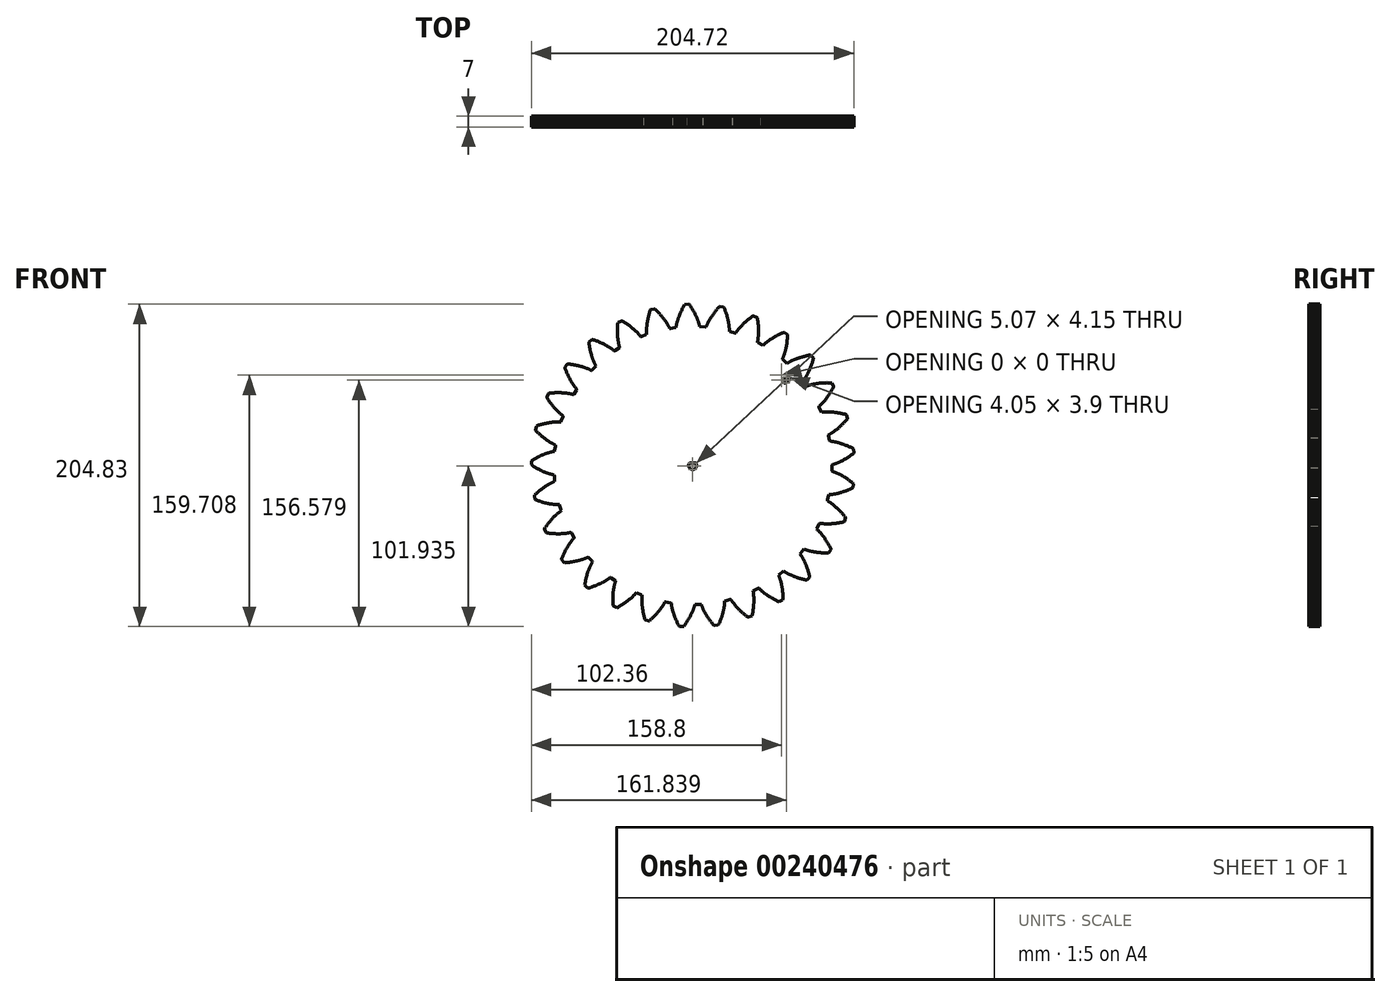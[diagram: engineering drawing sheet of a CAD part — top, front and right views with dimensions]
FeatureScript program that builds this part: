
annotation { "Feature Type Name" : "Feature", "Feature Type Description" : "" }
export const myFeature = defineFeature(function(context is Context, id is Id, definition is map)
    precondition{}
    {
        {
            var Q0;
            Q0=qCreatedBy(makeId("Front.planeOp"),FACE);
            var sketch = newSketch(context, id + "F0", { "sketchPlane" : qUnion([Q0])});
            skLineSegment(sketch, "E0", {"start": v(88.47, -0.08) * mm, "end": v(88.5, 0.43) * mm});
            skLineSegment(sketch, "E1", {"start": v(88.5, 0.43) * mm, "end": v(88.77, 0.5) * mm});
            skLineSegment(sketch, "E2", {"start": v(88.77, 0.5) * mm, "end": v(89.04, 0.58) * mm});
            skLineSegment(sketch, "E3", {"start": v(89.04, 0.58) * mm, "end": v(89.33, 0.67) * mm});
            skLineSegment(sketch, "E4", {"start": v(89.33, 0.67) * mm, "end": v(89.63, 0.76) * mm});
            skLineSegment(sketch, "E5", {"start": v(89.63, 0.76) * mm, "end": v(89.94, 0.86) * mm});
            skLineSegment(sketch, "E6", {"start": v(89.94, 0.86) * mm, "end": v(90.26, 0.97) * mm});
            skLineSegment(sketch, "E7", {"start": v(90.26, 0.97) * mm, "end": v(90.59, 1.09) * mm});
            skLineSegment(sketch, "E8", {"start": v(90.59, 1.09) * mm, "end": v(90.93, 1.21) * mm});
            skLineSegment(sketch, "E9", {"start": v(90.93, 1.21) * mm, "end": v(91.28, 1.35) * mm});
            skLineSegment(sketch, "E10", {"start": v(91.28, 1.35) * mm, "end": v(91.64, 1.5) * mm});
            skLineSegment(sketch, "E11", {"start": v(91.64, 1.5) * mm, "end": v(92, 1.64) * mm});
            skLineSegment(sketch, "E12", {"start": v(92, 1.64) * mm, "end": v(92.38, 1.8) * mm});
            skLineSegment(sketch, "E13", {"start": v(92.38, 1.8) * mm, "end": v(92.77, 1.97) * mm});
            skLineSegment(sketch, "E14", {"start": v(92.77, 1.97) * mm, "end": v(93.17, 2.15) * mm});
            skLineSegment(sketch, "E15", {"start": v(93.17, 2.15) * mm, "end": v(93.58, 2.34) * mm});
            skLineSegment(sketch, "E16", {"start": v(93.58, 2.34) * mm, "end": v(94, 2.54) * mm});
            skLineSegment(sketch, "E17", {"start": v(94, 2.54) * mm, "end": v(94.42, 2.75) * mm});
            skLineSegment(sketch, "E18", {"start": v(94.42, 2.75) * mm, "end": v(94.85, 2.97) * mm});
            skLineSegment(sketch, "E19", {"start": v(94.85, 2.97) * mm, "end": v(95.3, 3.2) * mm});
            skLineSegment(sketch, "E20", {"start": v(95.3, 3.2) * mm, "end": v(95.74, 3.45) * mm});
            skLineSegment(sketch, "E21", {"start": v(95.74, 3.45) * mm, "end": v(96.2, 3.7) * mm});
            skLineSegment(sketch, "E22", {"start": v(96.2, 3.7) * mm, "end": v(96.66, 3.97) * mm});
            skLineSegment(sketch, "E23", {"start": v(96.66, 3.97) * mm, "end": v(97.13, 4.25) * mm});
            skLineSegment(sketch, "E24", {"start": v(97.13, 4.25) * mm, "end": v(97.61, 4.54) * mm});
            skLineSegment(sketch, "E25", {"start": v(97.61, 4.54) * mm, "end": v(98.1, 4.84) * mm});
            skLineSegment(sketch, "E26", {"start": v(98.1, 4.84) * mm, "end": v(98.6, 5.16) * mm});
            skLineSegment(sketch, "E27", {"start": v(98.6, 5.16) * mm, "end": v(99.1, 5.48) * mm});
            skLineSegment(sketch, "E28", {"start": v(99.1, 5.48) * mm, "end": v(99.6, 5.82) * mm});
            skLineSegment(sketch, "E29", {"start": v(99.6, 5.82) * mm, "end": v(100.1, 6.18) * mm});
            skLineSegment(sketch, "E30", {"start": v(100.1, 6.18) * mm, "end": v(100.63, 6.55) * mm});
            skLineSegment(sketch, "E31", {"start": v(100.63, 6.55) * mm, "end": v(101.15, 6.93) * mm});
            skLineSegment(sketch, "E32", {"start": v(101.15, 6.93) * mm, "end": v(101.68, 7.32) * mm});
            skLineSegment(sketch, "E33", {"start": v(101.68, 7.32) * mm, "end": v(102.21, 7.73) * mm});
            skLineSegment(sketch, "E34", {"start": v(102.21, 7.73) * mm, "end": v(102.36, 8.12) * mm});
            skLineSegment(sketch, "E35", {"start": v(102.36, 8.12) * mm, "end": v(102.16, 10.37) * mm});
            skLineSegment(sketch, "E36", {"start": v(102.16, 10.37) * mm, "end": v(101.94, 10.72) * mm});
            skLineSegment(sketch, "E37", {"start": v(101.94, 10.72) * mm, "end": v(101.34, 11.03) * mm});
            skLineSegment(sketch, "E38", {"start": v(101.34, 11.03) * mm, "end": v(100.75, 11.32) * mm});
            skLineSegment(sketch, "E39", {"start": v(100.75, 11.32) * mm, "end": v(100.17, 11.6) * mm});
            skLineSegment(sketch, "E40", {"start": v(100.17, 11.6) * mm, "end": v(99.59, 11.87) * mm});
            skLineSegment(sketch, "E41", {"start": v(99.59, 11.87) * mm, "end": v(99.02, 12.12) * mm});
            skLineSegment(sketch, "E42", {"start": v(99.02, 12.12) * mm, "end": v(98.46, 12.37) * mm});
            skLineSegment(sketch, "E43", {"start": v(98.46, 12.37) * mm, "end": v(97.91, 12.6) * mm});
            skLineSegment(sketch, "E44", {"start": v(97.91, 12.6) * mm, "end": v(97.37, 12.82) * mm});
            skLineSegment(sketch, "E45", {"start": v(97.37, 12.82) * mm, "end": v(96.84, 13.03) * mm});
            skLineSegment(sketch, "E46", {"start": v(96.84, 13.03) * mm, "end": v(96.31, 13.23) * mm});
            skLineSegment(sketch, "E47", {"start": v(96.31, 13.23) * mm, "end": v(95.8, 13.42) * mm});
            skLineSegment(sketch, "E48", {"start": v(95.8, 13.42) * mm, "end": v(95.3, 13.6) * mm});
            skLineSegment(sketch, "E49", {"start": v(95.3, 13.6) * mm, "end": v(94.8, 13.76) * mm});
            skLineSegment(sketch, "E50", {"start": v(94.8, 13.76) * mm, "end": v(94.31, 13.92) * mm});
            skLineSegment(sketch, "E51", {"start": v(94.31, 13.92) * mm, "end": v(93.84, 14.07) * mm});
            skLineSegment(sketch, "E52", {"start": v(93.84, 14.07) * mm, "end": v(93.37, 14.2) * mm});
            skLineSegment(sketch, "E53", {"start": v(93.37, 14.2) * mm, "end": v(92.92, 14.34) * mm});
            skLineSegment(sketch, "E54", {"start": v(92.92, 14.34) * mm, "end": v(92.47, 14.46) * mm});
            skLineSegment(sketch, "E55", {"start": v(92.47, 14.46) * mm, "end": v(92.04, 14.57) * mm});
            skLineSegment(sketch, "E56", {"start": v(92.04, 14.57) * mm, "end": v(91.61, 14.68) * mm});
            skLineSegment(sketch, "E57", {"start": v(91.61, 14.68) * mm, "end": v(91.2, 14.77) * mm});
            skLineSegment(sketch, "E58", {"start": v(91.2, 14.77) * mm, "end": v(90.8, 14.86) * mm});
            skLineSegment(sketch, "E59", {"start": v(90.8, 14.86) * mm, "end": v(90.4, 14.94) * mm});
            skLineSegment(sketch, "E60", {"start": v(90.4, 14.94) * mm, "end": v(90.03, 15.02) * mm});
            skLineSegment(sketch, "E61", {"start": v(90.03, 15.02) * mm, "end": v(89.66, 15.09) * mm});
            skLineSegment(sketch, "E62", {"start": v(89.66, 15.09) * mm, "end": v(89.3, 15.15) * mm});
            skLineSegment(sketch, "E63", {"start": v(89.3, 15.15) * mm, "end": v(88.96, 15.2) * mm});
            skLineSegment(sketch, "E64", {"start": v(88.96, 15.2) * mm, "end": v(88.62, 15.25) * mm});
            skLineSegment(sketch, "E65", {"start": v(88.62, 15.25) * mm, "end": v(88.3, 15.3) * mm});
            skLineSegment(sketch, "E66", {"start": v(88.3, 15.3) * mm, "end": v(88, 15.33) * mm});
            skLineSegment(sketch, "E67", {"start": v(88, 15.33) * mm, "end": v(87.7, 15.37) * mm});
            skLineSegment(sketch, "E68", {"start": v(87.7, 15.37) * mm, "end": v(87.4, 15.4) * mm});
            skLineSegment(sketch, "E69", {"start": v(87.4, 15.4) * mm, "end": v(87.13, 15.42) * mm});
            skLineSegment(sketch, "E70", {"start": v(87.13, 15.42) * mm, "end": v(87, 15.91) * mm});
            skLineSegment(sketch, "E71", {"start": v(87, 15.91) * mm, "end": v(86.4, 18.9) * mm});
            skLineSegment(sketch, "E72", {"start": v(86.4, 18.9) * mm, "end": v(86.33, 19.4) * mm});
            skLineSegment(sketch, "E73", {"start": v(86.33, 19.4) * mm, "end": v(86.57, 19.54) * mm});
            skLineSegment(sketch, "E74", {"start": v(86.57, 19.54) * mm, "end": v(86.82, 19.68) * mm});
            skLineSegment(sketch, "E75", {"start": v(86.82, 19.68) * mm, "end": v(87.08, 19.82) * mm});
            skLineSegment(sketch, "E76", {"start": v(87.08, 19.82) * mm, "end": v(87.36, 19.98) * mm});
            skLineSegment(sketch, "E77", {"start": v(87.36, 19.98) * mm, "end": v(87.64, 20.14) * mm});
            skLineSegment(sketch, "E78", {"start": v(87.64, 20.14) * mm, "end": v(87.92, 20.32) * mm});
            skLineSegment(sketch, "E79", {"start": v(87.92, 20.32) * mm, "end": v(88.22, 20.5) * mm});
            skLineSegment(sketch, "E80", {"start": v(88.22, 20.5) * mm, "end": v(88.53, 20.7) * mm});
            skLineSegment(sketch, "E81", {"start": v(88.53, 20.7) * mm, "end": v(88.84, 20.9) * mm});
            skLineSegment(sketch, "E82", {"start": v(88.84, 20.9) * mm, "end": v(89.16, 21.12) * mm});
            skLineSegment(sketch, "E83", {"start": v(89.16, 21.12) * mm, "end": v(89.49, 21.35) * mm});
            skLineSegment(sketch, "E84", {"start": v(89.49, 21.35) * mm, "end": v(89.82, 21.58) * mm});
            skLineSegment(sketch, "E85", {"start": v(89.82, 21.58) * mm, "end": v(90.17, 21.83) * mm});
            skLineSegment(sketch, "E86", {"start": v(90.17, 21.83) * mm, "end": v(90.52, 22.1) * mm});
            skLineSegment(sketch, "E87", {"start": v(90.52, 22.1) * mm, "end": v(90.87, 22.37) * mm});
            skLineSegment(sketch, "E88", {"start": v(90.87, 22.37) * mm, "end": v(91.24, 22.65) * mm});
            skLineSegment(sketch, "E89", {"start": v(91.24, 22.65) * mm, "end": v(91.6, 22.95) * mm});
            skLineSegment(sketch, "E90", {"start": v(91.6, 22.95) * mm, "end": v(91.98, 23.26) * mm});
            skLineSegment(sketch, "E91", {"start": v(91.98, 23.26) * mm, "end": v(92.36, 23.58) * mm});
            skLineSegment(sketch, "E92", {"start": v(92.36, 23.58) * mm, "end": v(92.75, 23.91) * mm});
            skLineSegment(sketch, "E93", {"start": v(92.75, 23.91) * mm, "end": v(93.14, 24.26) * mm});
            skLineSegment(sketch, "E94", {"start": v(93.14, 24.26) * mm, "end": v(93.54, 24.62) * mm});
            skLineSegment(sketch, "E95", {"start": v(93.54, 24.62) * mm, "end": v(93.94, 25) * mm});
            skLineSegment(sketch, "E96", {"start": v(93.94, 25) * mm, "end": v(94.34, 25.38) * mm});
            skLineSegment(sketch, "E97", {"start": v(94.34, 25.38) * mm, "end": v(94.75, 25.78) * mm});
            skLineSegment(sketch, "E98", {"start": v(94.75, 25.78) * mm, "end": v(95.17, 26.2) * mm});
            skLineSegment(sketch, "E99", {"start": v(95.17, 26.2) * mm, "end": v(95.58, 26.62) * mm});
            skLineSegment(sketch, "E100", {"start": v(95.58, 26.62) * mm, "end": v(96, 27.06) * mm});
            skLineSegment(sketch, "E101", {"start": v(96, 27.06) * mm, "end": v(96.43, 27.52) * mm});
            skLineSegment(sketch, "E102", {"start": v(96.43, 27.52) * mm, "end": v(96.85, 27.99) * mm});
            skLineSegment(sketch, "E103", {"start": v(96.85, 27.99) * mm, "end": v(97.28, 28.47) * mm});
            skLineSegment(sketch, "E104", {"start": v(97.28, 28.47) * mm, "end": v(97.71, 28.97) * mm});
            skLineSegment(sketch, "E105", {"start": v(97.71, 28.97) * mm, "end": v(98.15, 29.48) * mm});
            skLineSegment(sketch, "E106", {"start": v(98.15, 29.48) * mm, "end": v(98.21, 29.9) * mm});
            skLineSegment(sketch, "E107", {"start": v(98.21, 29.9) * mm, "end": v(97.53, 32.05) * mm});
            skLineSegment(sketch, "E108", {"start": v(97.53, 32.05) * mm, "end": v(97.24, 32.35) * mm});
            skLineSegment(sketch, "E109", {"start": v(97.24, 32.35) * mm, "end": v(96.59, 32.52) * mm});
            skLineSegment(sketch, "E110", {"start": v(96.59, 32.52) * mm, "end": v(95.95, 32.68) * mm});
            skLineSegment(sketch, "E111", {"start": v(95.95, 32.68) * mm, "end": v(95.32, 32.82) * mm});
            skLineSegment(sketch, "E112", {"start": v(95.32, 32.82) * mm, "end": v(94.7, 32.96) * mm});
            skLineSegment(sketch, "E113", {"start": v(94.7, 32.96) * mm, "end": v(94.09, 33.1) * mm});
            skLineSegment(sketch, "E114", {"start": v(94.09, 33.1) * mm, "end": v(93.49, 33.2) * mm});
            skLineSegment(sketch, "E115", {"start": v(93.49, 33.2) * mm, "end": v(92.9, 33.31) * mm});
            skLineSegment(sketch, "E116", {"start": v(92.9, 33.31) * mm, "end": v(92.33, 33.41) * mm});
            skLineSegment(sketch, "E117", {"start": v(92.33, 33.41) * mm, "end": v(91.76, 33.5) * mm});
            skLineSegment(sketch, "E118", {"start": v(91.76, 33.5) * mm, "end": v(91.2, 33.59) * mm});
            skLineSegment(sketch, "E119", {"start": v(91.2, 33.59) * mm, "end": v(90.66, 33.66) * mm});
            skLineSegment(sketch, "E120", {"start": v(90.66, 33.66) * mm, "end": v(90.13, 33.72) * mm});
            skLineSegment(sketch, "E121", {"start": v(90.13, 33.72) * mm, "end": v(89.61, 33.78) * mm});
            skLineSegment(sketch, "E122", {"start": v(89.61, 33.78) * mm, "end": v(89.1, 33.83) * mm});
            skLineSegment(sketch, "E123", {"start": v(89.1, 33.83) * mm, "end": v(88.6, 33.87) * mm});
            skLineSegment(sketch, "E124", {"start": v(88.6, 33.87) * mm, "end": v(88.12, 33.91) * mm});
            skLineSegment(sketch, "E125", {"start": v(88.12, 33.91) * mm, "end": v(87.65, 33.94) * mm});
            skLineSegment(sketch, "E126", {"start": v(87.65, 33.94) * mm, "end": v(87.19, 33.96) * mm});
            skLineSegment(sketch, "E127", {"start": v(87.19, 33.96) * mm, "end": v(86.74, 33.98) * mm});
            skLineSegment(sketch, "E128", {"start": v(86.74, 33.98) * mm, "end": v(86.3, 33.99) * mm});
            skLineSegment(sketch, "E129", {"start": v(86.3, 33.99) * mm, "end": v(85.88, 34) * mm});
            skLineSegment(sketch, "E130", {"start": v(85.88, 34) * mm, "end": v(85.47, 34) * mm});
            skLineSegment(sketch, "E131", {"start": v(85.47, 34) * mm, "end": v(85.07, 34) * mm});
            skLineSegment(sketch, "E132", {"start": v(85.07, 34) * mm, "end": v(84.68, 33.98) * mm});
            skLineSegment(sketch, "E133", {"start": v(84.68, 33.98) * mm, "end": v(84.3, 33.97) * mm});
            skLineSegment(sketch, "E134", {"start": v(84.3, 33.97) * mm, "end": v(83.95, 33.95) * mm});
            skLineSegment(sketch, "E135", {"start": v(83.95, 33.95) * mm, "end": v(83.6, 33.93) * mm});
            skLineSegment(sketch, "E136", {"start": v(83.6, 33.93) * mm, "end": v(83.26, 33.91) * mm});
            skLineSegment(sketch, "E137", {"start": v(83.26, 33.91) * mm, "end": v(82.94, 33.88) * mm});
            skLineSegment(sketch, "E138", {"start": v(82.94, 33.88) * mm, "end": v(82.63, 33.85) * mm});
            skLineSegment(sketch, "E139", {"start": v(82.63, 33.85) * mm, "end": v(82.33, 33.82) * mm});
            skLineSegment(sketch, "E140", {"start": v(82.33, 33.82) * mm, "end": v(82.04, 33.79) * mm});
            skLineSegment(sketch, "E141", {"start": v(82.04, 33.79) * mm, "end": v(81.77, 33.75) * mm});
            skLineSegment(sketch, "E142", {"start": v(81.77, 33.75) * mm, "end": v(81.54, 34.2) * mm});
            skLineSegment(sketch, "E143", {"start": v(81.54, 34.2) * mm, "end": v(80.3, 37) * mm});
            skLineSegment(sketch, "E144", {"start": v(80.3, 37) * mm, "end": v(80.12, 37.48) * mm});
            skLineSegment(sketch, "E145", {"start": v(80.12, 37.48) * mm, "end": v(80.33, 37.65) * mm});
            skLineSegment(sketch, "E146", {"start": v(80.33, 37.65) * mm, "end": v(80.55, 37.84) * mm});
            skLineSegment(sketch, "E147", {"start": v(80.55, 37.84) * mm, "end": v(80.77, 38.04) * mm});
            skLineSegment(sketch, "E148", {"start": v(80.77, 38.04) * mm, "end": v(81, 38.25) * mm});
            skLineSegment(sketch, "E149", {"start": v(81, 38.25) * mm, "end": v(81.24, 38.47) * mm});
            skLineSegment(sketch, "E150", {"start": v(81.24, 38.47) * mm, "end": v(81.49, 38.7) * mm});
            skLineSegment(sketch, "E151", {"start": v(81.49, 38.7) * mm, "end": v(81.74, 38.95) * mm});
            skLineSegment(sketch, "E152", {"start": v(81.74, 38.95) * mm, "end": v(82, 39.2) * mm});
            skLineSegment(sketch, "E153", {"start": v(82, 39.2) * mm, "end": v(82.26, 39.47) * mm});
            skLineSegment(sketch, "E154", {"start": v(82.26, 39.47) * mm, "end": v(82.52, 39.75) * mm});
            skLineSegment(sketch, "E155", {"start": v(82.52, 39.75) * mm, "end": v(82.8, 40.05) * mm});
            skLineSegment(sketch, "E156", {"start": v(82.8, 40.05) * mm, "end": v(83.07, 40.35) * mm});
            skLineSegment(sketch, "E157", {"start": v(83.07, 40.35) * mm, "end": v(83.35, 40.67) * mm});
            skLineSegment(sketch, "E158", {"start": v(83.35, 40.67) * mm, "end": v(83.64, 41) * mm});
            skLineSegment(sketch, "E159", {"start": v(83.64, 41) * mm, "end": v(83.93, 41.34) * mm});
            skLineSegment(sketch, "E160", {"start": v(83.93, 41.34) * mm, "end": v(84.22, 41.7) * mm});
            skLineSegment(sketch, "E161", {"start": v(84.22, 41.7) * mm, "end": v(84.52, 42.07) * mm});
            skLineSegment(sketch, "E162", {"start": v(84.52, 42.07) * mm, "end": v(84.82, 42.45) * mm});
            skLineSegment(sketch, "E163", {"start": v(84.82, 42.45) * mm, "end": v(85.12, 42.85) * mm});
            skLineSegment(sketch, "E164", {"start": v(85.12, 42.85) * mm, "end": v(85.43, 43.25) * mm});
            skLineSegment(sketch, "E165", {"start": v(85.43, 43.25) * mm, "end": v(85.73, 43.68) * mm});
            skLineSegment(sketch, "E166", {"start": v(85.73, 43.68) * mm, "end": v(86.04, 44.11) * mm});
            skLineSegment(sketch, "E167", {"start": v(86.04, 44.11) * mm, "end": v(86.36, 44.57) * mm});
            skLineSegment(sketch, "E168", {"start": v(86.36, 44.57) * mm, "end": v(86.67, 45.03) * mm});
            skLineSegment(sketch, "E169", {"start": v(86.67, 45.03) * mm, "end": v(86.98, 45.5) * mm});
            skLineSegment(sketch, "E170", {"start": v(86.98, 45.5) * mm, "end": v(87.3, 46) * mm});
            skLineSegment(sketch, "E171", {"start": v(87.3, 46) * mm, "end": v(87.61, 46.5) * mm});
            skLineSegment(sketch, "E172", {"start": v(87.61, 46.5) * mm, "end": v(87.93, 47.03) * mm});
            skLineSegment(sketch, "E173", {"start": v(87.93, 47.03) * mm, "end": v(88.24, 47.57) * mm});
            skLineSegment(sketch, "E174", {"start": v(88.24, 47.57) * mm, "end": v(88.56, 48.12) * mm});
            skLineSegment(sketch, "E175", {"start": v(88.56, 48.12) * mm, "end": v(88.88, 48.68) * mm});
            skLineSegment(sketch, "E176", {"start": v(88.88, 48.68) * mm, "end": v(89.19, 49.26) * mm});
            skLineSegment(sketch, "E177", {"start": v(89.19, 49.26) * mm, "end": v(89.5, 49.86) * mm});
            skLineSegment(sketch, "E178", {"start": v(89.5, 49.86) * mm, "end": v(89.47, 50.27) * mm});
            skLineSegment(sketch, "E179", {"start": v(89.47, 50.27) * mm, "end": v(88.34, 52.23) * mm});
            skLineSegment(sketch, "E180", {"start": v(88.34, 52.23) * mm, "end": v(88, 52.46) * mm});
            skLineSegment(sketch, "E181", {"start": v(88, 52.46) * mm, "end": v(87.33, 52.48) * mm});
            skLineSegment(sketch, "E182", {"start": v(87.33, 52.48) * mm, "end": v(86.67, 52.5) * mm});
            skLineSegment(sketch, "E183", {"start": v(86.67, 52.5) * mm, "end": v(86.02, 52.51) * mm});
            skLineSegment(sketch, "E184", {"start": v(86.02, 52.51) * mm, "end": v(85.39, 52.51) * mm});
            skLineSegment(sketch, "E185", {"start": v(85.39, 52.51) * mm, "end": v(84.76, 52.5) * mm});
            skLineSegment(sketch, "E186", {"start": v(84.76, 52.5) * mm, "end": v(84.15, 52.5) * mm});
            skLineSegment(sketch, "E187", {"start": v(84.15, 52.5) * mm, "end": v(83.56, 52.47) * mm});
            skLineSegment(sketch, "E188", {"start": v(83.56, 52.47) * mm, "end": v(82.97, 52.44) * mm});
            skLineSegment(sketch, "E189", {"start": v(82.97, 52.44) * mm, "end": v(82.4, 52.41) * mm});
            skLineSegment(sketch, "E190", {"start": v(82.4, 52.41) * mm, "end": v(81.84, 52.37) * mm});
            skLineSegment(sketch, "E191", {"start": v(81.84, 52.37) * mm, "end": v(81.3, 52.32) * mm});
            skLineSegment(sketch, "E192", {"start": v(81.3, 52.32) * mm, "end": v(80.76, 52.27) * mm});
            skLineSegment(sketch, "E193", {"start": v(80.76, 52.27) * mm, "end": v(80.24, 52.22) * mm});
            skLineSegment(sketch, "E194", {"start": v(80.24, 52.22) * mm, "end": v(79.73, 52.16) * mm});
            skLineSegment(sketch, "E195", {"start": v(79.73, 52.16) * mm, "end": v(79.24, 52.1) * mm});
            skLineSegment(sketch, "E196", {"start": v(79.24, 52.1) * mm, "end": v(78.76, 52.02) * mm});
            skLineSegment(sketch, "E197", {"start": v(78.76, 52.02) * mm, "end": v(78.3, 51.95) * mm});
            skLineSegment(sketch, "E198", {"start": v(78.3, 51.95) * mm, "end": v(77.84, 51.87) * mm});
            skLineSegment(sketch, "E199", {"start": v(77.84, 51.87) * mm, "end": v(77.4, 51.8) * mm});
            skLineSegment(sketch, "E200", {"start": v(77.4, 51.8) * mm, "end": v(76.97, 51.71) * mm});
            skLineSegment(sketch, "E201", {"start": v(76.97, 51.71) * mm, "end": v(76.55, 51.63) * mm});
            skLineSegment(sketch, "E202", {"start": v(76.55, 51.63) * mm, "end": v(76.15, 51.54) * mm});
            skLineSegment(sketch, "E203", {"start": v(76.15, 51.54) * mm, "end": v(75.76, 51.45) * mm});
            skLineSegment(sketch, "E204", {"start": v(75.76, 51.45) * mm, "end": v(75.38, 51.36) * mm});
            skLineSegment(sketch, "E205", {"start": v(75.38, 51.36) * mm, "end": v(75.02, 51.26) * mm});
            skLineSegment(sketch, "E206", {"start": v(75.02, 51.26) * mm, "end": v(74.67, 51.17) * mm});
            skLineSegment(sketch, "E207", {"start": v(74.67, 51.17) * mm, "end": v(74.33, 51.07) * mm});
            skLineSegment(sketch, "E208", {"start": v(74.33, 51.07) * mm, "end": v(74.01, 50.98) * mm});
            skLineSegment(sketch, "E209", {"start": v(74.01, 50.98) * mm, "end": v(73.7, 50.88) * mm});
            skLineSegment(sketch, "E210", {"start": v(73.7, 50.88) * mm, "end": v(73.4, 50.79) * mm});
            skLineSegment(sketch, "E211", {"start": v(73.4, 50.79) * mm, "end": v(73.12, 50.7) * mm});
            skLineSegment(sketch, "E212", {"start": v(73.12, 50.7) * mm, "end": v(72.85, 50.6) * mm});
            skLineSegment(sketch, "E213", {"start": v(72.85, 50.6) * mm, "end": v(72.59, 50.5) * mm});
            skLineSegment(sketch, "E214", {"start": v(72.59, 50.5) * mm, "end": v(72.27, 50.9) * mm});
            skLineSegment(sketch, "E215", {"start": v(72.27, 50.9) * mm, "end": v(70.46, 53.36) * mm});
            skLineSegment(sketch, "E216", {"start": v(70.46, 53.36) * mm, "end": v(70.18, 53.79) * mm});
            skLineSegment(sketch, "E217", {"start": v(70.18, 53.79) * mm, "end": v(70.35, 54) * mm});
            skLineSegment(sketch, "E218", {"start": v(70.35, 54) * mm, "end": v(70.52, 54.24) * mm});
            skLineSegment(sketch, "E219", {"start": v(70.52, 54.24) * mm, "end": v(70.7, 54.48) * mm});
            skLineSegment(sketch, "E220", {"start": v(70.7, 54.48) * mm, "end": v(70.88, 54.73) * mm});
            skLineSegment(sketch, "E221", {"start": v(70.88, 54.73) * mm, "end": v(71.06, 55) * mm});
            skLineSegment(sketch, "E222", {"start": v(71.06, 55) * mm, "end": v(71.25, 55.28) * mm});
            skLineSegment(sketch, "E223", {"start": v(71.25, 55.28) * mm, "end": v(71.44, 55.57) * mm});
            skLineSegment(sketch, "E224", {"start": v(71.44, 55.57) * mm, "end": v(71.64, 55.88) * mm});
            skLineSegment(sketch, "E225", {"start": v(71.64, 55.88) * mm, "end": v(71.84, 56.2) * mm});
            skLineSegment(sketch, "E226", {"start": v(71.84, 56.2) * mm, "end": v(72.03, 56.53) * mm});
            skLineSegment(sketch, "E227", {"start": v(72.03, 56.53) * mm, "end": v(72.24, 56.87) * mm});
            skLineSegment(sketch, "E228", {"start": v(72.24, 56.87) * mm, "end": v(72.44, 57.23) * mm});
            skLineSegment(sketch, "E229", {"start": v(72.44, 57.23) * mm, "end": v(72.65, 57.6) * mm});
            skLineSegment(sketch, "E230", {"start": v(72.65, 57.6) * mm, "end": v(72.86, 57.98) * mm});
            skLineSegment(sketch, "E231", {"start": v(72.86, 57.98) * mm, "end": v(73.07, 58.38) * mm});
            skLineSegment(sketch, "E232", {"start": v(73.07, 58.38) * mm, "end": v(73.28, 58.8) * mm});
            skLineSegment(sketch, "E233", {"start": v(73.28, 58.8) * mm, "end": v(73.49, 59.21) * mm});
            skLineSegment(sketch, "E234", {"start": v(73.49, 59.21) * mm, "end": v(73.7, 59.65) * mm});
            skLineSegment(sketch, "E235", {"start": v(73.7, 59.65) * mm, "end": v(73.9, 60.1) * mm});
            skLineSegment(sketch, "E236", {"start": v(73.9, 60.1) * mm, "end": v(74.12, 60.57) * mm});
            skLineSegment(sketch, "E237", {"start": v(74.12, 60.57) * mm, "end": v(74.33, 61.05) * mm});
            skLineSegment(sketch, "E238", {"start": v(74.33, 61.05) * mm, "end": v(74.54, 61.54) * mm});
            skLineSegment(sketch, "E239", {"start": v(74.54, 61.54) * mm, "end": v(74.74, 62.05) * mm});
            skLineSegment(sketch, "E240", {"start": v(74.74, 62.05) * mm, "end": v(74.95, 62.57) * mm});
            skLineSegment(sketch, "E241", {"start": v(74.95, 62.57) * mm, "end": v(75.15, 63.1) * mm});
            skLineSegment(sketch, "E242", {"start": v(75.15, 63.1) * mm, "end": v(75.35, 63.66) * mm});
            skLineSegment(sketch, "E243", {"start": v(75.35, 63.66) * mm, "end": v(75.55, 64.22) * mm});
            skLineSegment(sketch, "E244", {"start": v(75.55, 64.22) * mm, "end": v(75.75, 64.8) * mm});
            skLineSegment(sketch, "E245", {"start": v(75.75, 64.8) * mm, "end": v(75.94, 65.39) * mm});
            skLineSegment(sketch, "E246", {"start": v(75.94, 65.39) * mm, "end": v(76.13, 66) * mm});
            skLineSegment(sketch, "E247", {"start": v(76.13, 66) * mm, "end": v(76.32, 66.61) * mm});
            skLineSegment(sketch, "E248", {"start": v(76.32, 66.61) * mm, "end": v(76.5, 67.24) * mm});
            skLineSegment(sketch, "E249", {"start": v(76.5, 67.24) * mm, "end": v(76.68, 67.9) * mm});
            skLineSegment(sketch, "E250", {"start": v(76.68, 67.9) * mm, "end": v(76.56, 68.3) * mm});
            skLineSegment(sketch, "E251", {"start": v(76.56, 68.3) * mm, "end": v(75.04, 69.96) * mm});
            skLineSegment(sketch, "E252", {"start": v(75.04, 69.96) * mm, "end": v(74.65, 70.11) * mm});
            skLineSegment(sketch, "E253", {"start": v(74.65, 70.11) * mm, "end": v(73.99, 70) * mm});
            skLineSegment(sketch, "E254", {"start": v(73.99, 70) * mm, "end": v(73.34, 69.87) * mm});
            skLineSegment(sketch, "E255", {"start": v(73.34, 69.87) * mm, "end": v(72.7, 69.74) * mm});
            skLineSegment(sketch, "E256", {"start": v(72.7, 69.74) * mm, "end": v(72.09, 69.6) * mm});
            skLineSegment(sketch, "E257", {"start": v(72.09, 69.6) * mm, "end": v(71.48, 69.46) * mm});
            skLineSegment(sketch, "E258", {"start": v(71.48, 69.46) * mm, "end": v(70.89, 69.32) * mm});
            skLineSegment(sketch, "E259", {"start": v(70.89, 69.32) * mm, "end": v(70.3, 69.17) * mm});
            skLineSegment(sketch, "E260", {"start": v(70.3, 69.17) * mm, "end": v(69.74, 69.02) * mm});
            skLineSegment(sketch, "E261", {"start": v(69.74, 69.02) * mm, "end": v(69.2, 68.86) * mm});
            skLineSegment(sketch, "E262", {"start": v(69.2, 68.86) * mm, "end": v(68.66, 68.7) * mm});
            skLineSegment(sketch, "E263", {"start": v(68.66, 68.7) * mm, "end": v(68.13, 68.54) * mm});
            skLineSegment(sketch, "E264", {"start": v(68.13, 68.54) * mm, "end": v(67.62, 68.38) * mm});
            skLineSegment(sketch, "E265", {"start": v(67.62, 68.38) * mm, "end": v(67.13, 68.21) * mm});
            skLineSegment(sketch, "E266", {"start": v(67.13, 68.21) * mm, "end": v(66.65, 68.04) * mm});
            skLineSegment(sketch, "E267", {"start": v(66.65, 68.04) * mm, "end": v(66.18, 67.87) * mm});
            skLineSegment(sketch, "E268", {"start": v(66.18, 67.87) * mm, "end": v(65.72, 67.7) * mm});
            skLineSegment(sketch, "E269", {"start": v(65.72, 67.7) * mm, "end": v(65.28, 67.53) * mm});
            skLineSegment(sketch, "E270", {"start": v(65.28, 67.53) * mm, "end": v(64.85, 67.36) * mm});
            skLineSegment(sketch, "E271", {"start": v(64.85, 67.36) * mm, "end": v(64.44, 67.18) * mm});
            skLineSegment(sketch, "E272", {"start": v(64.44, 67.18) * mm, "end": v(64.04, 67.01) * mm});
            skLineSegment(sketch, "E273", {"start": v(64.04, 67.01) * mm, "end": v(63.65, 66.84) * mm});
            skLineSegment(sketch, "E274", {"start": v(63.65, 66.84) * mm, "end": v(63.28, 66.67) * mm});
            skLineSegment(sketch, "E275", {"start": v(63.28, 66.67) * mm, "end": v(62.92, 66.5) * mm});
            skLineSegment(sketch, "E276", {"start": v(62.92, 66.5) * mm, "end": v(62.57, 66.32) * mm});
            skLineSegment(sketch, "E277", {"start": v(62.57, 66.32) * mm, "end": v(62.23, 66.15) * mm});
            skLineSegment(sketch, "E278", {"start": v(62.23, 66.15) * mm, "end": v(61.91, 65.99) * mm});
            skLineSegment(sketch, "E279", {"start": v(61.91, 65.99) * mm, "end": v(61.6, 65.82) * mm});
            skLineSegment(sketch, "E280", {"start": v(61.6, 65.82) * mm, "end": v(61.3, 65.66) * mm});
            skLineSegment(sketch, "E281", {"start": v(61.3, 65.66) * mm, "end": v(61.03, 65.5) * mm});
            skLineSegment(sketch, "E282", {"start": v(61.03, 65.5) * mm, "end": v(60.76, 65.34) * mm});
            skLineSegment(sketch, "E283", {"start": v(60.76, 65.34) * mm, "end": v(60.5, 65.19) * mm});
            skLineSegment(sketch, "E284", {"start": v(60.5, 65.19) * mm, "end": v(60.25, 65.04) * mm});
            skLineSegment(sketch, "E285", {"start": v(60.25, 65.04) * mm, "end": v(60.02, 64.89) * mm});
            skLineSegment(sketch, "E286", {"start": v(60.02, 64.89) * mm, "end": v(59.63, 65.2) * mm});
            skLineSegment(sketch, "E287", {"start": v(59.63, 65.2) * mm, "end": v(57.33, 67.23) * mm});
            skLineSegment(sketch, "E288", {"start": v(57.33, 67.23) * mm, "end": v(56.96, 67.58) * mm});
            skLineSegment(sketch, "E289", {"start": v(56.96, 67.58) * mm, "end": v(57.08, 67.83) * mm});
            skLineSegment(sketch, "E290", {"start": v(57.08, 67.83) * mm, "end": v(57.2, 68.1) * mm});
            skLineSegment(sketch, "E291", {"start": v(57.2, 68.1) * mm, "end": v(57.32, 68.37) * mm});
            skLineSegment(sketch, "E292", {"start": v(57.32, 68.37) * mm, "end": v(57.44, 68.65) * mm});
            skLineSegment(sketch, "E293", {"start": v(57.44, 68.65) * mm, "end": v(57.56, 68.96) * mm});
            skLineSegment(sketch, "E294", {"start": v(57.56, 68.96) * mm, "end": v(57.69, 69.27) * mm});
            skLineSegment(sketch, "E295", {"start": v(57.69, 69.27) * mm, "end": v(57.81, 69.6) * mm});
            skLineSegment(sketch, "E296", {"start": v(57.81, 69.6) * mm, "end": v(57.94, 69.93) * mm});
            skLineSegment(sketch, "E297", {"start": v(57.94, 69.93) * mm, "end": v(58.06, 70.29) * mm});
            skLineSegment(sketch, "E298", {"start": v(58.06, 70.29) * mm, "end": v(58.19, 70.65) * mm});
            skLineSegment(sketch, "E299", {"start": v(58.19, 70.65) * mm, "end": v(58.31, 71.03) * mm});
            skLineSegment(sketch, "E300", {"start": v(58.31, 71.03) * mm, "end": v(58.43, 71.43) * mm});
            skLineSegment(sketch, "E301", {"start": v(58.43, 71.43) * mm, "end": v(58.56, 71.83) * mm});
            skLineSegment(sketch, "E302", {"start": v(58.56, 71.83) * mm, "end": v(58.68, 72.25) * mm});
            skLineSegment(sketch, "E303", {"start": v(58.68, 72.25) * mm, "end": v(58.8, 72.69) * mm});
            skLineSegment(sketch, "E304", {"start": v(58.8, 72.69) * mm, "end": v(58.91, 73.13) * mm});
            skLineSegment(sketch, "E305", {"start": v(58.91, 73.13) * mm, "end": v(59.03, 73.6) * mm});
            skLineSegment(sketch, "E306", {"start": v(59.03, 73.6) * mm, "end": v(59.14, 74.06) * mm});
            skLineSegment(sketch, "E307", {"start": v(59.14, 74.06) * mm, "end": v(59.25, 74.55) * mm});
            skLineSegment(sketch, "E308", {"start": v(59.25, 74.55) * mm, "end": v(59.35, 75.05) * mm});
            skLineSegment(sketch, "E309", {"start": v(59.35, 75.05) * mm, "end": v(59.45, 75.56) * mm});
            skLineSegment(sketch, "E310", {"start": v(59.45, 75.56) * mm, "end": v(59.55, 76.1) * mm});
            skLineSegment(sketch, "E311", {"start": v(59.55, 76.1) * mm, "end": v(59.64, 76.63) * mm});
            skLineSegment(sketch, "E312", {"start": v(59.64, 76.63) * mm, "end": v(59.73, 77.18) * mm});
            skLineSegment(sketch, "E313", {"start": v(59.73, 77.18) * mm, "end": v(59.82, 77.75) * mm});
            skLineSegment(sketch, "E314", {"start": v(59.82, 77.75) * mm, "end": v(59.9, 78.33) * mm});
            skLineSegment(sketch, "E315", {"start": v(59.9, 78.33) * mm, "end": v(59.97, 78.92) * mm});
            skLineSegment(sketch, "E316", {"start": v(59.97, 78.92) * mm, "end": v(60.04, 79.53) * mm});
            skLineSegment(sketch, "E317", {"start": v(60.04, 79.53) * mm, "end": v(60.1, 80.15) * mm});
            skLineSegment(sketch, "E318", {"start": v(60.1, 80.15) * mm, "end": v(60.15, 80.78) * mm});
            skLineSegment(sketch, "E319", {"start": v(60.15, 80.78) * mm, "end": v(60.2, 81.42) * mm});
            skLineSegment(sketch, "E320", {"start": v(60.2, 81.42) * mm, "end": v(60.25, 82.08) * mm});
            skLineSegment(sketch, "E321", {"start": v(60.25, 82.08) * mm, "end": v(60.28, 82.75) * mm});
            skLineSegment(sketch, "E322", {"start": v(60.28, 82.75) * mm, "end": v(60.08, 83.12) * mm});
            skLineSegment(sketch, "E323", {"start": v(60.08, 83.12) * mm, "end": v(58.23, 84.42) * mm});
            skLineSegment(sketch, "E324", {"start": v(58.23, 84.42) * mm, "end": v(57.82, 84.48) * mm});
            skLineSegment(sketch, "E325", {"start": v(57.82, 84.48) * mm, "end": v(57.2, 84.23) * mm});
            skLineSegment(sketch, "E326", {"start": v(57.2, 84.23) * mm, "end": v(56.6, 83.96) * mm});
            skLineSegment(sketch, "E327", {"start": v(56.6, 83.96) * mm, "end": v(56, 83.7) * mm});
            skLineSegment(sketch, "E328", {"start": v(56, 83.7) * mm, "end": v(55.43, 83.44) * mm});
            skLineSegment(sketch, "E329", {"start": v(55.43, 83.44) * mm, "end": v(54.86, 83.17) * mm});
            skLineSegment(sketch, "E330", {"start": v(54.86, 83.17) * mm, "end": v(54.32, 82.9) * mm});
            skLineSegment(sketch, "E331", {"start": v(54.32, 82.9) * mm, "end": v(53.78, 82.63) * mm});
            skLineSegment(sketch, "E332", {"start": v(53.78, 82.63) * mm, "end": v(53.27, 82.36) * mm});
            skLineSegment(sketch, "E333", {"start": v(53.27, 82.36) * mm, "end": v(52.76, 82.09) * mm});
            skLineSegment(sketch, "E334", {"start": v(52.76, 82.09) * mm, "end": v(52.27, 81.82) * mm});
            skLineSegment(sketch, "E335", {"start": v(52.27, 81.82) * mm, "end": v(51.8, 81.55) * mm});
            skLineSegment(sketch, "E336", {"start": v(51.8, 81.55) * mm, "end": v(51.33, 81.28) * mm});
            skLineSegment(sketch, "E337", {"start": v(51.33, 81.28) * mm, "end": v(50.88, 81) * mm});
            skLineSegment(sketch, "E338", {"start": v(50.88, 81) * mm, "end": v(50.45, 80.74) * mm});
            skLineSegment(sketch, "E339", {"start": v(50.45, 80.74) * mm, "end": v(50.03, 80.48) * mm});
            skLineSegment(sketch, "E340", {"start": v(50.03, 80.48) * mm, "end": v(49.62, 80.21) * mm});
            skLineSegment(sketch, "E341", {"start": v(49.62, 80.21) * mm, "end": v(49.23, 79.95) * mm});
            skLineSegment(sketch, "E342", {"start": v(49.23, 79.95) * mm, "end": v(48.84, 79.69) * mm});
            skLineSegment(sketch, "E343", {"start": v(48.84, 79.69) * mm, "end": v(48.48, 79.43) * mm});
            skLineSegment(sketch, "E344", {"start": v(48.48, 79.43) * mm, "end": v(48.12, 79.17) * mm});
            skLineSegment(sketch, "E345", {"start": v(48.12, 79.17) * mm, "end": v(47.78, 78.92) * mm});
            skLineSegment(sketch, "E346", {"start": v(47.78, 78.92) * mm, "end": v(47.45, 78.67) * mm});
            skLineSegment(sketch, "E347", {"start": v(47.45, 78.67) * mm, "end": v(47.14, 78.43) * mm});
            skLineSegment(sketch, "E348", {"start": v(47.14, 78.43) * mm, "end": v(46.84, 78.19) * mm});
            skLineSegment(sketch, "E349", {"start": v(46.84, 78.19) * mm, "end": v(46.55, 77.95) * mm});
            skLineSegment(sketch, "E350", {"start": v(46.55, 77.95) * mm, "end": v(46.27, 77.72) * mm});
            skLineSegment(sketch, "E351", {"start": v(46.27, 77.72) * mm, "end": v(46, 77.5) * mm});
            skLineSegment(sketch, "E352", {"start": v(46, 77.5) * mm, "end": v(45.75, 77.27) * mm});
            skLineSegment(sketch, "E353", {"start": v(45.75, 77.27) * mm, "end": v(45.5, 77.05) * mm});
            skLineSegment(sketch, "E354", {"start": v(45.5, 77.05) * mm, "end": v(45.28, 76.84) * mm});
            skLineSegment(sketch, "E355", {"start": v(45.28, 76.84) * mm, "end": v(45.06, 76.63) * mm});
            skLineSegment(sketch, "E356", {"start": v(45.06, 76.63) * mm, "end": v(44.85, 76.43) * mm});
            skLineSegment(sketch, "E357", {"start": v(44.85, 76.43) * mm, "end": v(44.66, 76.24) * mm});
            skLineSegment(sketch, "E358", {"start": v(44.66, 76.24) * mm, "end": v(44.2, 76.46) * mm});
            skLineSegment(sketch, "E359", {"start": v(44.2, 76.46) * mm, "end": v(41.53, 77.94) * mm});
            skLineSegment(sketch, "E360", {"start": v(41.53, 77.94) * mm, "end": v(41.1, 78.2) * mm});
            skLineSegment(sketch, "E361", {"start": v(41.1, 78.2) * mm, "end": v(41.15, 78.48) * mm});
            skLineSegment(sketch, "E362", {"start": v(41.15, 78.48) * mm, "end": v(41.21, 78.76) * mm});
            skLineSegment(sketch, "E363", {"start": v(41.21, 78.76) * mm, "end": v(41.27, 79.05) * mm});
            skLineSegment(sketch, "E364", {"start": v(41.27, 79.05) * mm, "end": v(41.33, 79.36) * mm});
            skLineSegment(sketch, "E365", {"start": v(41.33, 79.36) * mm, "end": v(41.38, 79.68) * mm});
            skLineSegment(sketch, "E366", {"start": v(41.38, 79.68) * mm, "end": v(41.44, 80.01) * mm});
            skLineSegment(sketch, "E367", {"start": v(41.44, 80.01) * mm, "end": v(41.49, 80.36) * mm});
            skLineSegment(sketch, "E368", {"start": v(41.49, 80.36) * mm, "end": v(41.54, 80.72) * mm});
            skLineSegment(sketch, "E369", {"start": v(41.54, 80.72) * mm, "end": v(41.58, 81.09) * mm});
            skLineSegment(sketch, "E370", {"start": v(41.58, 81.09) * mm, "end": v(41.63, 81.47) * mm});
            skLineSegment(sketch, "E371", {"start": v(41.63, 81.47) * mm, "end": v(41.66, 81.87) * mm});
            skLineSegment(sketch, "E372", {"start": v(41.66, 81.87) * mm, "end": v(41.7, 82.28) * mm});
            skLineSegment(sketch, "E373", {"start": v(41.7, 82.28) * mm, "end": v(41.73, 82.7) * mm});
            skLineSegment(sketch, "E374", {"start": v(41.73, 82.7) * mm, "end": v(41.76, 83.14) * mm});
            skLineSegment(sketch, "E375", {"start": v(41.76, 83.14) * mm, "end": v(41.78, 83.59) * mm});
            skLineSegment(sketch, "E376", {"start": v(41.78, 83.59) * mm, "end": v(41.8, 84.05) * mm});
            skLineSegment(sketch, "E377", {"start": v(41.8, 84.05) * mm, "end": v(41.81, 84.52) * mm});
            skLineSegment(sketch, "E378", {"start": v(41.81, 84.52) * mm, "end": v(41.82, 85) * mm});
            skLineSegment(sketch, "E379", {"start": v(41.82, 85) * mm, "end": v(41.82, 85.5) * mm});
            skLineSegment(sketch, "E380", {"start": v(41.82, 85.5) * mm, "end": v(41.82, 86.02) * mm});
            skLineSegment(sketch, "E381", {"start": v(41.82, 86.02) * mm, "end": v(41.8, 86.54) * mm});
            skLineSegment(sketch, "E382", {"start": v(41.8, 86.54) * mm, "end": v(41.79, 87.08) * mm});
            skLineSegment(sketch, "E383", {"start": v(41.79, 87.08) * mm, "end": v(41.77, 87.62) * mm});
            skLineSegment(sketch, "E384", {"start": v(41.77, 87.62) * mm, "end": v(41.73, 88.18) * mm});
            skLineSegment(sketch, "E385", {"start": v(41.73, 88.18) * mm, "end": v(41.7, 88.75) * mm});
            skLineSegment(sketch, "E386", {"start": v(41.7, 88.75) * mm, "end": v(41.65, 89.34) * mm});
            skLineSegment(sketch, "E387", {"start": v(41.65, 89.34) * mm, "end": v(41.6, 89.93) * mm});
            skLineSegment(sketch, "E388", {"start": v(41.6, 89.93) * mm, "end": v(41.53, 90.54) * mm});
            skLineSegment(sketch, "E389", {"start": v(41.53, 90.54) * mm, "end": v(41.45, 91.16) * mm});
            skLineSegment(sketch, "E390", {"start": v(41.45, 91.16) * mm, "end": v(41.37, 91.79) * mm});
            skLineSegment(sketch, "E391", {"start": v(41.37, 91.79) * mm, "end": v(41.28, 92.43) * mm});
            skLineSegment(sketch, "E392", {"start": v(41.28, 92.43) * mm, "end": v(41.18, 93.08) * mm});
            skLineSegment(sketch, "E393", {"start": v(41.18, 93.08) * mm, "end": v(41.07, 93.74) * mm});
            skLineSegment(sketch, "E394", {"start": v(41.07, 93.74) * mm, "end": v(40.8, 94.06) * mm});
            skLineSegment(sketch, "E395", {"start": v(40.8, 94.06) * mm, "end": v(38.71, 94.93) * mm});
            skLineSegment(sketch, "E396", {"start": v(38.71, 94.93) * mm, "end": v(38.3, 94.9) * mm});
            skLineSegment(sketch, "E397", {"start": v(38.3, 94.9) * mm, "end": v(37.74, 94.52) * mm});
            skLineSegment(sketch, "E398", {"start": v(37.74, 94.52) * mm, "end": v(37.2, 94.13) * mm});
            skLineSegment(sketch, "E399", {"start": v(37.2, 94.13) * mm, "end": v(36.69, 93.75) * mm});
            skLineSegment(sketch, "E400", {"start": v(36.69, 93.75) * mm, "end": v(36.18, 93.36) * mm});
            skLineSegment(sketch, "E401", {"start": v(36.18, 93.36) * mm, "end": v(35.7, 92.98) * mm});
            skLineSegment(sketch, "E402", {"start": v(35.7, 92.98) * mm, "end": v(35.21, 92.6) * mm});
            skLineSegment(sketch, "E403", {"start": v(35.21, 92.6) * mm, "end": v(34.75, 92.22) * mm});
            skLineSegment(sketch, "E404", {"start": v(34.75, 92.22) * mm, "end": v(34.3, 91.85) * mm});
            skLineSegment(sketch, "E405", {"start": v(34.3, 91.85) * mm, "end": v(33.87, 91.48) * mm});
            skLineSegment(sketch, "E406", {"start": v(33.87, 91.48) * mm, "end": v(33.45, 91.1) * mm});
            skLineSegment(sketch, "E407", {"start": v(33.45, 91.1) * mm, "end": v(33.04, 90.74) * mm});
            skLineSegment(sketch, "E408", {"start": v(33.04, 90.74) * mm, "end": v(32.65, 90.38) * mm});
            skLineSegment(sketch, "E409", {"start": v(32.65, 90.38) * mm, "end": v(32.27, 90.02) * mm});
            skLineSegment(sketch, "E410", {"start": v(32.27, 90.02) * mm, "end": v(31.9, 89.66) * mm});
            skLineSegment(sketch, "E411", {"start": v(31.9, 89.66) * mm, "end": v(31.54, 89.31) * mm});
            skLineSegment(sketch, "E412", {"start": v(31.54, 89.31) * mm, "end": v(31.2, 88.96) * mm});
            skLineSegment(sketch, "E413", {"start": v(31.2, 88.96) * mm, "end": v(30.88, 88.62) * mm});
            skLineSegment(sketch, "E414", {"start": v(30.88, 88.62) * mm, "end": v(30.56, 88.29) * mm});
            skLineSegment(sketch, "E415", {"start": v(30.56, 88.29) * mm, "end": v(30.26, 87.96) * mm});
            skLineSegment(sketch, "E416", {"start": v(30.26, 87.96) * mm, "end": v(29.96, 87.63) * mm});
            skLineSegment(sketch, "E417", {"start": v(29.96, 87.63) * mm, "end": v(29.69, 87.31) * mm});
            skLineSegment(sketch, "E418", {"start": v(29.69, 87.31) * mm, "end": v(29.42, 87) * mm});
            skLineSegment(sketch, "E419", {"start": v(29.42, 87) * mm, "end": v(29.16, 86.7) * mm});
            skLineSegment(sketch, "E420", {"start": v(29.16, 86.7) * mm, "end": v(28.92, 86.4) * mm});
            skLineSegment(sketch, "E421", {"start": v(28.92, 86.4) * mm, "end": v(28.69, 86.1) * mm});
            skLineSegment(sketch, "E422", {"start": v(28.69, 86.1) * mm, "end": v(28.47, 85.8) * mm});
            skLineSegment(sketch, "E423", {"start": v(28.47, 85.8) * mm, "end": v(28.26, 85.53) * mm});
            skLineSegment(sketch, "E424", {"start": v(28.26, 85.53) * mm, "end": v(28.06, 85.26) * mm});
            skLineSegment(sketch, "E425", {"start": v(28.06, 85.26) * mm, "end": v(27.87, 85) * mm});
            skLineSegment(sketch, "E426", {"start": v(27.87, 85) * mm, "end": v(27.69, 84.74) * mm});
            skLineSegment(sketch, "E427", {"start": v(27.69, 84.74) * mm, "end": v(27.52, 84.49) * mm});
            skLineSegment(sketch, "E428", {"start": v(27.52, 84.49) * mm, "end": v(27.36, 84.25) * mm});
            skLineSegment(sketch, "E429", {"start": v(27.36, 84.25) * mm, "end": v(27.21, 84.02) * mm});
            skLineSegment(sketch, "E430", {"start": v(27.21, 84.02) * mm, "end": v(26.72, 84.14) * mm});
            skLineSegment(sketch, "E431", {"start": v(26.72, 84.14) * mm, "end": v(23.79, 85) * mm});
            skLineSegment(sketch, "E432", {"start": v(23.79, 85) * mm, "end": v(23.3, 85.18) * mm});
            skLineSegment(sketch, "E433", {"start": v(23.3, 85.18) * mm, "end": v(23.3, 85.45) * mm});
            skLineSegment(sketch, "E434", {"start": v(23.3, 85.45) * mm, "end": v(23.3, 85.74) * mm});
            skLineSegment(sketch, "E435", {"start": v(23.3, 85.74) * mm, "end": v(23.3, 86.04) * mm});
            skLineSegment(sketch, "E436", {"start": v(23.3, 86.04) * mm, "end": v(23.29, 86.35) * mm});
            skLineSegment(sketch, "E437", {"start": v(23.29, 86.35) * mm, "end": v(23.27, 86.68) * mm});
            skLineSegment(sketch, "E438", {"start": v(23.27, 86.68) * mm, "end": v(23.25, 87.01) * mm});
            skLineSegment(sketch, "E439", {"start": v(23.25, 87.01) * mm, "end": v(23.23, 87.36) * mm});
            skLineSegment(sketch, "E440", {"start": v(23.23, 87.36) * mm, "end": v(23.2, 87.72) * mm});
            skLineSegment(sketch, "E441", {"start": v(23.2, 87.72) * mm, "end": v(23.17, 88.1) * mm});
            skLineSegment(sketch, "E442", {"start": v(23.17, 88.1) * mm, "end": v(23.13, 88.48) * mm});
            skLineSegment(sketch, "E443", {"start": v(23.13, 88.48) * mm, "end": v(23.08, 88.88) * mm});
            skLineSegment(sketch, "E444", {"start": v(23.08, 88.88) * mm, "end": v(23.03, 89.29) * mm});
            skLineSegment(sketch, "E445", {"start": v(23.03, 89.29) * mm, "end": v(22.97, 89.7) * mm});
            skLineSegment(sketch, "E446", {"start": v(22.97, 89.7) * mm, "end": v(22.9, 90.14) * mm});
            skLineSegment(sketch, "E447", {"start": v(22.9, 90.14) * mm, "end": v(22.83, 90.58) * mm});
            skLineSegment(sketch, "E448", {"start": v(22.83, 90.58) * mm, "end": v(22.74, 91.03) * mm});
            skLineSegment(sketch, "E449", {"start": v(22.74, 91.03) * mm, "end": v(22.65, 91.5) * mm});
            skLineSegment(sketch, "E450", {"start": v(22.65, 91.5) * mm, "end": v(22.56, 91.98) * mm});
            skLineSegment(sketch, "E451", {"start": v(22.56, 91.98) * mm, "end": v(22.45, 92.46) * mm});
            skLineSegment(sketch, "E452", {"start": v(22.45, 92.46) * mm, "end": v(22.34, 92.96) * mm});
            skLineSegment(sketch, "E453", {"start": v(22.34, 92.96) * mm, "end": v(22.21, 93.47) * mm});
            skLineSegment(sketch, "E454", {"start": v(22.21, 93.47) * mm, "end": v(22.08, 93.99) * mm});
            skLineSegment(sketch, "E455", {"start": v(22.08, 93.99) * mm, "end": v(21.94, 94.52) * mm});
            skLineSegment(sketch, "E456", {"start": v(21.94, 94.52) * mm, "end": v(21.79, 95.06) * mm});
            skLineSegment(sketch, "E457", {"start": v(21.79, 95.06) * mm, "end": v(21.63, 95.6) * mm});
            skLineSegment(sketch, "E458", {"start": v(21.63, 95.6) * mm, "end": v(21.45, 96.16) * mm});
            skLineSegment(sketch, "E459", {"start": v(21.45, 96.16) * mm, "end": v(21.27, 96.73) * mm});
            skLineSegment(sketch, "E460", {"start": v(21.27, 96.73) * mm, "end": v(21.08, 97.31) * mm});
            skLineSegment(sketch, "E461", {"start": v(21.08, 97.31) * mm, "end": v(20.88, 97.9) * mm});
            skLineSegment(sketch, "E462", {"start": v(20.88, 97.9) * mm, "end": v(20.66, 98.5) * mm});
            skLineSegment(sketch, "E463", {"start": v(20.66, 98.5) * mm, "end": v(20.43, 99.1) * mm});
            skLineSegment(sketch, "E464", {"start": v(20.43, 99.1) * mm, "end": v(20.2, 99.72) * mm});
            skLineSegment(sketch, "E465", {"start": v(20.2, 99.72) * mm, "end": v(19.94, 100.34) * mm});
            skLineSegment(sketch, "E466", {"start": v(19.94, 100.34) * mm, "end": v(19.6, 100.59) * mm});
            skLineSegment(sketch, "E467", {"start": v(19.6, 100.59) * mm, "end": v(17.39, 101) * mm});
            skLineSegment(sketch, "E468", {"start": v(17.39, 101) * mm, "end": v(16.98, 100.88) * mm});
            skLineSegment(sketch, "E469", {"start": v(16.98, 100.88) * mm, "end": v(16.53, 100.38) * mm});
            skLineSegment(sketch, "E470", {"start": v(16.53, 100.38) * mm, "end": v(16.1, 99.9) * mm});
            skLineSegment(sketch, "E471", {"start": v(16.1, 99.9) * mm, "end": v(15.66, 99.4) * mm});
            skLineSegment(sketch, "E472", {"start": v(15.66, 99.4) * mm, "end": v(15.25, 98.92) * mm});
            skLineSegment(sketch, "E473", {"start": v(15.25, 98.92) * mm, "end": v(14.86, 98.44) * mm});
            skLineSegment(sketch, "E474", {"start": v(14.86, 98.44) * mm, "end": v(14.47, 97.97) * mm});
            skLineSegment(sketch, "E475", {"start": v(14.47, 97.97) * mm, "end": v(14.1, 97.5) * mm});
            skLineSegment(sketch, "E476", {"start": v(14.1, 97.5) * mm, "end": v(13.74, 97.04) * mm});
            skLineSegment(sketch, "E477", {"start": v(13.74, 97.04) * mm, "end": v(13.4, 96.58) * mm});
            skLineSegment(sketch, "E478", {"start": v(13.4, 96.58) * mm, "end": v(13.07, 96.13) * mm});
            skLineSegment(sketch, "E479", {"start": v(13.07, 96.13) * mm, "end": v(12.75, 95.68) * mm});
            skLineSegment(sketch, "E480", {"start": v(12.75, 95.68) * mm, "end": v(12.44, 95.24) * mm});
            skLineSegment(sketch, "E481", {"start": v(12.44, 95.24) * mm, "end": v(12.15, 94.81) * mm});
            skLineSegment(sketch, "E482", {"start": v(12.15, 94.81) * mm, "end": v(11.87, 94.39) * mm});
            skLineSegment(sketch, "E483", {"start": v(11.87, 94.39) * mm, "end": v(11.6, 93.97) * mm});
            skLineSegment(sketch, "E484", {"start": v(11.6, 93.97) * mm, "end": v(11.34, 93.56) * mm});
            skLineSegment(sketch, "E485", {"start": v(11.34, 93.56) * mm, "end": v(11.09, 93.15) * mm});
            skLineSegment(sketch, "E486", {"start": v(11.09, 93.15) * mm, "end": v(10.85, 92.76) * mm});
            skLineSegment(sketch, "E487", {"start": v(10.85, 92.76) * mm, "end": v(10.63, 92.37) * mm});
            skLineSegment(sketch, "E488", {"start": v(10.63, 92.37) * mm, "end": v(10.41, 91.99) * mm});
            skLineSegment(sketch, "E489", {"start": v(10.41, 91.99) * mm, "end": v(10.21, 91.62) * mm});
            skLineSegment(sketch, "E490", {"start": v(10.21, 91.62) * mm, "end": v(10.02, 91.25) * mm});
            skLineSegment(sketch, "E491", {"start": v(10.02, 91.25) * mm, "end": v(9.83, 90.9) * mm});
            skLineSegment(sketch, "E492", {"start": v(9.83, 90.9) * mm, "end": v(9.66, 90.55) * mm});
            skLineSegment(sketch, "E493", {"start": v(9.66, 90.55) * mm, "end": v(9.5, 90.21) * mm});
            skLineSegment(sketch, "E494", {"start": v(9.5, 90.21) * mm, "end": v(9.34, 89.89) * mm});
            skLineSegment(sketch, "E495", {"start": v(9.34, 89.89) * mm, "end": v(9.2, 89.57) * mm});
            skLineSegment(sketch, "E496", {"start": v(9.2, 89.57) * mm, "end": v(9.06, 89.26) * mm});
            skLineSegment(sketch, "E497", {"start": v(9.06, 89.26) * mm, "end": v(8.93, 88.96) * mm});
            skLineSegment(sketch, "E498", {"start": v(8.93, 88.96) * mm, "end": v(8.81, 88.67) * mm});
            skLineSegment(sketch, "E499", {"start": v(8.81, 88.67) * mm, "end": v(8.7, 88.4) * mm});
            skLineSegment(sketch, "E500", {"start": v(8.7, 88.4) * mm, "end": v(8.6, 88.13) * mm});
            skLineSegment(sketch, "E501", {"start": v(8.6, 88.13) * mm, "end": v(8.5, 87.87) * mm});
            skLineSegment(sketch, "E502", {"start": v(8.5, 87.87) * mm, "end": v(8, 87.88) * mm});
            skLineSegment(sketch, "E503", {"start": v(8, 87.88) * mm, "end": v(4.94, 88.1) * mm});
            skLineSegment(sketch, "E504", {"start": v(4.94, 88.1) * mm, "end": v(4.44, 88.16) * mm});
            skLineSegment(sketch, "E505", {"start": v(4.44, 88.16) * mm, "end": v(4.38, 88.43) * mm});
            skLineSegment(sketch, "E506", {"start": v(4.38, 88.43) * mm, "end": v(4.32, 88.7) * mm});
            skLineSegment(sketch, "E507", {"start": v(4.32, 88.7) * mm, "end": v(4.24, 89) * mm});
            skLineSegment(sketch, "E508", {"start": v(4.24, 89) * mm, "end": v(4.17, 89.3) * mm});
            skLineSegment(sketch, "E509", {"start": v(4.17, 89.3) * mm, "end": v(4.08, 89.62) * mm});
            skLineSegment(sketch, "E510", {"start": v(4.08, 89.62) * mm, "end": v(4, 89.94) * mm});
            skLineSegment(sketch, "E511", {"start": v(4, 89.94) * mm, "end": v(3.9, 90.28) * mm});
            skLineSegment(sketch, "E512", {"start": v(3.9, 90.28) * mm, "end": v(3.79, 90.62) * mm});
            skLineSegment(sketch, "E513", {"start": v(3.79, 90.62) * mm, "end": v(3.67, 90.98) * mm});
            skLineSegment(sketch, "E514", {"start": v(3.67, 90.98) * mm, "end": v(3.55, 91.35) * mm});
            skLineSegment(sketch, "E515", {"start": v(3.55, 91.35) * mm, "end": v(3.42, 91.72) * mm});
            skLineSegment(sketch, "E516", {"start": v(3.42, 91.72) * mm, "end": v(3.28, 92.11) * mm});
            skLineSegment(sketch, "E517", {"start": v(3.28, 92.11) * mm, "end": v(3.13, 92.5) * mm});
            skLineSegment(sketch, "E518", {"start": v(3.13, 92.5) * mm, "end": v(2.97, 92.92) * mm});
            skLineSegment(sketch, "E519", {"start": v(2.97, 92.92) * mm, "end": v(2.8, 93.33) * mm});
            skLineSegment(sketch, "E520", {"start": v(2.8, 93.33) * mm, "end": v(2.63, 93.76) * mm});
            skLineSegment(sketch, "E521", {"start": v(2.63, 93.76) * mm, "end": v(2.44, 94.2) * mm});
            skLineSegment(sketch, "E522", {"start": v(2.44, 94.2) * mm, "end": v(2.24, 94.64) * mm});
            skLineSegment(sketch, "E523", {"start": v(2.24, 94.64) * mm, "end": v(2.04, 95.09) * mm});
            skLineSegment(sketch, "E524", {"start": v(2.04, 95.09) * mm, "end": v(1.82, 95.55) * mm});
            skLineSegment(sketch, "E525", {"start": v(1.82, 95.55) * mm, "end": v(1.59, 96.02) * mm});
            skLineSegment(sketch, "E526", {"start": v(1.59, 96.02) * mm, "end": v(1.35, 96.5) * mm});
            skLineSegment(sketch, "E527", {"start": v(1.35, 96.5) * mm, "end": v(1.1, 96.99) * mm});
            skLineSegment(sketch, "E528", {"start": v(1.1, 96.99) * mm, "end": v(0.83, 97.48) * mm});
            skLineSegment(sketch, "E529", {"start": v(0.83, 97.48) * mm, "end": v(0.56, 97.98) * mm});
            skLineSegment(sketch, "E530", {"start": v(0.56, 97.98) * mm, "end": v(0.27, 98.5) * mm});
            skLineSegment(sketch, "E531", {"start": v(0.27, 98.5) * mm, "end": v(-0.03, 99) * mm});
            skLineSegment(sketch, "E532", {"start": v(-0.03, 99) * mm, "end": v(-0.35, 99.53) * mm});
            skLineSegment(sketch, "E533", {"start": v(-0.35, 99.53) * mm, "end": v(-0.67, 100.06) * mm});
            skLineSegment(sketch, "E534", {"start": v(-0.67, 100.06) * mm, "end": v(-1, 100.6) * mm});
            skLineSegment(sketch, "E535", {"start": v(-1, 100.6) * mm, "end": v(-1.36, 101.14) * mm});
            skLineSegment(sketch, "E536", {"start": v(-1.36, 101.14) * mm, "end": v(-1.73, 101.7) * mm});
            skLineSegment(sketch, "E537", {"start": v(-1.73, 101.7) * mm, "end": v(-2.1, 102.24) * mm});
            skLineSegment(sketch, "E538", {"start": v(-2.1, 102.24) * mm, "end": v(-2.49, 102.42) * mm});
            skLineSegment(sketch, "E539", {"start": v(-2.49, 102.42) * mm, "end": v(-4.74, 102.33) * mm});
            skLineSegment(sketch, "E540", {"start": v(-4.74, 102.33) * mm, "end": v(-5.11, 102.13) * mm});
            skLineSegment(sketch, "E541", {"start": v(-5.11, 102.13) * mm, "end": v(-5.45, 101.55) * mm});
            skLineSegment(sketch, "E542", {"start": v(-5.45, 101.55) * mm, "end": v(-5.77, 100.98) * mm});
            skLineSegment(sketch, "E543", {"start": v(-5.77, 100.98) * mm, "end": v(-6.08, 100.41) * mm});
            skLineSegment(sketch, "E544", {"start": v(-6.08, 100.41) * mm, "end": v(-6.38, 99.85) * mm});
            skLineSegment(sketch, "E545", {"start": v(-6.38, 99.85) * mm, "end": v(-6.67, 99.3) * mm});
            skLineSegment(sketch, "E546", {"start": v(-6.67, 99.3) * mm, "end": v(-6.94, 98.75) * mm});
            skLineSegment(sketch, "E547", {"start": v(-6.94, 98.75) * mm, "end": v(-7.2, 98.21) * mm});
            skLineSegment(sketch, "E548", {"start": v(-7.2, 98.21) * mm, "end": v(-7.45, 97.69) * mm});
            skLineSegment(sketch, "E549", {"start": v(-7.45, 97.69) * mm, "end": v(-7.69, 97.17) * mm});
            skLineSegment(sketch, "E550", {"start": v(-7.69, 97.17) * mm, "end": v(-7.92, 96.65) * mm});
            skLineSegment(sketch, "E551", {"start": v(-7.92, 96.65) * mm, "end": v(-8.13, 96.15) * mm});
            skLineSegment(sketch, "E552", {"start": v(-8.13, 96.15) * mm, "end": v(-8.34, 95.65) * mm});
            skLineSegment(sketch, "E553", {"start": v(-8.34, 95.65) * mm, "end": v(-8.53, 95.17) * mm});
            skLineSegment(sketch, "E554", {"start": v(-8.53, 95.17) * mm, "end": v(-8.71, 94.7) * mm});
            skLineSegment(sketch, "E555", {"start": v(-8.71, 94.7) * mm, "end": v(-8.89, 94.23) * mm});
            skLineSegment(sketch, "E556", {"start": v(-8.89, 94.23) * mm, "end": v(-9.05, 93.77) * mm});
            skLineSegment(sketch, "E557", {"start": v(-9.05, 93.77) * mm, "end": v(-9.2, 93.32) * mm});
            skLineSegment(sketch, "E558", {"start": v(-9.2, 93.32) * mm, "end": v(-9.35, 92.88) * mm});
            skLineSegment(sketch, "E559", {"start": v(-9.35, 92.88) * mm, "end": v(-9.49, 92.46) * mm});
            skLineSegment(sketch, "E560", {"start": v(-9.49, 92.46) * mm, "end": v(-9.62, 92.04) * mm});
            skLineSegment(sketch, "E561", {"start": v(-9.62, 92.04) * mm, "end": v(-9.74, 91.63) * mm});
            skLineSegment(sketch, "E562", {"start": v(-9.74, 91.63) * mm, "end": v(-9.85, 91.24) * mm});
            skLineSegment(sketch, "E563", {"start": v(-9.85, 91.24) * mm, "end": v(-9.95, 90.85) * mm});
            skLineSegment(sketch, "E564", {"start": v(-9.95, 90.85) * mm, "end": v(-10.04, 90.47) * mm});
            skLineSegment(sketch, "E565", {"start": v(-10.04, 90.47) * mm, "end": v(-10.13, 90.1) * mm});
            skLineSegment(sketch, "E566", {"start": v(-10.13, 90.1) * mm, "end": v(-10.21, 89.76) * mm});
            skLineSegment(sketch, "E567", {"start": v(-10.21, 89.76) * mm, "end": v(-10.29, 89.41) * mm});
            skLineSegment(sketch, "E568", {"start": v(-10.29, 89.41) * mm, "end": v(-10.35, 89.08) * mm});
            skLineSegment(sketch, "E569", {"start": v(-10.35, 89.08) * mm, "end": v(-10.41, 88.76) * mm});
            skLineSegment(sketch, "E570", {"start": v(-10.41, 88.76) * mm, "end": v(-10.47, 88.46) * mm});
            skLineSegment(sketch, "E571", {"start": v(-10.47, 88.46) * mm, "end": v(-10.52, 88.16) * mm});
            skLineSegment(sketch, "E572", {"start": v(-10.52, 88.16) * mm, "end": v(-10.56, 87.88) * mm});
            skLineSegment(sketch, "E573", {"start": v(-10.56, 87.88) * mm, "end": v(-10.6, 87.6) * mm});
            skLineSegment(sketch, "E574", {"start": v(-10.6, 87.6) * mm, "end": v(-11.1, 87.5) * mm});
            skLineSegment(sketch, "E575", {"start": v(-11.1, 87.5) * mm, "end": v(-14.12, 87.07) * mm});
            skLineSegment(sketch, "E576", {"start": v(-14.12, 87.07) * mm, "end": v(-14.63, 87.01) * mm});
            skLineSegment(sketch, "E577", {"start": v(-14.63, 87.01) * mm, "end": v(-14.74, 87.27) * mm});
            skLineSegment(sketch, "E578", {"start": v(-14.74, 87.27) * mm, "end": v(-14.87, 87.52) * mm});
            skLineSegment(sketch, "E579", {"start": v(-14.87, 87.52) * mm, "end": v(-15, 87.8) * mm});
            skLineSegment(sketch, "E580", {"start": v(-15, 87.8) * mm, "end": v(-15.14, 88.07) * mm});
            skLineSegment(sketch, "E581", {"start": v(-15.14, 88.07) * mm, "end": v(-15.29, 88.36) * mm});
            skLineSegment(sketch, "E582", {"start": v(-15.29, 88.36) * mm, "end": v(-15.45, 88.66) * mm});
            skLineSegment(sketch, "E583", {"start": v(-15.45, 88.66) * mm, "end": v(-15.62, 88.97) * mm});
            skLineSegment(sketch, "E584", {"start": v(-15.62, 88.97) * mm, "end": v(-15.8, 89.28) * mm});
            skLineSegment(sketch, "E585", {"start": v(-15.8, 89.28) * mm, "end": v(-15.98, 89.6) * mm});
            skLineSegment(sketch, "E586", {"start": v(-15.98, 89.6) * mm, "end": v(-16.18, 89.94) * mm});
            skLineSegment(sketch, "E587", {"start": v(-16.18, 89.94) * mm, "end": v(-16.4, 90.28) * mm});
            skLineSegment(sketch, "E588", {"start": v(-16.4, 90.28) * mm, "end": v(-16.61, 90.63) * mm});
            skLineSegment(sketch, "E589", {"start": v(-16.61, 90.63) * mm, "end": v(-16.84, 90.98) * mm});
            skLineSegment(sketch, "E590", {"start": v(-16.84, 90.98) * mm, "end": v(-17.08, 91.35) * mm});
            skLineSegment(sketch, "E591", {"start": v(-17.08, 91.35) * mm, "end": v(-17.34, 91.72) * mm});
            skLineSegment(sketch, "E592", {"start": v(-17.34, 91.72) * mm, "end": v(-17.6, 92.1) * mm});
            skLineSegment(sketch, "E593", {"start": v(-17.6, 92.1) * mm, "end": v(-17.88, 92.48) * mm});
            skLineSegment(sketch, "E594", {"start": v(-17.88, 92.48) * mm, "end": v(-18.16, 92.87) * mm});
            skLineSegment(sketch, "E595", {"start": v(-18.16, 92.87) * mm, "end": v(-18.47, 93.27) * mm});
            skLineSegment(sketch, "E596", {"start": v(-18.47, 93.27) * mm, "end": v(-18.78, 93.67) * mm});
            skLineSegment(sketch, "E597", {"start": v(-18.78, 93.67) * mm, "end": v(-19.1, 94.08) * mm});
            skLineSegment(sketch, "E598", {"start": v(-19.1, 94.08) * mm, "end": v(-19.44, 94.5) * mm});
            skLineSegment(sketch, "E599", {"start": v(-19.44, 94.5) * mm, "end": v(-19.8, 94.92) * mm});
            skLineSegment(sketch, "E600", {"start": v(-19.8, 94.92) * mm, "end": v(-20.16, 95.34) * mm});
            skLineSegment(sketch, "E601", {"start": v(-20.16, 95.34) * mm, "end": v(-20.53, 95.77) * mm});
            skLineSegment(sketch, "E602", {"start": v(-20.53, 95.77) * mm, "end": v(-20.92, 96.2) * mm});
            skLineSegment(sketch, "E603", {"start": v(-20.92, 96.2) * mm, "end": v(-21.33, 96.65) * mm});
            skLineSegment(sketch, "E604", {"start": v(-21.33, 96.65) * mm, "end": v(-21.75, 97.1) * mm});
            skLineSegment(sketch, "E605", {"start": v(-21.75, 97.1) * mm, "end": v(-22.18, 97.54) * mm});
            skLineSegment(sketch, "E606", {"start": v(-22.18, 97.54) * mm, "end": v(-22.62, 98) * mm});
            skLineSegment(sketch, "E607", {"start": v(-22.62, 98) * mm, "end": v(-23.08, 98.45) * mm});
            skLineSegment(sketch, "E608", {"start": v(-23.08, 98.45) * mm, "end": v(-23.56, 98.9) * mm});
            skLineSegment(sketch, "E609", {"start": v(-23.56, 98.9) * mm, "end": v(-24.05, 99.36) * mm});
            skLineSegment(sketch, "E610", {"start": v(-24.05, 99.36) * mm, "end": v(-24.46, 99.45) * mm});
            skLineSegment(sketch, "E611", {"start": v(-24.46, 99.45) * mm, "end": v(-26.64, 98.88) * mm});
            skLineSegment(sketch, "E612", {"start": v(-26.64, 98.88) * mm, "end": v(-26.96, 98.61) * mm});
            skLineSegment(sketch, "E613", {"start": v(-26.96, 98.61) * mm, "end": v(-27.16, 97.97) * mm});
            skLineSegment(sketch, "E614", {"start": v(-27.16, 97.97) * mm, "end": v(-27.36, 97.34) * mm});
            skLineSegment(sketch, "E615", {"start": v(-27.36, 97.34) * mm, "end": v(-27.54, 96.72) * mm});
            skLineSegment(sketch, "E616", {"start": v(-27.54, 96.72) * mm, "end": v(-27.7, 96.1) * mm});
            skLineSegment(sketch, "E617", {"start": v(-27.7, 96.1) * mm, "end": v(-27.87, 95.5) * mm});
            skLineSegment(sketch, "E618", {"start": v(-27.87, 95.5) * mm, "end": v(-28.02, 94.91) * mm});
            skLineSegment(sketch, "E619", {"start": v(-28.02, 94.91) * mm, "end": v(-28.16, 94.33) * mm});
            skLineSegment(sketch, "E620", {"start": v(-28.16, 94.33) * mm, "end": v(-28.29, 93.76) * mm});
            skLineSegment(sketch, "E621", {"start": v(-28.29, 93.76) * mm, "end": v(-28.4, 93.2) * mm});
            skLineSegment(sketch, "E622", {"start": v(-28.4, 93.2) * mm, "end": v(-28.52, 92.65) * mm});
            skLineSegment(sketch, "E623", {"start": v(-28.52, 92.65) * mm, "end": v(-28.62, 92.12) * mm});
            skLineSegment(sketch, "E624", {"start": v(-28.62, 92.12) * mm, "end": v(-28.72, 91.59) * mm});
            skLineSegment(sketch, "E625", {"start": v(-28.72, 91.59) * mm, "end": v(-28.8, 91.07) * mm});
            skLineSegment(sketch, "E626", {"start": v(-28.8, 91.07) * mm, "end": v(-28.88, 90.57) * mm});
            skLineSegment(sketch, "E627", {"start": v(-28.88, 90.57) * mm, "end": v(-28.95, 90.07) * mm});
            skLineSegment(sketch, "E628", {"start": v(-28.95, 90.07) * mm, "end": v(-29.01, 89.6) * mm});
            skLineSegment(sketch, "E629", {"start": v(-29.01, 89.6) * mm, "end": v(-29.07, 89.12) * mm});
            skLineSegment(sketch, "E630", {"start": v(-29.07, 89.12) * mm, "end": v(-29.11, 88.66) * mm});
            skLineSegment(sketch, "E631", {"start": v(-29.11, 88.66) * mm, "end": v(-29.15, 88.22) * mm});
            skLineSegment(sketch, "E632", {"start": v(-29.15, 88.22) * mm, "end": v(-29.2, 87.78) * mm});
            skLineSegment(sketch, "E633", {"start": v(-29.2, 87.78) * mm, "end": v(-29.22, 87.36) * mm});
            skLineSegment(sketch, "E634", {"start": v(-29.22, 87.36) * mm, "end": v(-29.24, 86.95) * mm});
            skLineSegment(sketch, "E635", {"start": v(-29.24, 86.95) * mm, "end": v(-29.26, 86.55) * mm});
            skLineSegment(sketch, "E636", {"start": v(-29.26, 86.55) * mm, "end": v(-29.27, 86.16) * mm});
            skLineSegment(sketch, "E637", {"start": v(-29.27, 86.16) * mm, "end": v(-29.28, 85.79) * mm});
            skLineSegment(sketch, "E638", {"start": v(-29.28, 85.79) * mm, "end": v(-29.28, 85.43) * mm});
            skLineSegment(sketch, "E639", {"start": v(-29.28, 85.43) * mm, "end": v(-29.28, 85.08) * mm});
            skLineSegment(sketch, "E640", {"start": v(-29.28, 85.08) * mm, "end": v(-29.27, 84.74) * mm});
            skLineSegment(sketch, "E641", {"start": v(-29.27, 84.74) * mm, "end": v(-29.26, 84.41) * mm});
            skLineSegment(sketch, "E642", {"start": v(-29.26, 84.41) * mm, "end": v(-29.25, 84.1) * mm});
            skLineSegment(sketch, "E643", {"start": v(-29.25, 84.1) * mm, "end": v(-29.24, 83.8) * mm});
            skLineSegment(sketch, "E644", {"start": v(-29.24, 83.8) * mm, "end": v(-29.22, 83.51) * mm});
            skLineSegment(sketch, "E645", {"start": v(-29.22, 83.51) * mm, "end": v(-29.2, 83.24) * mm});
            skLineSegment(sketch, "E646", {"start": v(-29.2, 83.24) * mm, "end": v(-29.66, 83.04) * mm});
            skLineSegment(sketch, "E647", {"start": v(-29.66, 83.04) * mm, "end": v(-32.52, 81.96) * mm});
            skLineSegment(sketch, "E648", {"start": v(-32.52, 81.96) * mm, "end": v(-33, 81.8) * mm});
            skLineSegment(sketch, "E649", {"start": v(-33, 81.8) * mm, "end": v(-33.17, 82.02) * mm});
            skLineSegment(sketch, "E650", {"start": v(-33.17, 82.02) * mm, "end": v(-33.35, 82.25) * mm});
            skLineSegment(sketch, "E651", {"start": v(-33.35, 82.25) * mm, "end": v(-33.53, 82.48) * mm});
            skLineSegment(sketch, "E652", {"start": v(-33.53, 82.48) * mm, "end": v(-33.73, 82.72) * mm});
            skLineSegment(sketch, "E653", {"start": v(-33.73, 82.72) * mm, "end": v(-33.94, 82.97) * mm});
            skLineSegment(sketch, "E654", {"start": v(-33.94, 82.97) * mm, "end": v(-34.16, 83.23) * mm});
            skLineSegment(sketch, "E655", {"start": v(-34.16, 83.23) * mm, "end": v(-34.39, 83.5) * mm});
            skLineSegment(sketch, "E656", {"start": v(-34.39, 83.5) * mm, "end": v(-34.63, 83.76) * mm});
            skLineSegment(sketch, "E657", {"start": v(-34.63, 83.76) * mm, "end": v(-34.88, 84.04) * mm});
            skLineSegment(sketch, "E658", {"start": v(-34.88, 84.04) * mm, "end": v(-35.15, 84.32) * mm});
            skLineSegment(sketch, "E659", {"start": v(-35.15, 84.32) * mm, "end": v(-35.43, 84.6) * mm});
            skLineSegment(sketch, "E660", {"start": v(-35.43, 84.6) * mm, "end": v(-35.72, 84.9) * mm});
            skLineSegment(sketch, "E661", {"start": v(-35.72, 84.9) * mm, "end": v(-36.02, 85.2) * mm});
            skLineSegment(sketch, "E662", {"start": v(-36.02, 85.2) * mm, "end": v(-36.33, 85.5) * mm});
            skLineSegment(sketch, "E663", {"start": v(-36.33, 85.5) * mm, "end": v(-36.66, 85.8) * mm});
            skLineSegment(sketch, "E664", {"start": v(-36.66, 85.8) * mm, "end": v(-37, 86.12) * mm});
            skLineSegment(sketch, "E665", {"start": v(-37, 86.12) * mm, "end": v(-37.35, 86.44) * mm});
            skLineSegment(sketch, "E666", {"start": v(-37.35, 86.44) * mm, "end": v(-37.72, 86.76) * mm});
            skLineSegment(sketch, "E667", {"start": v(-37.72, 86.76) * mm, "end": v(-38.1, 87.08) * mm});
            skLineSegment(sketch, "E668", {"start": v(-38.1, 87.08) * mm, "end": v(-38.49, 87.4) * mm});
            skLineSegment(sketch, "E669", {"start": v(-38.49, 87.4) * mm, "end": v(-38.9, 87.74) * mm});
            skLineSegment(sketch, "E670", {"start": v(-38.9, 87.74) * mm, "end": v(-39.31, 88.07) * mm});
            skLineSegment(sketch, "E671", {"start": v(-39.31, 88.07) * mm, "end": v(-39.75, 88.4) * mm});
            skLineSegment(sketch, "E672", {"start": v(-39.75, 88.4) * mm, "end": v(-40.2, 88.74) * mm});
            skLineSegment(sketch, "E673", {"start": v(-40.2, 88.74) * mm, "end": v(-40.65, 89.08) * mm});
            skLineSegment(sketch, "E674", {"start": v(-40.65, 89.08) * mm, "end": v(-41.13, 89.42) * mm});
            skLineSegment(sketch, "E675", {"start": v(-41.13, 89.42) * mm, "end": v(-41.62, 89.77) * mm});
            skLineSegment(sketch, "E676", {"start": v(-41.62, 89.77) * mm, "end": v(-42.12, 90.11) * mm});
            skLineSegment(sketch, "E677", {"start": v(-42.12, 90.11) * mm, "end": v(-42.64, 90.46) * mm});
            skLineSegment(sketch, "E678", {"start": v(-42.64, 90.46) * mm, "end": v(-43.17, 90.8) * mm});
            skLineSegment(sketch, "E679", {"start": v(-43.17, 90.8) * mm, "end": v(-43.72, 91.15) * mm});
            skLineSegment(sketch, "E680", {"start": v(-43.72, 91.15) * mm, "end": v(-44.28, 91.5) * mm});
            skLineSegment(sketch, "E681", {"start": v(-44.28, 91.5) * mm, "end": v(-44.86, 91.83) * mm});
            skLineSegment(sketch, "E682", {"start": v(-44.86, 91.83) * mm, "end": v(-45.28, 91.83) * mm});
            skLineSegment(sketch, "E683", {"start": v(-45.28, 91.83) * mm, "end": v(-47.29, 90.8) * mm});
            skLineSegment(sketch, "E684", {"start": v(-47.29, 90.8) * mm, "end": v(-47.54, 90.47) * mm});
            skLineSegment(sketch, "E685", {"start": v(-47.54, 90.47) * mm, "end": v(-47.6, 89.8) * mm});
            skLineSegment(sketch, "E686", {"start": v(-47.6, 89.8) * mm, "end": v(-47.65, 89.15) * mm});
            skLineSegment(sketch, "E687", {"start": v(-47.65, 89.15) * mm, "end": v(-47.7, 88.5) * mm});
            skLineSegment(sketch, "E688", {"start": v(-47.7, 88.5) * mm, "end": v(-47.73, 87.87) * mm});
            skLineSegment(sketch, "E689", {"start": v(-47.73, 87.87) * mm, "end": v(-47.76, 87.25) * mm});
            skLineSegment(sketch, "E690", {"start": v(-47.76, 87.25) * mm, "end": v(-47.78, 86.64) * mm});
            skLineSegment(sketch, "E691", {"start": v(-47.78, 86.64) * mm, "end": v(-47.8, 86.04) * mm});
            skLineSegment(sketch, "E692", {"start": v(-47.8, 86.04) * mm, "end": v(-47.8, 85.45) * mm});
            skLineSegment(sketch, "E693", {"start": v(-47.8, 85.45) * mm, "end": v(-47.8, 84.88) * mm});
            skLineSegment(sketch, "E694", {"start": v(-47.8, 84.88) * mm, "end": v(-47.78, 84.32) * mm});
            skLineSegment(sketch, "E695", {"start": v(-47.78, 84.32) * mm, "end": v(-47.77, 83.77) * mm});
            skLineSegment(sketch, "E696", {"start": v(-47.77, 83.77) * mm, "end": v(-47.75, 83.24) * mm});
            skLineSegment(sketch, "E697", {"start": v(-47.75, 83.24) * mm, "end": v(-47.72, 82.72) * mm});
            skLineSegment(sketch, "E698", {"start": v(-47.72, 82.72) * mm, "end": v(-47.69, 82.2) * mm});
            skLineSegment(sketch, "E699", {"start": v(-47.69, 82.2) * mm, "end": v(-47.65, 81.7) * mm});
            skLineSegment(sketch, "E700", {"start": v(-47.65, 81.7) * mm, "end": v(-47.6, 81.23) * mm});
            skLineSegment(sketch, "E701", {"start": v(-47.6, 81.23) * mm, "end": v(-47.56, 80.75) * mm});
            skLineSegment(sketch, "E702", {"start": v(-47.56, 80.75) * mm, "end": v(-47.5, 80.3) * mm});
            skLineSegment(sketch, "E703", {"start": v(-47.5, 80.3) * mm, "end": v(-47.45, 79.85) * mm});
            skLineSegment(sketch, "E704", {"start": v(-47.45, 79.85) * mm, "end": v(-47.39, 79.42) * mm});
            skLineSegment(sketch, "E705", {"start": v(-47.39, 79.42) * mm, "end": v(-47.33, 79) * mm});
            skLineSegment(sketch, "E706", {"start": v(-47.33, 79) * mm, "end": v(-47.26, 78.6) * mm});
            skLineSegment(sketch, "E707", {"start": v(-47.26, 78.6) * mm, "end": v(-47.2, 78.2) * mm});
            skLineSegment(sketch, "E708", {"start": v(-47.2, 78.2) * mm, "end": v(-47.12, 77.82) * mm});
            skLineSegment(sketch, "E709", {"start": v(-47.12, 77.82) * mm, "end": v(-47.05, 77.45) * mm});
            skLineSegment(sketch, "E710", {"start": v(-47.05, 77.45) * mm, "end": v(-46.97, 77.1) * mm});
            skLineSegment(sketch, "E711", {"start": v(-46.97, 77.1) * mm, "end": v(-46.9, 76.76) * mm});
            skLineSegment(sketch, "E712", {"start": v(-46.9, 76.76) * mm, "end": v(-46.82, 76.43) * mm});
            skLineSegment(sketch, "E713", {"start": v(-46.82, 76.43) * mm, "end": v(-46.74, 76.11) * mm});
            skLineSegment(sketch, "E714", {"start": v(-46.74, 76.11) * mm, "end": v(-46.66, 75.8) * mm});
            skLineSegment(sketch, "E715", {"start": v(-46.66, 75.8) * mm, "end": v(-46.58, 75.52) * mm});
            skLineSegment(sketch, "E716", {"start": v(-46.58, 75.52) * mm, "end": v(-46.5, 75.24) * mm});
            skLineSegment(sketch, "E717", {"start": v(-46.5, 75.24) * mm, "end": v(-46.42, 74.98) * mm});
            skLineSegment(sketch, "E718", {"start": v(-46.42, 74.98) * mm, "end": v(-46.83, 74.68) * mm});
            skLineSegment(sketch, "E719", {"start": v(-46.83, 74.68) * mm, "end": v(-49.4, 73.01) * mm});
            skLineSegment(sketch, "E720", {"start": v(-49.4, 73.01) * mm, "end": v(-49.83, 72.75) * mm});
            skLineSegment(sketch, "E721", {"start": v(-49.83, 72.75) * mm, "end": v(-50.04, 72.93) * mm});
            skLineSegment(sketch, "E722", {"start": v(-50.04, 72.93) * mm, "end": v(-50.26, 73.12) * mm});
            skLineSegment(sketch, "E723", {"start": v(-50.26, 73.12) * mm, "end": v(-50.5, 73.3) * mm});
            skLineSegment(sketch, "E724", {"start": v(-50.5, 73.3) * mm, "end": v(-50.74, 73.5) * mm});
            skLineSegment(sketch, "E725", {"start": v(-50.74, 73.5) * mm, "end": v(-51, 73.7) * mm});
            skLineSegment(sketch, "E726", {"start": v(-51, 73.7) * mm, "end": v(-51.26, 73.9) * mm});
            skLineSegment(sketch, "E727", {"start": v(-51.26, 73.9) * mm, "end": v(-51.55, 74.11) * mm});
            skLineSegment(sketch, "E728", {"start": v(-51.55, 74.11) * mm, "end": v(-51.84, 74.32) * mm});
            skLineSegment(sketch, "E729", {"start": v(-51.84, 74.32) * mm, "end": v(-52.15, 74.54) * mm});
            skLineSegment(sketch, "E730", {"start": v(-52.15, 74.54) * mm, "end": v(-52.47, 74.76) * mm});
            skLineSegment(sketch, "E731", {"start": v(-52.47, 74.76) * mm, "end": v(-52.8, 74.98) * mm});
            skLineSegment(sketch, "E732", {"start": v(-52.8, 74.98) * mm, "end": v(-53.14, 75.2) * mm});
            skLineSegment(sketch, "E733", {"start": v(-53.14, 75.2) * mm, "end": v(-53.5, 75.43) * mm});
            skLineSegment(sketch, "E734", {"start": v(-53.5, 75.43) * mm, "end": v(-53.88, 75.66) * mm});
            skLineSegment(sketch, "E735", {"start": v(-53.88, 75.66) * mm, "end": v(-54.26, 75.89) * mm});
            skLineSegment(sketch, "E736", {"start": v(-54.26, 75.89) * mm, "end": v(-54.66, 76.12) * mm});
            skLineSegment(sketch, "E737", {"start": v(-54.66, 76.12) * mm, "end": v(-55.07, 76.35) * mm});
            skLineSegment(sketch, "E738", {"start": v(-55.07, 76.35) * mm, "end": v(-55.5, 76.58) * mm});
            skLineSegment(sketch, "E739", {"start": v(-55.5, 76.58) * mm, "end": v(-55.94, 76.82) * mm});
            skLineSegment(sketch, "E740", {"start": v(-55.94, 76.82) * mm, "end": v(-56.4, 77.05) * mm});
            skLineSegment(sketch, "E741", {"start": v(-56.4, 77.05) * mm, "end": v(-56.86, 77.29) * mm});
            skLineSegment(sketch, "E742", {"start": v(-56.86, 77.29) * mm, "end": v(-57.34, 77.52) * mm});
            skLineSegment(sketch, "E743", {"start": v(-57.34, 77.52) * mm, "end": v(-57.83, 77.76) * mm});
            skLineSegment(sketch, "E744", {"start": v(-57.83, 77.76) * mm, "end": v(-58.34, 78) * mm});
            skLineSegment(sketch, "E745", {"start": v(-58.34, 78) * mm, "end": v(-58.87, 78.23) * mm});
            skLineSegment(sketch, "E746", {"start": v(-58.87, 78.23) * mm, "end": v(-59.4, 78.46) * mm});
            skLineSegment(sketch, "E747", {"start": v(-59.4, 78.46) * mm, "end": v(-59.95, 78.69) * mm});
            skLineSegment(sketch, "E748", {"start": v(-59.95, 78.69) * mm, "end": v(-60.52, 78.91) * mm});
            skLineSegment(sketch, "E749", {"start": v(-60.52, 78.91) * mm, "end": v(-61.1, 79.14) * mm});
            skLineSegment(sketch, "E750", {"start": v(-61.1, 79.14) * mm, "end": v(-61.7, 79.36) * mm});
            skLineSegment(sketch, "E751", {"start": v(-61.7, 79.36) * mm, "end": v(-62.3, 79.58) * mm});
            skLineSegment(sketch, "E752", {"start": v(-62.3, 79.58) * mm, "end": v(-62.93, 79.8) * mm});
            skLineSegment(sketch, "E753", {"start": v(-62.93, 79.8) * mm, "end": v(-63.56, 80) * mm});
            skLineSegment(sketch, "E754", {"start": v(-63.56, 80) * mm, "end": v(-63.97, 79.91) * mm});
            skLineSegment(sketch, "E755", {"start": v(-63.97, 79.91) * mm, "end": v(-65.72, 78.48) * mm});
            skLineSegment(sketch, "E756", {"start": v(-65.72, 78.48) * mm, "end": v(-65.9, 78.1) * mm});
            skLineSegment(sketch, "E757", {"start": v(-65.9, 78.1) * mm, "end": v(-65.8, 77.43) * mm});
            skLineSegment(sketch, "E758", {"start": v(-65.8, 77.43) * mm, "end": v(-65.72, 76.78) * mm});
            skLineSegment(sketch, "E759", {"start": v(-65.72, 76.78) * mm, "end": v(-65.62, 76.14) * mm});
            skLineSegment(sketch, "E760", {"start": v(-65.62, 76.14) * mm, "end": v(-65.52, 75.51) * mm});
            skLineSegment(sketch, "E761", {"start": v(-65.52, 75.51) * mm, "end": v(-65.41, 74.9) * mm});
            skLineSegment(sketch, "E762", {"start": v(-65.41, 74.9) * mm, "end": v(-65.3, 74.3) * mm});
            skLineSegment(sketch, "E763", {"start": v(-65.3, 74.3) * mm, "end": v(-65.18, 73.72) * mm});
            skLineSegment(sketch, "E764", {"start": v(-65.18, 73.72) * mm, "end": v(-65.06, 73.14) * mm});
            skLineSegment(sketch, "E765", {"start": v(-65.06, 73.14) * mm, "end": v(-64.94, 72.58) * mm});
            skLineSegment(sketch, "E766", {"start": v(-64.94, 72.58) * mm, "end": v(-64.8, 72.04) * mm});
            skLineSegment(sketch, "E767", {"start": v(-64.8, 72.04) * mm, "end": v(-64.67, 71.5) * mm});
            skLineSegment(sketch, "E768", {"start": v(-64.67, 71.5) * mm, "end": v(-64.54, 71) * mm});
            skLineSegment(sketch, "E769", {"start": v(-64.54, 71) * mm, "end": v(-64.4, 70.49) * mm});
            skLineSegment(sketch, "E770", {"start": v(-64.4, 70.49) * mm, "end": v(-64.26, 70) * mm});
            skLineSegment(sketch, "E771", {"start": v(-64.26, 70) * mm, "end": v(-64.11, 69.52) * mm});
            skLineSegment(sketch, "E772", {"start": v(-64.11, 69.52) * mm, "end": v(-63.97, 69.06) * mm});
            skLineSegment(sketch, "E773", {"start": v(-63.97, 69.06) * mm, "end": v(-63.82, 68.6) * mm});
            skLineSegment(sketch, "E774", {"start": v(-63.82, 68.6) * mm, "end": v(-63.67, 68.17) * mm});
            skLineSegment(sketch, "E775", {"start": v(-63.67, 68.17) * mm, "end": v(-63.52, 67.75) * mm});
            skLineSegment(sketch, "E776", {"start": v(-63.52, 67.75) * mm, "end": v(-63.37, 67.34) * mm});
            skLineSegment(sketch, "E777", {"start": v(-63.37, 67.34) * mm, "end": v(-63.22, 66.94) * mm});
            skLineSegment(sketch, "E778", {"start": v(-63.22, 66.94) * mm, "end": v(-63.06, 66.56) * mm});
            skLineSegment(sketch, "E779", {"start": v(-63.06, 66.56) * mm, "end": v(-62.91, 66.19) * mm});
            skLineSegment(sketch, "E780", {"start": v(-62.91, 66.19) * mm, "end": v(-62.76, 65.83) * mm});
            skLineSegment(sketch, "E781", {"start": v(-62.76, 65.83) * mm, "end": v(-62.61, 65.49) * mm});
            skLineSegment(sketch, "E782", {"start": v(-62.61, 65.49) * mm, "end": v(-62.46, 65.16) * mm});
            skLineSegment(sketch, "E783", {"start": v(-62.46, 65.16) * mm, "end": v(-62.31, 64.84) * mm});
            skLineSegment(sketch, "E784", {"start": v(-62.31, 64.84) * mm, "end": v(-62.17, 64.54) * mm});
            skLineSegment(sketch, "E785", {"start": v(-62.17, 64.54) * mm, "end": v(-62.02, 64.25) * mm});
            skLineSegment(sketch, "E786", {"start": v(-62.02, 64.25) * mm, "end": v(-61.88, 63.97) * mm});
            skLineSegment(sketch, "E787", {"start": v(-61.88, 63.97) * mm, "end": v(-61.74, 63.7) * mm});
            skLineSegment(sketch, "E788", {"start": v(-61.74, 63.7) * mm, "end": v(-61.6, 63.45) * mm});
            skLineSegment(sketch, "E789", {"start": v(-61.6, 63.45) * mm, "end": v(-61.47, 63.21) * mm});
            skLineSegment(sketch, "E790", {"start": v(-61.47, 63.21) * mm, "end": v(-61.8, 62.83) * mm});
            skLineSegment(sketch, "E791", {"start": v(-61.8, 62.83) * mm, "end": v(-63.95, 60.65) * mm});
            skLineSegment(sketch, "E792", {"start": v(-63.95, 60.65) * mm, "end": v(-64.32, 60.3) * mm});
            skLineSegment(sketch, "E793", {"start": v(-64.32, 60.3) * mm, "end": v(-64.56, 60.43) * mm});
            skLineSegment(sketch, "E794", {"start": v(-64.56, 60.43) * mm, "end": v(-64.82, 60.57) * mm});
            skLineSegment(sketch, "E795", {"start": v(-64.82, 60.57) * mm, "end": v(-65.08, 60.7) * mm});
            skLineSegment(sketch, "E796", {"start": v(-65.08, 60.7) * mm, "end": v(-65.37, 60.84) * mm});
            skLineSegment(sketch, "E797", {"start": v(-65.37, 60.84) * mm, "end": v(-65.66, 60.98) * mm});
            skLineSegment(sketch, "E798", {"start": v(-65.66, 60.98) * mm, "end": v(-65.97, 61.12) * mm});
            skLineSegment(sketch, "E799", {"start": v(-65.97, 61.12) * mm, "end": v(-66.29, 61.26) * mm});
            skLineSegment(sketch, "E800", {"start": v(-66.29, 61.26) * mm, "end": v(-66.62, 61.4) * mm});
            skLineSegment(sketch, "E801", {"start": v(-66.62, 61.4) * mm, "end": v(-66.96, 61.55) * mm});
            skLineSegment(sketch, "E802", {"start": v(-66.96, 61.55) * mm, "end": v(-67.32, 61.7) * mm});
            skLineSegment(sketch, "E803", {"start": v(-67.32, 61.7) * mm, "end": v(-67.7, 61.84) * mm});
            skLineSegment(sketch, "E804", {"start": v(-67.7, 61.84) * mm, "end": v(-68.08, 61.98) * mm});
            skLineSegment(sketch, "E805", {"start": v(-68.08, 61.98) * mm, "end": v(-68.48, 62.12) * mm});
            skLineSegment(sketch, "E806", {"start": v(-68.48, 62.12) * mm, "end": v(-68.9, 62.27) * mm});
            skLineSegment(sketch, "E807", {"start": v(-68.9, 62.27) * mm, "end": v(-69.32, 62.4) * mm});
            skLineSegment(sketch, "E808", {"start": v(-69.32, 62.4) * mm, "end": v(-69.76, 62.55) * mm});
            skLineSegment(sketch, "E809", {"start": v(-69.76, 62.55) * mm, "end": v(-70.2, 62.69) * mm});
            skLineSegment(sketch, "E810", {"start": v(-70.2, 62.69) * mm, "end": v(-70.68, 62.83) * mm});
            skLineSegment(sketch, "E811", {"start": v(-70.68, 62.83) * mm, "end": v(-71.16, 62.96) * mm});
            skLineSegment(sketch, "E812", {"start": v(-71.16, 62.96) * mm, "end": v(-71.65, 63.1) * mm});
            skLineSegment(sketch, "E813", {"start": v(-71.65, 63.1) * mm, "end": v(-72.16, 63.22) * mm});
            skLineSegment(sketch, "E814", {"start": v(-72.16, 63.22) * mm, "end": v(-72.68, 63.35) * mm});
            skLineSegment(sketch, "E815", {"start": v(-72.68, 63.35) * mm, "end": v(-73.21, 63.47) * mm});
            skLineSegment(sketch, "E816", {"start": v(-73.21, 63.47) * mm, "end": v(-73.76, 63.59) * mm});
            skLineSegment(sketch, "E817", {"start": v(-73.76, 63.59) * mm, "end": v(-74.32, 63.7) * mm});
            skLineSegment(sketch, "E818", {"start": v(-74.32, 63.7) * mm, "end": v(-74.9, 63.81) * mm});
            skLineSegment(sketch, "E819", {"start": v(-74.9, 63.81) * mm, "end": v(-75.48, 63.92) * mm});
            skLineSegment(sketch, "E820", {"start": v(-75.48, 63.92) * mm, "end": v(-76.08, 64.02) * mm});
            skLineSegment(sketch, "E821", {"start": v(-76.08, 64.02) * mm, "end": v(-76.7, 64.12) * mm});
            skLineSegment(sketch, "E822", {"start": v(-76.7, 64.12) * mm, "end": v(-77.33, 64.2) * mm});
            skLineSegment(sketch, "E823", {"start": v(-77.33, 64.2) * mm, "end": v(-77.97, 64.29) * mm});
            skLineSegment(sketch, "E824", {"start": v(-77.97, 64.29) * mm, "end": v(-78.62, 64.37) * mm});
            skLineSegment(sketch, "E825", {"start": v(-78.62, 64.37) * mm, "end": v(-79.3, 64.44) * mm});
            skLineSegment(sketch, "E826", {"start": v(-79.3, 64.44) * mm, "end": v(-79.67, 64.26) * mm});
            skLineSegment(sketch, "E827", {"start": v(-79.67, 64.26) * mm, "end": v(-81.07, 62.48) * mm});
            skLineSegment(sketch, "E828", {"start": v(-81.07, 62.48) * mm, "end": v(-81.15, 62.07) * mm});
            skLineSegment(sketch, "E829", {"start": v(-81.15, 62.07) * mm, "end": v(-80.93, 61.44) * mm});
            skLineSegment(sketch, "E830", {"start": v(-80.93, 61.44) * mm, "end": v(-80.7, 60.82) * mm});
            skLineSegment(sketch, "E831", {"start": v(-80.7, 60.82) * mm, "end": v(-80.47, 60.22) * mm});
            skLineSegment(sketch, "E832", {"start": v(-80.47, 60.22) * mm, "end": v(-80.23, 59.63) * mm});
            skLineSegment(sketch, "E833", {"start": v(-80.23, 59.63) * mm, "end": v(-80, 59.05) * mm});
            skLineSegment(sketch, "E834", {"start": v(-80, 59.05) * mm, "end": v(-79.76, 58.5) * mm});
            skLineSegment(sketch, "E835", {"start": v(-79.76, 58.5) * mm, "end": v(-79.52, 57.94) * mm});
            skLineSegment(sketch, "E836", {"start": v(-79.52, 57.94) * mm, "end": v(-79.28, 57.41) * mm});
            skLineSegment(sketch, "E837", {"start": v(-79.28, 57.41) * mm, "end": v(-79.03, 56.9) * mm});
            skLineSegment(sketch, "E838", {"start": v(-79.03, 56.9) * mm, "end": v(-78.79, 56.39) * mm});
            skLineSegment(sketch, "E839", {"start": v(-78.79, 56.39) * mm, "end": v(-78.55, 55.9) * mm});
            skLineSegment(sketch, "E840", {"start": v(-78.55, 55.9) * mm, "end": v(-78.3, 55.42) * mm});
            skLineSegment(sketch, "E841", {"start": v(-78.3, 55.42) * mm, "end": v(-78.06, 54.96) * mm});
            skLineSegment(sketch, "E842", {"start": v(-78.06, 54.96) * mm, "end": v(-77.81, 54.5) * mm});
            skLineSegment(sketch, "E843", {"start": v(-77.81, 54.5) * mm, "end": v(-77.57, 54.07) * mm});
            skLineSegment(sketch, "E844", {"start": v(-77.57, 54.07) * mm, "end": v(-77.33, 53.65) * mm});
            skLineSegment(sketch, "E845", {"start": v(-77.33, 53.65) * mm, "end": v(-77.09, 53.25) * mm});
            skLineSegment(sketch, "E846", {"start": v(-77.09, 53.25) * mm, "end": v(-76.85, 52.85) * mm});
            skLineSegment(sketch, "E847", {"start": v(-76.85, 52.85) * mm, "end": v(-76.6, 52.47) * mm});
            skLineSegment(sketch, "E848", {"start": v(-76.6, 52.47) * mm, "end": v(-76.37, 52.1) * mm});
            skLineSegment(sketch, "E849", {"start": v(-76.37, 52.1) * mm, "end": v(-76.14, 51.75) * mm});
            skLineSegment(sketch, "E850", {"start": v(-76.14, 51.75) * mm, "end": v(-75.9, 51.4) * mm});
            skLineSegment(sketch, "E851", {"start": v(-75.9, 51.4) * mm, "end": v(-75.68, 51.08) * mm});
            skLineSegment(sketch, "E852", {"start": v(-75.68, 51.08) * mm, "end": v(-75.46, 50.76) * mm});
            skLineSegment(sketch, "E853", {"start": v(-75.46, 50.76) * mm, "end": v(-75.24, 50.46) * mm});
            skLineSegment(sketch, "E854", {"start": v(-75.24, 50.46) * mm, "end": v(-75.02, 50.17) * mm});
            skLineSegment(sketch, "E855", {"start": v(-75.02, 50.17) * mm, "end": v(-74.8, 49.9) * mm});
            skLineSegment(sketch, "E856", {"start": v(-74.8, 49.9) * mm, "end": v(-74.6, 49.63) * mm});
            skLineSegment(sketch, "E857", {"start": v(-74.6, 49.63) * mm, "end": v(-74.4, 49.38) * mm});
            skLineSegment(sketch, "E858", {"start": v(-74.4, 49.38) * mm, "end": v(-74.2, 49.14) * mm});
            skLineSegment(sketch, "E859", {"start": v(-74.2, 49.14) * mm, "end": v(-74, 48.9) * mm});
            skLineSegment(sketch, "E860", {"start": v(-74, 48.9) * mm, "end": v(-73.81, 48.69) * mm});
            skLineSegment(sketch, "E861", {"start": v(-73.81, 48.69) * mm, "end": v(-73.63, 48.48) * mm});
            skLineSegment(sketch, "E862", {"start": v(-73.63, 48.48) * mm, "end": v(-73.88, 48.04) * mm});
            skLineSegment(sketch, "E863", {"start": v(-73.88, 48.04) * mm, "end": v(-75.5, 45.45) * mm});
            skLineSegment(sketch, "E864", {"start": v(-75.5, 45.45) * mm, "end": v(-75.79, 45.03) * mm});
            skLineSegment(sketch, "E865", {"start": v(-75.79, 45.03) * mm, "end": v(-76.05, 45.1) * mm});
            skLineSegment(sketch, "E866", {"start": v(-76.05, 45.1) * mm, "end": v(-76.33, 45.18) * mm});
            skLineSegment(sketch, "E867", {"start": v(-76.33, 45.18) * mm, "end": v(-76.62, 45.25) * mm});
            skLineSegment(sketch, "E868", {"start": v(-76.62, 45.25) * mm, "end": v(-76.93, 45.33) * mm});
            skLineSegment(sketch, "E869", {"start": v(-76.93, 45.33) * mm, "end": v(-77.25, 45.4) * mm});
            skLineSegment(sketch, "E870", {"start": v(-77.25, 45.4) * mm, "end": v(-77.57, 45.47) * mm});
            skLineSegment(sketch, "E871", {"start": v(-77.57, 45.47) * mm, "end": v(-77.92, 45.54) * mm});
            skLineSegment(sketch, "E872", {"start": v(-77.92, 45.54) * mm, "end": v(-78.27, 45.6) * mm});
            skLineSegment(sketch, "E873", {"start": v(-78.27, 45.6) * mm, "end": v(-78.64, 45.68) * mm});
            skLineSegment(sketch, "E874", {"start": v(-78.64, 45.68) * mm, "end": v(-79.02, 45.74) * mm});
            skLineSegment(sketch, "E875", {"start": v(-79.02, 45.74) * mm, "end": v(-79.42, 45.8) * mm});
            skLineSegment(sketch, "E876", {"start": v(-79.42, 45.8) * mm, "end": v(-79.82, 45.86) * mm});
            skLineSegment(sketch, "E877", {"start": v(-79.82, 45.86) * mm, "end": v(-80.25, 45.91) * mm});
            skLineSegment(sketch, "E878", {"start": v(-80.25, 45.91) * mm, "end": v(-80.68, 45.97) * mm});
            skLineSegment(sketch, "E879", {"start": v(-80.68, 45.97) * mm, "end": v(-81.13, 46.01) * mm});
            skLineSegment(sketch, "E880", {"start": v(-81.13, 46.01) * mm, "end": v(-81.58, 46.05) * mm});
            skLineSegment(sketch, "E881", {"start": v(-81.58, 46.05) * mm, "end": v(-82.06, 46.1) * mm});
            skLineSegment(sketch, "E882", {"start": v(-82.06, 46.1) * mm, "end": v(-82.54, 46.13) * mm});
            skLineSegment(sketch, "E883", {"start": v(-82.54, 46.13) * mm, "end": v(-83.04, 46.16) * mm});
            skLineSegment(sketch, "E884", {"start": v(-83.04, 46.16) * mm, "end": v(-83.55, 46.18) * mm});
            skLineSegment(sketch, "E885", {"start": v(-83.55, 46.18) * mm, "end": v(-84.07, 46.2) * mm});
            skLineSegment(sketch, "E886", {"start": v(-84.07, 46.2) * mm, "end": v(-84.6, 46.2) * mm});
            skLineSegment(sketch, "E887", {"start": v(-84.6, 46.2) * mm, "end": v(-85.16, 46.21) * mm});
            skLineSegment(sketch, "E888", {"start": v(-85.16, 46.21) * mm, "end": v(-85.72, 46.21) * mm});
            skLineSegment(sketch, "E889", {"start": v(-85.72, 46.21) * mm, "end": v(-86.29, 46.2) * mm});
            skLineSegment(sketch, "E890", {"start": v(-86.29, 46.2) * mm, "end": v(-86.87, 46.19) * mm});
            skLineSegment(sketch, "E891", {"start": v(-86.87, 46.19) * mm, "end": v(-87.47, 46.16) * mm});
            skLineSegment(sketch, "E892", {"start": v(-87.47, 46.16) * mm, "end": v(-88.08, 46.13) * mm});
            skLineSegment(sketch, "E893", {"start": v(-88.08, 46.13) * mm, "end": v(-88.7, 46.1) * mm});
            skLineSegment(sketch, "E894", {"start": v(-88.7, 46.1) * mm, "end": v(-89.33, 46.04) * mm});
            skLineSegment(sketch, "E895", {"start": v(-89.33, 46.04) * mm, "end": v(-89.98, 45.99) * mm});
            skLineSegment(sketch, "E896", {"start": v(-89.98, 45.99) * mm, "end": v(-90.63, 45.92) * mm});
            skLineSegment(sketch, "E897", {"start": v(-90.63, 45.92) * mm, "end": v(-91.3, 45.85) * mm});
            skLineSegment(sketch, "E898", {"start": v(-91.3, 45.85) * mm, "end": v(-91.63, 45.6) * mm});
            skLineSegment(sketch, "E899", {"start": v(-91.63, 45.6) * mm, "end": v(-92.61, 43.56) * mm});
            skLineSegment(sketch, "E900", {"start": v(-92.61, 43.56) * mm, "end": v(-92.61, 43.14) * mm});
            skLineSegment(sketch, "E901", {"start": v(-92.61, 43.14) * mm, "end": v(-92.25, 42.57) * mm});
            skLineSegment(sketch, "E902", {"start": v(-92.25, 42.57) * mm, "end": v(-91.9, 42.01) * mm});
            skLineSegment(sketch, "E903", {"start": v(-91.9, 42.01) * mm, "end": v(-91.54, 41.47) * mm});
            skLineSegment(sketch, "E904", {"start": v(-91.54, 41.47) * mm, "end": v(-91.19, 40.95) * mm});
            skLineSegment(sketch, "E905", {"start": v(-91.19, 40.95) * mm, "end": v(-90.83, 40.44) * mm});
            skLineSegment(sketch, "E906", {"start": v(-90.83, 40.44) * mm, "end": v(-90.48, 39.94) * mm});
            skLineSegment(sketch, "E907", {"start": v(-90.48, 39.94) * mm, "end": v(-90.13, 39.46) * mm});
            skLineSegment(sketch, "E908", {"start": v(-90.13, 39.46) * mm, "end": v(-89.78, 38.99) * mm});
            skLineSegment(sketch, "E909", {"start": v(-89.78, 38.99) * mm, "end": v(-89.43, 38.53) * mm});
            skLineSegment(sketch, "E910", {"start": v(-89.43, 38.53) * mm, "end": v(-89.08, 38.1) * mm});
            skLineSegment(sketch, "E911", {"start": v(-89.08, 38.1) * mm, "end": v(-88.74, 37.67) * mm});
            skLineSegment(sketch, "E912", {"start": v(-88.74, 37.67) * mm, "end": v(-88.4, 37.26) * mm});
            skLineSegment(sketch, "E913", {"start": v(-88.4, 37.26) * mm, "end": v(-88.06, 36.86) * mm});
            skLineSegment(sketch, "E914", {"start": v(-88.06, 36.86) * mm, "end": v(-87.73, 36.47) * mm});
            skLineSegment(sketch, "E915", {"start": v(-87.73, 36.47) * mm, "end": v(-87.4, 36.1) * mm});
            skLineSegment(sketch, "E916", {"start": v(-87.4, 36.1) * mm, "end": v(-87.07, 35.74) * mm});
            skLineSegment(sketch, "E917", {"start": v(-87.07, 35.74) * mm, "end": v(-86.74, 35.4) * mm});
            skLineSegment(sketch, "E918", {"start": v(-86.74, 35.4) * mm, "end": v(-86.42, 35.06) * mm});
            skLineSegment(sketch, "E919", {"start": v(-86.42, 35.06) * mm, "end": v(-86.11, 34.74) * mm});
            skLineSegment(sketch, "E920", {"start": v(-86.11, 34.74) * mm, "end": v(-85.8, 34.43) * mm});
            skLineSegment(sketch, "E921", {"start": v(-85.8, 34.43) * mm, "end": v(-85.5, 34.13) * mm});
            skLineSegment(sketch, "E922", {"start": v(-85.5, 34.13) * mm, "end": v(-85.2, 33.85) * mm});
            skLineSegment(sketch, "E923", {"start": v(-85.2, 33.85) * mm, "end": v(-84.9, 33.58) * mm});
            skLineSegment(sketch, "E924", {"start": v(-84.9, 33.58) * mm, "end": v(-84.62, 33.32) * mm});
            skLineSegment(sketch, "E925", {"start": v(-84.62, 33.32) * mm, "end": v(-84.34, 33.07) * mm});
            skLineSegment(sketch, "E926", {"start": v(-84.34, 33.07) * mm, "end": v(-84.07, 32.84) * mm});
            skLineSegment(sketch, "E927", {"start": v(-84.07, 32.84) * mm, "end": v(-83.8, 32.6) * mm});
            skLineSegment(sketch, "E928", {"start": v(-83.8, 32.6) * mm, "end": v(-83.54, 32.4) * mm});
            skLineSegment(sketch, "E929", {"start": v(-83.54, 32.4) * mm, "end": v(-83.28, 32.2) * mm});
            skLineSegment(sketch, "E930", {"start": v(-83.28, 32.2) * mm, "end": v(-83.04, 32) * mm});
            skLineSegment(sketch, "E931", {"start": v(-83.04, 32) * mm, "end": v(-82.8, 31.82) * mm});
            skLineSegment(sketch, "E932", {"start": v(-82.8, 31.82) * mm, "end": v(-82.57, 31.65) * mm});
            skLineSegment(sketch, "E933", {"start": v(-82.57, 31.65) * mm, "end": v(-82.34, 31.49) * mm});
            skLineSegment(sketch, "E934", {"start": v(-82.34, 31.49) * mm, "end": v(-82.5, 31) * mm});
            skLineSegment(sketch, "E935", {"start": v(-82.5, 31) * mm, "end": v(-83.52, 28.12) * mm});
            skLineSegment(sketch, "E936", {"start": v(-83.52, 28.12) * mm, "end": v(-83.71, 27.65) * mm});
            skLineSegment(sketch, "E937", {"start": v(-83.71, 27.65) * mm, "end": v(-83.99, 27.66) * mm});
            skLineSegment(sketch, "E938", {"start": v(-83.99, 27.66) * mm, "end": v(-84.27, 27.68) * mm});
            skLineSegment(sketch, "E939", {"start": v(-84.27, 27.68) * mm, "end": v(-84.57, 27.69) * mm});
            skLineSegment(sketch, "E940", {"start": v(-84.57, 27.69) * mm, "end": v(-84.89, 27.7) * mm});
            skLineSegment(sketch, "E941", {"start": v(-84.89, 27.7) * mm, "end": v(-85.21, 27.7) * mm});
            skLineSegment(sketch, "E942", {"start": v(-85.21, 27.7) * mm, "end": v(-85.55, 27.7) * mm});
            skLineSegment(sketch, "E943", {"start": v(-85.55, 27.7) * mm, "end": v(-85.9, 27.69) * mm});
            skLineSegment(sketch, "E944", {"start": v(-85.9, 27.69) * mm, "end": v(-86.26, 27.68) * mm});
            skLineSegment(sketch, "E945", {"start": v(-86.26, 27.68) * mm, "end": v(-86.64, 27.67) * mm});
            skLineSegment(sketch, "E946", {"start": v(-86.64, 27.67) * mm, "end": v(-87.02, 27.65) * mm});
            skLineSegment(sketch, "E947", {"start": v(-87.02, 27.65) * mm, "end": v(-87.42, 27.62) * mm});
            skLineSegment(sketch, "E948", {"start": v(-87.42, 27.62) * mm, "end": v(-87.83, 27.6) * mm});
            skLineSegment(sketch, "E949", {"start": v(-87.83, 27.6) * mm, "end": v(-88.25, 27.55) * mm});
            skLineSegment(sketch, "E950", {"start": v(-88.25, 27.55) * mm, "end": v(-88.69, 27.5) * mm});
            skLineSegment(sketch, "E951", {"start": v(-88.69, 27.5) * mm, "end": v(-89.13, 27.46) * mm});
            skLineSegment(sketch, "E952", {"start": v(-89.13, 27.46) * mm, "end": v(-89.6, 27.4) * mm});
            skLineSegment(sketch, "E953", {"start": v(-89.6, 27.4) * mm, "end": v(-90.06, 27.34) * mm});
            skLineSegment(sketch, "E954", {"start": v(-90.06, 27.34) * mm, "end": v(-90.54, 27.27) * mm});
            skLineSegment(sketch, "E955", {"start": v(-90.54, 27.27) * mm, "end": v(-91.03, 27.19) * mm});
            skLineSegment(sketch, "E956", {"start": v(-91.03, 27.19) * mm, "end": v(-91.54, 27.1) * mm});
            skLineSegment(sketch, "E957", {"start": v(-91.54, 27.1) * mm, "end": v(-92.05, 27) * mm});
            skLineSegment(sketch, "E958", {"start": v(-92.05, 27) * mm, "end": v(-92.58, 26.9) * mm});
            skLineSegment(sketch, "E959", {"start": v(-92.58, 26.9) * mm, "end": v(-93.11, 26.79) * mm});
            skLineSegment(sketch, "E960", {"start": v(-93.11, 26.79) * mm, "end": v(-93.66, 26.67) * mm});
            skLineSegment(sketch, "E961", {"start": v(-93.66, 26.67) * mm, "end": v(-94.22, 26.54) * mm});
            skLineSegment(sketch, "E962", {"start": v(-94.22, 26.54) * mm, "end": v(-94.78, 26.4) * mm});
            skLineSegment(sketch, "E963", {"start": v(-94.78, 26.4) * mm, "end": v(-95.36, 26.24) * mm});
            skLineSegment(sketch, "E964", {"start": v(-95.36, 26.24) * mm, "end": v(-95.95, 26.08) * mm});
            skLineSegment(sketch, "E965", {"start": v(-95.95, 26.08) * mm, "end": v(-96.55, 25.9) * mm});
            skLineSegment(sketch, "E966", {"start": v(-96.55, 25.9) * mm, "end": v(-97.16, 25.73) * mm});
            skLineSegment(sketch, "E967", {"start": v(-97.16, 25.73) * mm, "end": v(-97.77, 25.53) * mm});
            skLineSegment(sketch, "E968", {"start": v(-97.77, 25.53) * mm, "end": v(-98.4, 25.33) * mm});
            skLineSegment(sketch, "E969", {"start": v(-98.4, 25.33) * mm, "end": v(-99.03, 25.11) * mm});
            skLineSegment(sketch, "E970", {"start": v(-99.03, 25.11) * mm, "end": v(-99.3, 24.79) * mm});
            skLineSegment(sketch, "E971", {"start": v(-99.3, 24.79) * mm, "end": v(-99.82, 22.6) * mm});
            skLineSegment(sketch, "E972", {"start": v(-99.82, 22.6) * mm, "end": v(-99.73, 22.19) * mm});
            skLineSegment(sketch, "E973", {"start": v(-99.73, 22.19) * mm, "end": v(-99.26, 21.7) * mm});
            skLineSegment(sketch, "E974", {"start": v(-99.26, 21.7) * mm, "end": v(-98.8, 21.24) * mm});
            skLineSegment(sketch, "E975", {"start": v(-98.8, 21.24) * mm, "end": v(-98.33, 20.79) * mm});
            skLineSegment(sketch, "E976", {"start": v(-98.33, 20.79) * mm, "end": v(-97.87, 20.35) * mm});
            skLineSegment(sketch, "E977", {"start": v(-97.87, 20.35) * mm, "end": v(-97.42, 19.93) * mm});
            skLineSegment(sketch, "E978", {"start": v(-97.42, 19.93) * mm, "end": v(-96.96, 19.52) * mm});
            skLineSegment(sketch, "E979", {"start": v(-96.96, 19.52) * mm, "end": v(-96.52, 19.12) * mm});
            skLineSegment(sketch, "E980", {"start": v(-96.52, 19.12) * mm, "end": v(-96.07, 18.74) * mm});
            skLineSegment(sketch, "E981", {"start": v(-96.07, 18.74) * mm, "end": v(-95.64, 18.37) * mm});
            skLineSegment(sketch, "E982", {"start": v(-95.64, 18.37) * mm, "end": v(-95.2, 18.02) * mm});
            skLineSegment(sketch, "E983", {"start": v(-95.2, 18.02) * mm, "end": v(-94.77, 17.67) * mm});
            skLineSegment(sketch, "E984", {"start": v(-94.77, 17.67) * mm, "end": v(-94.35, 17.34) * mm});
            skLineSegment(sketch, "E985", {"start": v(-94.35, 17.34) * mm, "end": v(-93.94, 17.03) * mm});
            skLineSegment(sketch, "E986", {"start": v(-93.94, 17.03) * mm, "end": v(-93.53, 16.72) * mm});
            skLineSegment(sketch, "E987", {"start": v(-93.53, 16.72) * mm, "end": v(-93.12, 16.43) * mm});
            skLineSegment(sketch, "E988", {"start": v(-93.12, 16.43) * mm, "end": v(-92.73, 16.15) * mm});
            skLineSegment(sketch, "E989", {"start": v(-92.73, 16.15) * mm, "end": v(-92.34, 15.88) * mm});
            skLineSegment(sketch, "E990", {"start": v(-92.34, 15.88) * mm, "end": v(-91.95, 15.62) * mm});
            skLineSegment(sketch, "E991", {"start": v(-91.95, 15.62) * mm, "end": v(-91.58, 15.38) * mm});
            skLineSegment(sketch, "E992", {"start": v(-91.58, 15.38) * mm, "end": v(-91.21, 15.14) * mm});
            skLineSegment(sketch, "E993", {"start": v(-91.21, 15.14) * mm, "end": v(-90.85, 14.92) * mm});
            skLineSegment(sketch, "E994", {"start": v(-90.85, 14.92) * mm, "end": v(-90.5, 14.7) * mm});
            skLineSegment(sketch, "E995", {"start": v(-90.5, 14.7) * mm, "end": v(-90.15, 14.5) * mm});
            skLineSegment(sketch, "E996", {"start": v(-90.15, 14.5) * mm, "end": v(-89.82, 14.31) * mm});
            skLineSegment(sketch, "E997", {"start": v(-89.82, 14.31) * mm, "end": v(-89.49, 14.13) * mm});
            skLineSegment(sketch, "E998", {"start": v(-89.49, 14.13) * mm, "end": v(-89.17, 13.96) * mm});
            skLineSegment(sketch, "E999", {"start": v(-89.17, 13.96) * mm, "end": v(-88.86, 13.8) * mm});
            skLineSegment(sketch, "E1000", {"start": v(-88.86, 13.8) * mm, "end": v(-88.56, 13.64) * mm});
            skLineSegment(sketch, "E1001", {"start": v(-88.56, 13.64) * mm, "end": v(-88.27, 13.5) * mm});
            skLineSegment(sketch, "E1002", {"start": v(-88.27, 13.5) * mm, "end": v(-87.99, 13.37) * mm});
            skLineSegment(sketch, "E1003", {"start": v(-87.99, 13.37) * mm, "end": v(-87.72, 13.24) * mm});
            skLineSegment(sketch, "E1004", {"start": v(-87.72, 13.24) * mm, "end": v(-87.45, 13.12) * mm});
            skLineSegment(sketch, "E1005", {"start": v(-87.45, 13.12) * mm, "end": v(-87.2, 13) * mm});
            skLineSegment(sketch, "E1006", {"start": v(-87.2, 13) * mm, "end": v(-87.24, 12.5) * mm});
            skLineSegment(sketch, "E1007", {"start": v(-87.24, 12.5) * mm, "end": v(-87.62, 9.47) * mm});
            skLineSegment(sketch, "E1008", {"start": v(-87.62, 9.47) * mm, "end": v(-87.71, 8.97) * mm});
            skLineSegment(sketch, "E1009", {"start": v(-87.71, 8.97) * mm, "end": v(-87.98, 8.93) * mm});
            skLineSegment(sketch, "E1010", {"start": v(-87.98, 8.93) * mm, "end": v(-88.27, 8.88) * mm});
            skLineSegment(sketch, "E1011", {"start": v(-88.27, 8.88) * mm, "end": v(-88.56, 8.82) * mm});
            skLineSegment(sketch, "E1012", {"start": v(-88.56, 8.82) * mm, "end": v(-88.87, 8.76) * mm});
            skLineSegment(sketch, "E1013", {"start": v(-88.87, 8.76) * mm, "end": v(-89.19, 8.7) * mm});
            skLineSegment(sketch, "E1014", {"start": v(-89.19, 8.7) * mm, "end": v(-89.52, 8.62) * mm});
            skLineSegment(sketch, "E1015", {"start": v(-89.52, 8.62) * mm, "end": v(-89.86, 8.54) * mm});
            skLineSegment(sketch, "E1016", {"start": v(-89.86, 8.54) * mm, "end": v(-90.2, 8.45) * mm});
            skLineSegment(sketch, "E1017", {"start": v(-90.2, 8.45) * mm, "end": v(-90.57, 8.36) * mm});
            skLineSegment(sketch, "E1018", {"start": v(-90.57, 8.36) * mm, "end": v(-90.94, 8.26) * mm});
            skLineSegment(sketch, "E1019", {"start": v(-90.94, 8.26) * mm, "end": v(-91.33, 8.15) * mm});
            skLineSegment(sketch, "E1020", {"start": v(-91.33, 8.15) * mm, "end": v(-91.72, 8.03) * mm});
            skLineSegment(sketch, "E1021", {"start": v(-91.72, 8.03) * mm, "end": v(-92.13, 7.9) * mm});
            skLineSegment(sketch, "E1022", {"start": v(-92.13, 7.9) * mm, "end": v(-92.54, 7.76) * mm});
            skLineSegment(sketch, "E1023", {"start": v(-92.54, 7.76) * mm, "end": v(-92.96, 7.62) * mm});
            skLineSegment(sketch, "E1024", {"start": v(-92.96, 7.62) * mm, "end": v(-93.4, 7.47) * mm});
            skLineSegment(sketch, "E1025", {"start": v(-93.4, 7.47) * mm, "end": v(-93.84, 7.3) * mm});
            skLineSegment(sketch, "E1026", {"start": v(-93.84, 7.3) * mm, "end": v(-94.3, 7.13) * mm});
            skLineSegment(sketch, "E1027", {"start": v(-94.3, 7.13) * mm, "end": v(-94.76, 6.95) * mm});
            skLineSegment(sketch, "E1028", {"start": v(-94.76, 6.95) * mm, "end": v(-95.23, 6.75) * mm});
            skLineSegment(sketch, "E1029", {"start": v(-95.23, 6.75) * mm, "end": v(-95.72, 6.55) * mm});
            skLineSegment(sketch, "E1030", {"start": v(-95.72, 6.55) * mm, "end": v(-96.2, 6.33) * mm});
            skLineSegment(sketch, "E1031", {"start": v(-96.2, 6.33) * mm, "end": v(-96.7, 6.1) * mm});
            skLineSegment(sketch, "E1032", {"start": v(-96.7, 6.1) * mm, "end": v(-97.21, 5.87) * mm});
            skLineSegment(sketch, "E1033", {"start": v(-97.21, 5.87) * mm, "end": v(-97.73, 5.62) * mm});
            skLineSegment(sketch, "E1034", {"start": v(-97.73, 5.62) * mm, "end": v(-98.25, 5.36) * mm});
            skLineSegment(sketch, "E1035", {"start": v(-98.25, 5.36) * mm, "end": v(-98.79, 5.1) * mm});
            skLineSegment(sketch, "E1036", {"start": v(-98.79, 5.1) * mm, "end": v(-99.33, 4.8) * mm});
            skLineSegment(sketch, "E1037", {"start": v(-99.33, 4.8) * mm, "end": v(-99.87, 4.51) * mm});
            skLineSegment(sketch, "E1038", {"start": v(-99.87, 4.51) * mm, "end": v(-100.43, 4.2) * mm});
            skLineSegment(sketch, "E1039", {"start": v(-100.43, 4.2) * mm, "end": v(-100.99, 3.88) * mm});
            skLineSegment(sketch, "E1040", {"start": v(-100.99, 3.88) * mm, "end": v(-101.56, 3.55) * mm});
            skLineSegment(sketch, "E1041", {"start": v(-101.56, 3.55) * mm, "end": v(-102.13, 3.2) * mm});
            skLineSegment(sketch, "E1042", {"start": v(-102.13, 3.2) * mm, "end": v(-102.32, 2.83) * mm});
            skLineSegment(sketch, "E1043", {"start": v(-102.32, 2.83) * mm, "end": v(-102.36, 0.57) * mm});
            skLineSegment(sketch, "E1044", {"start": v(-102.36, 0.57) * mm, "end": v(-102.18, 0.19) * mm});
            skLineSegment(sketch, "E1045", {"start": v(-102.18, 0.19) * mm, "end": v(-101.62, -0.18) * mm});
            skLineSegment(sketch, "E1046", {"start": v(-101.62, -0.18) * mm, "end": v(-101.06, -0.53) * mm});
            skLineSegment(sketch, "E1047", {"start": v(-101.06, -0.53) * mm, "end": v(-100.51, -0.87) * mm});
            skLineSegment(sketch, "E1048", {"start": v(-100.51, -0.87) * mm, "end": v(-99.97, -1.2) * mm});
            skLineSegment(sketch, "E1049", {"start": v(-99.97, -1.2) * mm, "end": v(-99.43, -1.52) * mm});
            skLineSegment(sketch, "E1050", {"start": v(-99.43, -1.52) * mm, "end": v(-98.9, -1.82) * mm});
            skLineSegment(sketch, "E1051", {"start": v(-98.9, -1.82) * mm, "end": v(-98.38, -2.1) * mm});
            skLineSegment(sketch, "E1052", {"start": v(-98.38, -2.1) * mm, "end": v(-97.87, -2.39) * mm});
            skLineSegment(sketch, "E1053", {"start": v(-97.87, -2.39) * mm, "end": v(-97.36, -2.65) * mm});
            skLineSegment(sketch, "E1054", {"start": v(-97.36, -2.65) * mm, "end": v(-96.86, -2.9) * mm});
            skLineSegment(sketch, "E1055", {"start": v(-96.86, -2.9) * mm, "end": v(-96.37, -3.15) * mm});
            skLineSegment(sketch, "E1056", {"start": v(-96.37, -3.15) * mm, "end": v(-95.89, -3.38) * mm});
            skLineSegment(sketch, "E1057", {"start": v(-95.89, -3.38) * mm, "end": v(-95.41, -3.6) * mm});
            skLineSegment(sketch, "E1058", {"start": v(-95.41, -3.6) * mm, "end": v(-94.95, -3.81) * mm});
            skLineSegment(sketch, "E1059", {"start": v(-94.95, -3.81) * mm, "end": v(-94.5, -4) * mm});
            skLineSegment(sketch, "E1060", {"start": v(-94.5, -4) * mm, "end": v(-94.04, -4.2) * mm});
            skLineSegment(sketch, "E1061", {"start": v(-94.04, -4.2) * mm, "end": v(-93.6, -4.38) * mm});
            skLineSegment(sketch, "E1062", {"start": v(-93.6, -4.38) * mm, "end": v(-93.18, -4.55) * mm});
            skLineSegment(sketch, "E1063", {"start": v(-93.18, -4.55) * mm, "end": v(-92.76, -4.7) * mm});
            skLineSegment(sketch, "E1064", {"start": v(-92.76, -4.7) * mm, "end": v(-92.35, -4.86) * mm});
            skLineSegment(sketch, "E1065", {"start": v(-92.35, -4.86) * mm, "end": v(-91.95, -5) * mm});
            skLineSegment(sketch, "E1066", {"start": v(-91.95, -5) * mm, "end": v(-91.56, -5.13) * mm});
            skLineSegment(sketch, "E1067", {"start": v(-91.56, -5.13) * mm, "end": v(-91.18, -5.25) * mm});
            skLineSegment(sketch, "E1068", {"start": v(-91.18, -5.25) * mm, "end": v(-90.8, -5.37) * mm});
            skLineSegment(sketch, "E1069", {"start": v(-90.8, -5.37) * mm, "end": v(-90.45, -5.47) * mm});
            skLineSegment(sketch, "E1070", {"start": v(-90.45, -5.47) * mm, "end": v(-90.1, -5.57) * mm});
            skLineSegment(sketch, "E1071", {"start": v(-90.1, -5.57) * mm, "end": v(-89.76, -5.67) * mm});
            skLineSegment(sketch, "E1072", {"start": v(-89.76, -5.67) * mm, "end": v(-89.44, -5.75) * mm});
            skLineSegment(sketch, "E1073", {"start": v(-89.44, -5.75) * mm, "end": v(-89.12, -5.83) * mm});
            skLineSegment(sketch, "E1074", {"start": v(-89.12, -5.83) * mm, "end": v(-88.82, -5.9) * mm});
            skLineSegment(sketch, "E1075", {"start": v(-88.82, -5.9) * mm, "end": v(-88.52, -5.96) * mm});
            skLineSegment(sketch, "E1076", {"start": v(-88.52, -5.96) * mm, "end": v(-88.24, -6.02) * mm});
            skLineSegment(sketch, "E1077", {"start": v(-88.24, -6.02) * mm, "end": v(-87.97, -6.08) * mm});
            skLineSegment(sketch, "E1078", {"start": v(-87.97, -6.08) * mm, "end": v(-87.9, -6.58) * mm});
            skLineSegment(sketch, "E1079", {"start": v(-87.9, -6.58) * mm, "end": v(-87.62, -9.62) * mm});
            skLineSegment(sketch, "E1080", {"start": v(-87.62, -9.62) * mm, "end": v(-87.6, -10.13) * mm});
            skLineSegment(sketch, "E1081", {"start": v(-87.6, -10.13) * mm, "end": v(-87.86, -10.23) * mm});
            skLineSegment(sketch, "E1082", {"start": v(-87.86, -10.23) * mm, "end": v(-88.12, -10.34) * mm});
            skLineSegment(sketch, "E1083", {"start": v(-88.12, -10.34) * mm, "end": v(-88.4, -10.46) * mm});
            skLineSegment(sketch, "E1084", {"start": v(-88.4, -10.46) * mm, "end": v(-88.69, -10.58) * mm});
            skLineSegment(sketch, "E1085", {"start": v(-88.69, -10.58) * mm, "end": v(-88.98, -10.72) * mm});
            skLineSegment(sketch, "E1086", {"start": v(-88.98, -10.72) * mm, "end": v(-89.29, -10.86) * mm});
            skLineSegment(sketch, "E1087", {"start": v(-89.29, -10.86) * mm, "end": v(-89.6, -11.01) * mm});
            skLineSegment(sketch, "E1088", {"start": v(-89.6, -11.01) * mm, "end": v(-89.93, -11.17) * mm});
            skLineSegment(sketch, "E1089", {"start": v(-89.93, -11.17) * mm, "end": v(-90.26, -11.34) * mm});
            skLineSegment(sketch, "E1090", {"start": v(-90.26, -11.34) * mm, "end": v(-90.6, -11.52) * mm});
            skLineSegment(sketch, "E1091", {"start": v(-90.6, -11.52) * mm, "end": v(-90.95, -11.71) * mm});
            skLineSegment(sketch, "E1092", {"start": v(-90.95, -11.71) * mm, "end": v(-91.31, -11.92) * mm});
            skLineSegment(sketch, "E1093", {"start": v(-91.31, -11.92) * mm, "end": v(-91.68, -12.13) * mm});
            skLineSegment(sketch, "E1094", {"start": v(-91.68, -12.13) * mm, "end": v(-92.06, -12.35) * mm});
            skLineSegment(sketch, "E1095", {"start": v(-92.06, -12.35) * mm, "end": v(-92.44, -12.58) * mm});
            skLineSegment(sketch, "E1096", {"start": v(-92.44, -12.58) * mm, "end": v(-92.83, -12.82) * mm});
            skLineSegment(sketch, "E1097", {"start": v(-92.83, -12.82) * mm, "end": v(-93.23, -13.08) * mm});
            skLineSegment(sketch, "E1098", {"start": v(-93.23, -13.08) * mm, "end": v(-93.64, -13.35) * mm});
            skLineSegment(sketch, "E1099", {"start": v(-93.64, -13.35) * mm, "end": v(-94.05, -13.62) * mm});
            skLineSegment(sketch, "E1100", {"start": v(-94.05, -13.62) * mm, "end": v(-94.47, -13.91) * mm});
            skLineSegment(sketch, "E1101", {"start": v(-94.47, -13.91) * mm, "end": v(-94.9, -14.22) * mm});
            skLineSegment(sketch, "E1102", {"start": v(-94.9, -14.22) * mm, "end": v(-95.33, -14.53) * mm});
            skLineSegment(sketch, "E1103", {"start": v(-95.33, -14.53) * mm, "end": v(-95.77, -14.86) * mm});
            skLineSegment(sketch, "E1104", {"start": v(-95.77, -14.86) * mm, "end": v(-96.22, -15.2) * mm});
            skLineSegment(sketch, "E1105", {"start": v(-96.22, -15.2) * mm, "end": v(-96.67, -15.55) * mm});
            skLineSegment(sketch, "E1106", {"start": v(-96.67, -15.55) * mm, "end": v(-97.12, -15.92) * mm});
            skLineSegment(sketch, "E1107", {"start": v(-97.12, -15.92) * mm, "end": v(-97.58, -16.3) * mm});
            skLineSegment(sketch, "E1108", {"start": v(-97.58, -16.3) * mm, "end": v(-98.05, -16.7) * mm});
            skLineSegment(sketch, "E1109", {"start": v(-98.05, -16.7) * mm, "end": v(-98.52, -17.1) * mm});
            skLineSegment(sketch, "E1110", {"start": v(-98.52, -17.1) * mm, "end": v(-99, -17.52) * mm});
            skLineSegment(sketch, "E1111", {"start": v(-99, -17.52) * mm, "end": v(-99.47, -17.96) * mm});
            skLineSegment(sketch, "E1112", {"start": v(-99.47, -17.96) * mm, "end": v(-99.96, -18.4) * mm});
            skLineSegment(sketch, "E1113", {"start": v(-99.96, -18.4) * mm, "end": v(-100.44, -18.87) * mm});
            skLineSegment(sketch, "E1114", {"start": v(-100.44, -18.87) * mm, "end": v(-100.55, -19.27) * mm});
            skLineSegment(sketch, "E1115", {"start": v(-100.55, -19.27) * mm, "end": v(-100.1, -21.49) * mm});
            skLineSegment(sketch, "E1116", {"start": v(-100.1, -21.49) * mm, "end": v(-99.85, -21.82) * mm});
            skLineSegment(sketch, "E1117", {"start": v(-99.85, -21.82) * mm, "end": v(-99.22, -22.06) * mm});
            skLineSegment(sketch, "E1118", {"start": v(-99.22, -22.06) * mm, "end": v(-98.6, -22.28) * mm});
            skLineSegment(sketch, "E1119", {"start": v(-98.6, -22.28) * mm, "end": v(-97.99, -22.5) * mm});
            skLineSegment(sketch, "E1120", {"start": v(-97.99, -22.5) * mm, "end": v(-97.39, -22.7) * mm});
            skLineSegment(sketch, "E1121", {"start": v(-97.39, -22.7) * mm, "end": v(-96.8, -22.9) * mm});
            skLineSegment(sketch, "E1122", {"start": v(-96.8, -22.9) * mm, "end": v(-96.22, -23.07) * mm});
            skLineSegment(sketch, "E1123", {"start": v(-96.22, -23.07) * mm, "end": v(-95.64, -23.25) * mm});
            skLineSegment(sketch, "E1124", {"start": v(-95.64, -23.25) * mm, "end": v(-95.08, -23.4) * mm});
            skLineSegment(sketch, "E1125", {"start": v(-95.08, -23.4) * mm, "end": v(-94.53, -23.56) * mm});
            skLineSegment(sketch, "E1126", {"start": v(-94.53, -23.56) * mm, "end": v(-93.99, -23.7) * mm});
            skLineSegment(sketch, "E1127", {"start": v(-93.99, -23.7) * mm, "end": v(-93.45, -23.83) * mm});
            skLineSegment(sketch, "E1128", {"start": v(-93.45, -23.83) * mm, "end": v(-92.93, -23.95) * mm});
            skLineSegment(sketch, "E1129", {"start": v(-92.93, -23.95) * mm, "end": v(-92.42, -24.07) * mm});
            skLineSegment(sketch, "E1130", {"start": v(-92.42, -24.07) * mm, "end": v(-91.92, -24.17) * mm});
            skLineSegment(sketch, "E1131", {"start": v(-91.92, -24.17) * mm, "end": v(-91.43, -24.26) * mm});
            skLineSegment(sketch, "E1132", {"start": v(-91.43, -24.26) * mm, "end": v(-90.95, -24.35) * mm});
            skLineSegment(sketch, "E1133", {"start": v(-90.95, -24.35) * mm, "end": v(-90.49, -24.43) * mm});
            skLineSegment(sketch, "E1134", {"start": v(-90.49, -24.43) * mm, "end": v(-90.03, -24.5) * mm});
            skLineSegment(sketch, "E1135", {"start": v(-90.03, -24.5) * mm, "end": v(-89.59, -24.57) * mm});
            skLineSegment(sketch, "E1136", {"start": v(-89.59, -24.57) * mm, "end": v(-89.16, -24.63) * mm});
            skLineSegment(sketch, "E1137", {"start": v(-89.16, -24.63) * mm, "end": v(-88.74, -24.68) * mm});
            skLineSegment(sketch, "E1138", {"start": v(-88.74, -24.68) * mm, "end": v(-88.33, -24.73) * mm});
            skLineSegment(sketch, "E1139", {"start": v(-88.33, -24.73) * mm, "end": v(-87.93, -24.77) * mm});
            skLineSegment(sketch, "E1140", {"start": v(-87.93, -24.77) * mm, "end": v(-87.54, -24.8) * mm});
            skLineSegment(sketch, "E1141", {"start": v(-87.54, -24.8) * mm, "end": v(-87.17, -24.83) * mm});
            skLineSegment(sketch, "E1142", {"start": v(-87.17, -24.83) * mm, "end": v(-86.8, -24.85) * mm});
            skLineSegment(sketch, "E1143", {"start": v(-86.8, -24.85) * mm, "end": v(-86.46, -24.87) * mm});
            skLineSegment(sketch, "E1144", {"start": v(-86.46, -24.87) * mm, "end": v(-86.12, -24.88) * mm});
            skLineSegment(sketch, "E1145", {"start": v(-86.12, -24.88) * mm, "end": v(-85.8, -24.89) * mm});
            skLineSegment(sketch, "E1146", {"start": v(-85.8, -24.89) * mm, "end": v(-85.48, -24.9) * mm});
            skLineSegment(sketch, "E1147", {"start": v(-85.48, -24.9) * mm, "end": v(-85.18, -24.9) * mm});
            skLineSegment(sketch, "E1148", {"start": v(-85.18, -24.9) * mm, "end": v(-84.9, -24.89) * mm});
            skLineSegment(sketch, "E1149", {"start": v(-84.9, -24.89) * mm, "end": v(-84.62, -24.88) * mm});
            skLineSegment(sketch, "E1150", {"start": v(-84.62, -24.88) * mm, "end": v(-84.44, -25.36) * mm});
            skLineSegment(sketch, "E1151", {"start": v(-84.44, -25.36) * mm, "end": v(-83.52, -28.27) * mm});
            skLineSegment(sketch, "E1152", {"start": v(-83.52, -28.27) * mm, "end": v(-83.39, -28.76) * mm});
            skLineSegment(sketch, "E1153", {"start": v(-83.39, -28.76) * mm, "end": v(-83.62, -28.92) * mm});
            skLineSegment(sketch, "E1154", {"start": v(-83.62, -28.92) * mm, "end": v(-83.85, -29.08) * mm});
            skLineSegment(sketch, "E1155", {"start": v(-83.85, -29.08) * mm, "end": v(-84.1, -29.26) * mm});
            skLineSegment(sketch, "E1156", {"start": v(-84.1, -29.26) * mm, "end": v(-84.35, -29.44) * mm});
            skLineSegment(sketch, "E1157", {"start": v(-84.35, -29.44) * mm, "end": v(-84.61, -29.63) * mm});
            skLineSegment(sketch, "E1158", {"start": v(-84.61, -29.63) * mm, "end": v(-84.88, -29.84) * mm});
            skLineSegment(sketch, "E1159", {"start": v(-84.88, -29.84) * mm, "end": v(-85.15, -30.05) * mm});
            skLineSegment(sketch, "E1160", {"start": v(-85.15, -30.05) * mm, "end": v(-85.44, -30.28) * mm});
            skLineSegment(sketch, "E1161", {"start": v(-85.44, -30.28) * mm, "end": v(-85.72, -30.52) * mm});
            skLineSegment(sketch, "E1162", {"start": v(-85.72, -30.52) * mm, "end": v(-86.02, -30.77) * mm});
            skLineSegment(sketch, "E1163", {"start": v(-86.02, -30.77) * mm, "end": v(-86.32, -31.03) * mm});
            skLineSegment(sketch, "E1164", {"start": v(-86.32, -31.03) * mm, "end": v(-86.63, -31.3) * mm});
            skLineSegment(sketch, "E1165", {"start": v(-86.63, -31.3) * mm, "end": v(-86.94, -31.59) * mm});
            skLineSegment(sketch, "E1166", {"start": v(-86.94, -31.59) * mm, "end": v(-87.26, -31.89) * mm});
            skLineSegment(sketch, "E1167", {"start": v(-87.26, -31.89) * mm, "end": v(-87.59, -32.2) * mm});
            skLineSegment(sketch, "E1168", {"start": v(-87.59, -32.2) * mm, "end": v(-87.92, -32.52) * mm});
            skLineSegment(sketch, "E1169", {"start": v(-87.92, -32.52) * mm, "end": v(-88.25, -32.85) * mm});
            skLineSegment(sketch, "E1170", {"start": v(-88.25, -32.85) * mm, "end": v(-88.6, -33.2) * mm});
            skLineSegment(sketch, "E1171", {"start": v(-88.6, -33.2) * mm, "end": v(-88.94, -33.56) * mm});
            skLineSegment(sketch, "E1172", {"start": v(-88.94, -33.56) * mm, "end": v(-89.29, -33.93) * mm});
            skLineSegment(sketch, "E1173", {"start": v(-89.29, -33.93) * mm, "end": v(-89.64, -34.32) * mm});
            skLineSegment(sketch, "E1174", {"start": v(-89.64, -34.32) * mm, "end": v(-90, -34.72) * mm});
            skLineSegment(sketch, "E1175", {"start": v(-90, -34.72) * mm, "end": v(-90.35, -35.14) * mm});
            skLineSegment(sketch, "E1176", {"start": v(-90.35, -35.14) * mm, "end": v(-90.71, -35.57) * mm});
            skLineSegment(sketch, "E1177", {"start": v(-90.71, -35.57) * mm, "end": v(-91.08, -36) * mm});
            skLineSegment(sketch, "E1178", {"start": v(-91.08, -36) * mm, "end": v(-91.44, -36.46) * mm});
            skLineSegment(sketch, "E1179", {"start": v(-91.44, -36.46) * mm, "end": v(-91.81, -36.93) * mm});
            skLineSegment(sketch, "E1180", {"start": v(-91.81, -36.93) * mm, "end": v(-92.18, -37.42) * mm});
            skLineSegment(sketch, "E1181", {"start": v(-92.18, -37.42) * mm, "end": v(-92.55, -37.92) * mm});
            skLineSegment(sketch, "E1182", {"start": v(-92.55, -37.92) * mm, "end": v(-92.93, -38.43) * mm});
            skLineSegment(sketch, "E1183", {"start": v(-92.93, -38.43) * mm, "end": v(-93.3, -38.96) * mm});
            skLineSegment(sketch, "E1184", {"start": v(-93.3, -38.96) * mm, "end": v(-93.68, -39.5) * mm});
            skLineSegment(sketch, "E1185", {"start": v(-93.68, -39.5) * mm, "end": v(-94.05, -40.06) * mm});
            skLineSegment(sketch, "E1186", {"start": v(-94.05, -40.06) * mm, "end": v(-94.07, -40.47) * mm});
            skLineSegment(sketch, "E1187", {"start": v(-94.07, -40.47) * mm, "end": v(-93.16, -42.54) * mm});
            skLineSegment(sketch, "E1188", {"start": v(-93.16, -42.54) * mm, "end": v(-92.83, -42.8) * mm});
            skLineSegment(sketch, "E1189", {"start": v(-92.83, -42.8) * mm, "end": v(-92.17, -42.9) * mm});
            skLineSegment(sketch, "E1190", {"start": v(-92.17, -42.9) * mm, "end": v(-91.52, -43) * mm});
            skLineSegment(sketch, "E1191", {"start": v(-91.52, -43) * mm, "end": v(-90.88, -43.07) * mm});
            skLineSegment(sketch, "E1192", {"start": v(-90.88, -43.07) * mm, "end": v(-90.24, -43.14) * mm});
            skLineSegment(sketch, "E1193", {"start": v(-90.24, -43.14) * mm, "end": v(-89.63, -43.2) * mm});
            skLineSegment(sketch, "E1194", {"start": v(-89.63, -43.2) * mm, "end": v(-89.02, -43.26) * mm});
            skLineSegment(sketch, "E1195", {"start": v(-89.02, -43.26) * mm, "end": v(-88.42, -43.3) * mm});
            skLineSegment(sketch, "E1196", {"start": v(-88.42, -43.3) * mm, "end": v(-87.84, -43.34) * mm});
            skLineSegment(sketch, "E1197", {"start": v(-87.84, -43.34) * mm, "end": v(-87.27, -43.36) * mm});
            skLineSegment(sketch, "E1198", {"start": v(-87.27, -43.36) * mm, "end": v(-86.7, -43.39) * mm});
            skLineSegment(sketch, "E1199", {"start": v(-86.7, -43.39) * mm, "end": v(-86.16, -43.4) * mm});
            skLineSegment(sketch, "E1200", {"start": v(-86.16, -43.4) * mm, "end": v(-85.62, -43.4) * mm});
            skLineSegment(sketch, "E1201", {"start": v(-85.62, -43.4) * mm, "end": v(-85.1, -43.4) * mm});
            skLineSegment(sketch, "E1202", {"start": v(-85.1, -43.4) * mm, "end": v(-84.59, -43.4) * mm});
            skLineSegment(sketch, "E1203", {"start": v(-84.59, -43.4) * mm, "end": v(-84.1, -43.4) * mm});
            skLineSegment(sketch, "E1204", {"start": v(-84.1, -43.4) * mm, "end": v(-83.6, -43.37) * mm});
            skLineSegment(sketch, "E1205", {"start": v(-83.6, -43.37) * mm, "end": v(-83.13, -43.35) * mm});
            skLineSegment(sketch, "E1206", {"start": v(-83.13, -43.35) * mm, "end": v(-82.67, -43.32) * mm});
            skLineSegment(sketch, "E1207", {"start": v(-82.67, -43.32) * mm, "end": v(-82.22, -43.3) * mm});
            skLineSegment(sketch, "E1208", {"start": v(-82.22, -43.3) * mm, "end": v(-81.79, -43.26) * mm});
            skLineSegment(sketch, "E1209", {"start": v(-81.79, -43.26) * mm, "end": v(-81.37, -43.22) * mm});
            skLineSegment(sketch, "E1210", {"start": v(-81.37, -43.22) * mm, "end": v(-80.96, -43.17) * mm});
            skLineSegment(sketch, "E1211", {"start": v(-80.96, -43.17) * mm, "end": v(-80.56, -43.12) * mm});
            skLineSegment(sketch, "E1212", {"start": v(-80.56, -43.12) * mm, "end": v(-80.18, -43.08) * mm});
            skLineSegment(sketch, "E1213", {"start": v(-80.18, -43.08) * mm, "end": v(-79.8, -43.02) * mm});
            skLineSegment(sketch, "E1214", {"start": v(-79.8, -43.02) * mm, "end": v(-79.45, -42.96) * mm});
            skLineSegment(sketch, "E1215", {"start": v(-79.45, -42.96) * mm, "end": v(-79.1, -42.9) * mm});
            skLineSegment(sketch, "E1216", {"start": v(-79.1, -42.9) * mm, "end": v(-78.77, -42.85) * mm});
            skLineSegment(sketch, "E1217", {"start": v(-78.77, -42.85) * mm, "end": v(-78.45, -42.79) * mm});
            skLineSegment(sketch, "E1218", {"start": v(-78.45, -42.79) * mm, "end": v(-78.15, -42.72) * mm});
            skLineSegment(sketch, "E1219", {"start": v(-78.15, -42.72) * mm, "end": v(-77.85, -42.66) * mm});
            skLineSegment(sketch, "E1220", {"start": v(-77.85, -42.66) * mm, "end": v(-77.57, -42.6) * mm});
            skLineSegment(sketch, "E1221", {"start": v(-77.57, -42.6) * mm, "end": v(-77.3, -42.53) * mm});
            skLineSegment(sketch, "E1222", {"start": v(-77.3, -42.53) * mm, "end": v(-77.03, -42.96) * mm});
            skLineSegment(sketch, "E1223", {"start": v(-77.03, -42.96) * mm, "end": v(-75.5, -45.6) * mm});
            skLineSegment(sketch, "E1224", {"start": v(-75.5, -45.6) * mm, "end": v(-75.27, -46.05) * mm});
            skLineSegment(sketch, "E1225", {"start": v(-75.27, -46.05) * mm, "end": v(-75.46, -46.25) * mm});
            skLineSegment(sketch, "E1226", {"start": v(-75.46, -46.25) * mm, "end": v(-75.65, -46.46) * mm});
            skLineSegment(sketch, "E1227", {"start": v(-75.65, -46.46) * mm, "end": v(-75.85, -46.69) * mm});
            skLineSegment(sketch, "E1228", {"start": v(-75.85, -46.69) * mm, "end": v(-76.06, -46.92) * mm});
            skLineSegment(sketch, "E1229", {"start": v(-76.06, -46.92) * mm, "end": v(-76.28, -47.17) * mm});
            skLineSegment(sketch, "E1230", {"start": v(-76.28, -47.17) * mm, "end": v(-76.5, -47.42) * mm});
            skLineSegment(sketch, "E1231", {"start": v(-76.5, -47.42) * mm, "end": v(-76.71, -47.7) * mm});
            skLineSegment(sketch, "E1232", {"start": v(-76.71, -47.7) * mm, "end": v(-76.94, -47.98) * mm});
            skLineSegment(sketch, "E1233", {"start": v(-76.94, -47.98) * mm, "end": v(-77.17, -48.27) * mm});
            skLineSegment(sketch, "E1234", {"start": v(-77.17, -48.27) * mm, "end": v(-77.4, -48.58) * mm});
            skLineSegment(sketch, "E1235", {"start": v(-77.4, -48.58) * mm, "end": v(-77.65, -48.9) * mm});
            skLineSegment(sketch, "E1236", {"start": v(-77.65, -48.9) * mm, "end": v(-77.89, -49.23) * mm});
            skLineSegment(sketch, "E1237", {"start": v(-77.89, -49.23) * mm, "end": v(-78.13, -49.58) * mm});
            skLineSegment(sketch, "E1238", {"start": v(-78.13, -49.58) * mm, "end": v(-78.38, -49.94) * mm});
            skLineSegment(sketch, "E1239", {"start": v(-78.38, -49.94) * mm, "end": v(-78.63, -50.3) * mm});
            skLineSegment(sketch, "E1240", {"start": v(-78.63, -50.3) * mm, "end": v(-78.89, -50.7) * mm});
            skLineSegment(sketch, "E1241", {"start": v(-78.89, -50.7) * mm, "end": v(-79.14, -51.1) * mm});
            skLineSegment(sketch, "E1242", {"start": v(-79.14, -51.1) * mm, "end": v(-79.4, -51.5) * mm});
            skLineSegment(sketch, "E1243", {"start": v(-79.4, -51.5) * mm, "end": v(-79.66, -51.93) * mm});
            skLineSegment(sketch, "E1244", {"start": v(-79.66, -51.93) * mm, "end": v(-79.91, -52.37) * mm});
            skLineSegment(sketch, "E1245", {"start": v(-79.91, -52.37) * mm, "end": v(-80.17, -52.82) * mm});
            skLineSegment(sketch, "E1246", {"start": v(-80.17, -52.82) * mm, "end": v(-80.44, -53.3) * mm});
            skLineSegment(sketch, "E1247", {"start": v(-80.44, -53.3) * mm, "end": v(-80.7, -53.77) * mm});
            skLineSegment(sketch, "E1248", {"start": v(-80.7, -53.77) * mm, "end": v(-80.96, -54.27) * mm});
            skLineSegment(sketch, "E1249", {"start": v(-80.96, -54.27) * mm, "end": v(-81.22, -54.78) * mm});
            skLineSegment(sketch, "E1250", {"start": v(-81.22, -54.78) * mm, "end": v(-81.48, -55.3) * mm});
            skLineSegment(sketch, "E1251", {"start": v(-81.48, -55.3) * mm, "end": v(-81.74, -55.84) * mm});
            skLineSegment(sketch, "E1252", {"start": v(-81.74, -55.84) * mm, "end": v(-82, -56.4) * mm});
            skLineSegment(sketch, "E1253", {"start": v(-82, -56.4) * mm, "end": v(-82.25, -56.96) * mm});
            skLineSegment(sketch, "E1254", {"start": v(-82.25, -56.96) * mm, "end": v(-82.5, -57.54) * mm});
            skLineSegment(sketch, "E1255", {"start": v(-82.5, -57.54) * mm, "end": v(-82.76, -58.14) * mm});
            skLineSegment(sketch, "E1256", {"start": v(-82.76, -58.14) * mm, "end": v(-83, -58.75) * mm});
            skLineSegment(sketch, "E1257", {"start": v(-83, -58.75) * mm, "end": v(-83.25, -59.37) * mm});
            skLineSegment(sketch, "E1258", {"start": v(-83.25, -59.37) * mm, "end": v(-83.18, -59.79) * mm});
            skLineSegment(sketch, "E1259", {"start": v(-83.18, -59.79) * mm, "end": v(-81.85, -61.6) * mm});
            skLineSegment(sketch, "E1260", {"start": v(-81.85, -61.6) * mm, "end": v(-81.47, -61.8) * mm});
            skLineSegment(sketch, "E1261", {"start": v(-81.47, -61.8) * mm, "end": v(-80.8, -61.75) * mm});
            skLineSegment(sketch, "E1262", {"start": v(-80.8, -61.75) * mm, "end": v(-80.15, -61.7) * mm});
            skLineSegment(sketch, "E1263", {"start": v(-80.15, -61.7) * mm, "end": v(-79.5, -61.64) * mm});
            skLineSegment(sketch, "E1264", {"start": v(-79.5, -61.64) * mm, "end": v(-78.87, -61.57) * mm});
            skLineSegment(sketch, "E1265", {"start": v(-78.87, -61.57) * mm, "end": v(-78.26, -61.5) * mm});
            skLineSegment(sketch, "E1266", {"start": v(-78.26, -61.5) * mm, "end": v(-77.65, -61.42) * mm});
            skLineSegment(sketch, "E1267", {"start": v(-77.65, -61.42) * mm, "end": v(-77.06, -61.33) * mm});
            skLineSegment(sketch, "E1268", {"start": v(-77.06, -61.33) * mm, "end": v(-76.48, -61.24) * mm});
            skLineSegment(sketch, "E1269", {"start": v(-76.48, -61.24) * mm, "end": v(-75.92, -61.15) * mm});
            skLineSegment(sketch, "E1270", {"start": v(-75.92, -61.15) * mm, "end": v(-75.37, -61.05) * mm});
            skLineSegment(sketch, "E1271", {"start": v(-75.37, -61.05) * mm, "end": v(-74.83, -60.94) * mm});
            skLineSegment(sketch, "E1272", {"start": v(-74.83, -60.94) * mm, "end": v(-74.3, -60.83) * mm});
            skLineSegment(sketch, "E1273", {"start": v(-74.3, -60.83) * mm, "end": v(-73.8, -60.72) * mm});
            skLineSegment(sketch, "E1274", {"start": v(-73.8, -60.72) * mm, "end": v(-73.3, -60.6) * mm});
            skLineSegment(sketch, "E1275", {"start": v(-73.3, -60.6) * mm, "end": v(-72.8, -60.49) * mm});
            skLineSegment(sketch, "E1276", {"start": v(-72.8, -60.49) * mm, "end": v(-72.34, -60.37) * mm});
            skLineSegment(sketch, "E1277", {"start": v(-72.34, -60.37) * mm, "end": v(-71.88, -60.25) * mm});
            skLineSegment(sketch, "E1278", {"start": v(-71.88, -60.25) * mm, "end": v(-71.44, -60.12) * mm});
            skLineSegment(sketch, "E1279", {"start": v(-71.44, -60.12) * mm, "end": v(-71, -60) * mm});
            skLineSegment(sketch, "E1280", {"start": v(-71, -60) * mm, "end": v(-70.6, -59.86) * mm});
            skLineSegment(sketch, "E1281", {"start": v(-70.6, -59.86) * mm, "end": v(-70.19, -59.73) * mm});
            skLineSegment(sketch, "E1282", {"start": v(-70.19, -59.73) * mm, "end": v(-69.8, -59.6) * mm});
            skLineSegment(sketch, "E1283", {"start": v(-69.8, -59.6) * mm, "end": v(-69.42, -59.47) * mm});
            skLineSegment(sketch, "E1284", {"start": v(-69.42, -59.47) * mm, "end": v(-69.06, -59.34) * mm});
            skLineSegment(sketch, "E1285", {"start": v(-69.06, -59.34) * mm, "end": v(-68.7, -59.2) * mm});
            skLineSegment(sketch, "E1286", {"start": v(-68.7, -59.2) * mm, "end": v(-68.37, -59.08) * mm});
            skLineSegment(sketch, "E1287", {"start": v(-68.37, -59.08) * mm, "end": v(-68.04, -58.95) * mm});
            skLineSegment(sketch, "E1288", {"start": v(-68.04, -58.95) * mm, "end": v(-67.73, -58.82) * mm});
            skLineSegment(sketch, "E1289", {"start": v(-67.73, -58.82) * mm, "end": v(-67.43, -58.69) * mm});
            skLineSegment(sketch, "E1290", {"start": v(-67.43, -58.69) * mm, "end": v(-67.15, -58.56) * mm});
            skLineSegment(sketch, "E1291", {"start": v(-67.15, -58.56) * mm, "end": v(-66.88, -58.44) * mm});
            skLineSegment(sketch, "E1292", {"start": v(-66.88, -58.44) * mm, "end": v(-66.61, -58.31) * mm});
            skLineSegment(sketch, "E1293", {"start": v(-66.61, -58.31) * mm, "end": v(-66.37, -58.19) * mm});
            skLineSegment(sketch, "E1294", {"start": v(-66.37, -58.19) * mm, "end": v(-66, -58.55) * mm});
            skLineSegment(sketch, "E1295", {"start": v(-66, -58.55) * mm, "end": v(-63.95, -60.8) * mm});
            skLineSegment(sketch, "E1296", {"start": v(-63.95, -60.8) * mm, "end": v(-63.62, -61.2) * mm});
            skLineSegment(sketch, "E1297", {"start": v(-63.62, -61.2) * mm, "end": v(-63.76, -61.43) * mm});
            skLineSegment(sketch, "E1298", {"start": v(-63.76, -61.43) * mm, "end": v(-63.9, -61.68) * mm});
            skLineSegment(sketch, "E1299", {"start": v(-63.9, -61.68) * mm, "end": v(-64.06, -61.94) * mm});
            skLineSegment(sketch, "E1300", {"start": v(-64.06, -61.94) * mm, "end": v(-64.21, -62.21) * mm});
            skLineSegment(sketch, "E1301", {"start": v(-64.21, -62.21) * mm, "end": v(-64.36, -62.5) * mm});
            skLineSegment(sketch, "E1302", {"start": v(-64.36, -62.5) * mm, "end": v(-64.52, -62.8) * mm});
            skLineSegment(sketch, "E1303", {"start": v(-64.52, -62.8) * mm, "end": v(-64.68, -63.1) * mm});
            skLineSegment(sketch, "E1304", {"start": v(-64.68, -63.1) * mm, "end": v(-64.84, -63.43) * mm});
            skLineSegment(sketch, "E1305", {"start": v(-64.84, -63.43) * mm, "end": v(-65, -63.77) * mm});
            skLineSegment(sketch, "E1306", {"start": v(-65, -63.77) * mm, "end": v(-65.17, -64.12) * mm});
            skLineSegment(sketch, "E1307", {"start": v(-65.17, -64.12) * mm, "end": v(-65.33, -64.48) * mm});
            skLineSegment(sketch, "E1308", {"start": v(-65.33, -64.48) * mm, "end": v(-65.5, -64.86) * mm});
            skLineSegment(sketch, "E1309", {"start": v(-65.5, -64.86) * mm, "end": v(-65.66, -65.25) * mm});
            skLineSegment(sketch, "E1310", {"start": v(-65.66, -65.25) * mm, "end": v(-65.83, -65.65) * mm});
            skLineSegment(sketch, "E1311", {"start": v(-65.83, -65.65) * mm, "end": v(-66, -66.07) * mm});
            skLineSegment(sketch, "E1312", {"start": v(-66, -66.07) * mm, "end": v(-66.16, -66.5) * mm});
            skLineSegment(sketch, "E1313", {"start": v(-66.16, -66.5) * mm, "end": v(-66.32, -66.95) * mm});
            skLineSegment(sketch, "E1314", {"start": v(-66.32, -66.95) * mm, "end": v(-66.48, -67.4) * mm});
            skLineSegment(sketch, "E1315", {"start": v(-66.48, -67.4) * mm, "end": v(-66.64, -67.88) * mm});
            skLineSegment(sketch, "E1316", {"start": v(-66.64, -67.88) * mm, "end": v(-66.8, -68.36) * mm});
            skLineSegment(sketch, "E1317", {"start": v(-66.8, -68.36) * mm, "end": v(-66.96, -68.86) * mm});
            skLineSegment(sketch, "E1318", {"start": v(-66.96, -68.86) * mm, "end": v(-67.11, -69.38) * mm});
            skLineSegment(sketch, "E1319", {"start": v(-67.11, -69.38) * mm, "end": v(-67.26, -69.9) * mm});
            skLineSegment(sketch, "E1320", {"start": v(-67.26, -69.9) * mm, "end": v(-67.41, -70.44) * mm});
            skLineSegment(sketch, "E1321", {"start": v(-67.41, -70.44) * mm, "end": v(-67.56, -71) * mm});
            skLineSegment(sketch, "E1322", {"start": v(-67.56, -71) * mm, "end": v(-67.7, -71.56) * mm});
            skLineSegment(sketch, "E1323", {"start": v(-67.7, -71.56) * mm, "end": v(-67.83, -72.14) * mm});
            skLineSegment(sketch, "E1324", {"start": v(-67.83, -72.14) * mm, "end": v(-67.97, -72.74) * mm});
            skLineSegment(sketch, "E1325", {"start": v(-67.97, -72.74) * mm, "end": v(-68.1, -73.35) * mm});
            skLineSegment(sketch, "E1326", {"start": v(-68.1, -73.35) * mm, "end": v(-68.22, -73.97) * mm});
            skLineSegment(sketch, "E1327", {"start": v(-68.22, -73.97) * mm, "end": v(-68.34, -74.6) * mm});
            skLineSegment(sketch, "E1328", {"start": v(-68.34, -74.6) * mm, "end": v(-68.45, -75.26) * mm});
            skLineSegment(sketch, "E1329", {"start": v(-68.45, -75.26) * mm, "end": v(-68.56, -75.92) * mm});
            skLineSegment(sketch, "E1330", {"start": v(-68.56, -75.92) * mm, "end": v(-68.4, -76.3) * mm});
            skLineSegment(sketch, "E1331", {"start": v(-68.4, -76.3) * mm, "end": v(-66.7, -77.8) * mm});
            skLineSegment(sketch, "E1332", {"start": v(-66.7, -77.8) * mm, "end": v(-66.3, -77.9) * mm});
            skLineSegment(sketch, "E1333", {"start": v(-66.3, -77.9) * mm, "end": v(-65.65, -77.72) * mm});
            skLineSegment(sketch, "E1334", {"start": v(-65.65, -77.72) * mm, "end": v(-65.02, -77.52) * mm});
            skLineSegment(sketch, "E1335", {"start": v(-65.02, -77.52) * mm, "end": v(-64.4, -77.33) * mm});
            skLineSegment(sketch, "E1336", {"start": v(-64.4, -77.33) * mm, "end": v(-63.8, -77.12) * mm});
            skLineSegment(sketch, "E1337", {"start": v(-63.8, -77.12) * mm, "end": v(-63.22, -76.92) * mm});
            skLineSegment(sketch, "E1338", {"start": v(-63.22, -76.92) * mm, "end": v(-62.64, -76.71) * mm});
            skLineSegment(sketch, "E1339", {"start": v(-62.64, -76.71) * mm, "end": v(-62.09, -76.5) * mm});
            skLineSegment(sketch, "E1340", {"start": v(-62.09, -76.5) * mm, "end": v(-61.54, -76.29) * mm});
            skLineSegment(sketch, "E1341", {"start": v(-61.54, -76.29) * mm, "end": v(-61, -76.07) * mm});
            skLineSegment(sketch, "E1342", {"start": v(-61, -76.07) * mm, "end": v(-60.5, -75.86) * mm});
            skLineSegment(sketch, "E1343", {"start": v(-60.5, -75.86) * mm, "end": v(-59.99, -75.64) * mm});
            skLineSegment(sketch, "E1344", {"start": v(-59.99, -75.64) * mm, "end": v(-59.5, -75.42) * mm});
            skLineSegment(sketch, "E1345", {"start": v(-59.5, -75.42) * mm, "end": v(-59.02, -75.2) * mm});
            skLineSegment(sketch, "E1346", {"start": v(-59.02, -75.2) * mm, "end": v(-58.56, -74.98) * mm});
            skLineSegment(sketch, "E1347", {"start": v(-58.56, -74.98) * mm, "end": v(-58.12, -74.76) * mm});
            skLineSegment(sketch, "E1348", {"start": v(-58.12, -74.76) * mm, "end": v(-57.68, -74.55) * mm});
            skLineSegment(sketch, "E1349", {"start": v(-57.68, -74.55) * mm, "end": v(-57.26, -74.33) * mm});
            skLineSegment(sketch, "E1350", {"start": v(-57.26, -74.33) * mm, "end": v(-56.86, -74.1) * mm});
            skLineSegment(sketch, "E1351", {"start": v(-56.86, -74.1) * mm, "end": v(-56.46, -73.9) * mm});
            skLineSegment(sketch, "E1352", {"start": v(-56.46, -73.9) * mm, "end": v(-56.08, -73.68) * mm});
            skLineSegment(sketch, "E1353", {"start": v(-56.08, -73.68) * mm, "end": v(-55.72, -73.46) * mm});
            skLineSegment(sketch, "E1354", {"start": v(-55.72, -73.46) * mm, "end": v(-55.36, -73.25) * mm});
            skLineSegment(sketch, "E1355", {"start": v(-55.36, -73.25) * mm, "end": v(-55.02, -73.04) * mm});
            skLineSegment(sketch, "E1356", {"start": v(-55.02, -73.04) * mm, "end": v(-54.7, -72.84) * mm});
            skLineSegment(sketch, "E1357", {"start": v(-54.7, -72.84) * mm, "end": v(-54.38, -72.63) * mm});
            skLineSegment(sketch, "E1358", {"start": v(-54.38, -72.63) * mm, "end": v(-54.08, -72.43) * mm});
            skLineSegment(sketch, "E1359", {"start": v(-54.08, -72.43) * mm, "end": v(-53.8, -72.23) * mm});
            skLineSegment(sketch, "E1360", {"start": v(-53.8, -72.23) * mm, "end": v(-53.52, -72.04) * mm});
            skLineSegment(sketch, "E1361", {"start": v(-53.52, -72.04) * mm, "end": v(-53.25, -71.85) * mm});
            skLineSegment(sketch, "E1362", {"start": v(-53.25, -71.85) * mm, "end": v(-53, -71.66) * mm});
            skLineSegment(sketch, "E1363", {"start": v(-53, -71.66) * mm, "end": v(-52.76, -71.48) * mm});
            skLineSegment(sketch, "E1364", {"start": v(-52.76, -71.48) * mm, "end": v(-52.54, -71.3) * mm});
            skLineSegment(sketch, "E1365", {"start": v(-52.54, -71.3) * mm, "end": v(-52.32, -71.13) * mm});
            skLineSegment(sketch, "E1366", {"start": v(-52.32, -71.13) * mm, "end": v(-51.9, -71.4) * mm});
            skLineSegment(sketch, "E1367", {"start": v(-51.9, -71.4) * mm, "end": v(-49.4, -73.16) * mm});
            skLineSegment(sketch, "E1368", {"start": v(-49.4, -73.16) * mm, "end": v(-48.99, -73.48) * mm});
            skLineSegment(sketch, "E1369", {"start": v(-48.99, -73.48) * mm, "end": v(-49.08, -73.74) * mm});
            skLineSegment(sketch, "E1370", {"start": v(-49.08, -73.74) * mm, "end": v(-49.17, -74.01) * mm});
            skLineSegment(sketch, "E1371", {"start": v(-49.17, -74.01) * mm, "end": v(-49.26, -74.3) * mm});
            skLineSegment(sketch, "E1372", {"start": v(-49.26, -74.3) * mm, "end": v(-49.35, -74.6) * mm});
            skLineSegment(sketch, "E1373", {"start": v(-49.35, -74.6) * mm, "end": v(-49.44, -74.9) * mm});
            skLineSegment(sketch, "E1374", {"start": v(-49.44, -74.9) * mm, "end": v(-49.53, -75.23) * mm});
            skLineSegment(sketch, "E1375", {"start": v(-49.53, -75.23) * mm, "end": v(-49.62, -75.57) * mm});
            skLineSegment(sketch, "E1376", {"start": v(-49.62, -75.57) * mm, "end": v(-49.7, -75.92) * mm});
            skLineSegment(sketch, "E1377", {"start": v(-49.7, -75.92) * mm, "end": v(-49.79, -76.29) * mm});
            skLineSegment(sketch, "E1378", {"start": v(-49.79, -76.29) * mm, "end": v(-49.87, -76.67) * mm});
            skLineSegment(sketch, "E1379", {"start": v(-49.87, -76.67) * mm, "end": v(-49.95, -77.06) * mm});
            skLineSegment(sketch, "E1380", {"start": v(-49.95, -77.06) * mm, "end": v(-50.04, -77.46) * mm});
            skLineSegment(sketch, "E1381", {"start": v(-50.04, -77.46) * mm, "end": v(-50.11, -77.88) * mm});
            skLineSegment(sketch, "E1382", {"start": v(-50.11, -77.88) * mm, "end": v(-50.19, -78.3) * mm});
            skLineSegment(sketch, "E1383", {"start": v(-50.19, -78.3) * mm, "end": v(-50.26, -78.75) * mm});
            skLineSegment(sketch, "E1384", {"start": v(-50.26, -78.75) * mm, "end": v(-50.33, -79.2) * mm});
            skLineSegment(sketch, "E1385", {"start": v(-50.33, -79.2) * mm, "end": v(-50.39, -79.68) * mm});
            skLineSegment(sketch, "E1386", {"start": v(-50.39, -79.68) * mm, "end": v(-50.45, -80.16) * mm});
            skLineSegment(sketch, "E1387", {"start": v(-50.45, -80.16) * mm, "end": v(-50.5, -80.65) * mm});
            skLineSegment(sketch, "E1388", {"start": v(-50.5, -80.65) * mm, "end": v(-50.56, -81.16) * mm});
            skLineSegment(sketch, "E1389", {"start": v(-50.56, -81.16) * mm, "end": v(-50.6, -81.68) * mm});
            skLineSegment(sketch, "E1390", {"start": v(-50.6, -81.68) * mm, "end": v(-50.64, -82.22) * mm});
            skLineSegment(sketch, "E1391", {"start": v(-50.64, -82.22) * mm, "end": v(-50.68, -82.76) * mm});
            skLineSegment(sketch, "E1392", {"start": v(-50.68, -82.76) * mm, "end": v(-50.7, -83.32) * mm});
            skLineSegment(sketch, "E1393", {"start": v(-50.7, -83.32) * mm, "end": v(-50.73, -83.9) * mm});
            skLineSegment(sketch, "E1394", {"start": v(-50.73, -83.9) * mm, "end": v(-50.74, -84.48) * mm});
            skLineSegment(sketch, "E1395", {"start": v(-50.74, -84.48) * mm, "end": v(-50.75, -85.08) * mm});
            skLineSegment(sketch, "E1396", {"start": v(-50.75, -85.08) * mm, "end": v(-50.75, -85.69) * mm});
            skLineSegment(sketch, "E1397", {"start": v(-50.75, -85.69) * mm, "end": v(-50.75, -86.3) * mm});
            skLineSegment(sketch, "E1398", {"start": v(-50.75, -86.3) * mm, "end": v(-50.73, -86.94) * mm});
            skLineSegment(sketch, "E1399", {"start": v(-50.73, -86.94) * mm, "end": v(-50.71, -87.6) * mm});
            skLineSegment(sketch, "E1400", {"start": v(-50.71, -87.6) * mm, "end": v(-50.68, -88.25) * mm});
            skLineSegment(sketch, "E1401", {"start": v(-50.68, -88.25) * mm, "end": v(-50.64, -88.92) * mm});
            skLineSegment(sketch, "E1402", {"start": v(-50.64, -88.92) * mm, "end": v(-50.4, -89.26) * mm});
            skLineSegment(sketch, "E1403", {"start": v(-50.4, -89.26) * mm, "end": v(-48.43, -90.36) * mm});
            skLineSegment(sketch, "E1404", {"start": v(-48.43, -90.36) * mm, "end": v(-48.01, -90.38) * mm});
            skLineSegment(sketch, "E1405", {"start": v(-48.01, -90.38) * mm, "end": v(-47.42, -90.05) * mm});
            skLineSegment(sketch, "E1406", {"start": v(-47.42, -90.05) * mm, "end": v(-46.85, -89.73) * mm});
            skLineSegment(sketch, "E1407", {"start": v(-46.85, -89.73) * mm, "end": v(-46.3, -89.4) * mm});
            skLineSegment(sketch, "E1408", {"start": v(-46.3, -89.4) * mm, "end": v(-45.75, -89.07) * mm});
            skLineSegment(sketch, "E1409", {"start": v(-45.75, -89.07) * mm, "end": v(-45.22, -88.75) * mm});
            skLineSegment(sketch, "E1410", {"start": v(-45.22, -88.75) * mm, "end": v(-44.7, -88.42) * mm});
            skLineSegment(sketch, "E1411", {"start": v(-44.7, -88.42) * mm, "end": v(-44.2, -88.1) * mm});
            skLineSegment(sketch, "E1412", {"start": v(-44.2, -88.1) * mm, "end": v(-43.71, -87.77) * mm});
            skLineSegment(sketch, "E1413", {"start": v(-43.71, -87.77) * mm, "end": v(-43.24, -87.45) * mm});
            skLineSegment(sketch, "E1414", {"start": v(-43.24, -87.45) * mm, "end": v(-42.78, -87.13) * mm});
            skLineSegment(sketch, "E1415", {"start": v(-42.78, -87.13) * mm, "end": v(-42.34, -86.8) * mm});
            skLineSegment(sketch, "E1416", {"start": v(-42.34, -86.8) * mm, "end": v(-41.9, -86.49) * mm});
            skLineSegment(sketch, "E1417", {"start": v(-41.9, -86.49) * mm, "end": v(-41.5, -86.17) * mm});
            skLineSegment(sketch, "E1418", {"start": v(-41.5, -86.17) * mm, "end": v(-41.09, -85.86) * mm});
            skLineSegment(sketch, "E1419", {"start": v(-41.09, -85.86) * mm, "end": v(-40.7, -85.55) * mm});
            skLineSegment(sketch, "E1420", {"start": v(-40.7, -85.55) * mm, "end": v(-40.32, -85.24) * mm});
            skLineSegment(sketch, "E1421", {"start": v(-40.32, -85.24) * mm, "end": v(-39.96, -84.94) * mm});
            skLineSegment(sketch, "E1422", {"start": v(-39.96, -84.94) * mm, "end": v(-39.6, -84.64) * mm});
            skLineSegment(sketch, "E1423", {"start": v(-39.6, -84.64) * mm, "end": v(-39.27, -84.34) * mm});
            skLineSegment(sketch, "E1424", {"start": v(-39.27, -84.34) * mm, "end": v(-38.95, -84.05) * mm});
            skLineSegment(sketch, "E1425", {"start": v(-38.95, -84.05) * mm, "end": v(-38.64, -83.76) * mm});
            skLineSegment(sketch, "E1426", {"start": v(-38.64, -83.76) * mm, "end": v(-38.34, -83.48) * mm});
            skLineSegment(sketch, "E1427", {"start": v(-38.34, -83.48) * mm, "end": v(-38.05, -83.2) * mm});
            skLineSegment(sketch, "E1428", {"start": v(-38.05, -83.2) * mm, "end": v(-37.77, -82.93) * mm});
            skLineSegment(sketch, "E1429", {"start": v(-37.77, -82.93) * mm, "end": v(-37.51, -82.66) * mm});
            skLineSegment(sketch, "E1430", {"start": v(-37.51, -82.66) * mm, "end": v(-37.26, -82.4) * mm});
            skLineSegment(sketch, "E1431", {"start": v(-37.26, -82.4) * mm, "end": v(-37.02, -82.14) * mm});
            skLineSegment(sketch, "E1432", {"start": v(-37.02, -82.14) * mm, "end": v(-36.8, -81.9) * mm});
            skLineSegment(sketch, "E1433", {"start": v(-36.8, -81.9) * mm, "end": v(-36.58, -81.65) * mm});
            skLineSegment(sketch, "E1434", {"start": v(-36.58, -81.65) * mm, "end": v(-36.37, -81.42) * mm});
            skLineSegment(sketch, "E1435", {"start": v(-36.37, -81.42) * mm, "end": v(-36.18, -81.19) * mm});
            skLineSegment(sketch, "E1436", {"start": v(-36.18, -81.19) * mm, "end": v(-36, -80.97) * mm});
            skLineSegment(sketch, "E1437", {"start": v(-36, -80.97) * mm, "end": v(-35.82, -80.75) * mm});
            skLineSegment(sketch, "E1438", {"start": v(-35.82, -80.75) * mm, "end": v(-35.34, -80.93) * mm});
            skLineSegment(sketch, "E1439", {"start": v(-35.34, -80.93) * mm, "end": v(-32.52, -82.1) * mm});
            skLineSegment(sketch, "E1440", {"start": v(-32.52, -82.1) * mm, "end": v(-32.06, -82.33) * mm});
            skLineSegment(sketch, "E1441", {"start": v(-32.06, -82.33) * mm, "end": v(-32.1, -82.6) * mm});
            skLineSegment(sketch, "E1442", {"start": v(-32.1, -82.6) * mm, "end": v(-32.12, -82.89) * mm});
            skLineSegment(sketch, "E1443", {"start": v(-32.12, -82.89) * mm, "end": v(-32.15, -83.19) * mm});
            skLineSegment(sketch, "E1444", {"start": v(-32.15, -83.19) * mm, "end": v(-32.17, -83.5) * mm});
            skLineSegment(sketch, "E1445", {"start": v(-32.17, -83.5) * mm, "end": v(-32.2, -83.82) * mm});
            skLineSegment(sketch, "E1446", {"start": v(-32.2, -83.82) * mm, "end": v(-32.2, -84.16) * mm});
            skLineSegment(sketch, "E1447", {"start": v(-32.2, -84.16) * mm, "end": v(-32.22, -84.5) * mm});
            skLineSegment(sketch, "E1448", {"start": v(-32.22, -84.5) * mm, "end": v(-32.23, -84.87) * mm});
            skLineSegment(sketch, "E1449", {"start": v(-32.23, -84.87) * mm, "end": v(-32.24, -85.24) * mm});
            skLineSegment(sketch, "E1450", {"start": v(-32.24, -85.24) * mm, "end": v(-32.24, -85.63) * mm});
            skLineSegment(sketch, "E1451", {"start": v(-32.24, -85.63) * mm, "end": v(-32.23, -86.03) * mm});
            skLineSegment(sketch, "E1452", {"start": v(-32.23, -86.03) * mm, "end": v(-32.23, -86.44) * mm});
            skLineSegment(sketch, "E1453", {"start": v(-32.23, -86.44) * mm, "end": v(-32.21, -86.87) * mm});
            skLineSegment(sketch, "E1454", {"start": v(-32.21, -86.87) * mm, "end": v(-32.2, -87.3) * mm});
            skLineSegment(sketch, "E1455", {"start": v(-32.2, -87.3) * mm, "end": v(-32.17, -87.75) * mm});
            skLineSegment(sketch, "E1456", {"start": v(-32.17, -87.75) * mm, "end": v(-32.14, -88.21) * mm});
            skLineSegment(sketch, "E1457", {"start": v(-32.14, -88.21) * mm, "end": v(-32.1, -88.68) * mm});
            skLineSegment(sketch, "E1458", {"start": v(-32.1, -88.68) * mm, "end": v(-32.05, -89.17) * mm});
            skLineSegment(sketch, "E1459", {"start": v(-32.05, -89.17) * mm, "end": v(-32, -89.66) * mm});
            skLineSegment(sketch, "E1460", {"start": v(-32, -89.66) * mm, "end": v(-31.94, -90.17) * mm});
            skLineSegment(sketch, "E1461", {"start": v(-31.94, -90.17) * mm, "end": v(-31.87, -90.69) * mm});
            skLineSegment(sketch, "E1462", {"start": v(-31.87, -90.69) * mm, "end": v(-31.8, -91.22) * mm});
            skLineSegment(sketch, "E1463", {"start": v(-31.8, -91.22) * mm, "end": v(-31.71, -91.76) * mm});
            skLineSegment(sketch, "E1464", {"start": v(-31.71, -91.76) * mm, "end": v(-31.62, -92.31) * mm});
            skLineSegment(sketch, "E1465", {"start": v(-31.62, -92.31) * mm, "end": v(-31.52, -92.88) * mm});
            skLineSegment(sketch, "E1466", {"start": v(-31.52, -92.88) * mm, "end": v(-31.4, -93.45) * mm});
            skLineSegment(sketch, "E1467", {"start": v(-31.4, -93.45) * mm, "end": v(-31.29, -94.04) * mm});
            skLineSegment(sketch, "E1468", {"start": v(-31.29, -94.04) * mm, "end": v(-31.16, -94.63) * mm});
            skLineSegment(sketch, "E1469", {"start": v(-31.16, -94.63) * mm, "end": v(-31.02, -95.24) * mm});
            skLineSegment(sketch, "E1470", {"start": v(-31.02, -95.24) * mm, "end": v(-30.87, -95.86) * mm});
            skLineSegment(sketch, "E1471", {"start": v(-30.87, -95.86) * mm, "end": v(-30.71, -96.48) * mm});
            skLineSegment(sketch, "E1472", {"start": v(-30.71, -96.48) * mm, "end": v(-30.54, -97.12) * mm});
            skLineSegment(sketch, "E1473", {"start": v(-30.54, -97.12) * mm, "end": v(-30.36, -97.77) * mm});
            skLineSegment(sketch, "E1474", {"start": v(-30.36, -97.77) * mm, "end": v(-30.05, -98.05) * mm});
            skLineSegment(sketch, "E1475", {"start": v(-30.05, -98.05) * mm, "end": v(-27.89, -98.7) * mm});
            skLineSegment(sketch, "E1476", {"start": v(-27.89, -98.7) * mm, "end": v(-27.47, -98.62) * mm});
            skLineSegment(sketch, "E1477", {"start": v(-27.47, -98.62) * mm, "end": v(-26.97, -98.18) * mm});
            skLineSegment(sketch, "E1478", {"start": v(-26.97, -98.18) * mm, "end": v(-26.48, -97.74) * mm});
            skLineSegment(sketch, "E1479", {"start": v(-26.48, -97.74) * mm, "end": v(-26, -97.3) * mm});
            skLineSegment(sketch, "E1480", {"start": v(-26, -97.3) * mm, "end": v(-25.54, -96.86) * mm});
            skLineSegment(sketch, "E1481", {"start": v(-25.54, -96.86) * mm, "end": v(-25.1, -96.43) * mm});
            skLineSegment(sketch, "E1482", {"start": v(-25.1, -96.43) * mm, "end": v(-24.66, -96) * mm});
            skLineSegment(sketch, "E1483", {"start": v(-24.66, -96) * mm, "end": v(-24.24, -95.57) * mm});
            skLineSegment(sketch, "E1484", {"start": v(-24.24, -95.57) * mm, "end": v(-23.84, -95.15) * mm});
            skLineSegment(sketch, "E1485", {"start": v(-23.84, -95.15) * mm, "end": v(-23.45, -94.74) * mm});
            skLineSegment(sketch, "E1486", {"start": v(-23.45, -94.74) * mm, "end": v(-23.07, -94.32) * mm});
            skLineSegment(sketch, "E1487", {"start": v(-23.07, -94.32) * mm, "end": v(-22.7, -93.91) * mm});
            skLineSegment(sketch, "E1488", {"start": v(-22.7, -93.91) * mm, "end": v(-22.35, -93.51) * mm});
            skLineSegment(sketch, "E1489", {"start": v(-22.35, -93.51) * mm, "end": v(-22, -93.11) * mm});
            skLineSegment(sketch, "E1490", {"start": v(-22, -93.11) * mm, "end": v(-21.68, -92.72) * mm});
            skLineSegment(sketch, "E1491", {"start": v(-21.68, -92.72) * mm, "end": v(-21.37, -92.33) * mm});
            skLineSegment(sketch, "E1492", {"start": v(-21.37, -92.33) * mm, "end": v(-21.07, -91.95) * mm});
            skLineSegment(sketch, "E1493", {"start": v(-21.07, -91.95) * mm, "end": v(-20.78, -91.58) * mm});
            skLineSegment(sketch, "E1494", {"start": v(-20.78, -91.58) * mm, "end": v(-20.5, -91.2) * mm});
            skLineSegment(sketch, "E1495", {"start": v(-20.5, -91.2) * mm, "end": v(-20.24, -90.85) * mm});
            skLineSegment(sketch, "E1496", {"start": v(-20.24, -90.85) * mm, "end": v(-19.98, -90.5) * mm});
            skLineSegment(sketch, "E1497", {"start": v(-19.98, -90.5) * mm, "end": v(-19.74, -90.14) * mm});
            skLineSegment(sketch, "E1498", {"start": v(-19.74, -90.14) * mm, "end": v(-19.5, -89.8) * mm});
            skLineSegment(sketch, "E1499", {"start": v(-19.5, -89.8) * mm, "end": v(-19.29, -89.47) * mm});
            skLineSegment(sketch, "E1500", {"start": v(-19.29, -89.47) * mm, "end": v(-19.08, -89.15) * mm});
            skLineSegment(sketch, "E1501", {"start": v(-19.08, -89.15) * mm, "end": v(-18.88, -88.83) * mm});
            skLineSegment(sketch, "E1502", {"start": v(-18.88, -88.83) * mm, "end": v(-18.69, -88.52) * mm});
            skLineSegment(sketch, "E1503", {"start": v(-18.69, -88.52) * mm, "end": v(-18.5, -88.22) * mm});
            skLineSegment(sketch, "E1504", {"start": v(-18.5, -88.22) * mm, "end": v(-18.34, -87.93) * mm});
            skLineSegment(sketch, "E1505", {"start": v(-18.34, -87.93) * mm, "end": v(-18.18, -87.64) * mm});
            skLineSegment(sketch, "E1506", {"start": v(-18.18, -87.64) * mm, "end": v(-18.03, -87.37) * mm});
            skLineSegment(sketch, "E1507", {"start": v(-18.03, -87.37) * mm, "end": v(-17.89, -87.1) * mm});
            skLineSegment(sketch, "E1508", {"start": v(-17.89, -87.1) * mm, "end": v(-17.76, -86.85) * mm});
            skLineSegment(sketch, "E1509", {"start": v(-17.76, -86.85) * mm, "end": v(-17.63, -86.6) * mm});
            skLineSegment(sketch, "E1510", {"start": v(-17.63, -86.6) * mm, "end": v(-17.13, -86.67) * mm});
            skLineSegment(sketch, "E1511", {"start": v(-17.13, -86.67) * mm, "end": v(-14.12, -87.22) * mm});
            skLineSegment(sketch, "E1512", {"start": v(-14.12, -87.22) * mm, "end": v(-13.63, -87.33) * mm});
            skLineSegment(sketch, "E1513", {"start": v(-13.63, -87.33) * mm, "end": v(-13.6, -87.6) * mm});
            skLineSegment(sketch, "E1514", {"start": v(-13.6, -87.6) * mm, "end": v(-13.56, -87.9) * mm});
            skLineSegment(sketch, "E1515", {"start": v(-13.56, -87.9) * mm, "end": v(-13.53, -88.19) * mm});
            skLineSegment(sketch, "E1516", {"start": v(-13.53, -88.19) * mm, "end": v(-13.48, -88.5) * mm});
            skLineSegment(sketch, "E1517", {"start": v(-13.48, -88.5) * mm, "end": v(-13.43, -88.82) * mm});
            skLineSegment(sketch, "E1518", {"start": v(-13.43, -88.82) * mm, "end": v(-13.38, -89.15) * mm});
            skLineSegment(sketch, "E1519", {"start": v(-13.38, -89.15) * mm, "end": v(-13.31, -89.5) * mm});
            skLineSegment(sketch, "E1520", {"start": v(-13.31, -89.5) * mm, "end": v(-13.25, -89.85) * mm});
            skLineSegment(sketch, "E1521", {"start": v(-13.25, -89.85) * mm, "end": v(-13.17, -90.22) * mm});
            skLineSegment(sketch, "E1522", {"start": v(-13.17, -90.22) * mm, "end": v(-13.09, -90.6) * mm});
            skLineSegment(sketch, "E1523", {"start": v(-13.09, -90.6) * mm, "end": v(-13, -90.99) * mm});
            skLineSegment(sketch, "E1524", {"start": v(-13, -90.99) * mm, "end": v(-12.9, -91.39) * mm});
            skLineSegment(sketch, "E1525", {"start": v(-12.9, -91.39) * mm, "end": v(-12.8, -91.8) * mm});
            skLineSegment(sketch, "E1526", {"start": v(-12.8, -91.8) * mm, "end": v(-12.69, -92.22) * mm});
            skLineSegment(sketch, "E1527", {"start": v(-12.69, -92.22) * mm, "end": v(-12.56, -92.65) * mm});
            skLineSegment(sketch, "E1528", {"start": v(-12.56, -92.65) * mm, "end": v(-12.43, -93.1) * mm});
            skLineSegment(sketch, "E1529", {"start": v(-12.43, -93.1) * mm, "end": v(-12.3, -93.55) * mm});
            skLineSegment(sketch, "E1530", {"start": v(-12.3, -93.55) * mm, "end": v(-12.15, -94) * mm});
            skLineSegment(sketch, "E1531", {"start": v(-12.15, -94) * mm, "end": v(-11.99, -94.48) * mm});
            skLineSegment(sketch, "E1532", {"start": v(-11.99, -94.48) * mm, "end": v(-11.82, -94.96) * mm});
            skLineSegment(sketch, "E1533", {"start": v(-11.82, -94.96) * mm, "end": v(-11.64, -95.46) * mm});
            skLineSegment(sketch, "E1534", {"start": v(-11.64, -95.46) * mm, "end": v(-11.46, -95.96) * mm});
            skLineSegment(sketch, "E1535", {"start": v(-11.46, -95.96) * mm, "end": v(-11.26, -96.47) * mm});
            skLineSegment(sketch, "E1536", {"start": v(-11.26, -96.47) * mm, "end": v(-11.05, -96.99) * mm});
            skLineSegment(sketch, "E1537", {"start": v(-11.05, -96.99) * mm, "end": v(-10.83, -97.52) * mm});
            skLineSegment(sketch, "E1538", {"start": v(-10.83, -97.52) * mm, "end": v(-10.6, -98.05) * mm});
            skLineSegment(sketch, "E1539", {"start": v(-10.6, -98.05) * mm, "end": v(-10.35, -98.6) * mm});
            skLineSegment(sketch, "E1540", {"start": v(-10.35, -98.6) * mm, "end": v(-10.1, -99.15) * mm});
            skLineSegment(sketch, "E1541", {"start": v(-10.1, -99.15) * mm, "end": v(-9.83, -99.72) * mm});
            skLineSegment(sketch, "E1542", {"start": v(-9.83, -99.72) * mm, "end": v(-9.56, -100.29) * mm});
            skLineSegment(sketch, "E1543", {"start": v(-9.56, -100.29) * mm, "end": v(-9.27, -100.86) * mm});
            skLineSegment(sketch, "E1544", {"start": v(-9.27, -100.86) * mm, "end": v(-8.96, -101.45) * mm});
            skLineSegment(sketch, "E1545", {"start": v(-8.96, -101.45) * mm, "end": v(-8.65, -102.04) * mm});
            skLineSegment(sketch, "E1546", {"start": v(-8.65, -102.04) * mm, "end": v(-8.28, -102.25) * mm});
            skLineSegment(sketch, "E1547", {"start": v(-8.28, -102.25) * mm, "end": v(-6.03, -102.41) * mm});
            skLineSegment(sketch, "E1548", {"start": v(-6.03, -102.41) * mm, "end": v(-5.64, -102.26) * mm});
            skLineSegment(sketch, "E1549", {"start": v(-5.64, -102.26) * mm, "end": v(-5.25, -101.72) * mm});
            skLineSegment(sketch, "E1550", {"start": v(-5.25, -101.72) * mm, "end": v(-4.86, -101.18) * mm});
            skLineSegment(sketch, "E1551", {"start": v(-4.86, -101.18) * mm, "end": v(-4.5, -100.65) * mm});
            skLineSegment(sketch, "E1552", {"start": v(-4.5, -100.65) * mm, "end": v(-4.14, -100.12) * mm});
            skLineSegment(sketch, "E1553", {"start": v(-4.14, -100.12) * mm, "end": v(-3.8, -99.6) * mm});
            skLineSegment(sketch, "E1554", {"start": v(-3.8, -99.6) * mm, "end": v(-3.46, -99.1) * mm});
            skLineSegment(sketch, "E1555", {"start": v(-3.46, -99.1) * mm, "end": v(-3.14, -98.59) * mm});
            skLineSegment(sketch, "E1556", {"start": v(-3.14, -98.59) * mm, "end": v(-2.84, -98.09) * mm});
            skLineSegment(sketch, "E1557", {"start": v(-2.84, -98.09) * mm, "end": v(-2.54, -97.6) * mm});
            skLineSegment(sketch, "E1558", {"start": v(-2.54, -97.6) * mm, "end": v(-2.26, -97.11) * mm});
            skLineSegment(sketch, "E1559", {"start": v(-2.26, -97.11) * mm, "end": v(-2, -96.64) * mm});
            skLineSegment(sketch, "E1560", {"start": v(-2, -96.64) * mm, "end": v(-1.74, -96.17) * mm});
            skLineSegment(sketch, "E1561", {"start": v(-1.74, -96.17) * mm, "end": v(-1.5, -95.7) * mm});
            skLineSegment(sketch, "E1562", {"start": v(-1.5, -95.7) * mm, "end": v(-1.26, -95.25) * mm});
            skLineSegment(sketch, "E1563", {"start": v(-1.26, -95.25) * mm, "end": v(-1.03, -94.8) * mm});
            skLineSegment(sketch, "E1564", {"start": v(-1.03, -94.8) * mm, "end": v(-0.82, -94.37) * mm});
            skLineSegment(sketch, "E1565", {"start": v(-0.82, -94.37) * mm, "end": v(-0.62, -93.94) * mm});
            skLineSegment(sketch, "E1566", {"start": v(-0.62, -93.94) * mm, "end": v(-0.43, -93.52) * mm});
            skLineSegment(sketch, "E1567", {"start": v(-0.43, -93.52) * mm, "end": v(-0.25, -93.1) * mm});
            skLineSegment(sketch, "E1568", {"start": v(-0.25, -93.1) * mm, "end": v(-0.07, -92.7) * mm});
            skLineSegment(sketch, "E1569", {"start": v(-0.07, -92.7) * mm, "end": v(0.09, -92.32) * mm});
            skLineSegment(sketch, "E1570", {"start": v(0.09, -92.32) * mm, "end": v(0.24, -91.93) * mm});
            skLineSegment(sketch, "E1571", {"start": v(0.24, -91.93) * mm, "end": v(0.39, -91.56) * mm});
            skLineSegment(sketch, "E1572", {"start": v(0.39, -91.56) * mm, "end": v(0.52, -91.2) * mm});
            skLineSegment(sketch, "E1573", {"start": v(0.52, -91.2) * mm, "end": v(0.65, -90.85) * mm});
            skLineSegment(sketch, "E1574", {"start": v(0.65, -90.85) * mm, "end": v(0.77, -90.5) * mm});
            skLineSegment(sketch, "E1575", {"start": v(0.77, -90.5) * mm, "end": v(0.88, -90.17) * mm});
            skLineSegment(sketch, "E1576", {"start": v(0.88, -90.17) * mm, "end": v(0.98, -89.85) * mm});
            skLineSegment(sketch, "E1577", {"start": v(0.98, -89.85) * mm, "end": v(1.07, -89.54) * mm});
            skLineSegment(sketch, "E1578", {"start": v(1.07, -89.54) * mm, "end": v(1.16, -89.24) * mm});
            skLineSegment(sketch, "E1579", {"start": v(1.16, -89.24) * mm, "end": v(1.24, -88.95) * mm});
            skLineSegment(sketch, "E1580", {"start": v(1.24, -88.95) * mm, "end": v(1.32, -88.67) * mm});
            skLineSegment(sketch, "E1581", {"start": v(1.32, -88.67) * mm, "end": v(1.38, -88.4) * mm});
            skLineSegment(sketch, "E1582", {"start": v(1.38, -88.4) * mm, "end": v(1.9, -88.36) * mm});
            skLineSegment(sketch, "E1583", {"start": v(1.9, -88.36) * mm, "end": v(4.94, -88.25) * mm});
            skLineSegment(sketch, "E1584", {"start": v(4.94, -88.25) * mm, "end": v(5.45, -88.26) * mm});
            skLineSegment(sketch, "E1585", {"start": v(5.45, -88.26) * mm, "end": v(5.54, -88.52) * mm});
            skLineSegment(sketch, "E1586", {"start": v(5.54, -88.52) * mm, "end": v(5.63, -88.79) * mm});
            skLineSegment(sketch, "E1587", {"start": v(5.63, -88.79) * mm, "end": v(5.74, -89.07) * mm});
            skLineSegment(sketch, "E1588", {"start": v(5.74, -89.07) * mm, "end": v(5.85, -89.36) * mm});
            skLineSegment(sketch, "E1589", {"start": v(5.85, -89.36) * mm, "end": v(5.96, -89.67) * mm});
            skLineSegment(sketch, "E1590", {"start": v(5.96, -89.67) * mm, "end": v(6.09, -89.98) * mm});
            skLineSegment(sketch, "E1591", {"start": v(6.09, -89.98) * mm, "end": v(6.22, -90.3) * mm});
            skLineSegment(sketch, "E1592", {"start": v(6.22, -90.3) * mm, "end": v(6.37, -90.64) * mm});
            skLineSegment(sketch, "E1593", {"start": v(6.37, -90.64) * mm, "end": v(6.52, -90.98) * mm});
            skLineSegment(sketch, "E1594", {"start": v(6.52, -90.98) * mm, "end": v(6.68, -91.33) * mm});
            skLineSegment(sketch, "E1595", {"start": v(6.68, -91.33) * mm, "end": v(6.85, -91.7) * mm});
            skLineSegment(sketch, "E1596", {"start": v(6.85, -91.7) * mm, "end": v(7.03, -92.06) * mm});
            skLineSegment(sketch, "E1597", {"start": v(7.03, -92.06) * mm, "end": v(7.22, -92.44) * mm});
            skLineSegment(sketch, "E1598", {"start": v(7.22, -92.44) * mm, "end": v(7.42, -92.83) * mm});
            skLineSegment(sketch, "E1599", {"start": v(7.42, -92.83) * mm, "end": v(7.64, -93.22) * mm});
            skLineSegment(sketch, "E1600", {"start": v(7.64, -93.22) * mm, "end": v(7.86, -93.63) * mm});
            skLineSegment(sketch, "E1601", {"start": v(7.86, -93.63) * mm, "end": v(8.1, -94.04) * mm});
            skLineSegment(sketch, "E1602", {"start": v(8.1, -94.04) * mm, "end": v(8.33, -94.46) * mm});
            skLineSegment(sketch, "E1603", {"start": v(8.33, -94.46) * mm, "end": v(8.6, -94.89) * mm});
            skLineSegment(sketch, "E1604", {"start": v(8.6, -94.89) * mm, "end": v(8.86, -95.32) * mm});
            skLineSegment(sketch, "E1605", {"start": v(8.86, -95.32) * mm, "end": v(9.14, -95.76) * mm});
            skLineSegment(sketch, "E1606", {"start": v(9.14, -95.76) * mm, "end": v(9.43, -96.21) * mm});
            skLineSegment(sketch, "E1607", {"start": v(9.43, -96.21) * mm, "end": v(9.73, -96.67) * mm});
            skLineSegment(sketch, "E1608", {"start": v(9.73, -96.67) * mm, "end": v(10.05, -97.13) * mm});
            skLineSegment(sketch, "E1609", {"start": v(10.05, -97.13) * mm, "end": v(10.37, -97.6) * mm});
            skLineSegment(sketch, "E1610", {"start": v(10.37, -97.6) * mm, "end": v(10.72, -98.08) * mm});
            skLineSegment(sketch, "E1611", {"start": v(10.72, -98.08) * mm, "end": v(11.07, -98.56) * mm});
            skLineSegment(sketch, "E1612", {"start": v(11.07, -98.56) * mm, "end": v(11.44, -99.04) * mm});
            skLineSegment(sketch, "E1613", {"start": v(11.44, -99.04) * mm, "end": v(11.82, -99.54) * mm});
            skLineSegment(sketch, "E1614", {"start": v(11.82, -99.54) * mm, "end": v(12.21, -100.03) * mm});
            skLineSegment(sketch, "E1615", {"start": v(12.21, -100.03) * mm, "end": v(12.62, -100.54) * mm});
            skLineSegment(sketch, "E1616", {"start": v(12.62, -100.54) * mm, "end": v(13.04, -101.04) * mm});
            skLineSegment(sketch, "E1617", {"start": v(13.04, -101.04) * mm, "end": v(13.48, -101.55) * mm});
            skLineSegment(sketch, "E1618", {"start": v(13.48, -101.55) * mm, "end": v(13.88, -101.68) * mm});
            skLineSegment(sketch, "E1619", {"start": v(13.88, -101.68) * mm, "end": v(16.11, -101.35) * mm});
            skLineSegment(sketch, "E1620", {"start": v(16.11, -101.35) * mm, "end": v(16.46, -101.12) * mm});
            skLineSegment(sketch, "E1621", {"start": v(16.46, -101.12) * mm, "end": v(16.73, -100.5) * mm});
            skLineSegment(sketch, "E1622", {"start": v(16.73, -100.5) * mm, "end": v(16.99, -99.9) * mm});
            skLineSegment(sketch, "E1623", {"start": v(16.99, -99.9) * mm, "end": v(17.24, -99.3) * mm});
            skLineSegment(sketch, "E1624", {"start": v(17.24, -99.3) * mm, "end": v(17.47, -98.7) * mm});
            skLineSegment(sketch, "E1625", {"start": v(17.47, -98.7) * mm, "end": v(17.7, -98.13) * mm});
            skLineSegment(sketch, "E1626", {"start": v(17.7, -98.13) * mm, "end": v(17.9, -97.56) * mm});
            skLineSegment(sketch, "E1627", {"start": v(17.9, -97.56) * mm, "end": v(18.11, -97) * mm});
            skLineSegment(sketch, "E1628", {"start": v(18.11, -97) * mm, "end": v(18.3, -96.44) * mm});
            skLineSegment(sketch, "E1629", {"start": v(18.3, -96.44) * mm, "end": v(18.48, -95.9) * mm});
            skLineSegment(sketch, "E1630", {"start": v(18.48, -95.9) * mm, "end": v(18.65, -95.36) * mm});
            skLineSegment(sketch, "E1631", {"start": v(18.65, -95.36) * mm, "end": v(18.81, -94.84) * mm});
            skLineSegment(sketch, "E1632", {"start": v(18.81, -94.84) * mm, "end": v(18.96, -94.33) * mm});
            skLineSegment(sketch, "E1633", {"start": v(18.96, -94.33) * mm, "end": v(19.1, -93.82) * mm});
            skLineSegment(sketch, "E1634", {"start": v(19.1, -93.82) * mm, "end": v(19.24, -93.33) * mm});
            skLineSegment(sketch, "E1635", {"start": v(19.24, -93.33) * mm, "end": v(19.36, -92.85) * mm});
            skLineSegment(sketch, "E1636", {"start": v(19.36, -92.85) * mm, "end": v(19.47, -92.37) * mm});
            skLineSegment(sketch, "E1637", {"start": v(19.47, -92.37) * mm, "end": v(19.58, -91.91) * mm});
            skLineSegment(sketch, "E1638", {"start": v(19.58, -91.91) * mm, "end": v(19.67, -91.46) * mm});
            skLineSegment(sketch, "E1639", {"start": v(19.67, -91.46) * mm, "end": v(19.76, -91.02) * mm});
            skLineSegment(sketch, "E1640", {"start": v(19.76, -91.02) * mm, "end": v(19.84, -90.6) * mm});
            skLineSegment(sketch, "E1641", {"start": v(19.84, -90.6) * mm, "end": v(19.92, -90.18) * mm});
            skLineSegment(sketch, "E1642", {"start": v(19.92, -90.18) * mm, "end": v(19.99, -89.77) * mm});
            skLineSegment(sketch, "E1643", {"start": v(19.99, -89.77) * mm, "end": v(20.05, -89.37) * mm});
            skLineSegment(sketch, "E1644", {"start": v(20.05, -89.37) * mm, "end": v(20.1, -89) * mm});
            skLineSegment(sketch, "E1645", {"start": v(20.1, -89) * mm, "end": v(20.15, -88.62) * mm});
            skLineSegment(sketch, "E1646", {"start": v(20.15, -88.62) * mm, "end": v(20.2, -88.26) * mm});
            skLineSegment(sketch, "E1647", {"start": v(20.2, -88.26) * mm, "end": v(20.23, -87.91) * mm});
            skLineSegment(sketch, "E1648", {"start": v(20.23, -87.91) * mm, "end": v(20.26, -87.58) * mm});
            skLineSegment(sketch, "E1649", {"start": v(20.26, -87.58) * mm, "end": v(20.28, -87.25) * mm});
            skLineSegment(sketch, "E1650", {"start": v(20.28, -87.25) * mm, "end": v(20.3, -86.94) * mm});
            skLineSegment(sketch, "E1651", {"start": v(20.3, -86.94) * mm, "end": v(20.32, -86.64) * mm});
            skLineSegment(sketch, "E1652", {"start": v(20.32, -86.64) * mm, "end": v(20.33, -86.35) * mm});
            skLineSegment(sketch, "E1653", {"start": v(20.33, -86.35) * mm, "end": v(20.34, -86.08) * mm});
            skLineSegment(sketch, "E1654", {"start": v(20.34, -86.08) * mm, "end": v(20.83, -85.93) * mm});
            skLineSegment(sketch, "E1655", {"start": v(20.83, -85.93) * mm, "end": v(23.79, -85.16) * mm});
            skLineSegment(sketch, "E1656", {"start": v(23.79, -85.16) * mm, "end": v(24.28, -85.06) * mm});
            skLineSegment(sketch, "E1657", {"start": v(24.28, -85.06) * mm, "end": v(24.43, -85.3) * mm});
            skLineSegment(sketch, "E1658", {"start": v(24.43, -85.3) * mm, "end": v(24.58, -85.54) * mm});
            skLineSegment(sketch, "E1659", {"start": v(24.58, -85.54) * mm, "end": v(24.74, -85.8) * mm});
            skLineSegment(sketch, "E1660", {"start": v(24.74, -85.8) * mm, "end": v(24.9, -86.05) * mm});
            skLineSegment(sketch, "E1661", {"start": v(24.9, -86.05) * mm, "end": v(25.09, -86.33) * mm});
            skLineSegment(sketch, "E1662", {"start": v(25.09, -86.33) * mm, "end": v(25.28, -86.6) * mm});
            skLineSegment(sketch, "E1663", {"start": v(25.28, -86.6) * mm, "end": v(25.48, -86.9) * mm});
            skLineSegment(sketch, "E1664", {"start": v(25.48, -86.9) * mm, "end": v(25.69, -87.18) * mm});
            skLineSegment(sketch, "E1665", {"start": v(25.69, -87.18) * mm, "end": v(25.91, -87.49) * mm});
            skLineSegment(sketch, "E1666", {"start": v(25.91, -87.49) * mm, "end": v(26.14, -87.8) * mm});
            skLineSegment(sketch, "E1667", {"start": v(26.14, -87.8) * mm, "end": v(26.39, -88.11) * mm});
            skLineSegment(sketch, "E1668", {"start": v(26.39, -88.11) * mm, "end": v(26.64, -88.43) * mm});
            skLineSegment(sketch, "E1669", {"start": v(26.64, -88.43) * mm, "end": v(26.91, -88.76) * mm});
            skLineSegment(sketch, "E1670", {"start": v(26.91, -88.76) * mm, "end": v(27.2, -89.1) * mm});
            skLineSegment(sketch, "E1671", {"start": v(27.2, -89.1) * mm, "end": v(27.48, -89.44) * mm});
            skLineSegment(sketch, "E1672", {"start": v(27.48, -89.44) * mm, "end": v(27.79, -89.79) * mm});
            skLineSegment(sketch, "E1673", {"start": v(27.79, -89.79) * mm, "end": v(28.1, -90.14) * mm});
            skLineSegment(sketch, "E1674", {"start": v(28.1, -90.14) * mm, "end": v(28.43, -90.5) * mm});
            skLineSegment(sketch, "E1675", {"start": v(28.43, -90.5) * mm, "end": v(28.77, -90.86) * mm});
            skLineSegment(sketch, "E1676", {"start": v(28.77, -90.86) * mm, "end": v(29.13, -91.23) * mm});
            skLineSegment(sketch, "E1677", {"start": v(29.13, -91.23) * mm, "end": v(29.5, -91.6) * mm});
            skLineSegment(sketch, "E1678", {"start": v(29.5, -91.6) * mm, "end": v(29.88, -91.97) * mm});
            skLineSegment(sketch, "E1679", {"start": v(29.88, -91.97) * mm, "end": v(30.27, -92.36) * mm});
            skLineSegment(sketch, "E1680", {"start": v(30.27, -92.36) * mm, "end": v(30.68, -92.74) * mm});
            skLineSegment(sketch, "E1681", {"start": v(30.68, -92.74) * mm, "end": v(31.1, -93.13) * mm});
            skLineSegment(sketch, "E1682", {"start": v(31.1, -93.13) * mm, "end": v(31.54, -93.52) * mm});
            skLineSegment(sketch, "E1683", {"start": v(31.54, -93.52) * mm, "end": v(31.99, -93.91) * mm});
            skLineSegment(sketch, "E1684", {"start": v(31.99, -93.91) * mm, "end": v(32.45, -94.3) * mm});
            skLineSegment(sketch, "E1685", {"start": v(32.45, -94.3) * mm, "end": v(32.93, -94.7) * mm});
            skLineSegment(sketch, "E1686", {"start": v(32.93, -94.7) * mm, "end": v(33.42, -95.1) * mm});
            skLineSegment(sketch, "E1687", {"start": v(33.42, -95.1) * mm, "end": v(33.93, -95.5) * mm});
            skLineSegment(sketch, "E1688", {"start": v(33.93, -95.5) * mm, "end": v(34.45, -95.91) * mm});
            skLineSegment(sketch, "E1689", {"start": v(34.45, -95.91) * mm, "end": v(34.98, -96.32) * mm});
            skLineSegment(sketch, "E1690", {"start": v(34.98, -96.32) * mm, "end": v(35.4, -96.36) * mm});
            skLineSegment(sketch, "E1691", {"start": v(35.4, -96.36) * mm, "end": v(37.51, -95.56) * mm});
            skLineSegment(sketch, "E1692", {"start": v(37.51, -95.56) * mm, "end": v(37.8, -95.25) * mm});
            skLineSegment(sketch, "E1693", {"start": v(37.8, -95.25) * mm, "end": v(37.93, -94.6) * mm});
            skLineSegment(sketch, "E1694", {"start": v(37.93, -94.6) * mm, "end": v(38.05, -93.95) * mm});
            skLineSegment(sketch, "E1695", {"start": v(38.05, -93.95) * mm, "end": v(38.17, -93.3) * mm});
            skLineSegment(sketch, "E1696", {"start": v(38.17, -93.3) * mm, "end": v(38.27, -92.68) * mm});
            skLineSegment(sketch, "E1697", {"start": v(38.27, -92.68) * mm, "end": v(38.37, -92.07) * mm});
            skLineSegment(sketch, "E1698", {"start": v(38.37, -92.07) * mm, "end": v(38.45, -91.46) * mm});
            skLineSegment(sketch, "E1699", {"start": v(38.45, -91.46) * mm, "end": v(38.53, -90.87) * mm});
            skLineSegment(sketch, "E1700", {"start": v(38.53, -90.87) * mm, "end": v(38.6, -90.3) * mm});
            skLineSegment(sketch, "E1701", {"start": v(38.6, -90.3) * mm, "end": v(38.65, -89.72) * mm});
            skLineSegment(sketch, "E1702", {"start": v(38.65, -89.72) * mm, "end": v(38.7, -89.16) * mm});
            skLineSegment(sketch, "E1703", {"start": v(38.7, -89.16) * mm, "end": v(38.75, -88.62) * mm});
            skLineSegment(sketch, "E1704", {"start": v(38.75, -88.62) * mm, "end": v(38.79, -88.08) * mm});
            skLineSegment(sketch, "E1705", {"start": v(38.79, -88.08) * mm, "end": v(38.81, -87.56) * mm});
            skLineSegment(sketch, "E1706", {"start": v(38.81, -87.56) * mm, "end": v(38.84, -87.05) * mm});
            skLineSegment(sketch, "E1707", {"start": v(38.84, -87.05) * mm, "end": v(38.85, -86.55) * mm});
            skLineSegment(sketch, "E1708", {"start": v(38.85, -86.55) * mm, "end": v(38.86, -86.07) * mm});
            skLineSegment(sketch, "E1709", {"start": v(38.86, -86.07) * mm, "end": v(38.87, -85.6) * mm});
            skLineSegment(sketch, "E1710", {"start": v(38.87, -85.6) * mm, "end": v(38.86, -85.13) * mm});
            skLineSegment(sketch, "E1711", {"start": v(38.86, -85.13) * mm, "end": v(38.86, -84.68) * mm});
            skLineSegment(sketch, "E1712", {"start": v(38.86, -84.68) * mm, "end": v(38.84, -84.25) * mm});
            skLineSegment(sketch, "E1713", {"start": v(38.84, -84.25) * mm, "end": v(38.83, -83.82) * mm});
            skLineSegment(sketch, "E1714", {"start": v(38.83, -83.82) * mm, "end": v(38.8, -83.41) * mm});
            skLineSegment(sketch, "E1715", {"start": v(38.8, -83.41) * mm, "end": v(38.78, -83.01) * mm});
            skLineSegment(sketch, "E1716", {"start": v(38.78, -83.01) * mm, "end": v(38.75, -82.63) * mm});
            skLineSegment(sketch, "E1717", {"start": v(38.75, -82.63) * mm, "end": v(38.72, -82.25) * mm});
            skLineSegment(sketch, "E1718", {"start": v(38.72, -82.25) * mm, "end": v(38.68, -81.9) * mm});
            skLineSegment(sketch, "E1719", {"start": v(38.68, -81.9) * mm, "end": v(38.64, -81.55) * mm});
            skLineSegment(sketch, "E1720", {"start": v(38.64, -81.55) * mm, "end": v(38.6, -81.21) * mm});
            skLineSegment(sketch, "E1721", {"start": v(38.6, -81.21) * mm, "end": v(38.55, -80.9) * mm});
            skLineSegment(sketch, "E1722", {"start": v(38.55, -80.9) * mm, "end": v(38.5, -80.58) * mm});
            skLineSegment(sketch, "E1723", {"start": v(38.5, -80.58) * mm, "end": v(38.46, -80.28) * mm});
            skLineSegment(sketch, "E1724", {"start": v(38.46, -80.28) * mm, "end": v(38.4, -80) * mm});
            skLineSegment(sketch, "E1725", {"start": v(38.4, -80) * mm, "end": v(38.36, -79.73) * mm});
            skLineSegment(sketch, "E1726", {"start": v(38.36, -79.73) * mm, "end": v(38.8, -79.48) * mm});
            skLineSegment(sketch, "E1727", {"start": v(38.8, -79.48) * mm, "end": v(41.53, -78.1) * mm});
            skLineSegment(sketch, "E1728", {"start": v(41.53, -78.1) * mm, "end": v(41.99, -77.88) * mm});
            skLineSegment(sketch, "E1729", {"start": v(41.99, -77.88) * mm, "end": v(42.18, -78.09) * mm});
            skLineSegment(sketch, "E1730", {"start": v(42.18, -78.09) * mm, "end": v(42.38, -78.3) * mm});
            skLineSegment(sketch, "E1731", {"start": v(42.38, -78.3) * mm, "end": v(42.59, -78.5) * mm});
            skLineSegment(sketch, "E1732", {"start": v(42.59, -78.5) * mm, "end": v(42.81, -78.73) * mm});
            skLineSegment(sketch, "E1733", {"start": v(42.81, -78.73) * mm, "end": v(43.05, -78.95) * mm});
            skLineSegment(sketch, "E1734", {"start": v(43.05, -78.95) * mm, "end": v(43.3, -79.18) * mm});
            skLineSegment(sketch, "E1735", {"start": v(43.3, -79.18) * mm, "end": v(43.55, -79.42) * mm});
            skLineSegment(sketch, "E1736", {"start": v(43.55, -79.42) * mm, "end": v(43.82, -79.66) * mm});
            skLineSegment(sketch, "E1737", {"start": v(43.82, -79.66) * mm, "end": v(44.1, -79.9) * mm});
            skLineSegment(sketch, "E1738", {"start": v(44.1, -79.9) * mm, "end": v(44.4, -80.16) * mm});
            skLineSegment(sketch, "E1739", {"start": v(44.4, -80.16) * mm, "end": v(44.7, -80.41) * mm});
            skLineSegment(sketch, "E1740", {"start": v(44.7, -80.41) * mm, "end": v(45.02, -80.68) * mm});
            skLineSegment(sketch, "E1741", {"start": v(45.02, -80.68) * mm, "end": v(45.35, -80.94) * mm});
            skLineSegment(sketch, "E1742", {"start": v(45.35, -80.94) * mm, "end": v(45.7, -81.2) * mm});
            skLineSegment(sketch, "E1743", {"start": v(45.7, -81.2) * mm, "end": v(46.05, -81.48) * mm});
            skLineSegment(sketch, "E1744", {"start": v(46.05, -81.48) * mm, "end": v(46.43, -81.75) * mm});
            skLineSegment(sketch, "E1745", {"start": v(46.43, -81.75) * mm, "end": v(46.81, -82.03) * mm});
            skLineSegment(sketch, "E1746", {"start": v(46.81, -82.03) * mm, "end": v(47.2, -82.3) * mm});
            skLineSegment(sketch, "E1747", {"start": v(47.2, -82.3) * mm, "end": v(47.62, -82.59) * mm});
            skLineSegment(sketch, "E1748", {"start": v(47.62, -82.59) * mm, "end": v(48.05, -82.87) * mm});
            skLineSegment(sketch, "E1749", {"start": v(48.05, -82.87) * mm, "end": v(48.49, -83.15) * mm});
            skLineSegment(sketch, "E1750", {"start": v(48.49, -83.15) * mm, "end": v(48.94, -83.44) * mm});
            skLineSegment(sketch, "E1751", {"start": v(48.94, -83.44) * mm, "end": v(49.4, -83.72) * mm});
            skLineSegment(sketch, "E1752", {"start": v(49.4, -83.72) * mm, "end": v(49.89, -84.01) * mm});
            skLineSegment(sketch, "E1753", {"start": v(49.89, -84.01) * mm, "end": v(50.38, -84.3) * mm});
            skLineSegment(sketch, "E1754", {"start": v(50.38, -84.3) * mm, "end": v(50.9, -84.59) * mm});
            skLineSegment(sketch, "E1755", {"start": v(50.9, -84.59) * mm, "end": v(51.41, -84.88) * mm});
            skLineSegment(sketch, "E1756", {"start": v(51.41, -84.88) * mm, "end": v(51.95, -85.16) * mm});
            skLineSegment(sketch, "E1757", {"start": v(51.95, -85.16) * mm, "end": v(52.5, -85.45) * mm});
            skLineSegment(sketch, "E1758", {"start": v(52.5, -85.45) * mm, "end": v(53.07, -85.74) * mm});
            skLineSegment(sketch, "E1759", {"start": v(53.07, -85.74) * mm, "end": v(53.65, -86.02) * mm});
            skLineSegment(sketch, "E1760", {"start": v(53.65, -86.02) * mm, "end": v(54.25, -86.3) * mm});
            skLineSegment(sketch, "E1761", {"start": v(54.25, -86.3) * mm, "end": v(54.86, -86.58) * mm});
            skLineSegment(sketch, "E1762", {"start": v(54.86, -86.58) * mm, "end": v(55.27, -86.53) * mm});
            skLineSegment(sketch, "E1763", {"start": v(55.27, -86.53) * mm, "end": v(57.16, -85.3) * mm});
            skLineSegment(sketch, "E1764", {"start": v(57.16, -85.3) * mm, "end": v(57.38, -84.94) * mm});
            skLineSegment(sketch, "E1765", {"start": v(57.38, -84.94) * mm, "end": v(57.37, -84.26) * mm});
            skLineSegment(sketch, "E1766", {"start": v(57.37, -84.26) * mm, "end": v(57.35, -83.6) * mm});
            skLineSegment(sketch, "E1767", {"start": v(57.35, -83.6) * mm, "end": v(57.32, -82.96) * mm});
            skLineSegment(sketch, "E1768", {"start": v(57.32, -82.96) * mm, "end": v(57.29, -82.33) * mm});
            skLineSegment(sketch, "E1769", {"start": v(57.29, -82.33) * mm, "end": v(57.25, -81.7) * mm});
            skLineSegment(sketch, "E1770", {"start": v(57.25, -81.7) * mm, "end": v(57.2, -81.1) * mm});
            skLineSegment(sketch, "E1771", {"start": v(57.2, -81.1) * mm, "end": v(57.15, -80.5) * mm});
            skLineSegment(sketch, "E1772", {"start": v(57.15, -80.5) * mm, "end": v(57.1, -79.92) * mm});
            skLineSegment(sketch, "E1773", {"start": v(57.1, -79.92) * mm, "end": v(57.03, -79.35) * mm});
            skLineSegment(sketch, "E1774", {"start": v(57.03, -79.35) * mm, "end": v(56.96, -78.8) * mm});
            skLineSegment(sketch, "E1775", {"start": v(56.96, -78.8) * mm, "end": v(56.88, -78.25) * mm});
            skLineSegment(sketch, "E1776", {"start": v(56.88, -78.25) * mm, "end": v(56.8, -77.72) * mm});
            skLineSegment(sketch, "E1777", {"start": v(56.8, -77.72) * mm, "end": v(56.72, -77.2) * mm});
            skLineSegment(sketch, "E1778", {"start": v(56.72, -77.2) * mm, "end": v(56.63, -76.7) * mm});
            skLineSegment(sketch, "E1779", {"start": v(56.63, -76.7) * mm, "end": v(56.54, -76.21) * mm});
            skLineSegment(sketch, "E1780", {"start": v(56.54, -76.21) * mm, "end": v(56.44, -75.74) * mm});
            skLineSegment(sketch, "E1781", {"start": v(56.44, -75.74) * mm, "end": v(56.34, -75.27) * mm});
            skLineSegment(sketch, "E1782", {"start": v(56.34, -75.27) * mm, "end": v(56.24, -74.82) * mm});
            skLineSegment(sketch, "E1783", {"start": v(56.24, -74.82) * mm, "end": v(56.14, -74.39) * mm});
            skLineSegment(sketch, "E1784", {"start": v(56.14, -74.39) * mm, "end": v(56.03, -73.96) * mm});
            skLineSegment(sketch, "E1785", {"start": v(56.03, -73.96) * mm, "end": v(55.93, -73.55) * mm});
            skLineSegment(sketch, "E1786", {"start": v(55.93, -73.55) * mm, "end": v(55.82, -73.16) * mm});
            skLineSegment(sketch, "E1787", {"start": v(55.82, -73.16) * mm, "end": v(55.7, -72.77) * mm});
            skLineSegment(sketch, "E1788", {"start": v(55.7, -72.77) * mm, "end": v(55.6, -72.4) * mm});
            skLineSegment(sketch, "E1789", {"start": v(55.6, -72.4) * mm, "end": v(55.48, -72.05) * mm});
            skLineSegment(sketch, "E1790", {"start": v(55.48, -72.05) * mm, "end": v(55.37, -71.7) * mm});
            skLineSegment(sketch, "E1791", {"start": v(55.37, -71.7) * mm, "end": v(55.25, -71.37) * mm});
            skLineSegment(sketch, "E1792", {"start": v(55.25, -71.37) * mm, "end": v(55.14, -71.05) * mm});
            skLineSegment(sketch, "E1793", {"start": v(55.14, -71.05) * mm, "end": v(55.03, -70.75) * mm});
            skLineSegment(sketch, "E1794", {"start": v(55.03, -70.75) * mm, "end": v(54.92, -70.46) * mm});
            skLineSegment(sketch, "E1795", {"start": v(54.92, -70.46) * mm, "end": v(54.8, -70.18) * mm});
            skLineSegment(sketch, "E1796", {"start": v(54.8, -70.18) * mm, "end": v(54.7, -69.9) * mm});
            skLineSegment(sketch, "E1797", {"start": v(54.7, -69.9) * mm, "end": v(54.59, -69.66) * mm});
            skLineSegment(sketch, "E1798", {"start": v(54.59, -69.66) * mm, "end": v(54.97, -69.32) * mm});
            skLineSegment(sketch, "E1799", {"start": v(54.97, -69.32) * mm, "end": v(57.33, -67.38) * mm});
            skLineSegment(sketch, "E1800", {"start": v(57.33, -67.38) * mm, "end": v(57.74, -67.07) * mm});
            skLineSegment(sketch, "E1801", {"start": v(57.74, -67.07) * mm, "end": v(57.97, -67.23) * mm});
            skLineSegment(sketch, "E1802", {"start": v(57.97, -67.23) * mm, "end": v(58.2, -67.39) * mm});
            skLineSegment(sketch, "E1803", {"start": v(58.2, -67.39) * mm, "end": v(58.46, -67.55) * mm});
            skLineSegment(sketch, "E1804", {"start": v(58.46, -67.55) * mm, "end": v(58.72, -67.72) * mm});
            skLineSegment(sketch, "E1805", {"start": v(58.72, -67.72) * mm, "end": v(59, -67.89) * mm});
            skLineSegment(sketch, "E1806", {"start": v(59, -67.89) * mm, "end": v(59.29, -68.06) * mm});
            skLineSegment(sketch, "E1807", {"start": v(59.29, -68.06) * mm, "end": v(59.6, -68.24) * mm});
            skLineSegment(sketch, "E1808", {"start": v(59.6, -68.24) * mm, "end": v(59.9, -68.42) * mm});
            skLineSegment(sketch, "E1809", {"start": v(59.9, -68.42) * mm, "end": v(60.23, -68.6) * mm});
            skLineSegment(sketch, "E1810", {"start": v(60.23, -68.6) * mm, "end": v(60.58, -68.78) * mm});
            skLineSegment(sketch, "E1811", {"start": v(60.58, -68.78) * mm, "end": v(60.93, -68.96) * mm});
            skLineSegment(sketch, "E1812", {"start": v(60.93, -68.96) * mm, "end": v(61.3, -69.15) * mm});
            skLineSegment(sketch, "E1813", {"start": v(61.3, -69.15) * mm, "end": v(61.68, -69.33) * mm});
            skLineSegment(sketch, "E1814", {"start": v(61.68, -69.33) * mm, "end": v(62.07, -69.52) * mm});
            skLineSegment(sketch, "E1815", {"start": v(62.07, -69.52) * mm, "end": v(62.48, -69.7) * mm});
            skLineSegment(sketch, "E1816", {"start": v(62.48, -69.7) * mm, "end": v(62.9, -69.9) * mm});
            skLineSegment(sketch, "E1817", {"start": v(62.9, -69.9) * mm, "end": v(63.34, -70.08) * mm});
            skLineSegment(sketch, "E1818", {"start": v(63.34, -70.08) * mm, "end": v(63.79, -70.27) * mm});
            skLineSegment(sketch, "E1819", {"start": v(63.79, -70.27) * mm, "end": v(64.25, -70.45) * mm});
            skLineSegment(sketch, "E1820", {"start": v(64.25, -70.45) * mm, "end": v(64.72, -70.64) * mm});
            skLineSegment(sketch, "E1821", {"start": v(64.72, -70.64) * mm, "end": v(65.21, -70.82) * mm});
            skLineSegment(sketch, "E1822", {"start": v(65.21, -70.82) * mm, "end": v(65.72, -71) * mm});
            skLineSegment(sketch, "E1823", {"start": v(65.72, -71) * mm, "end": v(66.24, -71.18) * mm});
            skLineSegment(sketch, "E1824", {"start": v(66.24, -71.18) * mm, "end": v(66.77, -71.36) * mm});
            skLineSegment(sketch, "E1825", {"start": v(66.77, -71.36) * mm, "end": v(67.31, -71.54) * mm});
            skLineSegment(sketch, "E1826", {"start": v(67.31, -71.54) * mm, "end": v(67.87, -71.7) * mm});
            skLineSegment(sketch, "E1827", {"start": v(67.87, -71.7) * mm, "end": v(68.45, -71.88) * mm});
            skLineSegment(sketch, "E1828", {"start": v(68.45, -71.88) * mm, "end": v(69.03, -72.04) * mm});
            skLineSegment(sketch, "E1829", {"start": v(69.03, -72.04) * mm, "end": v(69.63, -72.2) * mm});
            skLineSegment(sketch, "E1830", {"start": v(69.63, -72.2) * mm, "end": v(70.25, -72.36) * mm});
            skLineSegment(sketch, "E1831", {"start": v(70.25, -72.36) * mm, "end": v(70.88, -72.51) * mm});
            skLineSegment(sketch, "E1832", {"start": v(70.88, -72.51) * mm, "end": v(71.52, -72.66) * mm});
            skLineSegment(sketch, "E1833", {"start": v(71.52, -72.66) * mm, "end": v(72.18, -72.8) * mm});
            skLineSegment(sketch, "E1834", {"start": v(72.18, -72.8) * mm, "end": v(72.57, -72.66) * mm});
            skLineSegment(sketch, "E1835", {"start": v(72.57, -72.66) * mm, "end": v(74.15, -71.05) * mm});
            skLineSegment(sketch, "E1836", {"start": v(74.15, -71.05) * mm, "end": v(74.28, -70.65) * mm});
            skLineSegment(sketch, "E1837", {"start": v(74.28, -70.65) * mm, "end": v(74.13, -70) * mm});
            skLineSegment(sketch, "E1838", {"start": v(74.13, -70) * mm, "end": v(73.97, -69.36) * mm});
            skLineSegment(sketch, "E1839", {"start": v(73.97, -69.36) * mm, "end": v(73.8, -68.73) * mm});
            skLineSegment(sketch, "E1840", {"start": v(73.8, -68.73) * mm, "end": v(73.63, -68.12) * mm});
            skLineSegment(sketch, "E1841", {"start": v(73.63, -68.12) * mm, "end": v(73.46, -67.52) * mm});
            skLineSegment(sketch, "E1842", {"start": v(73.46, -67.52) * mm, "end": v(73.28, -66.94) * mm});
            skLineSegment(sketch, "E1843", {"start": v(73.28, -66.94) * mm, "end": v(73.1, -66.37) * mm});
            skLineSegment(sketch, "E1844", {"start": v(73.1, -66.37) * mm, "end": v(72.92, -65.82) * mm});
            skLineSegment(sketch, "E1845", {"start": v(72.92, -65.82) * mm, "end": v(72.74, -65.27) * mm});
            skLineSegment(sketch, "E1846", {"start": v(72.74, -65.27) * mm, "end": v(72.55, -64.75) * mm});
            skLineSegment(sketch, "E1847", {"start": v(72.55, -64.75) * mm, "end": v(72.36, -64.23) * mm});
            skLineSegment(sketch, "E1848", {"start": v(72.36, -64.23) * mm, "end": v(72.17, -63.73) * mm});
            skLineSegment(sketch, "E1849", {"start": v(72.17, -63.73) * mm, "end": v(71.98, -63.25) * mm});
            skLineSegment(sketch, "E1850", {"start": v(71.98, -63.25) * mm, "end": v(71.78, -62.77) * mm});
            skLineSegment(sketch, "E1851", {"start": v(71.78, -62.77) * mm, "end": v(71.59, -62.31) * mm});
            skLineSegment(sketch, "E1852", {"start": v(71.59, -62.31) * mm, "end": v(71.4, -61.87) * mm});
            skLineSegment(sketch, "E1853", {"start": v(71.4, -61.87) * mm, "end": v(71.2, -61.44) * mm});
            skLineSegment(sketch, "E1854", {"start": v(71.2, -61.44) * mm, "end": v(71, -61.02) * mm});
            skLineSegment(sketch, "E1855", {"start": v(71, -61.02) * mm, "end": v(70.8, -60.62) * mm});
            skLineSegment(sketch, "E1856", {"start": v(70.8, -60.62) * mm, "end": v(70.6, -60.23) * mm});
            skLineSegment(sketch, "E1857", {"start": v(70.6, -60.23) * mm, "end": v(70.42, -59.85) * mm});
            skLineSegment(sketch, "E1858", {"start": v(70.42, -59.85) * mm, "end": v(70.22, -59.48) * mm});
            skLineSegment(sketch, "E1859", {"start": v(70.22, -59.48) * mm, "end": v(70.03, -59.13) * mm});
            skLineSegment(sketch, "E1860", {"start": v(70.03, -59.13) * mm, "end": v(69.85, -58.8) * mm});
            skLineSegment(sketch, "E1861", {"start": v(69.85, -58.8) * mm, "end": v(69.66, -58.47) * mm});
            skLineSegment(sketch, "E1862", {"start": v(69.66, -58.47) * mm, "end": v(69.47, -58.16) * mm});
            skLineSegment(sketch, "E1863", {"start": v(69.47, -58.16) * mm, "end": v(69.3, -57.86) * mm});
            skLineSegment(sketch, "E1864", {"start": v(69.3, -57.86) * mm, "end": v(69.11, -57.57) * mm});
            skLineSegment(sketch, "E1865", {"start": v(69.11, -57.57) * mm, "end": v(68.94, -57.3) * mm});
            skLineSegment(sketch, "E1866", {"start": v(68.94, -57.3) * mm, "end": v(68.77, -57.04) * mm});
            skLineSegment(sketch, "E1867", {"start": v(68.77, -57.04) * mm, "end": v(68.6, -56.8) * mm});
            skLineSegment(sketch, "E1868", {"start": v(68.6, -56.8) * mm, "end": v(68.43, -56.55) * mm});
            skLineSegment(sketch, "E1869", {"start": v(68.43, -56.55) * mm, "end": v(68.27, -56.33) * mm});
            skLineSegment(sketch, "E1870", {"start": v(68.27, -56.33) * mm, "end": v(68.57, -55.92) * mm});
            skLineSegment(sketch, "E1871", {"start": v(68.57, -55.92) * mm, "end": v(70.46, -53.52) * mm});
            skLineSegment(sketch, "E1872", {"start": v(70.46, -53.52) * mm, "end": v(70.8, -53.13) * mm});
            skLineSegment(sketch, "E1873", {"start": v(70.8, -53.13) * mm, "end": v(71.05, -53.23) * mm});
            skLineSegment(sketch, "E1874", {"start": v(71.05, -53.23) * mm, "end": v(71.32, -53.34) * mm});
            skLineSegment(sketch, "E1875", {"start": v(71.32, -53.34) * mm, "end": v(71.6, -53.44) * mm});
            skLineSegment(sketch, "E1876", {"start": v(71.6, -53.44) * mm, "end": v(71.9, -53.55) * mm});
            skLineSegment(sketch, "E1877", {"start": v(71.9, -53.55) * mm, "end": v(72.2, -53.66) * mm});
            skLineSegment(sketch, "E1878", {"start": v(72.2, -53.66) * mm, "end": v(72.52, -53.76) * mm});
            skLineSegment(sketch, "E1879", {"start": v(72.52, -53.76) * mm, "end": v(72.85, -53.87) * mm});
            skLineSegment(sketch, "E1880", {"start": v(72.85, -53.87) * mm, "end": v(73.2, -53.98) * mm});
            skLineSegment(sketch, "E1881", {"start": v(73.2, -53.98) * mm, "end": v(73.56, -54.08) * mm});
            skLineSegment(sketch, "E1882", {"start": v(73.56, -54.08) * mm, "end": v(73.93, -54.19) * mm});
            skLineSegment(sketch, "E1883", {"start": v(73.93, -54.19) * mm, "end": v(74.32, -54.29) * mm});
            skLineSegment(sketch, "E1884", {"start": v(74.32, -54.29) * mm, "end": v(74.72, -54.4) * mm});
            skLineSegment(sketch, "E1885", {"start": v(74.72, -54.4) * mm, "end": v(75.13, -54.5) * mm});
            skLineSegment(sketch, "E1886", {"start": v(75.13, -54.5) * mm, "end": v(75.55, -54.59) * mm});
            skLineSegment(sketch, "E1887", {"start": v(75.55, -54.59) * mm, "end": v(76, -54.68) * mm});
            skLineSegment(sketch, "E1888", {"start": v(76, -54.68) * mm, "end": v(76.44, -54.78) * mm});
            skLineSegment(sketch, "E1889", {"start": v(76.44, -54.78) * mm, "end": v(76.91, -54.86) * mm});
            skLineSegment(sketch, "E1890", {"start": v(76.91, -54.86) * mm, "end": v(77.39, -54.95) * mm});
            skLineSegment(sketch, "E1891", {"start": v(77.39, -54.95) * mm, "end": v(77.88, -55.03) * mm});
            skLineSegment(sketch, "E1892", {"start": v(77.88, -55.03) * mm, "end": v(78.38, -55.11) * mm});
            skLineSegment(sketch, "E1893", {"start": v(78.38, -55.11) * mm, "end": v(78.9, -55.18) * mm});
            skLineSegment(sketch, "E1894", {"start": v(78.9, -55.18) * mm, "end": v(79.43, -55.25) * mm});
            skLineSegment(sketch, "E1895", {"start": v(79.43, -55.25) * mm, "end": v(79.98, -55.32) * mm});
            skLineSegment(sketch, "E1896", {"start": v(79.98, -55.32) * mm, "end": v(80.53, -55.38) * mm});
            skLineSegment(sketch, "E1897", {"start": v(80.53, -55.38) * mm, "end": v(81.1, -55.43) * mm});
            skLineSegment(sketch, "E1898", {"start": v(81.1, -55.43) * mm, "end": v(81.69, -55.48) * mm});
            skLineSegment(sketch, "E1899", {"start": v(81.69, -55.48) * mm, "end": v(82.28, -55.52) * mm});
            skLineSegment(sketch, "E1900", {"start": v(82.28, -55.52) * mm, "end": v(82.9, -55.55) * mm});
            skLineSegment(sketch, "E1901", {"start": v(82.9, -55.55) * mm, "end": v(83.51, -55.58) * mm});
            skLineSegment(sketch, "E1902", {"start": v(83.51, -55.58) * mm, "end": v(84.15, -55.6) * mm});
            skLineSegment(sketch, "E1903", {"start": v(84.15, -55.6) * mm, "end": v(84.8, -55.62) * mm});
            skLineSegment(sketch, "E1904", {"start": v(84.8, -55.62) * mm, "end": v(85.45, -55.62) * mm});
            skLineSegment(sketch, "E1905", {"start": v(85.45, -55.62) * mm, "end": v(86.13, -55.62) * mm});
            skLineSegment(sketch, "E1906", {"start": v(86.13, -55.62) * mm, "end": v(86.48, -55.4) * mm});
            skLineSegment(sketch, "E1907", {"start": v(86.48, -55.4) * mm, "end": v(87.68, -53.49) * mm});
            skLineSegment(sketch, "E1908", {"start": v(87.68, -53.49) * mm, "end": v(87.72, -53.07) * mm});
            skLineSegment(sketch, "E1909", {"start": v(87.72, -53.07) * mm, "end": v(87.43, -52.47) * mm});
            skLineSegment(sketch, "E1910", {"start": v(87.43, -52.47) * mm, "end": v(87.14, -51.87) * mm});
            skLineSegment(sketch, "E1911", {"start": v(87.14, -51.87) * mm, "end": v(86.84, -51.3) * mm});
            skLineSegment(sketch, "E1912", {"start": v(86.84, -51.3) * mm, "end": v(86.54, -50.74) * mm});
            skLineSegment(sketch, "E1913", {"start": v(86.54, -50.74) * mm, "end": v(86.25, -50.2) * mm});
            skLineSegment(sketch, "E1914", {"start": v(86.25, -50.2) * mm, "end": v(85.95, -49.66) * mm});
            skLineSegment(sketch, "E1915", {"start": v(85.95, -49.66) * mm, "end": v(85.65, -49.14) * mm});
            skLineSegment(sketch, "E1916", {"start": v(85.65, -49.14) * mm, "end": v(85.35, -48.64) * mm});
            skLineSegment(sketch, "E1917", {"start": v(85.35, -48.64) * mm, "end": v(85.06, -48.15) * mm});
            skLineSegment(sketch, "E1918", {"start": v(85.06, -48.15) * mm, "end": v(84.76, -47.67) * mm});
            skLineSegment(sketch, "E1919", {"start": v(84.76, -47.67) * mm, "end": v(84.46, -47.21) * mm});
            skLineSegment(sketch, "E1920", {"start": v(84.46, -47.21) * mm, "end": v(84.17, -46.76) * mm});
            skLineSegment(sketch, "E1921", {"start": v(84.17, -46.76) * mm, "end": v(83.88, -46.33) * mm});
            skLineSegment(sketch, "E1922", {"start": v(83.88, -46.33) * mm, "end": v(83.59, -45.91) * mm});
            skLineSegment(sketch, "E1923", {"start": v(83.59, -45.91) * mm, "end": v(83.3, -45.5) * mm});
            skLineSegment(sketch, "E1924", {"start": v(83.3, -45.5) * mm, "end": v(83, -45.11) * mm});
            skLineSegment(sketch, "E1925", {"start": v(83, -45.11) * mm, "end": v(82.73, -44.73) * mm});
            skLineSegment(sketch, "E1926", {"start": v(82.73, -44.73) * mm, "end": v(82.44, -44.37) * mm});
            skLineSegment(sketch, "E1927", {"start": v(82.44, -44.37) * mm, "end": v(82.17, -44.02) * mm});
            skLineSegment(sketch, "E1928", {"start": v(82.17, -44.02) * mm, "end": v(81.9, -43.67) * mm});
            skLineSegment(sketch, "E1929", {"start": v(81.9, -43.67) * mm, "end": v(81.62, -43.35) * mm});
            skLineSegment(sketch, "E1930", {"start": v(81.62, -43.35) * mm, "end": v(81.36, -43.03) * mm});
            skLineSegment(sketch, "E1931", {"start": v(81.36, -43.03) * mm, "end": v(81.1, -42.73) * mm});
            skLineSegment(sketch, "E1932", {"start": v(81.1, -42.73) * mm, "end": v(80.84, -42.44) * mm});
            skLineSegment(sketch, "E1933", {"start": v(80.84, -42.44) * mm, "end": v(80.59, -42.17) * mm});
            skLineSegment(sketch, "E1934", {"start": v(80.59, -42.17) * mm, "end": v(80.34, -41.9) * mm});
            skLineSegment(sketch, "E1935", {"start": v(80.34, -41.9) * mm, "end": v(80.1, -41.65) * mm});
            skLineSegment(sketch, "E1936", {"start": v(80.1, -41.65) * mm, "end": v(79.86, -41.4) * mm});
            skLineSegment(sketch, "E1937", {"start": v(79.86, -41.4) * mm, "end": v(79.63, -41.18) * mm});
            skLineSegment(sketch, "E1938", {"start": v(79.63, -41.18) * mm, "end": v(79.4, -40.96) * mm});
            skLineSegment(sketch, "E1939", {"start": v(79.4, -40.96) * mm, "end": v(79.19, -40.75) * mm});
            skLineSegment(sketch, "E1940", {"start": v(79.19, -40.75) * mm, "end": v(78.98, -40.56) * mm});
            skLineSegment(sketch, "E1941", {"start": v(78.98, -40.56) * mm, "end": v(78.77, -40.37) * mm});
            skLineSegment(sketch, "E1942", {"start": v(78.77, -40.37) * mm, "end": v(78.98, -39.9) * mm});
            skLineSegment(sketch, "E1943", {"start": v(78.98, -39.9) * mm, "end": v(80.3, -37.15) * mm});
            skLineSegment(sketch, "E1944", {"start": v(80.3, -37.15) * mm, "end": v(80.55, -36.7) * mm});
            skLineSegment(sketch, "E1945", {"start": v(80.55, -36.7) * mm, "end": v(80.82, -36.75) * mm});
            skLineSegment(sketch, "E1946", {"start": v(80.82, -36.75) * mm, "end": v(81.1, -36.8) * mm});
            skLineSegment(sketch, "E1947", {"start": v(81.1, -36.8) * mm, "end": v(81.4, -36.84) * mm});
            skLineSegment(sketch, "E1948", {"start": v(81.4, -36.84) * mm, "end": v(81.71, -36.88) * mm});
            skLineSegment(sketch, "E1949", {"start": v(81.71, -36.88) * mm, "end": v(82.03, -36.92) * mm});
            skLineSegment(sketch, "E1950", {"start": v(82.03, -36.92) * mm, "end": v(82.37, -36.95) * mm});
            skLineSegment(sketch, "E1951", {"start": v(82.37, -36.95) * mm, "end": v(82.72, -36.99) * mm});
            skLineSegment(sketch, "E1952", {"start": v(82.72, -36.99) * mm, "end": v(83.08, -37.01) * mm});
            skLineSegment(sketch, "E1953", {"start": v(83.08, -37.01) * mm, "end": v(83.45, -37.04) * mm});
            skLineSegment(sketch, "E1954", {"start": v(83.45, -37.04) * mm, "end": v(83.84, -37.06) * mm});
            skLineSegment(sketch, "E1955", {"start": v(83.84, -37.06) * mm, "end": v(84.24, -37.08) * mm});
            skLineSegment(sketch, "E1956", {"start": v(84.24, -37.08) * mm, "end": v(84.65, -37.1) * mm});
            skLineSegment(sketch, "E1957", {"start": v(84.65, -37.1) * mm, "end": v(85.07, -37.1) * mm});
            skLineSegment(sketch, "E1958", {"start": v(85.07, -37.1) * mm, "end": v(85.5, -37.1) * mm});
            skLineSegment(sketch, "E1959", {"start": v(85.5, -37.1) * mm, "end": v(85.96, -37.1) * mm});
            skLineSegment(sketch, "E1960", {"start": v(85.96, -37.1) * mm, "end": v(86.42, -37.1) * mm});
            skLineSegment(sketch, "E1961", {"start": v(86.42, -37.1) * mm, "end": v(86.9, -37.09) * mm});
            skLineSegment(sketch, "E1962", {"start": v(86.9, -37.09) * mm, "end": v(87.38, -37.07) * mm});
            skLineSegment(sketch, "E1963", {"start": v(87.38, -37.07) * mm, "end": v(87.88, -37.04) * mm});
            skLineSegment(sketch, "E1964", {"start": v(87.88, -37.04) * mm, "end": v(88.39, -37) * mm});
            skLineSegment(sketch, "E1965", {"start": v(88.39, -37) * mm, "end": v(88.9, -36.97) * mm});
            skLineSegment(sketch, "E1966", {"start": v(88.9, -36.97) * mm, "end": v(89.44, -36.92) * mm});
            skLineSegment(sketch, "E1967", {"start": v(89.44, -36.92) * mm, "end": v(89.99, -36.87) * mm});
            skLineSegment(sketch, "E1968", {"start": v(89.99, -36.87) * mm, "end": v(90.54, -36.8) * mm});
            skLineSegment(sketch, "E1969", {"start": v(90.54, -36.8) * mm, "end": v(91.11, -36.74) * mm});
            skLineSegment(sketch, "E1970", {"start": v(91.11, -36.74) * mm, "end": v(91.7, -36.66) * mm});
            skLineSegment(sketch, "E1971", {"start": v(91.7, -36.66) * mm, "end": v(92.28, -36.57) * mm});
            skLineSegment(sketch, "E1972", {"start": v(92.28, -36.57) * mm, "end": v(92.88, -36.47) * mm});
            skLineSegment(sketch, "E1973", {"start": v(92.88, -36.47) * mm, "end": v(93.5, -36.37) * mm});
            skLineSegment(sketch, "E1974", {"start": v(93.5, -36.37) * mm, "end": v(94.12, -36.25) * mm});
            skLineSegment(sketch, "E1975", {"start": v(94.12, -36.25) * mm, "end": v(94.76, -36.12) * mm});
            skLineSegment(sketch, "E1976", {"start": v(94.76, -36.12) * mm, "end": v(95.4, -35.99) * mm});
            skLineSegment(sketch, "E1977", {"start": v(95.4, -35.99) * mm, "end": v(96.06, -35.84) * mm});
            skLineSegment(sketch, "E1978", {"start": v(96.06, -35.84) * mm, "end": v(96.36, -35.55) * mm});
            skLineSegment(sketch, "E1979", {"start": v(96.36, -35.55) * mm, "end": v(97.11, -33.42) * mm});
            skLineSegment(sketch, "E1980", {"start": v(97.11, -33.42) * mm, "end": v(97.07, -33) * mm});
            skLineSegment(sketch, "E1981", {"start": v(97.07, -33) * mm, "end": v(96.65, -32.48) * mm});
            skLineSegment(sketch, "E1982", {"start": v(96.65, -32.48) * mm, "end": v(96.24, -31.97) * mm});
            skLineSegment(sketch, "E1983", {"start": v(96.24, -31.97) * mm, "end": v(95.83, -31.47) * mm});
            skLineSegment(sketch, "E1984", {"start": v(95.83, -31.47) * mm, "end": v(95.41, -30.98) * mm});
            skLineSegment(sketch, "E1985", {"start": v(95.41, -30.98) * mm, "end": v(95, -30.51) * mm});
            skLineSegment(sketch, "E1986", {"start": v(95, -30.51) * mm, "end": v(94.6, -30.06) * mm});
            skLineSegment(sketch, "E1987", {"start": v(94.6, -30.06) * mm, "end": v(94.2, -29.62) * mm});
            skLineSegment(sketch, "E1988", {"start": v(94.2, -29.62) * mm, "end": v(93.8, -29.19) * mm});
            skLineSegment(sketch, "E1989", {"start": v(93.8, -29.19) * mm, "end": v(93.4, -28.78) * mm});
            skLineSegment(sketch, "E1990", {"start": v(93.4, -28.78) * mm, "end": v(93.01, -28.37) * mm});
            skLineSegment(sketch, "E1991", {"start": v(93.01, -28.37) * mm, "end": v(92.63, -27.99) * mm});
            skLineSegment(sketch, "E1992", {"start": v(92.63, -27.99) * mm, "end": v(92.24, -27.61) * mm});
            skLineSegment(sketch, "E1993", {"start": v(92.24, -27.61) * mm, "end": v(91.86, -27.25) * mm});
            skLineSegment(sketch, "E1994", {"start": v(91.86, -27.25) * mm, "end": v(91.49, -26.9) * mm});
            skLineSegment(sketch, "E1995", {"start": v(91.49, -26.9) * mm, "end": v(91.12, -26.57) * mm});
            skLineSegment(sketch, "E1996", {"start": v(91.12, -26.57) * mm, "end": v(90.75, -26.25) * mm});
            skLineSegment(sketch, "E1997", {"start": v(90.75, -26.25) * mm, "end": v(90.4, -25.94) * mm});
            skLineSegment(sketch, "E1998", {"start": v(90.4, -25.94) * mm, "end": v(90.04, -25.64) * mm});
            skLineSegment(sketch, "E1999", {"start": v(90.04, -25.64) * mm, "end": v(89.7, -25.36) * mm});
            skLineSegment(sketch, "E2000", {"start": v(89.7, -25.36) * mm, "end": v(89.36, -25.09) * mm});
            skLineSegment(sketch, "E2001", {"start": v(89.36, -25.09) * mm, "end": v(89.02, -24.82) * mm});
            skLineSegment(sketch, "E2002", {"start": v(89.02, -24.82) * mm, "end": v(88.7, -24.58) * mm});
            skLineSegment(sketch, "E2003", {"start": v(88.7, -24.58) * mm, "end": v(88.37, -24.34) * mm});
            skLineSegment(sketch, "E2004", {"start": v(88.37, -24.34) * mm, "end": v(88.06, -24.1) * mm});
            skLineSegment(sketch, "E2005", {"start": v(88.06, -24.1) * mm, "end": v(87.75, -23.9) * mm});
            skLineSegment(sketch, "E2006", {"start": v(87.75, -23.9) * mm, "end": v(87.46, -23.69) * mm});
            skLineSegment(sketch, "E2007", {"start": v(87.46, -23.69) * mm, "end": v(87.17, -23.5) * mm});
            skLineSegment(sketch, "E2008", {"start": v(87.17, -23.5) * mm, "end": v(86.88, -23.3) * mm});
            skLineSegment(sketch, "E2009", {"start": v(86.88, -23.3) * mm, "end": v(86.6, -23.13) * mm});
            skLineSegment(sketch, "E2010", {"start": v(86.6, -23.13) * mm, "end": v(86.34, -22.97) * mm});
            skLineSegment(sketch, "E2011", {"start": v(86.34, -22.97) * mm, "end": v(86.09, -22.81) * mm});
            skLineSegment(sketch, "E2012", {"start": v(86.09, -22.81) * mm, "end": v(85.84, -22.67) * mm});
            skLineSegment(sketch, "E2013", {"start": v(85.84, -22.67) * mm, "end": v(85.6, -22.53) * mm});
            skLineSegment(sketch, "E2014", {"start": v(85.6, -22.53) * mm, "end": v(85.7, -22.03) * mm});
            skLineSegment(sketch, "E2015", {"start": v(85.7, -22.03) * mm, "end": v(86.4, -19.06) * mm});
            skLineSegment(sketch, "E2016", {"start": v(86.4, -19.06) * mm, "end": v(86.54, -18.57) * mm});
            skLineSegment(sketch, "E2017", {"start": v(86.54, -18.57) * mm, "end": v(86.82, -18.56) * mm});
            skLineSegment(sketch, "E2018", {"start": v(86.82, -18.56) * mm, "end": v(87.1, -18.54) * mm});
            skLineSegment(sketch, "E2019", {"start": v(87.1, -18.54) * mm, "end": v(87.4, -18.52) * mm});
            skLineSegment(sketch, "E2020", {"start": v(87.4, -18.52) * mm, "end": v(87.72, -18.49) * mm});
            skLineSegment(sketch, "E2021", {"start": v(87.72, -18.49) * mm, "end": v(88.04, -18.46) * mm});
            skLineSegment(sketch, "E2022", {"start": v(88.04, -18.46) * mm, "end": v(88.38, -18.42) * mm});
            skLineSegment(sketch, "E2023", {"start": v(88.38, -18.42) * mm, "end": v(88.72, -18.38) * mm});
            skLineSegment(sketch, "E2024", {"start": v(88.72, -18.38) * mm, "end": v(89.08, -18.33) * mm});
            skLineSegment(sketch, "E2025", {"start": v(89.08, -18.33) * mm, "end": v(89.45, -18.27) * mm});
            skLineSegment(sketch, "E2026", {"start": v(89.45, -18.27) * mm, "end": v(89.83, -18.2) * mm});
            skLineSegment(sketch, "E2027", {"start": v(89.83, -18.2) * mm, "end": v(90.23, -18.14) * mm});
            skLineSegment(sketch, "E2028", {"start": v(90.23, -18.14) * mm, "end": v(90.63, -18.07) * mm});
            skLineSegment(sketch, "E2029", {"start": v(90.63, -18.07) * mm, "end": v(91.05, -17.98) * mm});
            skLineSegment(sketch, "E2030", {"start": v(91.05, -17.98) * mm, "end": v(91.47, -17.9) * mm});
            skLineSegment(sketch, "E2031", {"start": v(91.47, -17.9) * mm, "end": v(91.91, -17.8) * mm});
            skLineSegment(sketch, "E2032", {"start": v(91.91, -17.8) * mm, "end": v(92.36, -17.7) * mm});
            skLineSegment(sketch, "E2033", {"start": v(92.36, -17.7) * mm, "end": v(92.82, -17.58) * mm});
            skLineSegment(sketch, "E2034", {"start": v(92.82, -17.58) * mm, "end": v(93.3, -17.45) * mm});
            skLineSegment(sketch, "E2035", {"start": v(93.3, -17.45) * mm, "end": v(93.77, -17.32) * mm});
            skLineSegment(sketch, "E2036", {"start": v(93.77, -17.32) * mm, "end": v(94.26, -17.18) * mm});
            skLineSegment(sketch, "E2037", {"start": v(94.26, -17.18) * mm, "end": v(94.76, -17.03) * mm});
            skLineSegment(sketch, "E2038", {"start": v(94.76, -17.03) * mm, "end": v(95.28, -16.87) * mm});
            skLineSegment(sketch, "E2039", {"start": v(95.28, -16.87) * mm, "end": v(95.8, -16.7) * mm});
            skLineSegment(sketch, "E2040", {"start": v(95.8, -16.7) * mm, "end": v(96.33, -16.52) * mm});
            skLineSegment(sketch, "E2041", {"start": v(96.33, -16.52) * mm, "end": v(96.87, -16.33) * mm});
            skLineSegment(sketch, "E2042", {"start": v(96.87, -16.33) * mm, "end": v(97.42, -16.13) * mm});
            skLineSegment(sketch, "E2043", {"start": v(97.42, -16.13) * mm, "end": v(97.97, -15.91) * mm});
            skLineSegment(sketch, "E2044", {"start": v(97.97, -15.91) * mm, "end": v(98.54, -15.69) * mm});
            skLineSegment(sketch, "E2045", {"start": v(98.54, -15.69) * mm, "end": v(99.12, -15.45) * mm});
            skLineSegment(sketch, "E2046", {"start": v(99.12, -15.45) * mm, "end": v(99.7, -15.2) * mm});
            skLineSegment(sketch, "E2047", {"start": v(99.7, -15.2) * mm, "end": v(100.3, -14.95) * mm});
            skLineSegment(sketch, "E2048", {"start": v(100.3, -14.95) * mm, "end": v(100.9, -14.68) * mm});
            skLineSegment(sketch, "E2049", {"start": v(100.9, -14.68) * mm, "end": v(101.5, -14.4) * mm});
            skLineSegment(sketch, "E2050", {"start": v(101.5, -14.4) * mm, "end": v(101.73, -14.04) * mm});
            skLineSegment(sketch, "E2051", {"start": v(101.73, -14.04) * mm, "end": v(102.02, -11.8) * mm});
            skLineSegment(sketch, "E2052", {"start": v(102.02, -11.8) * mm, "end": v(101.88, -11.4) * mm});
            skLineSegment(sketch, "E2053", {"start": v(101.88, -11.4) * mm, "end": v(101.36, -10.98) * mm});
            skLineSegment(sketch, "E2054", {"start": v(101.36, -10.98) * mm, "end": v(100.85, -10.57) * mm});
            skLineSegment(sketch, "E2055", {"start": v(100.85, -10.57) * mm, "end": v(100.34, -10.17) * mm});
            skLineSegment(sketch, "E2056", {"start": v(100.34, -10.17) * mm, "end": v(99.83, -9.78) * mm});
            skLineSegment(sketch, "E2057", {"start": v(99.83, -9.78) * mm, "end": v(99.33, -9.41) * mm});
            skLineSegment(sketch, "E2058", {"start": v(99.33, -9.41) * mm, "end": v(98.84, -9.06) * mm});
            skLineSegment(sketch, "E2059", {"start": v(98.84, -9.06) * mm, "end": v(98.35, -8.71) * mm});
            skLineSegment(sketch, "E2060", {"start": v(98.35, -8.71) * mm, "end": v(97.87, -8.38) * mm});
            skLineSegment(sketch, "E2061", {"start": v(97.87, -8.38) * mm, "end": v(97.4, -8.06) * mm});
            skLineSegment(sketch, "E2062", {"start": v(97.4, -8.06) * mm, "end": v(96.93, -7.75) * mm});
            skLineSegment(sketch, "E2063", {"start": v(96.93, -7.75) * mm, "end": v(96.46, -7.46) * mm});
            skLineSegment(sketch, "E2064", {"start": v(96.46, -7.46) * mm, "end": v(96, -7.18) * mm});
            skLineSegment(sketch, "E2065", {"start": v(96, -7.18) * mm, "end": v(95.56, -6.9) * mm});
            skLineSegment(sketch, "E2066", {"start": v(95.56, -6.9) * mm, "end": v(95.12, -6.65) * mm});
            skLineSegment(sketch, "E2067", {"start": v(95.12, -6.65) * mm, "end": v(94.69, -6.4) * mm});
            skLineSegment(sketch, "E2068", {"start": v(94.69, -6.4) * mm, "end": v(94.26, -6.16) * mm});
            skLineSegment(sketch, "E2069", {"start": v(94.26, -6.16) * mm, "end": v(93.85, -5.94) * mm});
            skLineSegment(sketch, "E2070", {"start": v(93.85, -5.94) * mm, "end": v(93.44, -5.72) * mm});
            skLineSegment(sketch, "E2071", {"start": v(93.44, -5.72) * mm, "end": v(93.04, -5.52) * mm});
            skLineSegment(sketch, "E2072", {"start": v(93.04, -5.52) * mm, "end": v(92.65, -5.33) * mm});
            skLineSegment(sketch, "E2073", {"start": v(92.65, -5.33) * mm, "end": v(92.26, -5.14) * mm});
            skLineSegment(sketch, "E2074", {"start": v(92.26, -5.14) * mm, "end": v(91.9, -4.97) * mm});
            skLineSegment(sketch, "E2075", {"start": v(91.9, -4.97) * mm, "end": v(91.53, -4.8) * mm});
            skLineSegment(sketch, "E2076", {"start": v(91.53, -4.8) * mm, "end": v(91.17, -4.65) * mm});
            skLineSegment(sketch, "E2077", {"start": v(91.17, -4.65) * mm, "end": v(90.83, -4.5) * mm});
            skLineSegment(sketch, "E2078", {"start": v(90.83, -4.5) * mm, "end": v(90.5, -4.37) * mm});
            skLineSegment(sketch, "E2079", {"start": v(90.5, -4.37) * mm, "end": v(90.17, -4.24) * mm});
            skLineSegment(sketch, "E2080", {"start": v(90.17, -4.24) * mm, "end": v(89.85, -4.12) * mm});
            skLineSegment(sketch, "E2081", {"start": v(89.85, -4.12) * mm, "end": v(89.55, -4.01) * mm});
            skLineSegment(sketch, "E2082", {"start": v(89.55, -4.01) * mm, "end": v(89.25, -3.9) * mm});
            skLineSegment(sketch, "E2083", {"start": v(89.25, -3.9) * mm, "end": v(88.97, -3.81) * mm});
            skLineSegment(sketch, "E2084", {"start": v(88.97, -3.81) * mm, "end": v(88.7, -3.72) * mm});
            skLineSegment(sketch, "E2085", {"start": v(88.7, -3.72) * mm, "end": v(88.43, -3.64) * mm});
            skLineSegment(sketch, "E2086", {"start": v(88.43, -3.64) * mm, "end": v(88.42, -3.13) * mm});
            skLineSegment(sketch, "E2087", {"start": v(88.42, -3.13) * mm, "end": v(88.47, -0.08) * mm});
            skLineSegment(sketch, "E2088", {"start": v(2.8, -0.08) * mm, "end": v(-2.48, -0.08) * mm});
            skLineSegment(sketch, "E2089", {"start": v(0.16, -2.72) * mm, "end": v(0.16, 2.57) * mm});
            skLineSegment(sketch, "E2090", {"start": v(98.27, 8.64) * mm, "end": v(98.27, 8.4) * mm});
            skLineSegment(sketch, "E2091", {"start": v(98.27, 8.4) * mm, "end": v(98.07, 7.63) * mm});
            skLineSegment(sketch, "E2092", {"start": v(98.07, 7.63) * mm, "end": v(97.51, 6.8) * mm});
            skLineSegment(sketch, "E2093", {"start": v(97.51, 6.8) * mm, "end": v(96.69, 6.25) * mm});
            skLineSegment(sketch, "E2094", {"start": v(96.69, 6.25) * mm, "end": v(95.93, 6.05) * mm});
            skLineSegment(sketch, "E2095", {"start": v(95.93, 6.05) * mm, "end": v(95.68, 6.05) * mm});
            skLineSegment(sketch, "E2096", {"start": v(95.68, 6.05) * mm, "end": v(95.42, 6.05) * mm});
            skLineSegment(sketch, "E2097", {"start": v(95.42, 6.05) * mm, "end": v(94.67, 6.25) * mm});
            skLineSegment(sketch, "E2098", {"start": v(94.67, 6.25) * mm, "end": v(93.84, 6.8) * mm});
            skLineSegment(sketch, "E2099", {"start": v(93.84, 6.8) * mm, "end": v(93.28, 7.63) * mm});
            skLineSegment(sketch, "E2100", {"start": v(93.28, 7.63) * mm, "end": v(93.08, 8.4) * mm});
            skLineSegment(sketch, "E2101", {"start": v(93.08, 8.4) * mm, "end": v(93.08, 8.64) * mm});
            skLineSegment(sketch, "E2102", {"start": v(93.08, 8.64) * mm, "end": v(93.08, 8.9) * mm});
            skLineSegment(sketch, "E2103", {"start": v(93.08, 8.9) * mm, "end": v(93.28, 9.65) * mm});
            skLineSegment(sketch, "E2104", {"start": v(93.28, 9.65) * mm, "end": v(93.84, 10.48) * mm});
            skLineSegment(sketch, "E2105", {"start": v(93.84, 10.48) * mm, "end": v(94.67, 11.03) * mm});
            skLineSegment(sketch, "E2106", {"start": v(94.67, 11.03) * mm, "end": v(95.42, 11.24) * mm});
            skLineSegment(sketch, "E2107", {"start": v(95.42, 11.24) * mm, "end": v(95.68, 11.24) * mm});
            skLineSegment(sketch, "E2108", {"start": v(95.68, 11.24) * mm, "end": v(95.93, 11.24) * mm});
            skLineSegment(sketch, "E2109", {"start": v(95.93, 11.24) * mm, "end": v(96.69, 11.03) * mm});
            skLineSegment(sketch, "E2110", {"start": v(96.69, 11.03) * mm, "end": v(97.51, 10.48) * mm});
            skLineSegment(sketch, "E2111", {"start": v(97.51, 10.48) * mm, "end": v(98.07, 9.65) * mm});
            skLineSegment(sketch, "E2112", {"start": v(98.07, 9.65) * mm, "end": v(98.27, 8.9) * mm});
            skLineSegment(sketch, "E2113", {"start": v(98.27, 8.9) * mm, "end": v(98.27, 8.64) * mm});
            skLineSegment(sketch, "E2114", {"start": v(57.56, 56.18) * mm, "end": v(57, 56.74) * mm});
            skLineSegment(sketch, "E2115", {"start": v(57, 56.74) * mm, "end": v(56.44, 57.3) * mm});
            skLineSegment(sketch, "E2116", {"start": v(56.44, 57.3) * mm, "end": v(55.87, 57.85) * mm});
            skLineSegment(sketch, "E2117", {"start": v(55.87, 57.85) * mm, "end": v(55.3, 58.4) * mm});
            skLineSegment(sketch, "E2118", {"start": v(55.33, 56.17) * mm, "end": v(57.55, 58.43) * mm});
            skLineSegment(sketch, "E2119", {"start": v(58.7, 57.29) * mm, "end": v(57.56, 57.3) * mm});
            skLineSegment(sketch, "E2120", {"start": v(57.56, 57.3) * mm, "end": v(56.44, 57.3) * mm});
            skLineSegment(sketch, "E2121", {"start": v(56.44, 57.3) * mm, "end": v(55.32, 57.28) * mm});
            skLineSegment(sketch, "E2122", {"start": v(55.32, 57.28) * mm, "end": v(54.2, 57.24) * mm});
            skLineSegment(sketch, "E2123", {"start": v(56.43, 55.07) * mm, "end": v(56.44, 56.18) * mm});
            skLineSegment(sketch, "E2124", {"start": v(56.44, 56.18) * mm, "end": v(56.44, 57.3) * mm});
            skLineSegment(sketch, "E2125", {"start": v(56.44, 57.3) * mm, "end": v(56.42, 58.42) * mm});
            skLineSegment(sketch, "E2126", {"start": v(56.42, 58.42) * mm, "end": v(56.38, 59.55) * mm});
            skLineSegment(sketch, "E2127", {"start": v(59.08, 52.22) * mm, "end": v(57.97, 52.27) * mm});
            skLineSegment(sketch, "E2128", {"start": v(57.97, 52.27) * mm, "end": v(57.45, 52.83) * mm});
            skLineSegment(sketch, "E2129", {"start": v(57.45, 52.83) * mm, "end": v(57.5, 53.94) * mm});
            skLineSegment(sketch, "E2130", {"start": v(57.5, 53.94) * mm, "end": v(59.82, 56.12) * mm});
            skLineSegment(sketch, "E2131", {"start": v(59.82, 56.12) * mm, "end": v(60.95, 56.07) * mm});
            skLineSegment(sketch, "E2132", {"start": v(60.95, 56.07) * mm, "end": v(61.5, 55.46) * mm});
            skLineSegment(sketch, "E2133", {"start": v(61.5, 55.46) * mm, "end": v(61.46, 54.33) * mm});
            skLineSegment(sketch, "E2134", {"start": v(61.46, 54.33) * mm, "end": v(59.08, 52.22) * mm});
            skLineSegment(sketch, "E2135", {"start": v(67.64, 47.82) * mm, "end": v(63.76, 45.06) * mm});
            skLineSegment(sketch, "E2136", {"start": v(63.76, 45.06) * mm, "end": v(64.27, 46.39) * mm});
            skLineSegment(sketch, "E2137", {"start": v(64.27, 46.39) * mm, "end": v(64.77, 47.73) * mm});
            skLineSegment(sketch, "E2138", {"start": v(64.77, 47.73) * mm, "end": v(65.24, 49.08) * mm});
            skLineSegment(sketch, "E2139", {"start": v(65.24, 49.08) * mm, "end": v(65.7, 50.45) * mm});
            skLineSegment(sketch, "E2140", {"start": v(65.7, 50.45) * mm, "end": v(61.93, 47.54) * mm});
            skLineSegment(sketch, "E2141", {"start": v(69.01, 42.9) * mm, "end": v(68.58, 43.58) * mm});
            skLineSegment(sketch, "E2142", {"start": v(68.58, 43.58) * mm, "end": v(68.15, 44.25) * mm});
            skLineSegment(sketch, "E2143", {"start": v(68.15, 44.25) * mm, "end": v(67.7, 44.92) * mm});
            skLineSegment(sketch, "E2144", {"start": v(67.7, 44.92) * mm, "end": v(67.26, 45.59) * mm});
            skLineSegment(sketch, "E2145", {"start": v(67.67, 42.06) * mm, "end": v(67.25, 42.72) * mm});
            skLineSegment(sketch, "E2146", {"start": v(67.25, 42.72) * mm, "end": v(66.82, 43.38) * mm});
            skLineSegment(sketch, "E2147", {"start": v(66.82, 43.38) * mm, "end": v(66.39, 44.04) * mm});
            skLineSegment(sketch, "E2148", {"start": v(66.39, 44.04) * mm, "end": v(65.95, 44.7) * mm});
            skLineSegment(sketch, "E2149", {"start": v(68.65, 37.23) * mm, "end": v(68.28, 37.9) * mm});
            skLineSegment(sketch, "E2150", {"start": v(68.28, 37.9) * mm, "end": v(67.9, 38.57) * mm});
            skLineSegment(sketch, "E2151", {"start": v(67.9, 38.57) * mm, "end": v(67.51, 39.24) * mm});
            skLineSegment(sketch, "E2152", {"start": v(67.51, 39.24) * mm, "end": v(67.12, 39.9) * mm});
            skLineSegment(sketch, "E2153", {"start": v(67.12, 39.9) * mm, "end": v(68.48, 40.72) * mm});
            skLineSegment(sketch, "E2154", {"start": v(68.48, 40.72) * mm, "end": v(69.57, 40.44) * mm});
            skLineSegment(sketch, "E2155", {"start": v(69.57, 40.44) * mm, "end": v(69.96, 39.75) * mm});
            skLineSegment(sketch, "E2156", {"start": v(69.96, 39.75) * mm, "end": v(70.36, 39.06) * mm});
            skLineSegment(sketch, "E2157", {"start": v(70.36, 39.06) * mm, "end": v(71.44, 38.75) * mm});
            skLineSegment(sketch, "E2158", {"start": v(71.44, 38.75) * mm, "end": v(72.13, 39.13) * mm});
            skLineSegment(sketch, "E2159", {"start": v(72.13, 39.13) * mm, "end": v(72.44, 40.22) * mm});
            skLineSegment(sketch, "E2160", {"start": v(72.44, 40.22) * mm, "end": v(72.03, 40.93) * mm});
            skLineSegment(sketch, "E2161", {"start": v(72.03, 40.93) * mm, "end": v(71.63, 41.64) * mm});
            skLineSegment(sketch, "E2162", {"start": v(71.63, 41.64) * mm, "end": v(70.53, 41.94) * mm});
            skLineSegment(sketch, "E2163", {"start": v(72.9, 34.12) * mm, "end": v(72.55, 34.84) * mm});
            skLineSegment(sketch, "E2164", {"start": v(72.55, 34.84) * mm, "end": v(72.2, 35.55) * mm});
            skLineSegment(sketch, "E2165", {"start": v(72.2, 35.55) * mm, "end": v(71.85, 36.26) * mm});
            skLineSegment(sketch, "E2166", {"start": v(71.85, 36.26) * mm, "end": v(72.2, 37.33) * mm});
            skLineSegment(sketch, "E2167", {"start": v(72.2, 37.33) * mm, "end": v(72.9, 37.7) * mm});
            skLineSegment(sketch, "E2168", {"start": v(72.9, 37.7) * mm, "end": v(73.97, 37.34) * mm});
            skLineSegment(sketch, "E2169", {"start": v(73.97, 37.34) * mm, "end": v(74.34, 36.6) * mm});
            skLineSegment(sketch, "E2170", {"start": v(74.34, 36.6) * mm, "end": v(74.7, 35.87) * mm});
            skLineSegment(sketch, "E2171", {"start": v(74.7, 35.87) * mm, "end": v(74.33, 34.8) * mm});
            skLineSegment(sketch, "E2172", {"start": v(74.33, 34.8) * mm, "end": v(72.18, 33.78) * mm});
            skLineSegment(sketch, "E2173", {"start": v(72.18, 33.78) * mm, "end": v(71.12, 34.15) * mm});
            skLineSegment(sketch, "E2174", {"start": v(71.12, 34.15) * mm, "end": v(70.07, 34.5) * mm});
            skLineSegment(sketch, "E2175", {"start": v(70.07, 34.5) * mm, "end": v(69.73, 35.18) * mm});
            skLineSegment(sketch, "E2176", {"start": v(75.08, 29.01) * mm, "end": v(75.37, 28.27) * mm});
            skLineSegment(sketch, "E2177", {"start": v(75.37, 28.27) * mm, "end": v(75.64, 27.53) * mm});
            skLineSegment(sketch, "E2178", {"start": v(75.64, 27.53) * mm, "end": v(75.91, 26.78) * mm});
            skLineSegment(sketch, "E2179", {"start": v(75.91, 26.78) * mm, "end": v(76.92, 26.29) * mm});
            skLineSegment(sketch, "E2180", {"start": v(76.92, 26.29) * mm, "end": v(77.67, 26.55) * mm});
            skLineSegment(sketch, "E2181", {"start": v(77.67, 26.55) * mm, "end": v(78.15, 27.58) * mm});
            skLineSegment(sketch, "E2182", {"start": v(78.15, 27.58) * mm, "end": v(77.88, 28.35) * mm});
            skLineSegment(sketch, "E2183", {"start": v(77.88, 28.35) * mm, "end": v(77.6, 29.11) * mm});
            skLineSegment(sketch, "E2184", {"start": v(77.6, 29.11) * mm, "end": v(77.3, 29.87) * mm});
            skLineSegment(sketch, "E2185", {"start": v(77.3, 29.87) * mm, "end": v(72.86, 28.15) * mm});
            skLineSegment(sketch, "E2186", {"start": v(74.4, 23.8) * mm, "end": v(77.43, 24.77) * mm});
            skLineSegment(sketch, "E2187", {"start": v(78.18, 25.01) * mm, "end": v(78.94, 25.25) * mm});
            skLineSegment(sketch, "E2188", {"start": v(76.46, 19.56) * mm, "end": v(75.5, 20.1) * mm});
            skLineSegment(sketch, "E2189", {"start": v(75.5, 20.1) * mm, "end": v(76.05, 21.06) * mm});
            skLineSegment(sketch, "E2190", {"start": v(76.05, 21.06) * mm, "end": v(79.88, 22.12) * mm});
            skLineSegment(sketch, "E2191", {"start": v(78.76, 20.15) * mm, "end": v(78.56, 20.92) * mm});
            skLineSegment(sketch, "E2192", {"start": v(78.56, 20.92) * mm, "end": v(78.35, 21.7) * mm});
            skLineSegment(sketch, "E2193", {"start": v(78.35, 21.7) * mm, "end": v(78.13, 22.47) * mm});
            skLineSegment(sketch, "E2194", {"start": v(78.13, 22.47) * mm, "end": v(77.9, 23.24) * mm});
            skLineSegment(sketch, "E2195", {"start": v(76.7, 14.85) * mm, "end": v(76.56, 15.6) * mm});
            skLineSegment(sketch, "E2196", {"start": v(76.56, 15.6) * mm, "end": v(76.4, 16.36) * mm});
            skLineSegment(sketch, "E2197", {"start": v(76.4, 16.36) * mm, "end": v(76.23, 17.11) * mm});
            skLineSegment(sketch, "E2198", {"start": v(76.23, 17.11) * mm, "end": v(76.83, 18.04) * mm});
            skLineSegment(sketch, "E2199", {"start": v(76.83, 18.04) * mm, "end": v(78.38, 18.4) * mm});
            skLineSegment(sketch, "E2200", {"start": v(78.38, 18.4) * mm, "end": v(79.33, 17.81) * mm});
            skLineSegment(sketch, "E2201", {"start": v(79.33, 17.81) * mm, "end": v(79.5, 17.03) * mm});
            skLineSegment(sketch, "E2202", {"start": v(79.5, 17.03) * mm, "end": v(79.66, 16.24) * mm});
            skLineSegment(sketch, "E2203", {"start": v(79.66, 16.24) * mm, "end": v(79.82, 15.46) * mm});
            skLineSegment(sketch, "E2204", {"start": v(78.55, 13.6) * mm, "end": v(79.47, 12.96) * mm});
            skLineSegment(sketch, "E2205", {"start": v(79.47, 12.96) * mm, "end": v(80.37, 12.3) * mm});
            skLineSegment(sketch, "E2206", {"start": v(80.37, 12.3) * mm, "end": v(80.5, 11.5) * mm});
            skLineSegment(sketch, "E2207", {"start": v(80.5, 11.5) * mm, "end": v(79.82, 10.6) * mm});
            skLineSegment(sketch, "E2208", {"start": v(79.82, 10.6) * mm, "end": v(77.46, 10.3) * mm});
            skLineSegment(sketch, "E2209", {"start": v(76.99, 13.33) * mm, "end": v(81.68, 14.16) * mm});
            skLineSegment(sketch, "E2210", {"start": v(77.99, 4.93) * mm, "end": v(78.03, 4.16) * mm});
            skLineSegment(sketch, "E2211", {"start": v(78.03, 4.16) * mm, "end": v(78.07, 3.39) * mm});
            skLineSegment(sketch, "E2212", {"start": v(78.07, 3.39) * mm, "end": v(78.1, 2.62) * mm});
            skLineSegment(sketch, "E2213", {"start": v(78.1, 2.62) * mm, "end": v(78.92, 1.87) * mm});
            skLineSegment(sketch, "E2214", {"start": v(78.92, 1.87) * mm, "end": v(82.1, 1.95) * mm});
            skLineSegment(sketch, "E2215", {"start": v(82.1, 1.95) * mm, "end": v(82.86, 2.78) * mm});
            skLineSegment(sketch, "E2216", {"start": v(82.86, 2.78) * mm, "end": v(82.83, 3.6) * mm});
            skLineSegment(sketch, "E2217", {"start": v(82.83, 3.6) * mm, "end": v(82.8, 4.42) * mm});
            skLineSegment(sketch, "E2218", {"start": v(82.8, 4.42) * mm, "end": v(82.74, 5.23) * mm});
            skLineSegment(sketch, "E2219", {"start": v(82.8, 4.42) * mm, "end": v(78.03, 4.16) * mm});
            skLineSegment(sketch, "E2220", {"start": v(81.28, -2.88) * mm, "end": v(81.3, -2.08) * mm});
            skLineSegment(sketch, "E2221", {"start": v(81.3, -2.08) * mm, "end": v(81.32, -1.28) * mm});
            skLineSegment(sketch, "E2222", {"start": v(81.32, -1.28) * mm, "end": v(81.32, -0.48) * mm});
            skLineSegment(sketch, "E2223", {"start": v(81.32, -0.48) * mm, "end": v(81.32, 0.32) * mm});
            skLineSegment(sketch, "E2224", {"start": v(79.69, -2.83) * mm, "end": v(79.71, -2.04) * mm});
            skLineSegment(sketch, "E2225", {"start": v(79.71, -2.04) * mm, "end": v(79.73, -1.26) * mm});
            skLineSegment(sketch, "E2226", {"start": v(79.73, -1.26) * mm, "end": v(79.74, -0.47) * mm});
            skLineSegment(sketch, "E2227", {"start": v(79.74, -0.47) * mm, "end": v(79.74, 0.32) * mm});
            skLineSegment(sketch, "E2228", {"start": v(82.8, -4.57) * mm, "end": v(82.74, -5.38) * mm});
            skLineSegment(sketch, "E2229", {"start": v(82.74, -5.38) * mm, "end": v(82.68, -6.2) * mm});
            skLineSegment(sketch, "E2230", {"start": v(82.68, -6.2) * mm, "end": v(82.62, -7.01) * mm});
            skLineSegment(sketch, "E2231", {"start": v(82.62, -7.01) * mm, "end": v(82.55, -7.83) * mm});
            skLineSegment(sketch, "E2232", {"start": v(82.55, -7.83) * mm, "end": v(80.25, -6.82) * mm});
            skLineSegment(sketch, "E2233", {"start": v(80.25, -6.82) * mm, "end": v(77.93, -5.85) * mm});
            skLineSegment(sketch, "E2234", {"start": v(78.43, -9) * mm, "end": v(77.65, -8.92) * mm});
            skLineSegment(sketch, "E2235", {"start": v(76.99, -13.49) * mm, "end": v(77.11, -12.73) * mm});
            skLineSegment(sketch, "E2236", {"start": v(77.11, -12.73) * mm, "end": v(77.24, -11.97) * mm});
            skLineSegment(sketch, "E2237", {"start": v(77.24, -11.97) * mm, "end": v(77.35, -11.2) * mm});
            skLineSegment(sketch, "E2238", {"start": v(77.35, -11.2) * mm, "end": v(77.46, -10.44) * mm});
            skLineSegment(sketch, "E2239", {"start": v(77.46, -10.44) * mm, "end": v(79.03, -10.65) * mm});
            skLineSegment(sketch, "E2240", {"start": v(79.03, -10.65) * mm, "end": v(79.7, -11.55) * mm});
            skLineSegment(sketch, "E2241", {"start": v(79.7, -11.55) * mm, "end": v(79.6, -12.33) * mm});
            skLineSegment(sketch, "E2242", {"start": v(79.6, -12.33) * mm, "end": v(79.47, -13.12) * mm});
            skLineSegment(sketch, "E2243", {"start": v(79.47, -13.12) * mm, "end": v(80.12, -14.03) * mm});
            skLineSegment(sketch, "E2244", {"start": v(80.12, -14.03) * mm, "end": v(80.9, -14.17) * mm});
            skLineSegment(sketch, "E2245", {"start": v(80.9, -14.17) * mm, "end": v(81.82, -13.5) * mm});
            skLineSegment(sketch, "E2246", {"start": v(81.82, -13.5) * mm, "end": v(81.94, -12.7) * mm});
            skLineSegment(sketch, "E2247", {"start": v(81.94, -12.7) * mm, "end": v(82.07, -11.89) * mm});
            skLineSegment(sketch, "E2248", {"start": v(82.07, -11.89) * mm, "end": v(81.4, -10.97) * mm});
            skLineSegment(sketch, "E2249", {"start": v(80.7, -19.1) * mm, "end": v(80.88, -18.31) * mm});
            skLineSegment(sketch, "E2250", {"start": v(80.88, -18.31) * mm, "end": v(81.05, -17.52) * mm});
            skLineSegment(sketch, "E2251", {"start": v(81.05, -17.52) * mm, "end": v(81.22, -16.72) * mm});
            skLineSegment(sketch, "E2252", {"start": v(81.22, -16.72) * mm, "end": v(81.38, -15.91) * mm});
            skLineSegment(sketch, "E2253", {"start": v(81.38, -15.91) * mm, "end": v(79.82, -15.6) * mm});
            skLineSegment(sketch, "E2254", {"start": v(79.82, -15.6) * mm, "end": v(79.66, -16.4) * mm});
            skLineSegment(sketch, "E2255", {"start": v(79.66, -16.4) * mm, "end": v(79.5, -17.18) * mm});
            skLineSegment(sketch, "E2256", {"start": v(79.5, -17.18) * mm, "end": v(79.33, -17.96) * mm});
            skLineSegment(sketch, "E2257", {"start": v(79.33, -17.96) * mm, "end": v(78.38, -18.56) * mm});
            skLineSegment(sketch, "E2258", {"start": v(78.38, -18.56) * mm, "end": v(76.83, -18.2) * mm});
            skLineSegment(sketch, "E2259", {"start": v(76.83, -18.2) * mm, "end": v(76.23, -17.26) * mm});
            skLineSegment(sketch, "E2260", {"start": v(76.23, -17.26) * mm, "end": v(76.4, -16.51) * mm});
            skLineSegment(sketch, "E2261", {"start": v(76.4, -16.51) * mm, "end": v(76.56, -15.76) * mm});
            skLineSegment(sketch, "E2262", {"start": v(76.56, -15.76) * mm, "end": v(77.49, -15.15) * mm});
            skLineSegment(sketch, "E2263", {"start": v(76.91, -23.92) * mm, "end": v(76.67, -24.68) * mm});
            skLineSegment(sketch, "E2264", {"start": v(76.67, -24.68) * mm, "end": v(76.43, -25.43) * mm});
            skLineSegment(sketch, "E2265", {"start": v(76.43, -25.43) * mm, "end": v(76.17, -26.19) * mm});
            skLineSegment(sketch, "E2266", {"start": v(76.17, -26.19) * mm, "end": v(76.66, -27.2) * mm});
            skLineSegment(sketch, "E2267", {"start": v(76.66, -27.2) * mm, "end": v(77.4, -27.46) * mm});
            skLineSegment(sketch, "E2268", {"start": v(77.4, -27.46) * mm, "end": v(78.42, -26.96) * mm});
            skLineSegment(sketch, "E2269", {"start": v(78.42, -26.96) * mm, "end": v(78.69, -26.18) * mm});
            skLineSegment(sketch, "E2270", {"start": v(78.69, -26.18) * mm, "end": v(78.94, -25.4) * mm});
            skLineSegment(sketch, "E2271", {"start": v(78.94, -25.4) * mm, "end": v(79.19, -24.63) * mm});
            skLineSegment(sketch, "E2272", {"start": v(79.19, -24.63) * mm, "end": v(74.64, -23.21) * mm});
            skLineSegment(sketch, "E2273", {"start": v(74.92, -31.68) * mm, "end": v(75.22, -30.94) * mm});
            skLineSegment(sketch, "E2274", {"start": v(75.22, -30.94) * mm, "end": v(75.53, -30.2) * mm});
            skLineSegment(sketch, "E2275", {"start": v(75.53, -30.2) * mm, "end": v(75.82, -29.45) * mm});
            skLineSegment(sketch, "E2276", {"start": v(75.82, -29.45) * mm, "end": v(76.1, -28.7) * mm});
            skLineSegment(sketch, "E2277", {"start": v(73.46, -31.06) * mm, "end": v(73.76, -30.34) * mm});
            skLineSegment(sketch, "E2278", {"start": v(73.76, -30.34) * mm, "end": v(74.05, -29.6) * mm});
            skLineSegment(sketch, "E2279", {"start": v(74.05, -29.6) * mm, "end": v(74.34, -28.88) * mm});
            skLineSegment(sketch, "E2280", {"start": v(74.34, -28.88) * mm, "end": v(74.62, -28.15) * mm});
            skLineSegment(sketch, "E2281", {"start": v(71.5, -35.35) * mm, "end": v(71.84, -34.64) * mm});
            skLineSegment(sketch, "E2282", {"start": v(71.84, -34.64) * mm, "end": v(72.18, -33.93) * mm});
            skLineSegment(sketch, "E2283", {"start": v(72.18, -33.93) * mm, "end": v(72.5, -33.22) * mm});
            skLineSegment(sketch, "E2284", {"start": v(72.5, -33.22) * mm, "end": v(72.83, -32.5) * mm});
            skLineSegment(sketch, "E2285", {"start": v(72.83, -32.5) * mm, "end": v(73.47, -33.66) * mm});
            skLineSegment(sketch, "E2286", {"start": v(73.47, -33.66) * mm, "end": v(74.1, -34.83) * mm});
            skLineSegment(sketch, "E2287", {"start": v(74.1, -34.83) * mm, "end": v(74.7, -36.02) * mm});
            skLineSegment(sketch, "E2288", {"start": v(74.7, -36.02) * mm, "end": v(70.4, -33.95) * mm});
            skLineSegment(sketch, "E2289", {"start": v(69.57, -40.6) * mm, "end": v(69.17, -41.28) * mm});
            skLineSegment(sketch, "E2290", {"start": v(69.17, -41.28) * mm, "end": v(68.76, -41.96) * mm});
            skLineSegment(sketch, "E2291", {"start": v(68.76, -41.96) * mm, "end": v(68.34, -42.63) * mm});
            skLineSegment(sketch, "E2292", {"start": v(68.34, -42.63) * mm, "end": v(68.58, -43.73) * mm});
            skLineSegment(sketch, "E2293", {"start": v(68.58, -43.73) * mm, "end": v(69.25, -44.16) * mm});
            skLineSegment(sketch, "E2294", {"start": v(69.25, -44.16) * mm, "end": v(70.36, -43.9) * mm});
            skLineSegment(sketch, "E2295", {"start": v(70.36, -43.9) * mm, "end": v(70.79, -43.2) * mm});
            skLineSegment(sketch, "E2296", {"start": v(70.79, -43.2) * mm, "end": v(71.21, -42.5) * mm});
            skLineSegment(sketch, "E2297", {"start": v(71.21, -42.5) * mm, "end": v(71.63, -41.8) * mm});
            skLineSegment(sketch, "E2298", {"start": v(71.63, -41.8) * mm, "end": v(67.51, -39.4) * mm});
            skLineSegment(sketch, "E2299", {"start": v(65.07, -43.31) * mm, "end": v(66.39, -44.2) * mm});
            skLineSegment(sketch, "E2300", {"start": v(66.39, -44.2) * mm, "end": v(67.26, -45.74) * mm});
            skLineSegment(sketch, "E2301", {"start": v(67.26, -45.74) * mm, "end": v(68.11, -47.3) * mm});
            skLineSegment(sketch, "E2302", {"start": v(68.11, -47.3) * mm, "end": v(66.35, -47.05) * mm});
            skLineSegment(sketch, "E2303", {"start": v(66.35, -47.05) * mm, "end": v(64.6, -46.77) * mm});
            skLineSegment(sketch, "E2304", {"start": v(64.6, -46.77) * mm, "end": v(63.3, -45.84) * mm});
            skLineSegment(sketch, "E2305", {"start": v(66.39, -44.2) * mm, "end": v(65.95, -44.84) * mm});
            skLineSegment(sketch, "E2306", {"start": v(65.95, -44.84) * mm, "end": v(65.5, -45.5) * mm});
            skLineSegment(sketch, "E2307", {"start": v(65.5, -45.5) * mm, "end": v(65.05, -46.13) * mm});
            skLineSegment(sketch, "E2308", {"start": v(65.05, -46.13) * mm, "end": v(64.6, -46.77) * mm});
            skLineSegment(sketch, "E2309", {"start": v(62.94, -51.51) * mm, "end": v(63.45, -50.9) * mm});
            skLineSegment(sketch, "E2310", {"start": v(63.45, -50.9) * mm, "end": v(63.95, -50.26) * mm});
            skLineSegment(sketch, "E2311", {"start": v(63.95, -50.26) * mm, "end": v(64.44, -49.63) * mm});
            skLineSegment(sketch, "E2312", {"start": v(64.44, -49.63) * mm, "end": v(64.93, -49) * mm});
            skLineSegment(sketch, "E2313", {"start": v(61.72, -50.5) * mm, "end": v(62.21, -49.9) * mm});
            skLineSegment(sketch, "E2314", {"start": v(62.21, -49.9) * mm, "end": v(62.7, -49.28) * mm});
            skLineSegment(sketch, "E2315", {"start": v(62.7, -49.28) * mm, "end": v(63.18, -48.66) * mm});
            skLineSegment(sketch, "E2316", {"start": v(63.18, -48.66) * mm, "end": v(63.66, -48.04) * mm});
            skLineSegment(sketch, "E2317", {"start": v(57.45, -52.99) * mm, "end": v(57.97, -52.42) * mm});
            skLineSegment(sketch, "E2318", {"start": v(57.97, -52.42) * mm, "end": v(58.49, -51.85) * mm});
            skLineSegment(sketch, "E2319", {"start": v(58.49, -51.85) * mm, "end": v(59, -51.27) * mm});
            skLineSegment(sketch, "E2320", {"start": v(59, -51.27) * mm, "end": v(59.5, -50.68) * mm});
            skLineSegment(sketch, "E2321", {"start": v(59.5, -50.68) * mm, "end": v(60.7, -51.71) * mm});
            skLineSegment(sketch, "E2322", {"start": v(60.7, -51.71) * mm, "end": v(60.8, -52.83) * mm});
            skLineSegment(sketch, "E2323", {"start": v(60.8, -52.83) * mm, "end": v(60.27, -53.43) * mm});
            skLineSegment(sketch, "E2324", {"start": v(60.27, -53.43) * mm, "end": v(59.74, -54.02) * mm});
            skLineSegment(sketch, "E2325", {"start": v(59.74, -54.02) * mm, "end": v(59.79, -55.14) * mm});
            skLineSegment(sketch, "E2326", {"start": v(59.79, -55.14) * mm, "end": v(60.37, -55.68) * mm});
            skLineSegment(sketch, "E2327", {"start": v(60.37, -55.68) * mm, "end": v(61.5, -55.62) * mm});
            skLineSegment(sketch, "E2328", {"start": v(61.5, -55.62) * mm, "end": v(62.05, -55) * mm});
            skLineSegment(sketch, "E2329", {"start": v(62.05, -55) * mm, "end": v(62.59, -54.4) * mm});
            skLineSegment(sketch, "E2330", {"start": v(62.59, -54.4) * mm, "end": v(62.52, -53.26) * mm});
            skLineSegment(sketch, "E2331", {"start": v(59.83, -57.4) * mm, "end": v(59.26, -58) * mm});
            skLineSegment(sketch, "E2332", {"start": v(59.26, -58) * mm, "end": v(58.69, -58.58) * mm});
            skLineSegment(sketch, "E2333", {"start": v(58.69, -58.58) * mm, "end": v(58.1, -59.15) * mm});
            skLineSegment(sketch, "E2334", {"start": v(58.1, -59.15) * mm, "end": v(57.52, -59.72) * mm});
            skLineSegment(sketch, "E2335", {"start": v(57.52, -59.72) * mm, "end": v(56.44, -57.45) * mm});
            skLineSegment(sketch, "E2336", {"start": v(56.44, -57.45) * mm, "end": v(55.32, -55.21) * mm});
            skSolve(sketch);
        }
        {
            var Q0;
            Q0=makeQuery(id+"F0.imprint","IMPRINT",FACE,{"disambiguationData":[TD([[makeQuery(id+"F0.imprint","IMPRINT",EDGE,{"derivedFrom":sQuery(id+"F0.wireOp",EDGE,"E0")}),1.0]])]});
            var sketch = newSketch(context, id + "F1", { "sketchPlane" : qUnion([Q0])});
            skArc(sketch, "E2337", {"start": v(-1.99, 1.6) * mm, "mid": v(0, -2.55) * mm, "end": v(1.99, 1.6) * mm});
            skLineSegment(sketch, "E2338.top", {"start": v(-1.99, 1.6) * mm, "end": v(1.99, 1.6) * mm});
            skSolve(sketch);
        }
        {
            var Q0;
            Q0 = qSketchRegion(id + "F0", true);
            extrude(context, id + "F2", {"entities" : qUnion([Q0]), "depth" : 7 * mm});
        }
        {
            var Q0;
            Q0 = qSketchRegion(id + "F1", true);
            extrude(context, id + "F3", {"entities" : qUnion([Q0]), "operationType" : NewBodyOperationType.REMOVE, "endBound" : BoundingType.UP_TO_NEXT, "depth" : 25 * mm});
        }
        {
            var Q0;
            Q0=makeQuery(id+"F2.opExtrude","CAP_FACE",FACE,{"disambiguationData":[OSD([sQuery(id+"F0.wireOp",EDGE,"E0"),sQuery(id+"F0.wireOp",EDGE,"E1"),sQuery(id+"F0.wireOp",EDGE,"E2"),sQuery(id+"F0.wireOp",EDGE,"E3"),sQuery(id+"F0.wireOp",EDGE,"E4"),sQuery(id+"F0.wireOp",EDGE,"E5"),sQuery(id+"F0.wireOp",EDGE,"E6"),sQuery(id+"F0.wireOp",EDGE,"E7"),sQuery(id+"F0.wireOp",EDGE,"E8"),sQuery(id+"F0.wireOp",EDGE,"E9"),sQuery(id+"F0.wireOp",EDGE,"E10"),sQuery(id+"F0.wireOp",EDGE,"E11"),sQuery(id+"F0.wireOp",EDGE,"E12"),sQuery(id+"F0.wireOp",EDGE,"E13"),sQuery(id+"F0.wireOp",EDGE,"E14"),sQuery(id+"F0.wireOp",EDGE,"E15"),sQuery(id+"F0.wireOp",EDGE,"E16"),sQuery(id+"F0.wireOp",EDGE,"E17"),sQuery(id+"F0.wireOp",EDGE,"E18"),sQuery(id+"F0.wireOp",EDGE,"E19"),sQuery(id+"F0.wireOp",EDGE,"E20"),sQuery(id+"F0.wireOp",EDGE,"E21"),sQuery(id+"F0.wireOp",EDGE,"E22"),sQuery(id+"F0.wireOp",EDGE,"E23"),sQuery(id+"F0.wireOp",EDGE,"E24"),sQuery(id+"F0.wireOp",EDGE,"E25"),sQuery(id+"F0.wireOp",EDGE,"E26"),sQuery(id+"F0.wireOp",EDGE,"E27"),sQuery(id+"F0.wireOp",EDGE,"E28"),sQuery(id+"F0.wireOp",EDGE,"E29"),sQuery(id+"F0.wireOp",EDGE,"E30"),sQuery(id+"F0.wireOp",EDGE,"E31"),sQuery(id+"F0.wireOp",EDGE,"E32"),sQuery(id+"F0.wireOp",EDGE,"E33"),sQuery(id+"F0.wireOp",EDGE,"E34"),sQuery(id+"F0.wireOp",EDGE,"E35"),sQuery(id+"F0.wireOp",EDGE,"E36"),sQuery(id+"F0.wireOp",EDGE,"E37"),sQuery(id+"F0.wireOp",EDGE,"E38"),sQuery(id+"F0.wireOp",EDGE,"E39"),sQuery(id+"F0.wireOp",EDGE,"E40"),sQuery(id+"F0.wireOp",EDGE,"E41"),sQuery(id+"F0.wireOp",EDGE,"E42"),sQuery(id+"F0.wireOp",EDGE,"E43"),sQuery(id+"F0.wireOp",EDGE,"E44"),sQuery(id+"F0.wireOp",EDGE,"E45"),sQuery(id+"F0.wireOp",EDGE,"E46"),sQuery(id+"F0.wireOp",EDGE,"E47"),sQuery(id+"F0.wireOp",EDGE,"E48"),sQuery(id+"F0.wireOp",EDGE,"E49"),sQuery(id+"F0.wireOp",EDGE,"E50"),sQuery(id+"F0.wireOp",EDGE,"E51"),sQuery(id+"F0.wireOp",EDGE,"E52"),sQuery(id+"F0.wireOp",EDGE,"E53"),sQuery(id+"F0.wireOp",EDGE,"E54"),sQuery(id+"F0.wireOp",EDGE,"E55"),sQuery(id+"F0.wireOp",EDGE,"E56"),sQuery(id+"F0.wireOp",EDGE,"E57"),sQuery(id+"F0.wireOp",EDGE,"E58"),sQuery(id+"F0.wireOp",EDGE,"E59"),sQuery(id+"F0.wireOp",EDGE,"E60"),sQuery(id+"F0.wireOp",EDGE,"E61"),sQuery(id+"F0.wireOp",EDGE,"E62"),sQuery(id+"F0.wireOp",EDGE,"E63"),sQuery(id+"F0.wireOp",EDGE,"E64"),sQuery(id+"F0.wireOp",EDGE,"E65"),sQuery(id+"F0.wireOp",EDGE,"E66"),sQuery(id+"F0.wireOp",EDGE,"E67"),sQuery(id+"F0.wireOp",EDGE,"E68"),sQuery(id+"F0.wireOp",EDGE,"E69"),sQuery(id+"F0.wireOp",EDGE,"E70"),sQuery(id+"F0.wireOp",EDGE,"E71"),sQuery(id+"F0.wireOp",EDGE,"E72"),sQuery(id+"F0.wireOp",EDGE,"E73"),sQuery(id+"F0.wireOp",EDGE,"E74"),sQuery(id+"F0.wireOp",EDGE,"E75"),sQuery(id+"F0.wireOp",EDGE,"E76"),sQuery(id+"F0.wireOp",EDGE,"E77"),sQuery(id+"F0.wireOp",EDGE,"E78"),sQuery(id+"F0.wireOp",EDGE,"E79"),sQuery(id+"F0.wireOp",EDGE,"E80"),sQuery(id+"F0.wireOp",EDGE,"E81"),sQuery(id+"F0.wireOp",EDGE,"E82"),sQuery(id+"F0.wireOp",EDGE,"E83"),sQuery(id+"F0.wireOp",EDGE,"E84"),sQuery(id+"F0.wireOp",EDGE,"E85"),sQuery(id+"F0.wireOp",EDGE,"E86"),sQuery(id+"F0.wireOp",EDGE,"E87"),sQuery(id+"F0.wireOp",EDGE,"E88"),sQuery(id+"F0.wireOp",EDGE,"E89"),sQuery(id+"F0.wireOp",EDGE,"E90"),sQuery(id+"F0.wireOp",EDGE,"E91"),sQuery(id+"F0.wireOp",EDGE,"E92"),sQuery(id+"F0.wireOp",EDGE,"E93"),sQuery(id+"F0.wireOp",EDGE,"E94"),sQuery(id+"F0.wireOp",EDGE,"E95"),sQuery(id+"F0.wireOp",EDGE,"E96"),sQuery(id+"F0.wireOp",EDGE,"E97"),sQuery(id+"F0.wireOp",EDGE,"E98"),sQuery(id+"F0.wireOp",EDGE,"E99"),sQuery(id+"F0.wireOp",EDGE,"E100"),sQuery(id+"F0.wireOp",EDGE,"E101"),sQuery(id+"F0.wireOp",EDGE,"E102"),sQuery(id+"F0.wireOp",EDGE,"E103"),sQuery(id+"F0.wireOp",EDGE,"E104"),sQuery(id+"F0.wireOp",EDGE,"E105"),sQuery(id+"F0.wireOp",EDGE,"E106"),sQuery(id+"F0.wireOp",EDGE,"E107"),sQuery(id+"F0.wireOp",EDGE,"E108"),sQuery(id+"F0.wireOp",EDGE,"E109"),sQuery(id+"F0.wireOp",EDGE,"E110"),sQuery(id+"F0.wireOp",EDGE,"E111"),sQuery(id+"F0.wireOp",EDGE,"E112"),sQuery(id+"F0.wireOp",EDGE,"E113"),sQuery(id+"F0.wireOp",EDGE,"E114"),sQuery(id+"F0.wireOp",EDGE,"E115"),sQuery(id+"F0.wireOp",EDGE,"E116"),sQuery(id+"F0.wireOp",EDGE,"E117"),sQuery(id+"F0.wireOp",EDGE,"E118"),sQuery(id+"F0.wireOp",EDGE,"E119"),sQuery(id+"F0.wireOp",EDGE,"E120"),sQuery(id+"F0.wireOp",EDGE,"E121"),sQuery(id+"F0.wireOp",EDGE,"E122"),sQuery(id+"F0.wireOp",EDGE,"E123"),sQuery(id+"F0.wireOp",EDGE,"E124"),sQuery(id+"F0.wireOp",EDGE,"E125"),sQuery(id+"F0.wireOp",EDGE,"E126"),sQuery(id+"F0.wireOp",EDGE,"E127"),sQuery(id+"F0.wireOp",EDGE,"E128"),sQuery(id+"F0.wireOp",EDGE,"E129"),sQuery(id+"F0.wireOp",EDGE,"E130"),sQuery(id+"F0.wireOp",EDGE,"E131"),sQuery(id+"F0.wireOp",EDGE,"E132"),sQuery(id+"F0.wireOp",EDGE,"E133"),sQuery(id+"F0.wireOp",EDGE,"E134"),sQuery(id+"F0.wireOp",EDGE,"E135"),sQuery(id+"F0.wireOp",EDGE,"E136"),sQuery(id+"F0.wireOp",EDGE,"E137"),sQuery(id+"F0.wireOp",EDGE,"E138"),sQuery(id+"F0.wireOp",EDGE,"E139"),sQuery(id+"F0.wireOp",EDGE,"E140"),sQuery(id+"F0.wireOp",EDGE,"E141"),sQuery(id+"F0.wireOp",EDGE,"E142"),sQuery(id+"F0.wireOp",EDGE,"E143"),sQuery(id+"F0.wireOp",EDGE,"E144"),sQuery(id+"F0.wireOp",EDGE,"E145"),sQuery(id+"F0.wireOp",EDGE,"E146"),sQuery(id+"F0.wireOp",EDGE,"E147"),sQuery(id+"F0.wireOp",EDGE,"E148"),sQuery(id+"F0.wireOp",EDGE,"E149"),sQuery(id+"F0.wireOp",EDGE,"E150"),sQuery(id+"F0.wireOp",EDGE,"E151"),sQuery(id+"F0.wireOp",EDGE,"E152"),sQuery(id+"F0.wireOp",EDGE,"E153"),sQuery(id+"F0.wireOp",EDGE,"E154"),sQuery(id+"F0.wireOp",EDGE,"E155"),sQuery(id+"F0.wireOp",EDGE,"E156"),sQuery(id+"F0.wireOp",EDGE,"E157"),sQuery(id+"F0.wireOp",EDGE,"E158"),sQuery(id+"F0.wireOp",EDGE,"E159"),sQuery(id+"F0.wireOp",EDGE,"E160"),sQuery(id+"F0.wireOp",EDGE,"E161"),sQuery(id+"F0.wireOp",EDGE,"E162"),sQuery(id+"F0.wireOp",EDGE,"E163"),sQuery(id+"F0.wireOp",EDGE,"E164"),sQuery(id+"F0.wireOp",EDGE,"E165"),sQuery(id+"F0.wireOp",EDGE,"E166"),sQuery(id+"F0.wireOp",EDGE,"E167"),sQuery(id+"F0.wireOp",EDGE,"E168"),sQuery(id+"F0.wireOp",EDGE,"E169"),sQuery(id+"F0.wireOp",EDGE,"E170"),sQuery(id+"F0.wireOp",EDGE,"E171"),sQuery(id+"F0.wireOp",EDGE,"E172"),sQuery(id+"F0.wireOp",EDGE,"E173"),sQuery(id+"F0.wireOp",EDGE,"E174"),sQuery(id+"F0.wireOp",EDGE,"E175"),sQuery(id+"F0.wireOp",EDGE,"E176"),sQuery(id+"F0.wireOp",EDGE,"E177"),sQuery(id+"F0.wireOp",EDGE,"E178"),sQuery(id+"F0.wireOp",EDGE,"E179"),sQuery(id+"F0.wireOp",EDGE,"E180"),sQuery(id+"F0.wireOp",EDGE,"E181"),sQuery(id+"F0.wireOp",EDGE,"E182"),sQuery(id+"F0.wireOp",EDGE,"E183"),sQuery(id+"F0.wireOp",EDGE,"E184"),sQuery(id+"F0.wireOp",EDGE,"E185"),sQuery(id+"F0.wireOp",EDGE,"E186"),sQuery(id+"F0.wireOp",EDGE,"E187"),sQuery(id+"F0.wireOp",EDGE,"E188"),sQuery(id+"F0.wireOp",EDGE,"E189"),sQuery(id+"F0.wireOp",EDGE,"E190"),sQuery(id+"F0.wireOp",EDGE,"E191"),sQuery(id+"F0.wireOp",EDGE,"E192"),sQuery(id+"F0.wireOp",EDGE,"E193"),sQuery(id+"F0.wireOp",EDGE,"E194"),sQuery(id+"F0.wireOp",EDGE,"E195"),sQuery(id+"F0.wireOp",EDGE,"E196"),sQuery(id+"F0.wireOp",EDGE,"E197"),sQuery(id+"F0.wireOp",EDGE,"E198"),sQuery(id+"F0.wireOp",EDGE,"E199"),sQuery(id+"F0.wireOp",EDGE,"E200"),sQuery(id+"F0.wireOp",EDGE,"E201"),sQuery(id+"F0.wireOp",EDGE,"E202"),sQuery(id+"F0.wireOp",EDGE,"E203"),sQuery(id+"F0.wireOp",EDGE,"E204"),sQuery(id+"F0.wireOp",EDGE,"E205"),sQuery(id+"F0.wireOp",EDGE,"E206"),sQuery(id+"F0.wireOp",EDGE,"E207"),sQuery(id+"F0.wireOp",EDGE,"E208"),sQuery(id+"F0.wireOp",EDGE,"E209"),sQuery(id+"F0.wireOp",EDGE,"E210"),sQuery(id+"F0.wireOp",EDGE,"E211"),sQuery(id+"F0.wireOp",EDGE,"E212"),sQuery(id+"F0.wireOp",EDGE,"E213"),sQuery(id+"F0.wireOp",EDGE,"E214"),sQuery(id+"F0.wireOp",EDGE,"E215"),sQuery(id+"F0.wireOp",EDGE,"E216"),sQuery(id+"F0.wireOp",EDGE,"E217"),sQuery(id+"F0.wireOp",EDGE,"E218"),sQuery(id+"F0.wireOp",EDGE,"E219"),sQuery(id+"F0.wireOp",EDGE,"E220"),sQuery(id+"F0.wireOp",EDGE,"E221"),sQuery(id+"F0.wireOp",EDGE,"E222"),sQuery(id+"F0.wireOp",EDGE,"E223"),sQuery(id+"F0.wireOp",EDGE,"E224"),sQuery(id+"F0.wireOp",EDGE,"E225"),sQuery(id+"F0.wireOp",EDGE,"E226"),sQuery(id+"F0.wireOp",EDGE,"E227"),sQuery(id+"F0.wireOp",EDGE,"E228"),sQuery(id+"F0.wireOp",EDGE,"E229"),sQuery(id+"F0.wireOp",EDGE,"E230"),sQuery(id+"F0.wireOp",EDGE,"E231"),sQuery(id+"F0.wireOp",EDGE,"E232"),sQuery(id+"F0.wireOp",EDGE,"E233"),sQuery(id+"F0.wireOp",EDGE,"E234"),sQuery(id+"F0.wireOp",EDGE,"E235"),sQuery(id+"F0.wireOp",EDGE,"E236"),sQuery(id+"F0.wireOp",EDGE,"E237"),sQuery(id+"F0.wireOp",EDGE,"E238"),sQuery(id+"F0.wireOp",EDGE,"E239"),sQuery(id+"F0.wireOp",EDGE,"E240"),sQuery(id+"F0.wireOp",EDGE,"E241"),sQuery(id+"F0.wireOp",EDGE,"E242"),sQuery(id+"F0.wireOp",EDGE,"E243"),sQuery(id+"F0.wireOp",EDGE,"E244"),sQuery(id+"F0.wireOp",EDGE,"E245"),sQuery(id+"F0.wireOp",EDGE,"E246"),sQuery(id+"F0.wireOp",EDGE,"E247"),sQuery(id+"F0.wireOp",EDGE,"E248"),sQuery(id+"F0.wireOp",EDGE,"E249"),sQuery(id+"F0.wireOp",EDGE,"E250"),sQuery(id+"F0.wireOp",EDGE,"E251"),sQuery(id+"F0.wireOp",EDGE,"E252"),sQuery(id+"F0.wireOp",EDGE,"E253"),sQuery(id+"F0.wireOp",EDGE,"E254"),sQuery(id+"F0.wireOp",EDGE,"E255"),sQuery(id+"F0.wireOp",EDGE,"E256"),sQuery(id+"F0.wireOp",EDGE,"E257"),sQuery(id+"F0.wireOp",EDGE,"E258"),sQuery(id+"F0.wireOp",EDGE,"E259"),sQuery(id+"F0.wireOp",EDGE,"E260"),sQuery(id+"F0.wireOp",EDGE,"E261"),sQuery(id+"F0.wireOp",EDGE,"E262"),sQuery(id+"F0.wireOp",EDGE,"E263"),sQuery(id+"F0.wireOp",EDGE,"E264"),sQuery(id+"F0.wireOp",EDGE,"E265"),sQuery(id+"F0.wireOp",EDGE,"E266"),sQuery(id+"F0.wireOp",EDGE,"E267"),sQuery(id+"F0.wireOp",EDGE,"E268"),sQuery(id+"F0.wireOp",EDGE,"E269"),sQuery(id+"F0.wireOp",EDGE,"E270"),sQuery(id+"F0.wireOp",EDGE,"E271"),sQuery(id+"F0.wireOp",EDGE,"E272"),sQuery(id+"F0.wireOp",EDGE,"E273"),sQuery(id+"F0.wireOp",EDGE,"E274"),sQuery(id+"F0.wireOp",EDGE,"E275"),sQuery(id+"F0.wireOp",EDGE,"E276"),sQuery(id+"F0.wireOp",EDGE,"E277"),sQuery(id+"F0.wireOp",EDGE,"E278"),sQuery(id+"F0.wireOp",EDGE,"E279"),sQuery(id+"F0.wireOp",EDGE,"E280"),sQuery(id+"F0.wireOp",EDGE,"E281"),sQuery(id+"F0.wireOp",EDGE,"E282"),sQuery(id+"F0.wireOp",EDGE,"E283"),sQuery(id+"F0.wireOp",EDGE,"E284"),sQuery(id+"F0.wireOp",EDGE,"E285"),sQuery(id+"F0.wireOp",EDGE,"E286"),sQuery(id+"F0.wireOp",EDGE,"E287"),sQuery(id+"F0.wireOp",EDGE,"E288"),sQuery(id+"F0.wireOp",EDGE,"E289"),sQuery(id+"F0.wireOp",EDGE,"E290"),sQuery(id+"F0.wireOp",EDGE,"E291"),sQuery(id+"F0.wireOp",EDGE,"E292"),sQuery(id+"F0.wireOp",EDGE,"E293"),sQuery(id+"F0.wireOp",EDGE,"E294"),sQuery(id+"F0.wireOp",EDGE,"E295"),sQuery(id+"F0.wireOp",EDGE,"E296"),sQuery(id+"F0.wireOp",EDGE,"E297"),sQuery(id+"F0.wireOp",EDGE,"E298"),sQuery(id+"F0.wireOp",EDGE,"E299"),sQuery(id+"F0.wireOp",EDGE,"E300"),sQuery(id+"F0.wireOp",EDGE,"E301"),sQuery(id+"F0.wireOp",EDGE,"E302"),sQuery(id+"F0.wireOp",EDGE,"E303"),sQuery(id+"F0.wireOp",EDGE,"E304"),sQuery(id+"F0.wireOp",EDGE,"E305"),sQuery(id+"F0.wireOp",EDGE,"E306"),sQuery(id+"F0.wireOp",EDGE,"E307"),sQuery(id+"F0.wireOp",EDGE,"E308"),sQuery(id+"F0.wireOp",EDGE,"E309"),sQuery(id+"F0.wireOp",EDGE,"E310"),sQuery(id+"F0.wireOp",EDGE,"E311"),sQuery(id+"F0.wireOp",EDGE,"E312"),sQuery(id+"F0.wireOp",EDGE,"E313"),sQuery(id+"F0.wireOp",EDGE,"E314"),sQuery(id+"F0.wireOp",EDGE,"E315"),sQuery(id+"F0.wireOp",EDGE,"E316"),sQuery(id+"F0.wireOp",EDGE,"E317"),sQuery(id+"F0.wireOp",EDGE,"E318"),sQuery(id+"F0.wireOp",EDGE,"E319"),sQuery(id+"F0.wireOp",EDGE,"E320"),sQuery(id+"F0.wireOp",EDGE,"E321"),sQuery(id+"F0.wireOp",EDGE,"E322"),sQuery(id+"F0.wireOp",EDGE,"E323"),sQuery(id+"F0.wireOp",EDGE,"E324"),sQuery(id+"F0.wireOp",EDGE,"E325"),sQuery(id+"F0.wireOp",EDGE,"E326"),sQuery(id+"F0.wireOp",EDGE,"E327"),sQuery(id+"F0.wireOp",EDGE,"E328"),sQuery(id+"F0.wireOp",EDGE,"E329"),sQuery(id+"F0.wireOp",EDGE,"E330"),sQuery(id+"F0.wireOp",EDGE,"E331"),sQuery(id+"F0.wireOp",EDGE,"E332"),sQuery(id+"F0.wireOp",EDGE,"E333"),sQuery(id+"F0.wireOp",EDGE,"E334"),sQuery(id+"F0.wireOp",EDGE,"E335"),sQuery(id+"F0.wireOp",EDGE,"E336"),sQuery(id+"F0.wireOp",EDGE,"E337"),sQuery(id+"F0.wireOp",EDGE,"E338"),sQuery(id+"F0.wireOp",EDGE,"E339"),sQuery(id+"F0.wireOp",EDGE,"E340"),sQuery(id+"F0.wireOp",EDGE,"E341"),sQuery(id+"F0.wireOp",EDGE,"E342"),sQuery(id+"F0.wireOp",EDGE,"E343"),sQuery(id+"F0.wireOp",EDGE,"E344"),sQuery(id+"F0.wireOp",EDGE,"E345"),sQuery(id+"F0.wireOp",EDGE,"E346"),sQuery(id+"F0.wireOp",EDGE,"E347"),sQuery(id+"F0.wireOp",EDGE,"E348"),sQuery(id+"F0.wireOp",EDGE,"E349"),sQuery(id+"F0.wireOp",EDGE,"E350"),sQuery(id+"F0.wireOp",EDGE,"E351"),sQuery(id+"F0.wireOp",EDGE,"E352"),sQuery(id+"F0.wireOp",EDGE,"E353"),sQuery(id+"F0.wireOp",EDGE,"E354"),sQuery(id+"F0.wireOp",EDGE,"E355"),sQuery(id+"F0.wireOp",EDGE,"E356"),sQuery(id+"F0.wireOp",EDGE,"E357"),sQuery(id+"F0.wireOp",EDGE,"E358"),sQuery(id+"F0.wireOp",EDGE,"E359"),sQuery(id+"F0.wireOp",EDGE,"E360"),sQuery(id+"F0.wireOp",EDGE,"E361"),sQuery(id+"F0.wireOp",EDGE,"E362"),sQuery(id+"F0.wireOp",EDGE,"E363"),sQuery(id+"F0.wireOp",EDGE,"E364"),sQuery(id+"F0.wireOp",EDGE,"E365"),sQuery(id+"F0.wireOp",EDGE,"E366"),sQuery(id+"F0.wireOp",EDGE,"E367"),sQuery(id+"F0.wireOp",EDGE,"E368"),sQuery(id+"F0.wireOp",EDGE,"E369"),sQuery(id+"F0.wireOp",EDGE,"E370"),sQuery(id+"F0.wireOp",EDGE,"E371"),sQuery(id+"F0.wireOp",EDGE,"E372"),sQuery(id+"F0.wireOp",EDGE,"E373"),sQuery(id+"F0.wireOp",EDGE,"E374"),sQuery(id+"F0.wireOp",EDGE,"E375"),sQuery(id+"F0.wireOp",EDGE,"E376"),sQuery(id+"F0.wireOp",EDGE,"E377"),sQuery(id+"F0.wireOp",EDGE,"E378"),sQuery(id+"F0.wireOp",EDGE,"E379"),sQuery(id+"F0.wireOp",EDGE,"E380"),sQuery(id+"F0.wireOp",EDGE,"E381"),sQuery(id+"F0.wireOp",EDGE,"E382"),sQuery(id+"F0.wireOp",EDGE,"E383"),sQuery(id+"F0.wireOp",EDGE,"E384"),sQuery(id+"F0.wireOp",EDGE,"E385"),sQuery(id+"F0.wireOp",EDGE,"E386"),sQuery(id+"F0.wireOp",EDGE,"E387"),sQuery(id+"F0.wireOp",EDGE,"E388"),sQuery(id+"F0.wireOp",EDGE,"E389"),sQuery(id+"F0.wireOp",EDGE,"E390"),sQuery(id+"F0.wireOp",EDGE,"E391"),sQuery(id+"F0.wireOp",EDGE,"E392"),sQuery(id+"F0.wireOp",EDGE,"E393"),sQuery(id+"F0.wireOp",EDGE,"E394"),sQuery(id+"F0.wireOp",EDGE,"E395"),sQuery(id+"F0.wireOp",EDGE,"E396"),sQuery(id+"F0.wireOp",EDGE,"E397"),sQuery(id+"F0.wireOp",EDGE,"E398"),sQuery(id+"F0.wireOp",EDGE,"E399"),sQuery(id+"F0.wireOp",EDGE,"E400"),sQuery(id+"F0.wireOp",EDGE,"E401"),sQuery(id+"F0.wireOp",EDGE,"E402"),sQuery(id+"F0.wireOp",EDGE,"E403"),sQuery(id+"F0.wireOp",EDGE,"E404"),sQuery(id+"F0.wireOp",EDGE,"E405"),sQuery(id+"F0.wireOp",EDGE,"E406"),sQuery(id+"F0.wireOp",EDGE,"E407"),sQuery(id+"F0.wireOp",EDGE,"E408"),sQuery(id+"F0.wireOp",EDGE,"E409"),sQuery(id+"F0.wireOp",EDGE,"E410"),sQuery(id+"F0.wireOp",EDGE,"E411"),sQuery(id+"F0.wireOp",EDGE,"E412"),sQuery(id+"F0.wireOp",EDGE,"E413"),sQuery(id+"F0.wireOp",EDGE,"E414"),sQuery(id+"F0.wireOp",EDGE,"E415"),sQuery(id+"F0.wireOp",EDGE,"E416"),sQuery(id+"F0.wireOp",EDGE,"E417"),sQuery(id+"F0.wireOp",EDGE,"E418"),sQuery(id+"F0.wireOp",EDGE,"E419"),sQuery(id+"F0.wireOp",EDGE,"E420"),sQuery(id+"F0.wireOp",EDGE,"E421"),sQuery(id+"F0.wireOp",EDGE,"E422"),sQuery(id+"F0.wireOp",EDGE,"E423"),sQuery(id+"F0.wireOp",EDGE,"E424"),sQuery(id+"F0.wireOp",EDGE,"E425"),sQuery(id+"F0.wireOp",EDGE,"E426"),sQuery(id+"F0.wireOp",EDGE,"E427"),sQuery(id+"F0.wireOp",EDGE,"E428"),sQuery(id+"F0.wireOp",EDGE,"E429"),sQuery(id+"F0.wireOp",EDGE,"E430"),sQuery(id+"F0.wireOp",EDGE,"E431"),sQuery(id+"F0.wireOp",EDGE,"E432"),sQuery(id+"F0.wireOp",EDGE,"E433"),sQuery(id+"F0.wireOp",EDGE,"E434"),sQuery(id+"F0.wireOp",EDGE,"E435"),sQuery(id+"F0.wireOp",EDGE,"E436"),sQuery(id+"F0.wireOp",EDGE,"E437"),sQuery(id+"F0.wireOp",EDGE,"E438"),sQuery(id+"F0.wireOp",EDGE,"E439"),sQuery(id+"F0.wireOp",EDGE,"E440"),sQuery(id+"F0.wireOp",EDGE,"E441"),sQuery(id+"F0.wireOp",EDGE,"E442"),sQuery(id+"F0.wireOp",EDGE,"E443"),sQuery(id+"F0.wireOp",EDGE,"E444"),sQuery(id+"F0.wireOp",EDGE,"E445"),sQuery(id+"F0.wireOp",EDGE,"E446"),sQuery(id+"F0.wireOp",EDGE,"E447"),sQuery(id+"F0.wireOp",EDGE,"E448"),sQuery(id+"F0.wireOp",EDGE,"E449"),sQuery(id+"F0.wireOp",EDGE,"E450"),sQuery(id+"F0.wireOp",EDGE,"E451"),sQuery(id+"F0.wireOp",EDGE,"E452"),sQuery(id+"F0.wireOp",EDGE,"E453"),sQuery(id+"F0.wireOp",EDGE,"E454"),sQuery(id+"F0.wireOp",EDGE,"E455"),sQuery(id+"F0.wireOp",EDGE,"E456"),sQuery(id+"F0.wireOp",EDGE,"E457"),sQuery(id+"F0.wireOp",EDGE,"E458"),sQuery(id+"F0.wireOp",EDGE,"E459"),sQuery(id+"F0.wireOp",EDGE,"E460"),sQuery(id+"F0.wireOp",EDGE,"E461"),sQuery(id+"F0.wireOp",EDGE,"E462"),sQuery(id+"F0.wireOp",EDGE,"E463"),sQuery(id+"F0.wireOp",EDGE,"E464"),sQuery(id+"F0.wireOp",EDGE,"E465"),sQuery(id+"F0.wireOp",EDGE,"E466"),sQuery(id+"F0.wireOp",EDGE,"E467"),sQuery(id+"F0.wireOp",EDGE,"E468"),sQuery(id+"F0.wireOp",EDGE,"E469"),sQuery(id+"F0.wireOp",EDGE,"E470"),sQuery(id+"F0.wireOp",EDGE,"E471"),sQuery(id+"F0.wireOp",EDGE,"E472"),sQuery(id+"F0.wireOp",EDGE,"E473"),sQuery(id+"F0.wireOp",EDGE,"E474"),sQuery(id+"F0.wireOp",EDGE,"E475"),sQuery(id+"F0.wireOp",EDGE,"E476"),sQuery(id+"F0.wireOp",EDGE,"E477"),sQuery(id+"F0.wireOp",EDGE,"E478"),sQuery(id+"F0.wireOp",EDGE,"E479"),sQuery(id+"F0.wireOp",EDGE,"E480"),sQuery(id+"F0.wireOp",EDGE,"E481"),sQuery(id+"F0.wireOp",EDGE,"E482"),sQuery(id+"F0.wireOp",EDGE,"E483"),sQuery(id+"F0.wireOp",EDGE,"E484"),sQuery(id+"F0.wireOp",EDGE,"E485"),sQuery(id+"F0.wireOp",EDGE,"E486"),sQuery(id+"F0.wireOp",EDGE,"E487"),sQuery(id+"F0.wireOp",EDGE,"E488"),sQuery(id+"F0.wireOp",EDGE,"E489"),sQuery(id+"F0.wireOp",EDGE,"E490"),sQuery(id+"F0.wireOp",EDGE,"E491"),sQuery(id+"F0.wireOp",EDGE,"E492"),sQuery(id+"F0.wireOp",EDGE,"E493"),sQuery(id+"F0.wireOp",EDGE,"E494"),sQuery(id+"F0.wireOp",EDGE,"E495"),sQuery(id+"F0.wireOp",EDGE,"E496"),sQuery(id+"F0.wireOp",EDGE,"E497"),sQuery(id+"F0.wireOp",EDGE,"E498"),sQuery(id+"F0.wireOp",EDGE,"E499"),sQuery(id+"F0.wireOp",EDGE,"E500"),sQuery(id+"F0.wireOp",EDGE,"E501"),sQuery(id+"F0.wireOp",EDGE,"E502"),sQuery(id+"F0.wireOp",EDGE,"E503"),sQuery(id+"F0.wireOp",EDGE,"E504"),sQuery(id+"F0.wireOp",EDGE,"E505"),sQuery(id+"F0.wireOp",EDGE,"E506"),sQuery(id+"F0.wireOp",EDGE,"E507"),sQuery(id+"F0.wireOp",EDGE,"E508"),sQuery(id+"F0.wireOp",EDGE,"E509"),sQuery(id+"F0.wireOp",EDGE,"E510"),sQuery(id+"F0.wireOp",EDGE,"E511"),sQuery(id+"F0.wireOp",EDGE,"E512"),sQuery(id+"F0.wireOp",EDGE,"E513"),sQuery(id+"F0.wireOp",EDGE,"E514"),sQuery(id+"F0.wireOp",EDGE,"E515"),sQuery(id+"F0.wireOp",EDGE,"E516"),sQuery(id+"F0.wireOp",EDGE,"E517"),sQuery(id+"F0.wireOp",EDGE,"E518"),sQuery(id+"F0.wireOp",EDGE,"E519"),sQuery(id+"F0.wireOp",EDGE,"E520"),sQuery(id+"F0.wireOp",EDGE,"E521"),sQuery(id+"F0.wireOp",EDGE,"E522"),sQuery(id+"F0.wireOp",EDGE,"E523"),sQuery(id+"F0.wireOp",EDGE,"E524"),sQuery(id+"F0.wireOp",EDGE,"E525"),sQuery(id+"F0.wireOp",EDGE,"E526"),sQuery(id+"F0.wireOp",EDGE,"E527"),sQuery(id+"F0.wireOp",EDGE,"E528"),sQuery(id+"F0.wireOp",EDGE,"E529"),sQuery(id+"F0.wireOp",EDGE,"E530"),sQuery(id+"F0.wireOp",EDGE,"E531"),sQuery(id+"F0.wireOp",EDGE,"E532"),sQuery(id+"F0.wireOp",EDGE,"E533"),sQuery(id+"F0.wireOp",EDGE,"E534"),sQuery(id+"F0.wireOp",EDGE,"E535"),sQuery(id+"F0.wireOp",EDGE,"E536"),sQuery(id+"F0.wireOp",EDGE,"E537"),sQuery(id+"F0.wireOp",EDGE,"E538"),sQuery(id+"F0.wireOp",EDGE,"E539"),sQuery(id+"F0.wireOp",EDGE,"E540"),sQuery(id+"F0.wireOp",EDGE,"E541"),sQuery(id+"F0.wireOp",EDGE,"E542"),sQuery(id+"F0.wireOp",EDGE,"E543"),sQuery(id+"F0.wireOp",EDGE,"E544"),sQuery(id+"F0.wireOp",EDGE,"E545"),sQuery(id+"F0.wireOp",EDGE,"E546"),sQuery(id+"F0.wireOp",EDGE,"E547"),sQuery(id+"F0.wireOp",EDGE,"E548"),sQuery(id+"F0.wireOp",EDGE,"E549"),sQuery(id+"F0.wireOp",EDGE,"E550"),sQuery(id+"F0.wireOp",EDGE,"E551"),sQuery(id+"F0.wireOp",EDGE,"E552"),sQuery(id+"F0.wireOp",EDGE,"E553"),sQuery(id+"F0.wireOp",EDGE,"E554"),sQuery(id+"F0.wireOp",EDGE,"E555"),sQuery(id+"F0.wireOp",EDGE,"E556"),sQuery(id+"F0.wireOp",EDGE,"E557"),sQuery(id+"F0.wireOp",EDGE,"E558"),sQuery(id+"F0.wireOp",EDGE,"E559"),sQuery(id+"F0.wireOp",EDGE,"E560"),sQuery(id+"F0.wireOp",EDGE,"E561"),sQuery(id+"F0.wireOp",EDGE,"E562"),sQuery(id+"F0.wireOp",EDGE,"E563"),sQuery(id+"F0.wireOp",EDGE,"E564"),sQuery(id+"F0.wireOp",EDGE,"E565"),sQuery(id+"F0.wireOp",EDGE,"E566"),sQuery(id+"F0.wireOp",EDGE,"E567"),sQuery(id+"F0.wireOp",EDGE,"E568"),sQuery(id+"F0.wireOp",EDGE,"E569"),sQuery(id+"F0.wireOp",EDGE,"E570"),sQuery(id+"F0.wireOp",EDGE,"E571"),sQuery(id+"F0.wireOp",EDGE,"E572"),sQuery(id+"F0.wireOp",EDGE,"E573"),sQuery(id+"F0.wireOp",EDGE,"E574"),sQuery(id+"F0.wireOp",EDGE,"E575"),sQuery(id+"F0.wireOp",EDGE,"E576"),sQuery(id+"F0.wireOp",EDGE,"E577"),sQuery(id+"F0.wireOp",EDGE,"E578"),sQuery(id+"F0.wireOp",EDGE,"E579"),sQuery(id+"F0.wireOp",EDGE,"E580"),sQuery(id+"F0.wireOp",EDGE,"E581"),sQuery(id+"F0.wireOp",EDGE,"E582"),sQuery(id+"F0.wireOp",EDGE,"E583"),sQuery(id+"F0.wireOp",EDGE,"E584"),sQuery(id+"F0.wireOp",EDGE,"E585"),sQuery(id+"F0.wireOp",EDGE,"E586"),sQuery(id+"F0.wireOp",EDGE,"E587"),sQuery(id+"F0.wireOp",EDGE,"E588"),sQuery(id+"F0.wireOp",EDGE,"E589"),sQuery(id+"F0.wireOp",EDGE,"E590"),sQuery(id+"F0.wireOp",EDGE,"E591"),sQuery(id+"F0.wireOp",EDGE,"E592"),sQuery(id+"F0.wireOp",EDGE,"E593"),sQuery(id+"F0.wireOp",EDGE,"E594"),sQuery(id+"F0.wireOp",EDGE,"E595"),sQuery(id+"F0.wireOp",EDGE,"E596"),sQuery(id+"F0.wireOp",EDGE,"E597"),sQuery(id+"F0.wireOp",EDGE,"E598"),sQuery(id+"F0.wireOp",EDGE,"E599"),sQuery(id+"F0.wireOp",EDGE,"E600"),sQuery(id+"F0.wireOp",EDGE,"E601"),sQuery(id+"F0.wireOp",EDGE,"E602"),sQuery(id+"F0.wireOp",EDGE,"E603"),sQuery(id+"F0.wireOp",EDGE,"E604"),sQuery(id+"F0.wireOp",EDGE,"E605"),sQuery(id+"F0.wireOp",EDGE,"E606"),sQuery(id+"F0.wireOp",EDGE,"E607"),sQuery(id+"F0.wireOp",EDGE,"E608"),sQuery(id+"F0.wireOp",EDGE,"E609"),sQuery(id+"F0.wireOp",EDGE,"E610"),sQuery(id+"F0.wireOp",EDGE,"E611"),sQuery(id+"F0.wireOp",EDGE,"E612"),sQuery(id+"F0.wireOp",EDGE,"E613"),sQuery(id+"F0.wireOp",EDGE,"E614"),sQuery(id+"F0.wireOp",EDGE,"E615"),sQuery(id+"F0.wireOp",EDGE,"E616"),sQuery(id+"F0.wireOp",EDGE,"E617"),sQuery(id+"F0.wireOp",EDGE,"E618"),sQuery(id+"F0.wireOp",EDGE,"E619"),sQuery(id+"F0.wireOp",EDGE,"E620"),sQuery(id+"F0.wireOp",EDGE,"E621"),sQuery(id+"F0.wireOp",EDGE,"E622"),sQuery(id+"F0.wireOp",EDGE,"E623"),sQuery(id+"F0.wireOp",EDGE,"E624"),sQuery(id+"F0.wireOp",EDGE,"E625"),sQuery(id+"F0.wireOp",EDGE,"E626"),sQuery(id+"F0.wireOp",EDGE,"E627"),sQuery(id+"F0.wireOp",EDGE,"E628"),sQuery(id+"F0.wireOp",EDGE,"E629"),sQuery(id+"F0.wireOp",EDGE,"E630"),sQuery(id+"F0.wireOp",EDGE,"E631"),sQuery(id+"F0.wireOp",EDGE,"E632"),sQuery(id+"F0.wireOp",EDGE,"E633"),sQuery(id+"F0.wireOp",EDGE,"E634"),sQuery(id+"F0.wireOp",EDGE,"E635"),sQuery(id+"F0.wireOp",EDGE,"E636"),sQuery(id+"F0.wireOp",EDGE,"E637"),sQuery(id+"F0.wireOp",EDGE,"E638"),sQuery(id+"F0.wireOp",EDGE,"E639"),sQuery(id+"F0.wireOp",EDGE,"E640"),sQuery(id+"F0.wireOp",EDGE,"E641"),sQuery(id+"F0.wireOp",EDGE,"E642"),sQuery(id+"F0.wireOp",EDGE,"E643"),sQuery(id+"F0.wireOp",EDGE,"E644"),sQuery(id+"F0.wireOp",EDGE,"E645"),sQuery(id+"F0.wireOp",EDGE,"E646"),sQuery(id+"F0.wireOp",EDGE,"E647"),sQuery(id+"F0.wireOp",EDGE,"E648"),sQuery(id+"F0.wireOp",EDGE,"E649"),sQuery(id+"F0.wireOp",EDGE,"E650"),sQuery(id+"F0.wireOp",EDGE,"E651"),sQuery(id+"F0.wireOp",EDGE,"E652"),sQuery(id+"F0.wireOp",EDGE,"E653"),sQuery(id+"F0.wireOp",EDGE,"E654"),sQuery(id+"F0.wireOp",EDGE,"E655"),sQuery(id+"F0.wireOp",EDGE,"E656"),sQuery(id+"F0.wireOp",EDGE,"E657"),sQuery(id+"F0.wireOp",EDGE,"E658"),sQuery(id+"F0.wireOp",EDGE,"E659"),sQuery(id+"F0.wireOp",EDGE,"E660"),sQuery(id+"F0.wireOp",EDGE,"E661"),sQuery(id+"F0.wireOp",EDGE,"E662"),sQuery(id+"F0.wireOp",EDGE,"E663"),sQuery(id+"F0.wireOp",EDGE,"E664"),sQuery(id+"F0.wireOp",EDGE,"E665"),sQuery(id+"F0.wireOp",EDGE,"E666"),sQuery(id+"F0.wireOp",EDGE,"E667"),sQuery(id+"F0.wireOp",EDGE,"E668"),sQuery(id+"F0.wireOp",EDGE,"E669"),sQuery(id+"F0.wireOp",EDGE,"E670"),sQuery(id+"F0.wireOp",EDGE,"E671"),sQuery(id+"F0.wireOp",EDGE,"E672"),sQuery(id+"F0.wireOp",EDGE,"E673"),sQuery(id+"F0.wireOp",EDGE,"E674"),sQuery(id+"F0.wireOp",EDGE,"E675"),sQuery(id+"F0.wireOp",EDGE,"E676"),sQuery(id+"F0.wireOp",EDGE,"E677"),sQuery(id+"F0.wireOp",EDGE,"E678"),sQuery(id+"F0.wireOp",EDGE,"E679"),sQuery(id+"F0.wireOp",EDGE,"E680"),sQuery(id+"F0.wireOp",EDGE,"E681"),sQuery(id+"F0.wireOp",EDGE,"E682"),sQuery(id+"F0.wireOp",EDGE,"E683"),sQuery(id+"F0.wireOp",EDGE,"E684"),sQuery(id+"F0.wireOp",EDGE,"E685"),sQuery(id+"F0.wireOp",EDGE,"E686"),sQuery(id+"F0.wireOp",EDGE,"E687"),sQuery(id+"F0.wireOp",EDGE,"E688"),sQuery(id+"F0.wireOp",EDGE,"E689"),sQuery(id+"F0.wireOp",EDGE,"E690"),sQuery(id+"F0.wireOp",EDGE,"E691"),sQuery(id+"F0.wireOp",EDGE,"E692"),sQuery(id+"F0.wireOp",EDGE,"E693"),sQuery(id+"F0.wireOp",EDGE,"E694"),sQuery(id+"F0.wireOp",EDGE,"E695"),sQuery(id+"F0.wireOp",EDGE,"E696"),sQuery(id+"F0.wireOp",EDGE,"E697"),sQuery(id+"F0.wireOp",EDGE,"E698"),sQuery(id+"F0.wireOp",EDGE,"E699"),sQuery(id+"F0.wireOp",EDGE,"E700"),sQuery(id+"F0.wireOp",EDGE,"E701"),sQuery(id+"F0.wireOp",EDGE,"E702"),sQuery(id+"F0.wireOp",EDGE,"E703"),sQuery(id+"F0.wireOp",EDGE,"E704"),sQuery(id+"F0.wireOp",EDGE,"E705"),sQuery(id+"F0.wireOp",EDGE,"E706"),sQuery(id+"F0.wireOp",EDGE,"E707"),sQuery(id+"F0.wireOp",EDGE,"E708"),sQuery(id+"F0.wireOp",EDGE,"E709"),sQuery(id+"F0.wireOp",EDGE,"E710"),sQuery(id+"F0.wireOp",EDGE,"E711"),sQuery(id+"F0.wireOp",EDGE,"E712"),sQuery(id+"F0.wireOp",EDGE,"E713"),sQuery(id+"F0.wireOp",EDGE,"E714"),sQuery(id+"F0.wireOp",EDGE,"E715"),sQuery(id+"F0.wireOp",EDGE,"E716"),sQuery(id+"F0.wireOp",EDGE,"E717"),sQuery(id+"F0.wireOp",EDGE,"E718"),sQuery(id+"F0.wireOp",EDGE,"E719"),sQuery(id+"F0.wireOp",EDGE,"E720"),sQuery(id+"F0.wireOp",EDGE,"E721"),sQuery(id+"F0.wireOp",EDGE,"E722"),sQuery(id+"F0.wireOp",EDGE,"E723"),sQuery(id+"F0.wireOp",EDGE,"E724"),sQuery(id+"F0.wireOp",EDGE,"E725"),sQuery(id+"F0.wireOp",EDGE,"E726"),sQuery(id+"F0.wireOp",EDGE,"E727"),sQuery(id+"F0.wireOp",EDGE,"E728"),sQuery(id+"F0.wireOp",EDGE,"E729"),sQuery(id+"F0.wireOp",EDGE,"E730"),sQuery(id+"F0.wireOp",EDGE,"E731"),sQuery(id+"F0.wireOp",EDGE,"E732"),sQuery(id+"F0.wireOp",EDGE,"E733"),sQuery(id+"F0.wireOp",EDGE,"E734"),sQuery(id+"F0.wireOp",EDGE,"E735"),sQuery(id+"F0.wireOp",EDGE,"E736"),sQuery(id+"F0.wireOp",EDGE,"E737"),sQuery(id+"F0.wireOp",EDGE,"E738"),sQuery(id+"F0.wireOp",EDGE,"E739"),sQuery(id+"F0.wireOp",EDGE,"E740"),sQuery(id+"F0.wireOp",EDGE,"E741"),sQuery(id+"F0.wireOp",EDGE,"E742"),sQuery(id+"F0.wireOp",EDGE,"E743"),sQuery(id+"F0.wireOp",EDGE,"E744"),sQuery(id+"F0.wireOp",EDGE,"E745"),sQuery(id+"F0.wireOp",EDGE,"E746"),sQuery(id+"F0.wireOp",EDGE,"E747"),sQuery(id+"F0.wireOp",EDGE,"E748"),sQuery(id+"F0.wireOp",EDGE,"E749"),sQuery(id+"F0.wireOp",EDGE,"E750"),sQuery(id+"F0.wireOp",EDGE,"E751"),sQuery(id+"F0.wireOp",EDGE,"E752"),sQuery(id+"F0.wireOp",EDGE,"E753"),sQuery(id+"F0.wireOp",EDGE,"E754"),sQuery(id+"F0.wireOp",EDGE,"E755"),sQuery(id+"F0.wireOp",EDGE,"E756"),sQuery(id+"F0.wireOp",EDGE,"E757"),sQuery(id+"F0.wireOp",EDGE,"E758"),sQuery(id+"F0.wireOp",EDGE,"E759"),sQuery(id+"F0.wireOp",EDGE,"E760"),sQuery(id+"F0.wireOp",EDGE,"E761"),sQuery(id+"F0.wireOp",EDGE,"E762"),sQuery(id+"F0.wireOp",EDGE,"E763"),sQuery(id+"F0.wireOp",EDGE,"E764"),sQuery(id+"F0.wireOp",EDGE,"E765"),sQuery(id+"F0.wireOp",EDGE,"E766"),sQuery(id+"F0.wireOp",EDGE,"E767"),sQuery(id+"F0.wireOp",EDGE,"E768"),sQuery(id+"F0.wireOp",EDGE,"E769"),sQuery(id+"F0.wireOp",EDGE,"E770"),sQuery(id+"F0.wireOp",EDGE,"E771"),sQuery(id+"F0.wireOp",EDGE,"E772"),sQuery(id+"F0.wireOp",EDGE,"E773"),sQuery(id+"F0.wireOp",EDGE,"E774"),sQuery(id+"F0.wireOp",EDGE,"E775"),sQuery(id+"F0.wireOp",EDGE,"E776"),sQuery(id+"F0.wireOp",EDGE,"E777"),sQuery(id+"F0.wireOp",EDGE,"E778"),sQuery(id+"F0.wireOp",EDGE,"E779"),sQuery(id+"F0.wireOp",EDGE,"E780"),sQuery(id+"F0.wireOp",EDGE,"E781"),sQuery(id+"F0.wireOp",EDGE,"E782"),sQuery(id+"F0.wireOp",EDGE,"E783"),sQuery(id+"F0.wireOp",EDGE,"E784"),sQuery(id+"F0.wireOp",EDGE,"E785"),sQuery(id+"F0.wireOp",EDGE,"E786"),sQuery(id+"F0.wireOp",EDGE,"E787"),sQuery(id+"F0.wireOp",EDGE,"E788"),sQuery(id+"F0.wireOp",EDGE,"E789"),sQuery(id+"F0.wireOp",EDGE,"E790"),sQuery(id+"F0.wireOp",EDGE,"E791"),sQuery(id+"F0.wireOp",EDGE,"E792"),sQuery(id+"F0.wireOp",EDGE,"E793"),sQuery(id+"F0.wireOp",EDGE,"E794"),sQuery(id+"F0.wireOp",EDGE,"E795"),sQuery(id+"F0.wireOp",EDGE,"E796"),sQuery(id+"F0.wireOp",EDGE,"E797"),sQuery(id+"F0.wireOp",EDGE,"E798"),sQuery(id+"F0.wireOp",EDGE,"E799"),sQuery(id+"F0.wireOp",EDGE,"E800"),sQuery(id+"F0.wireOp",EDGE,"E801"),sQuery(id+"F0.wireOp",EDGE,"E802"),sQuery(id+"F0.wireOp",EDGE,"E803"),sQuery(id+"F0.wireOp",EDGE,"E804"),sQuery(id+"F0.wireOp",EDGE,"E805"),sQuery(id+"F0.wireOp",EDGE,"E806"),sQuery(id+"F0.wireOp",EDGE,"E807"),sQuery(id+"F0.wireOp",EDGE,"E808"),sQuery(id+"F0.wireOp",EDGE,"E809"),sQuery(id+"F0.wireOp",EDGE,"E810"),sQuery(id+"F0.wireOp",EDGE,"E811"),sQuery(id+"F0.wireOp",EDGE,"E812"),sQuery(id+"F0.wireOp",EDGE,"E813"),sQuery(id+"F0.wireOp",EDGE,"E814"),sQuery(id+"F0.wireOp",EDGE,"E815"),sQuery(id+"F0.wireOp",EDGE,"E816"),sQuery(id+"F0.wireOp",EDGE,"E817"),sQuery(id+"F0.wireOp",EDGE,"E818"),sQuery(id+"F0.wireOp",EDGE,"E819"),sQuery(id+"F0.wireOp",EDGE,"E820"),sQuery(id+"F0.wireOp",EDGE,"E821"),sQuery(id+"F0.wireOp",EDGE,"E822"),sQuery(id+"F0.wireOp",EDGE,"E823"),sQuery(id+"F0.wireOp",EDGE,"E824"),sQuery(id+"F0.wireOp",EDGE,"E825"),sQuery(id+"F0.wireOp",EDGE,"E826"),sQuery(id+"F0.wireOp",EDGE,"E827"),sQuery(id+"F0.wireOp",EDGE,"E828"),sQuery(id+"F0.wireOp",EDGE,"E829"),sQuery(id+"F0.wireOp",EDGE,"E830"),sQuery(id+"F0.wireOp",EDGE,"E831"),sQuery(id+"F0.wireOp",EDGE,"E832"),sQuery(id+"F0.wireOp",EDGE,"E833"),sQuery(id+"F0.wireOp",EDGE,"E834"),sQuery(id+"F0.wireOp",EDGE,"E835"),sQuery(id+"F0.wireOp",EDGE,"E836"),sQuery(id+"F0.wireOp",EDGE,"E837"),sQuery(id+"F0.wireOp",EDGE,"E838"),sQuery(id+"F0.wireOp",EDGE,"E839"),sQuery(id+"F0.wireOp",EDGE,"E840"),sQuery(id+"F0.wireOp",EDGE,"E841"),sQuery(id+"F0.wireOp",EDGE,"E842"),sQuery(id+"F0.wireOp",EDGE,"E843"),sQuery(id+"F0.wireOp",EDGE,"E844"),sQuery(id+"F0.wireOp",EDGE,"E845"),sQuery(id+"F0.wireOp",EDGE,"E846"),sQuery(id+"F0.wireOp",EDGE,"E847"),sQuery(id+"F0.wireOp",EDGE,"E848"),sQuery(id+"F0.wireOp",EDGE,"E849"),sQuery(id+"F0.wireOp",EDGE,"E850"),sQuery(id+"F0.wireOp",EDGE,"E851"),sQuery(id+"F0.wireOp",EDGE,"E852"),sQuery(id+"F0.wireOp",EDGE,"E853"),sQuery(id+"F0.wireOp",EDGE,"E854"),sQuery(id+"F0.wireOp",EDGE,"E855"),sQuery(id+"F0.wireOp",EDGE,"E856"),sQuery(id+"F0.wireOp",EDGE,"E857"),sQuery(id+"F0.wireOp",EDGE,"E858"),sQuery(id+"F0.wireOp",EDGE,"E859"),sQuery(id+"F0.wireOp",EDGE,"E860"),sQuery(id+"F0.wireOp",EDGE,"E861"),sQuery(id+"F0.wireOp",EDGE,"E862"),sQuery(id+"F0.wireOp",EDGE,"E863"),sQuery(id+"F0.wireOp",EDGE,"E864"),sQuery(id+"F0.wireOp",EDGE,"E865"),sQuery(id+"F0.wireOp",EDGE,"E866"),sQuery(id+"F0.wireOp",EDGE,"E867"),sQuery(id+"F0.wireOp",EDGE,"E868"),sQuery(id+"F0.wireOp",EDGE,"E869"),sQuery(id+"F0.wireOp",EDGE,"E870"),sQuery(id+"F0.wireOp",EDGE,"E871"),sQuery(id+"F0.wireOp",EDGE,"E872"),sQuery(id+"F0.wireOp",EDGE,"E873"),sQuery(id+"F0.wireOp",EDGE,"E874"),sQuery(id+"F0.wireOp",EDGE,"E875"),sQuery(id+"F0.wireOp",EDGE,"E876"),sQuery(id+"F0.wireOp",EDGE,"E877"),sQuery(id+"F0.wireOp",EDGE,"E878"),sQuery(id+"F0.wireOp",EDGE,"E879"),sQuery(id+"F0.wireOp",EDGE,"E880"),sQuery(id+"F0.wireOp",EDGE,"E881"),sQuery(id+"F0.wireOp",EDGE,"E882"),sQuery(id+"F0.wireOp",EDGE,"E883"),sQuery(id+"F0.wireOp",EDGE,"E884"),sQuery(id+"F0.wireOp",EDGE,"E885"),sQuery(id+"F0.wireOp",EDGE,"E886"),sQuery(id+"F0.wireOp",EDGE,"E887"),sQuery(id+"F0.wireOp",EDGE,"E888"),sQuery(id+"F0.wireOp",EDGE,"E889"),sQuery(id+"F0.wireOp",EDGE,"E890"),sQuery(id+"F0.wireOp",EDGE,"E891"),sQuery(id+"F0.wireOp",EDGE,"E892"),sQuery(id+"F0.wireOp",EDGE,"E893"),sQuery(id+"F0.wireOp",EDGE,"E894"),sQuery(id+"F0.wireOp",EDGE,"E895"),sQuery(id+"F0.wireOp",EDGE,"E896"),sQuery(id+"F0.wireOp",EDGE,"E897"),sQuery(id+"F0.wireOp",EDGE,"E898"),sQuery(id+"F0.wireOp",EDGE,"E899"),sQuery(id+"F0.wireOp",EDGE,"E900"),sQuery(id+"F0.wireOp",EDGE,"E901"),sQuery(id+"F0.wireOp",EDGE,"E902"),sQuery(id+"F0.wireOp",EDGE,"E903"),sQuery(id+"F0.wireOp",EDGE,"E904"),sQuery(id+"F0.wireOp",EDGE,"E905"),sQuery(id+"F0.wireOp",EDGE,"E906"),sQuery(id+"F0.wireOp",EDGE,"E907"),sQuery(id+"F0.wireOp",EDGE,"E908"),sQuery(id+"F0.wireOp",EDGE,"E909"),sQuery(id+"F0.wireOp",EDGE,"E910"),sQuery(id+"F0.wireOp",EDGE,"E911"),sQuery(id+"F0.wireOp",EDGE,"E912"),sQuery(id+"F0.wireOp",EDGE,"E913"),sQuery(id+"F0.wireOp",EDGE,"E914"),sQuery(id+"F0.wireOp",EDGE,"E915"),sQuery(id+"F0.wireOp",EDGE,"E916"),sQuery(id+"F0.wireOp",EDGE,"E917"),sQuery(id+"F0.wireOp",EDGE,"E918"),sQuery(id+"F0.wireOp",EDGE,"E919"),sQuery(id+"F0.wireOp",EDGE,"E920"),sQuery(id+"F0.wireOp",EDGE,"E921"),sQuery(id+"F0.wireOp",EDGE,"E922"),sQuery(id+"F0.wireOp",EDGE,"E923"),sQuery(id+"F0.wireOp",EDGE,"E924"),sQuery(id+"F0.wireOp",EDGE,"E925"),sQuery(id+"F0.wireOp",EDGE,"E926"),sQuery(id+"F0.wireOp",EDGE,"E927"),sQuery(id+"F0.wireOp",EDGE,"E928"),sQuery(id+"F0.wireOp",EDGE,"E929"),sQuery(id+"F0.wireOp",EDGE,"E930"),sQuery(id+"F0.wireOp",EDGE,"E931"),sQuery(id+"F0.wireOp",EDGE,"E932"),sQuery(id+"F0.wireOp",EDGE,"E933"),sQuery(id+"F0.wireOp",EDGE,"E934"),sQuery(id+"F0.wireOp",EDGE,"E935"),sQuery(id+"F0.wireOp",EDGE,"E936"),sQuery(id+"F0.wireOp",EDGE,"E937"),sQuery(id+"F0.wireOp",EDGE,"E938"),sQuery(id+"F0.wireOp",EDGE,"E939"),sQuery(id+"F0.wireOp",EDGE,"E940"),sQuery(id+"F0.wireOp",EDGE,"E941"),sQuery(id+"F0.wireOp",EDGE,"E942"),sQuery(id+"F0.wireOp",EDGE,"E943"),sQuery(id+"F0.wireOp",EDGE,"E944"),sQuery(id+"F0.wireOp",EDGE,"E945"),sQuery(id+"F0.wireOp",EDGE,"E946"),sQuery(id+"F0.wireOp",EDGE,"E947"),sQuery(id+"F0.wireOp",EDGE,"E948"),sQuery(id+"F0.wireOp",EDGE,"E949"),sQuery(id+"F0.wireOp",EDGE,"E950"),sQuery(id+"F0.wireOp",EDGE,"E951"),sQuery(id+"F0.wireOp",EDGE,"E952"),sQuery(id+"F0.wireOp",EDGE,"E953"),sQuery(id+"F0.wireOp",EDGE,"E954"),sQuery(id+"F0.wireOp",EDGE,"E955"),sQuery(id+"F0.wireOp",EDGE,"E956"),sQuery(id+"F0.wireOp",EDGE,"E957"),sQuery(id+"F0.wireOp",EDGE,"E958"),sQuery(id+"F0.wireOp",EDGE,"E959"),sQuery(id+"F0.wireOp",EDGE,"E960"),sQuery(id+"F0.wireOp",EDGE,"E961"),sQuery(id+"F0.wireOp",EDGE,"E962"),sQuery(id+"F0.wireOp",EDGE,"E963"),sQuery(id+"F0.wireOp",EDGE,"E964"),sQuery(id+"F0.wireOp",EDGE,"E965"),sQuery(id+"F0.wireOp",EDGE,"E966"),sQuery(id+"F0.wireOp",EDGE,"E967"),sQuery(id+"F0.wireOp",EDGE,"E968"),sQuery(id+"F0.wireOp",EDGE,"E969"),sQuery(id+"F0.wireOp",EDGE,"E970"),sQuery(id+"F0.wireOp",EDGE,"E971"),sQuery(id+"F0.wireOp",EDGE,"E972"),sQuery(id+"F0.wireOp",EDGE,"E973"),sQuery(id+"F0.wireOp",EDGE,"E974"),sQuery(id+"F0.wireOp",EDGE,"E975"),sQuery(id+"F0.wireOp",EDGE,"E976"),sQuery(id+"F0.wireOp",EDGE,"E977"),sQuery(id+"F0.wireOp",EDGE,"E978"),sQuery(id+"F0.wireOp",EDGE,"E979"),sQuery(id+"F0.wireOp",EDGE,"E980"),sQuery(id+"F0.wireOp",EDGE,"E981"),sQuery(id+"F0.wireOp",EDGE,"E982"),sQuery(id+"F0.wireOp",EDGE,"E983"),sQuery(id+"F0.wireOp",EDGE,"E984"),sQuery(id+"F0.wireOp",EDGE,"E985"),sQuery(id+"F0.wireOp",EDGE,"E986"),sQuery(id+"F0.wireOp",EDGE,"E987"),sQuery(id+"F0.wireOp",EDGE,"E988"),sQuery(id+"F0.wireOp",EDGE,"E989"),sQuery(id+"F0.wireOp",EDGE,"E990"),sQuery(id+"F0.wireOp",EDGE,"E991"),sQuery(id+"F0.wireOp",EDGE,"E992"),sQuery(id+"F0.wireOp",EDGE,"E993"),sQuery(id+"F0.wireOp",EDGE,"E994"),sQuery(id+"F0.wireOp",EDGE,"E995"),sQuery(id+"F0.wireOp",EDGE,"E996"),sQuery(id+"F0.wireOp",EDGE,"E997"),sQuery(id+"F0.wireOp",EDGE,"E998"),sQuery(id+"F0.wireOp",EDGE,"E999"),sQuery(id+"F0.wireOp",EDGE,"E1000"),sQuery(id+"F0.wireOp",EDGE,"E1001"),sQuery(id+"F0.wireOp",EDGE,"E1002"),sQuery(id+"F0.wireOp",EDGE,"E1003"),sQuery(id+"F0.wireOp",EDGE,"E1004"),sQuery(id+"F0.wireOp",EDGE,"E1005"),sQuery(id+"F0.wireOp",EDGE,"E1006"),sQuery(id+"F0.wireOp",EDGE,"E1007"),sQuery(id+"F0.wireOp",EDGE,"E1008"),sQuery(id+"F0.wireOp",EDGE,"E1009"),sQuery(id+"F0.wireOp",EDGE,"E1010"),sQuery(id+"F0.wireOp",EDGE,"E1011"),sQuery(id+"F0.wireOp",EDGE,"E1012"),sQuery(id+"F0.wireOp",EDGE,"E1013"),sQuery(id+"F0.wireOp",EDGE,"E1014"),sQuery(id+"F0.wireOp",EDGE,"E1015"),sQuery(id+"F0.wireOp",EDGE,"E1016"),sQuery(id+"F0.wireOp",EDGE,"E1017"),sQuery(id+"F0.wireOp",EDGE,"E1018"),sQuery(id+"F0.wireOp",EDGE,"E1019"),sQuery(id+"F0.wireOp",EDGE,"E1020"),sQuery(id+"F0.wireOp",EDGE,"E1021"),sQuery(id+"F0.wireOp",EDGE,"E1022"),sQuery(id+"F0.wireOp",EDGE,"E1023"),sQuery(id+"F0.wireOp",EDGE,"E1024"),sQuery(id+"F0.wireOp",EDGE,"E1025"),sQuery(id+"F0.wireOp",EDGE,"E1026"),sQuery(id+"F0.wireOp",EDGE,"E1027"),sQuery(id+"F0.wireOp",EDGE,"E1028"),sQuery(id+"F0.wireOp",EDGE,"E1029"),sQuery(id+"F0.wireOp",EDGE,"E1030"),sQuery(id+"F0.wireOp",EDGE,"E1031"),sQuery(id+"F0.wireOp",EDGE,"E1032"),sQuery(id+"F0.wireOp",EDGE,"E1033"),sQuery(id+"F0.wireOp",EDGE,"E1034"),sQuery(id+"F0.wireOp",EDGE,"E1035"),sQuery(id+"F0.wireOp",EDGE,"E1036"),sQuery(id+"F0.wireOp",EDGE,"E1037"),sQuery(id+"F0.wireOp",EDGE,"E1038"),sQuery(id+"F0.wireOp",EDGE,"E1039"),sQuery(id+"F0.wireOp",EDGE,"E1040"),sQuery(id+"F0.wireOp",EDGE,"E1041"),sQuery(id+"F0.wireOp",EDGE,"E1042"),sQuery(id+"F0.wireOp",EDGE,"E1043"),sQuery(id+"F0.wireOp",EDGE,"E1044"),sQuery(id+"F0.wireOp",EDGE,"E1045"),sQuery(id+"F0.wireOp",EDGE,"E1046"),sQuery(id+"F0.wireOp",EDGE,"E1047"),sQuery(id+"F0.wireOp",EDGE,"E1048"),sQuery(id+"F0.wireOp",EDGE,"E1049"),sQuery(id+"F0.wireOp",EDGE,"E1050"),sQuery(id+"F0.wireOp",EDGE,"E1051"),sQuery(id+"F0.wireOp",EDGE,"E1052"),sQuery(id+"F0.wireOp",EDGE,"E1053"),sQuery(id+"F0.wireOp",EDGE,"E1054"),sQuery(id+"F0.wireOp",EDGE,"E1055"),sQuery(id+"F0.wireOp",EDGE,"E1056"),sQuery(id+"F0.wireOp",EDGE,"E1057"),sQuery(id+"F0.wireOp",EDGE,"E1058"),sQuery(id+"F0.wireOp",EDGE,"E1059"),sQuery(id+"F0.wireOp",EDGE,"E1060"),sQuery(id+"F0.wireOp",EDGE,"E1061"),sQuery(id+"F0.wireOp",EDGE,"E1062"),sQuery(id+"F0.wireOp",EDGE,"E1063"),sQuery(id+"F0.wireOp",EDGE,"E1064"),sQuery(id+"F0.wireOp",EDGE,"E1065"),sQuery(id+"F0.wireOp",EDGE,"E1066"),sQuery(id+"F0.wireOp",EDGE,"E1067"),sQuery(id+"F0.wireOp",EDGE,"E1068"),sQuery(id+"F0.wireOp",EDGE,"E1069"),sQuery(id+"F0.wireOp",EDGE,"E1070"),sQuery(id+"F0.wireOp",EDGE,"E1071"),sQuery(id+"F0.wireOp",EDGE,"E1072"),sQuery(id+"F0.wireOp",EDGE,"E1073"),sQuery(id+"F0.wireOp",EDGE,"E1074"),sQuery(id+"F0.wireOp",EDGE,"E1075"),sQuery(id+"F0.wireOp",EDGE,"E1076"),sQuery(id+"F0.wireOp",EDGE,"E1077"),sQuery(id+"F0.wireOp",EDGE,"E1078"),sQuery(id+"F0.wireOp",EDGE,"E1079"),sQuery(id+"F0.wireOp",EDGE,"E1080"),sQuery(id+"F0.wireOp",EDGE,"E1081"),sQuery(id+"F0.wireOp",EDGE,"E1082"),sQuery(id+"F0.wireOp",EDGE,"E1083"),sQuery(id+"F0.wireOp",EDGE,"E1084"),sQuery(id+"F0.wireOp",EDGE,"E1085"),sQuery(id+"F0.wireOp",EDGE,"E1086"),sQuery(id+"F0.wireOp",EDGE,"E1087"),sQuery(id+"F0.wireOp",EDGE,"E1088"),sQuery(id+"F0.wireOp",EDGE,"E1089"),sQuery(id+"F0.wireOp",EDGE,"E1090"),sQuery(id+"F0.wireOp",EDGE,"E1091"),sQuery(id+"F0.wireOp",EDGE,"E1092"),sQuery(id+"F0.wireOp",EDGE,"E1093"),sQuery(id+"F0.wireOp",EDGE,"E1094"),sQuery(id+"F0.wireOp",EDGE,"E1095"),sQuery(id+"F0.wireOp",EDGE,"E1096"),sQuery(id+"F0.wireOp",EDGE,"E1097"),sQuery(id+"F0.wireOp",EDGE,"E1098"),sQuery(id+"F0.wireOp",EDGE,"E1099"),sQuery(id+"F0.wireOp",EDGE,"E1100"),sQuery(id+"F0.wireOp",EDGE,"E1101"),sQuery(id+"F0.wireOp",EDGE,"E1102"),sQuery(id+"F0.wireOp",EDGE,"E1103"),sQuery(id+"F0.wireOp",EDGE,"E1104"),sQuery(id+"F0.wireOp",EDGE,"E1105"),sQuery(id+"F0.wireOp",EDGE,"E1106"),sQuery(id+"F0.wireOp",EDGE,"E1107"),sQuery(id+"F0.wireOp",EDGE,"E1108"),sQuery(id+"F0.wireOp",EDGE,"E1109"),sQuery(id+"F0.wireOp",EDGE,"E1110"),sQuery(id+"F0.wireOp",EDGE,"E1111"),sQuery(id+"F0.wireOp",EDGE,"E1112"),sQuery(id+"F0.wireOp",EDGE,"E1113"),sQuery(id+"F0.wireOp",EDGE,"E1114"),sQuery(id+"F0.wireOp",EDGE,"E1115"),sQuery(id+"F0.wireOp",EDGE,"E1116"),sQuery(id+"F0.wireOp",EDGE,"E1117"),sQuery(id+"F0.wireOp",EDGE,"E1118"),sQuery(id+"F0.wireOp",EDGE,"E1119"),sQuery(id+"F0.wireOp",EDGE,"E1120"),sQuery(id+"F0.wireOp",EDGE,"E1121"),sQuery(id+"F0.wireOp",EDGE,"E1122"),sQuery(id+"F0.wireOp",EDGE,"E1123"),sQuery(id+"F0.wireOp",EDGE,"E1124"),sQuery(id+"F0.wireOp",EDGE,"E1125"),sQuery(id+"F0.wireOp",EDGE,"E1126"),sQuery(id+"F0.wireOp",EDGE,"E1127"),sQuery(id+"F0.wireOp",EDGE,"E1128"),sQuery(id+"F0.wireOp",EDGE,"E1129"),sQuery(id+"F0.wireOp",EDGE,"E1130"),sQuery(id+"F0.wireOp",EDGE,"E1131"),sQuery(id+"F0.wireOp",EDGE,"E1132"),sQuery(id+"F0.wireOp",EDGE,"E1133"),sQuery(id+"F0.wireOp",EDGE,"E1134"),sQuery(id+"F0.wireOp",EDGE,"E1135"),sQuery(id+"F0.wireOp",EDGE,"E1136"),sQuery(id+"F0.wireOp",EDGE,"E1137"),sQuery(id+"F0.wireOp",EDGE,"E1138"),sQuery(id+"F0.wireOp",EDGE,"E1139"),sQuery(id+"F0.wireOp",EDGE,"E1140"),sQuery(id+"F0.wireOp",EDGE,"E1141"),sQuery(id+"F0.wireOp",EDGE,"E1142"),sQuery(id+"F0.wireOp",EDGE,"E1143"),sQuery(id+"F0.wireOp",EDGE,"E1144"),sQuery(id+"F0.wireOp",EDGE,"E1145"),sQuery(id+"F0.wireOp",EDGE,"E1146"),sQuery(id+"F0.wireOp",EDGE,"E1147"),sQuery(id+"F0.wireOp",EDGE,"E1148"),sQuery(id+"F0.wireOp",EDGE,"E1149"),sQuery(id+"F0.wireOp",EDGE,"E1150"),sQuery(id+"F0.wireOp",EDGE,"E1151"),sQuery(id+"F0.wireOp",EDGE,"E1152"),sQuery(id+"F0.wireOp",EDGE,"E1153"),sQuery(id+"F0.wireOp",EDGE,"E1154"),sQuery(id+"F0.wireOp",EDGE,"E1155"),sQuery(id+"F0.wireOp",EDGE,"E1156"),sQuery(id+"F0.wireOp",EDGE,"E1157"),sQuery(id+"F0.wireOp",EDGE,"E1158"),sQuery(id+"F0.wireOp",EDGE,"E1159"),sQuery(id+"F0.wireOp",EDGE,"E1160"),sQuery(id+"F0.wireOp",EDGE,"E1161"),sQuery(id+"F0.wireOp",EDGE,"E1162"),sQuery(id+"F0.wireOp",EDGE,"E1163"),sQuery(id+"F0.wireOp",EDGE,"E1164"),sQuery(id+"F0.wireOp",EDGE,"E1165"),sQuery(id+"F0.wireOp",EDGE,"E1166"),sQuery(id+"F0.wireOp",EDGE,"E1167"),sQuery(id+"F0.wireOp",EDGE,"E1168"),sQuery(id+"F0.wireOp",EDGE,"E1169"),sQuery(id+"F0.wireOp",EDGE,"E1170"),sQuery(id+"F0.wireOp",EDGE,"E1171"),sQuery(id+"F0.wireOp",EDGE,"E1172"),sQuery(id+"F0.wireOp",EDGE,"E1173"),sQuery(id+"F0.wireOp",EDGE,"E1174"),sQuery(id+"F0.wireOp",EDGE,"E1175"),sQuery(id+"F0.wireOp",EDGE,"E1176"),sQuery(id+"F0.wireOp",EDGE,"E1177"),sQuery(id+"F0.wireOp",EDGE,"E1178"),sQuery(id+"F0.wireOp",EDGE,"E1179"),sQuery(id+"F0.wireOp",EDGE,"E1180"),sQuery(id+"F0.wireOp",EDGE,"E1181"),sQuery(id+"F0.wireOp",EDGE,"E1182"),sQuery(id+"F0.wireOp",EDGE,"E1183"),sQuery(id+"F0.wireOp",EDGE,"E1184"),sQuery(id+"F0.wireOp",EDGE,"E1185"),sQuery(id+"F0.wireOp",EDGE,"E1186"),sQuery(id+"F0.wireOp",EDGE,"E1187"),sQuery(id+"F0.wireOp",EDGE,"E1188"),sQuery(id+"F0.wireOp",EDGE,"E1189"),sQuery(id+"F0.wireOp",EDGE,"E1190"),sQuery(id+"F0.wireOp",EDGE,"E1191"),sQuery(id+"F0.wireOp",EDGE,"E1192"),sQuery(id+"F0.wireOp",EDGE,"E1193"),sQuery(id+"F0.wireOp",EDGE,"E1194"),sQuery(id+"F0.wireOp",EDGE,"E1195"),sQuery(id+"F0.wireOp",EDGE,"E1196"),sQuery(id+"F0.wireOp",EDGE,"E1197"),sQuery(id+"F0.wireOp",EDGE,"E1198"),sQuery(id+"F0.wireOp",EDGE,"E1199"),sQuery(id+"F0.wireOp",EDGE,"E1200"),sQuery(id+"F0.wireOp",EDGE,"E1201"),sQuery(id+"F0.wireOp",EDGE,"E1202"),sQuery(id+"F0.wireOp",EDGE,"E1203"),sQuery(id+"F0.wireOp",EDGE,"E1204"),sQuery(id+"F0.wireOp",EDGE,"E1205"),sQuery(id+"F0.wireOp",EDGE,"E1206"),sQuery(id+"F0.wireOp",EDGE,"E1207"),sQuery(id+"F0.wireOp",EDGE,"E1208"),sQuery(id+"F0.wireOp",EDGE,"E1209"),sQuery(id+"F0.wireOp",EDGE,"E1210"),sQuery(id+"F0.wireOp",EDGE,"E1211"),sQuery(id+"F0.wireOp",EDGE,"E1212"),sQuery(id+"F0.wireOp",EDGE,"E1213"),sQuery(id+"F0.wireOp",EDGE,"E1214"),sQuery(id+"F0.wireOp",EDGE,"E1215"),sQuery(id+"F0.wireOp",EDGE,"E1216"),sQuery(id+"F0.wireOp",EDGE,"E1217"),sQuery(id+"F0.wireOp",EDGE,"E1218"),sQuery(id+"F0.wireOp",EDGE,"E1219"),sQuery(id+"F0.wireOp",EDGE,"E1220"),sQuery(id+"F0.wireOp",EDGE,"E1221"),sQuery(id+"F0.wireOp",EDGE,"E1222"),sQuery(id+"F0.wireOp",EDGE,"E1223"),sQuery(id+"F0.wireOp",EDGE,"E1224"),sQuery(id+"F0.wireOp",EDGE,"E1225"),sQuery(id+"F0.wireOp",EDGE,"E1226"),sQuery(id+"F0.wireOp",EDGE,"E1227"),sQuery(id+"F0.wireOp",EDGE,"E1228"),sQuery(id+"F0.wireOp",EDGE,"E1229"),sQuery(id+"F0.wireOp",EDGE,"E1230"),sQuery(id+"F0.wireOp",EDGE,"E1231"),sQuery(id+"F0.wireOp",EDGE,"E1232"),sQuery(id+"F0.wireOp",EDGE,"E1233"),sQuery(id+"F0.wireOp",EDGE,"E1234"),sQuery(id+"F0.wireOp",EDGE,"E1235"),sQuery(id+"F0.wireOp",EDGE,"E1236"),sQuery(id+"F0.wireOp",EDGE,"E1237"),sQuery(id+"F0.wireOp",EDGE,"E1238"),sQuery(id+"F0.wireOp",EDGE,"E1239"),sQuery(id+"F0.wireOp",EDGE,"E1240"),sQuery(id+"F0.wireOp",EDGE,"E1241"),sQuery(id+"F0.wireOp",EDGE,"E1242"),sQuery(id+"F0.wireOp",EDGE,"E1243"),sQuery(id+"F0.wireOp",EDGE,"E1244"),sQuery(id+"F0.wireOp",EDGE,"E1245"),sQuery(id+"F0.wireOp",EDGE,"E1246"),sQuery(id+"F0.wireOp",EDGE,"E1247"),sQuery(id+"F0.wireOp",EDGE,"E1248"),sQuery(id+"F0.wireOp",EDGE,"E1249"),sQuery(id+"F0.wireOp",EDGE,"E1250"),sQuery(id+"F0.wireOp",EDGE,"E1251"),sQuery(id+"F0.wireOp",EDGE,"E1252"),sQuery(id+"F0.wireOp",EDGE,"E1253"),sQuery(id+"F0.wireOp",EDGE,"E1254"),sQuery(id+"F0.wireOp",EDGE,"E1255"),sQuery(id+"F0.wireOp",EDGE,"E1256"),sQuery(id+"F0.wireOp",EDGE,"E1257"),sQuery(id+"F0.wireOp",EDGE,"E1258"),sQuery(id+"F0.wireOp",EDGE,"E1259"),sQuery(id+"F0.wireOp",EDGE,"E1260"),sQuery(id+"F0.wireOp",EDGE,"E1261"),sQuery(id+"F0.wireOp",EDGE,"E1262"),sQuery(id+"F0.wireOp",EDGE,"E1263"),sQuery(id+"F0.wireOp",EDGE,"E1264"),sQuery(id+"F0.wireOp",EDGE,"E1265"),sQuery(id+"F0.wireOp",EDGE,"E1266"),sQuery(id+"F0.wireOp",EDGE,"E1267"),sQuery(id+"F0.wireOp",EDGE,"E1268"),sQuery(id+"F0.wireOp",EDGE,"E1269"),sQuery(id+"F0.wireOp",EDGE,"E1270"),sQuery(id+"F0.wireOp",EDGE,"E1271"),sQuery(id+"F0.wireOp",EDGE,"E1272"),sQuery(id+"F0.wireOp",EDGE,"E1273"),sQuery(id+"F0.wireOp",EDGE,"E1274"),sQuery(id+"F0.wireOp",EDGE,"E1275"),sQuery(id+"F0.wireOp",EDGE,"E1276"),sQuery(id+"F0.wireOp",EDGE,"E1277"),sQuery(id+"F0.wireOp",EDGE,"E1278"),sQuery(id+"F0.wireOp",EDGE,"E1279"),sQuery(id+"F0.wireOp",EDGE,"E1280"),sQuery(id+"F0.wireOp",EDGE,"E1281"),sQuery(id+"F0.wireOp",EDGE,"E1282"),sQuery(id+"F0.wireOp",EDGE,"E1283"),sQuery(id+"F0.wireOp",EDGE,"E1284"),sQuery(id+"F0.wireOp",EDGE,"E1285"),sQuery(id+"F0.wireOp",EDGE,"E1286"),sQuery(id+"F0.wireOp",EDGE,"E1287"),sQuery(id+"F0.wireOp",EDGE,"E1288"),sQuery(id+"F0.wireOp",EDGE,"E1289"),sQuery(id+"F0.wireOp",EDGE,"E1290"),sQuery(id+"F0.wireOp",EDGE,"E1291"),sQuery(id+"F0.wireOp",EDGE,"E1292"),sQuery(id+"F0.wireOp",EDGE,"E1293"),sQuery(id+"F0.wireOp",EDGE,"E1294"),sQuery(id+"F0.wireOp",EDGE,"E1295"),sQuery(id+"F0.wireOp",EDGE,"E1296"),sQuery(id+"F0.wireOp",EDGE,"E1297"),sQuery(id+"F0.wireOp",EDGE,"E1298"),sQuery(id+"F0.wireOp",EDGE,"E1299"),sQuery(id+"F0.wireOp",EDGE,"E1300"),sQuery(id+"F0.wireOp",EDGE,"E1301"),sQuery(id+"F0.wireOp",EDGE,"E1302"),sQuery(id+"F0.wireOp",EDGE,"E1303"),sQuery(id+"F0.wireOp",EDGE,"E1304"),sQuery(id+"F0.wireOp",EDGE,"E1305"),sQuery(id+"F0.wireOp",EDGE,"E1306"),sQuery(id+"F0.wireOp",EDGE,"E1307"),sQuery(id+"F0.wireOp",EDGE,"E1308"),sQuery(id+"F0.wireOp",EDGE,"E1309"),sQuery(id+"F0.wireOp",EDGE,"E1310"),sQuery(id+"F0.wireOp",EDGE,"E1311"),sQuery(id+"F0.wireOp",EDGE,"E1312"),sQuery(id+"F0.wireOp",EDGE,"E1313"),sQuery(id+"F0.wireOp",EDGE,"E1314"),sQuery(id+"F0.wireOp",EDGE,"E1315"),sQuery(id+"F0.wireOp",EDGE,"E1316"),sQuery(id+"F0.wireOp",EDGE,"E1317"),sQuery(id+"F0.wireOp",EDGE,"E1318"),sQuery(id+"F0.wireOp",EDGE,"E1319"),sQuery(id+"F0.wireOp",EDGE,"E1320"),sQuery(id+"F0.wireOp",EDGE,"E1321"),sQuery(id+"F0.wireOp",EDGE,"E1322"),sQuery(id+"F0.wireOp",EDGE,"E1323"),sQuery(id+"F0.wireOp",EDGE,"E1324"),sQuery(id+"F0.wireOp",EDGE,"E1325"),sQuery(id+"F0.wireOp",EDGE,"E1326"),sQuery(id+"F0.wireOp",EDGE,"E1327"),sQuery(id+"F0.wireOp",EDGE,"E1328"),sQuery(id+"F0.wireOp",EDGE,"E1329"),sQuery(id+"F0.wireOp",EDGE,"E1330"),sQuery(id+"F0.wireOp",EDGE,"E1331"),sQuery(id+"F0.wireOp",EDGE,"E1332"),sQuery(id+"F0.wireOp",EDGE,"E1333"),sQuery(id+"F0.wireOp",EDGE,"E1334"),sQuery(id+"F0.wireOp",EDGE,"E1335"),sQuery(id+"F0.wireOp",EDGE,"E1336"),sQuery(id+"F0.wireOp",EDGE,"E1337"),sQuery(id+"F0.wireOp",EDGE,"E1338"),sQuery(id+"F0.wireOp",EDGE,"E1339"),sQuery(id+"F0.wireOp",EDGE,"E1340"),sQuery(id+"F0.wireOp",EDGE,"E1341"),sQuery(id+"F0.wireOp",EDGE,"E1342"),sQuery(id+"F0.wireOp",EDGE,"E1343"),sQuery(id+"F0.wireOp",EDGE,"E1344"),sQuery(id+"F0.wireOp",EDGE,"E1345"),sQuery(id+"F0.wireOp",EDGE,"E1346"),sQuery(id+"F0.wireOp",EDGE,"E1347"),sQuery(id+"F0.wireOp",EDGE,"E1348"),sQuery(id+"F0.wireOp",EDGE,"E1349"),sQuery(id+"F0.wireOp",EDGE,"E1350"),sQuery(id+"F0.wireOp",EDGE,"E1351"),sQuery(id+"F0.wireOp",EDGE,"E1352"),sQuery(id+"F0.wireOp",EDGE,"E1353"),sQuery(id+"F0.wireOp",EDGE,"E1354"),sQuery(id+"F0.wireOp",EDGE,"E1355"),sQuery(id+"F0.wireOp",EDGE,"E1356"),sQuery(id+"F0.wireOp",EDGE,"E1357"),sQuery(id+"F0.wireOp",EDGE,"E1358"),sQuery(id+"F0.wireOp",EDGE,"E1359"),sQuery(id+"F0.wireOp",EDGE,"E1360"),sQuery(id+"F0.wireOp",EDGE,"E1361"),sQuery(id+"F0.wireOp",EDGE,"E1362"),sQuery(id+"F0.wireOp",EDGE,"E1363"),sQuery(id+"F0.wireOp",EDGE,"E1364"),sQuery(id+"F0.wireOp",EDGE,"E1365"),sQuery(id+"F0.wireOp",EDGE,"E1366"),sQuery(id+"F0.wireOp",EDGE,"E1367"),sQuery(id+"F0.wireOp",EDGE,"E1368"),sQuery(id+"F0.wireOp",EDGE,"E1369"),sQuery(id+"F0.wireOp",EDGE,"E1370"),sQuery(id+"F0.wireOp",EDGE,"E1371"),sQuery(id+"F0.wireOp",EDGE,"E1372"),sQuery(id+"F0.wireOp",EDGE,"E1373"),sQuery(id+"F0.wireOp",EDGE,"E1374"),sQuery(id+"F0.wireOp",EDGE,"E1375"),sQuery(id+"F0.wireOp",EDGE,"E1376"),sQuery(id+"F0.wireOp",EDGE,"E1377"),sQuery(id+"F0.wireOp",EDGE,"E1378"),sQuery(id+"F0.wireOp",EDGE,"E1379"),sQuery(id+"F0.wireOp",EDGE,"E1380"),sQuery(id+"F0.wireOp",EDGE,"E1381"),sQuery(id+"F0.wireOp",EDGE,"E1382"),sQuery(id+"F0.wireOp",EDGE,"E1383"),sQuery(id+"F0.wireOp",EDGE,"E1384"),sQuery(id+"F0.wireOp",EDGE,"E1385"),sQuery(id+"F0.wireOp",EDGE,"E1386"),sQuery(id+"F0.wireOp",EDGE,"E1387"),sQuery(id+"F0.wireOp",EDGE,"E1388"),sQuery(id+"F0.wireOp",EDGE,"E1389"),sQuery(id+"F0.wireOp",EDGE,"E1390"),sQuery(id+"F0.wireOp",EDGE,"E1391"),sQuery(id+"F0.wireOp",EDGE,"E1392"),sQuery(id+"F0.wireOp",EDGE,"E1393"),sQuery(id+"F0.wireOp",EDGE,"E1394"),sQuery(id+"F0.wireOp",EDGE,"E1395"),sQuery(id+"F0.wireOp",EDGE,"E1396"),sQuery(id+"F0.wireOp",EDGE,"E1397"),sQuery(id+"F0.wireOp",EDGE,"E1398"),sQuery(id+"F0.wireOp",EDGE,"E1399"),sQuery(id+"F0.wireOp",EDGE,"E1400"),sQuery(id+"F0.wireOp",EDGE,"E1401"),sQuery(id+"F0.wireOp",EDGE,"E1402"),sQuery(id+"F0.wireOp",EDGE,"E1403"),sQuery(id+"F0.wireOp",EDGE,"E1404"),sQuery(id+"F0.wireOp",EDGE,"E1405"),sQuery(id+"F0.wireOp",EDGE,"E1406"),sQuery(id+"F0.wireOp",EDGE,"E1407"),sQuery(id+"F0.wireOp",EDGE,"E1408"),sQuery(id+"F0.wireOp",EDGE,"E1409"),sQuery(id+"F0.wireOp",EDGE,"E1410"),sQuery(id+"F0.wireOp",EDGE,"E1411"),sQuery(id+"F0.wireOp",EDGE,"E1412"),sQuery(id+"F0.wireOp",EDGE,"E1413"),sQuery(id+"F0.wireOp",EDGE,"E1414"),sQuery(id+"F0.wireOp",EDGE,"E1415"),sQuery(id+"F0.wireOp",EDGE,"E1416"),sQuery(id+"F0.wireOp",EDGE,"E1417"),sQuery(id+"F0.wireOp",EDGE,"E1418"),sQuery(id+"F0.wireOp",EDGE,"E1419"),sQuery(id+"F0.wireOp",EDGE,"E1420"),sQuery(id+"F0.wireOp",EDGE,"E1421"),sQuery(id+"F0.wireOp",EDGE,"E1422"),sQuery(id+"F0.wireOp",EDGE,"E1423"),sQuery(id+"F0.wireOp",EDGE,"E1424"),sQuery(id+"F0.wireOp",EDGE,"E1425"),sQuery(id+"F0.wireOp",EDGE,"E1426"),sQuery(id+"F0.wireOp",EDGE,"E1427"),sQuery(id+"F0.wireOp",EDGE,"E1428"),sQuery(id+"F0.wireOp",EDGE,"E1429"),sQuery(id+"F0.wireOp",EDGE,"E1430"),sQuery(id+"F0.wireOp",EDGE,"E1431"),sQuery(id+"F0.wireOp",EDGE,"E1432"),sQuery(id+"F0.wireOp",EDGE,"E1433"),sQuery(id+"F0.wireOp",EDGE,"E1434"),sQuery(id+"F0.wireOp",EDGE,"E1435"),sQuery(id+"F0.wireOp",EDGE,"E1436"),sQuery(id+"F0.wireOp",EDGE,"E1437"),sQuery(id+"F0.wireOp",EDGE,"E1438"),sQuery(id+"F0.wireOp",EDGE,"E1439"),sQuery(id+"F0.wireOp",EDGE,"E1440"),sQuery(id+"F0.wireOp",EDGE,"E1441"),sQuery(id+"F0.wireOp",EDGE,"E1442"),sQuery(id+"F0.wireOp",EDGE,"E1443"),sQuery(id+"F0.wireOp",EDGE,"E1444"),sQuery(id+"F0.wireOp",EDGE,"E1445"),sQuery(id+"F0.wireOp",EDGE,"E1446"),sQuery(id+"F0.wireOp",EDGE,"E1447"),sQuery(id+"F0.wireOp",EDGE,"E1448"),sQuery(id+"F0.wireOp",EDGE,"E1449"),sQuery(id+"F0.wireOp",EDGE,"E1450"),sQuery(id+"F0.wireOp",EDGE,"E1451"),sQuery(id+"F0.wireOp",EDGE,"E1452"),sQuery(id+"F0.wireOp",EDGE,"E1453"),sQuery(id+"F0.wireOp",EDGE,"E1454"),sQuery(id+"F0.wireOp",EDGE,"E1455"),sQuery(id+"F0.wireOp",EDGE,"E1456"),sQuery(id+"F0.wireOp",EDGE,"E1457"),sQuery(id+"F0.wireOp",EDGE,"E1458"),sQuery(id+"F0.wireOp",EDGE,"E1459"),sQuery(id+"F0.wireOp",EDGE,"E1460"),sQuery(id+"F0.wireOp",EDGE,"E1461"),sQuery(id+"F0.wireOp",EDGE,"E1462"),sQuery(id+"F0.wireOp",EDGE,"E1463"),sQuery(id+"F0.wireOp",EDGE,"E1464"),sQuery(id+"F0.wireOp",EDGE,"E1465"),sQuery(id+"F0.wireOp",EDGE,"E1466"),sQuery(id+"F0.wireOp",EDGE,"E1467"),sQuery(id+"F0.wireOp",EDGE,"E1468"),sQuery(id+"F0.wireOp",EDGE,"E1469"),sQuery(id+"F0.wireOp",EDGE,"E1470"),sQuery(id+"F0.wireOp",EDGE,"E1471"),sQuery(id+"F0.wireOp",EDGE,"E1472"),sQuery(id+"F0.wireOp",EDGE,"E1473"),sQuery(id+"F0.wireOp",EDGE,"E1474"),sQuery(id+"F0.wireOp",EDGE,"E1475"),sQuery(id+"F0.wireOp",EDGE,"E1476"),sQuery(id+"F0.wireOp",EDGE,"E1477"),sQuery(id+"F0.wireOp",EDGE,"E1478"),sQuery(id+"F0.wireOp",EDGE,"E1479"),sQuery(id+"F0.wireOp",EDGE,"E1480"),sQuery(id+"F0.wireOp",EDGE,"E1481"),sQuery(id+"F0.wireOp",EDGE,"E1482"),sQuery(id+"F0.wireOp",EDGE,"E1483"),sQuery(id+"F0.wireOp",EDGE,"E1484"),sQuery(id+"F0.wireOp",EDGE,"E1485"),sQuery(id+"F0.wireOp",EDGE,"E1486"),sQuery(id+"F0.wireOp",EDGE,"E1487"),sQuery(id+"F0.wireOp",EDGE,"E1488"),sQuery(id+"F0.wireOp",EDGE,"E1489"),sQuery(id+"F0.wireOp",EDGE,"E1490"),sQuery(id+"F0.wireOp",EDGE,"E1491"),sQuery(id+"F0.wireOp",EDGE,"E1492"),sQuery(id+"F0.wireOp",EDGE,"E1493"),sQuery(id+"F0.wireOp",EDGE,"E1494"),sQuery(id+"F0.wireOp",EDGE,"E1495"),sQuery(id+"F0.wireOp",EDGE,"E1496"),sQuery(id+"F0.wireOp",EDGE,"E1497"),sQuery(id+"F0.wireOp",EDGE,"E1498"),sQuery(id+"F0.wireOp",EDGE,"E1499"),sQuery(id+"F0.wireOp",EDGE,"E1500"),sQuery(id+"F0.wireOp",EDGE,"E1501"),sQuery(id+"F0.wireOp",EDGE,"E1502"),sQuery(id+"F0.wireOp",EDGE,"E1503"),sQuery(id+"F0.wireOp",EDGE,"E1504"),sQuery(id+"F0.wireOp",EDGE,"E1505"),sQuery(id+"F0.wireOp",EDGE,"E1506"),sQuery(id+"F0.wireOp",EDGE,"E1507"),sQuery(id+"F0.wireOp",EDGE,"E1508"),sQuery(id+"F0.wireOp",EDGE,"E1509"),sQuery(id+"F0.wireOp",EDGE,"E1510"),sQuery(id+"F0.wireOp",EDGE,"E1511"),sQuery(id+"F0.wireOp",EDGE,"E1512"),sQuery(id+"F0.wireOp",EDGE,"E1513"),sQuery(id+"F0.wireOp",EDGE,"E1514"),sQuery(id+"F0.wireOp",EDGE,"E1515"),sQuery(id+"F0.wireOp",EDGE,"E1516"),sQuery(id+"F0.wireOp",EDGE,"E1517"),sQuery(id+"F0.wireOp",EDGE,"E1518"),sQuery(id+"F0.wireOp",EDGE,"E1519"),sQuery(id+"F0.wireOp",EDGE,"E1520"),sQuery(id+"F0.wireOp",EDGE,"E1521"),sQuery(id+"F0.wireOp",EDGE,"E1522"),sQuery(id+"F0.wireOp",EDGE,"E1523"),sQuery(id+"F0.wireOp",EDGE,"E1524"),sQuery(id+"F0.wireOp",EDGE,"E1525"),sQuery(id+"F0.wireOp",EDGE,"E1526"),sQuery(id+"F0.wireOp",EDGE,"E1527"),sQuery(id+"F0.wireOp",EDGE,"E1528"),sQuery(id+"F0.wireOp",EDGE,"E1529"),sQuery(id+"F0.wireOp",EDGE,"E1530"),sQuery(id+"F0.wireOp",EDGE,"E1531"),sQuery(id+"F0.wireOp",EDGE,"E1532"),sQuery(id+"F0.wireOp",EDGE,"E1533"),sQuery(id+"F0.wireOp",EDGE,"E1534"),sQuery(id+"F0.wireOp",EDGE,"E1535"),sQuery(id+"F0.wireOp",EDGE,"E1536"),sQuery(id+"F0.wireOp",EDGE,"E1537"),sQuery(id+"F0.wireOp",EDGE,"E1538"),sQuery(id+"F0.wireOp",EDGE,"E1539"),sQuery(id+"F0.wireOp",EDGE,"E1540"),sQuery(id+"F0.wireOp",EDGE,"E1541"),sQuery(id+"F0.wireOp",EDGE,"E1542"),sQuery(id+"F0.wireOp",EDGE,"E1543"),sQuery(id+"F0.wireOp",EDGE,"E1544"),sQuery(id+"F0.wireOp",EDGE,"E1545"),sQuery(id+"F0.wireOp",EDGE,"E1546"),sQuery(id+"F0.wireOp",EDGE,"E1547"),sQuery(id+"F0.wireOp",EDGE,"E1548"),sQuery(id+"F0.wireOp",EDGE,"E1549"),sQuery(id+"F0.wireOp",EDGE,"E1550"),sQuery(id+"F0.wireOp",EDGE,"E1551"),sQuery(id+"F0.wireOp",EDGE,"E1552"),sQuery(id+"F0.wireOp",EDGE,"E1553"),sQuery(id+"F0.wireOp",EDGE,"E1554"),sQuery(id+"F0.wireOp",EDGE,"E1555"),sQuery(id+"F0.wireOp",EDGE,"E1556"),sQuery(id+"F0.wireOp",EDGE,"E1557"),sQuery(id+"F0.wireOp",EDGE,"E1558"),sQuery(id+"F0.wireOp",EDGE,"E1559"),sQuery(id+"F0.wireOp",EDGE,"E1560"),sQuery(id+"F0.wireOp",EDGE,"E1561"),sQuery(id+"F0.wireOp",EDGE,"E1562"),sQuery(id+"F0.wireOp",EDGE,"E1563"),sQuery(id+"F0.wireOp",EDGE,"E1564"),sQuery(id+"F0.wireOp",EDGE,"E1565"),sQuery(id+"F0.wireOp",EDGE,"E1566"),sQuery(id+"F0.wireOp",EDGE,"E1567"),sQuery(id+"F0.wireOp",EDGE,"E1568"),sQuery(id+"F0.wireOp",EDGE,"E1569"),sQuery(id+"F0.wireOp",EDGE,"E1570"),sQuery(id+"F0.wireOp",EDGE,"E1571"),sQuery(id+"F0.wireOp",EDGE,"E1572"),sQuery(id+"F0.wireOp",EDGE,"E1573"),sQuery(id+"F0.wireOp",EDGE,"E1574"),sQuery(id+"F0.wireOp",EDGE,"E1575"),sQuery(id+"F0.wireOp",EDGE,"E1576"),sQuery(id+"F0.wireOp",EDGE,"E1577"),sQuery(id+"F0.wireOp",EDGE,"E1578"),sQuery(id+"F0.wireOp",EDGE,"E1579"),sQuery(id+"F0.wireOp",EDGE,"E1580"),sQuery(id+"F0.wireOp",EDGE,"E1581"),sQuery(id+"F0.wireOp",EDGE,"E1582"),sQuery(id+"F0.wireOp",EDGE,"E1583"),sQuery(id+"F0.wireOp",EDGE,"E1584"),sQuery(id+"F0.wireOp",EDGE,"E1585"),sQuery(id+"F0.wireOp",EDGE,"E1586"),sQuery(id+"F0.wireOp",EDGE,"E1587"),sQuery(id+"F0.wireOp",EDGE,"E1588"),sQuery(id+"F0.wireOp",EDGE,"E1589"),sQuery(id+"F0.wireOp",EDGE,"E1590"),sQuery(id+"F0.wireOp",EDGE,"E1591"),sQuery(id+"F0.wireOp",EDGE,"E1592"),sQuery(id+"F0.wireOp",EDGE,"E1593"),sQuery(id+"F0.wireOp",EDGE,"E1594"),sQuery(id+"F0.wireOp",EDGE,"E1595"),sQuery(id+"F0.wireOp",EDGE,"E1596"),sQuery(id+"F0.wireOp",EDGE,"E1597"),sQuery(id+"F0.wireOp",EDGE,"E1598"),sQuery(id+"F0.wireOp",EDGE,"E1599"),sQuery(id+"F0.wireOp",EDGE,"E1600"),sQuery(id+"F0.wireOp",EDGE,"E1601"),sQuery(id+"F0.wireOp",EDGE,"E1602"),sQuery(id+"F0.wireOp",EDGE,"E1603"),sQuery(id+"F0.wireOp",EDGE,"E1604"),sQuery(id+"F0.wireOp",EDGE,"E1605"),sQuery(id+"F0.wireOp",EDGE,"E1606"),sQuery(id+"F0.wireOp",EDGE,"E1607"),sQuery(id+"F0.wireOp",EDGE,"E1608"),sQuery(id+"F0.wireOp",EDGE,"E1609"),sQuery(id+"F0.wireOp",EDGE,"E1610"),sQuery(id+"F0.wireOp",EDGE,"E1611"),sQuery(id+"F0.wireOp",EDGE,"E1612"),sQuery(id+"F0.wireOp",EDGE,"E1613"),sQuery(id+"F0.wireOp",EDGE,"E1614"),sQuery(id+"F0.wireOp",EDGE,"E1615"),sQuery(id+"F0.wireOp",EDGE,"E1616"),sQuery(id+"F0.wireOp",EDGE,"E1617"),sQuery(id+"F0.wireOp",EDGE,"E1618"),sQuery(id+"F0.wireOp",EDGE,"E1619"),sQuery(id+"F0.wireOp",EDGE,"E1620"),sQuery(id+"F0.wireOp",EDGE,"E1621"),sQuery(id+"F0.wireOp",EDGE,"E1622"),sQuery(id+"F0.wireOp",EDGE,"E1623"),sQuery(id+"F0.wireOp",EDGE,"E1624"),sQuery(id+"F0.wireOp",EDGE,"E1625"),sQuery(id+"F0.wireOp",EDGE,"E1626"),sQuery(id+"F0.wireOp",EDGE,"E1627"),sQuery(id+"F0.wireOp",EDGE,"E1628"),sQuery(id+"F0.wireOp",EDGE,"E1629"),sQuery(id+"F0.wireOp",EDGE,"E1630"),sQuery(id+"F0.wireOp",EDGE,"E1631"),sQuery(id+"F0.wireOp",EDGE,"E1632"),sQuery(id+"F0.wireOp",EDGE,"E1633"),sQuery(id+"F0.wireOp",EDGE,"E1634"),sQuery(id+"F0.wireOp",EDGE,"E1635"),sQuery(id+"F0.wireOp",EDGE,"E1636"),sQuery(id+"F0.wireOp",EDGE,"E1637"),sQuery(id+"F0.wireOp",EDGE,"E1638"),sQuery(id+"F0.wireOp",EDGE,"E1639"),sQuery(id+"F0.wireOp",EDGE,"E1640"),sQuery(id+"F0.wireOp",EDGE,"E1641"),sQuery(id+"F0.wireOp",EDGE,"E1642"),sQuery(id+"F0.wireOp",EDGE,"E1643"),sQuery(id+"F0.wireOp",EDGE,"E1644"),sQuery(id+"F0.wireOp",EDGE,"E1645"),sQuery(id+"F0.wireOp",EDGE,"E1646"),sQuery(id+"F0.wireOp",EDGE,"E1647"),sQuery(id+"F0.wireOp",EDGE,"E1648"),sQuery(id+"F0.wireOp",EDGE,"E1649"),sQuery(id+"F0.wireOp",EDGE,"E1650"),sQuery(id+"F0.wireOp",EDGE,"E1651"),sQuery(id+"F0.wireOp",EDGE,"E1652"),sQuery(id+"F0.wireOp",EDGE,"E1653"),sQuery(id+"F0.wireOp",EDGE,"E1654"),sQuery(id+"F0.wireOp",EDGE,"E1655"),sQuery(id+"F0.wireOp",EDGE,"E1656"),sQuery(id+"F0.wireOp",EDGE,"E1657"),sQuery(id+"F0.wireOp",EDGE,"E1658"),sQuery(id+"F0.wireOp",EDGE,"E1659"),sQuery(id+"F0.wireOp",EDGE,"E1660"),sQuery(id+"F0.wireOp",EDGE,"E1661"),sQuery(id+"F0.wireOp",EDGE,"E1662"),sQuery(id+"F0.wireOp",EDGE,"E1663"),sQuery(id+"F0.wireOp",EDGE,"E1664"),sQuery(id+"F0.wireOp",EDGE,"E1665"),sQuery(id+"F0.wireOp",EDGE,"E1666"),sQuery(id+"F0.wireOp",EDGE,"E1667"),sQuery(id+"F0.wireOp",EDGE,"E1668"),sQuery(id+"F0.wireOp",EDGE,"E1669"),sQuery(id+"F0.wireOp",EDGE,"E1670"),sQuery(id+"F0.wireOp",EDGE,"E1671"),sQuery(id+"F0.wireOp",EDGE,"E1672"),sQuery(id+"F0.wireOp",EDGE,"E1673"),sQuery(id+"F0.wireOp",EDGE,"E1674"),sQuery(id+"F0.wireOp",EDGE,"E1675"),sQuery(id+"F0.wireOp",EDGE,"E1676"),sQuery(id+"F0.wireOp",EDGE,"E1677"),sQuery(id+"F0.wireOp",EDGE,"E1678"),sQuery(id+"F0.wireOp",EDGE,"E1679"),sQuery(id+"F0.wireOp",EDGE,"E1680"),sQuery(id+"F0.wireOp",EDGE,"E1681"),sQuery(id+"F0.wireOp",EDGE,"E1682"),sQuery(id+"F0.wireOp",EDGE,"E1683"),sQuery(id+"F0.wireOp",EDGE,"E1684"),sQuery(id+"F0.wireOp",EDGE,"E1685"),sQuery(id+"F0.wireOp",EDGE,"E1686"),sQuery(id+"F0.wireOp",EDGE,"E1687"),sQuery(id+"F0.wireOp",EDGE,"E1688"),sQuery(id+"F0.wireOp",EDGE,"E1689"),sQuery(id+"F0.wireOp",EDGE,"E1690"),sQuery(id+"F0.wireOp",EDGE,"E1691"),sQuery(id+"F0.wireOp",EDGE,"E1692"),sQuery(id+"F0.wireOp",EDGE,"E1693"),sQuery(id+"F0.wireOp",EDGE,"E1694"),sQuery(id+"F0.wireOp",EDGE,"E1695"),sQuery(id+"F0.wireOp",EDGE,"E1696"),sQuery(id+"F0.wireOp",EDGE,"E1697"),sQuery(id+"F0.wireOp",EDGE,"E1698"),sQuery(id+"F0.wireOp",EDGE,"E1699"),sQuery(id+"F0.wireOp",EDGE,"E1700"),sQuery(id+"F0.wireOp",EDGE,"E1701"),sQuery(id+"F0.wireOp",EDGE,"E1702"),sQuery(id+"F0.wireOp",EDGE,"E1703"),sQuery(id+"F0.wireOp",EDGE,"E1704"),sQuery(id+"F0.wireOp",EDGE,"E1705"),sQuery(id+"F0.wireOp",EDGE,"E1706"),sQuery(id+"F0.wireOp",EDGE,"E1707"),sQuery(id+"F0.wireOp",EDGE,"E1708"),sQuery(id+"F0.wireOp",EDGE,"E1709"),sQuery(id+"F0.wireOp",EDGE,"E1710"),sQuery(id+"F0.wireOp",EDGE,"E1711"),sQuery(id+"F0.wireOp",EDGE,"E1712"),sQuery(id+"F0.wireOp",EDGE,"E1713"),sQuery(id+"F0.wireOp",EDGE,"E1714"),sQuery(id+"F0.wireOp",EDGE,"E1715"),sQuery(id+"F0.wireOp",EDGE,"E1716"),sQuery(id+"F0.wireOp",EDGE,"E1717"),sQuery(id+"F0.wireOp",EDGE,"E1718"),sQuery(id+"F0.wireOp",EDGE,"E1719"),sQuery(id+"F0.wireOp",EDGE,"E1720"),sQuery(id+"F0.wireOp",EDGE,"E1721"),sQuery(id+"F0.wireOp",EDGE,"E1722"),sQuery(id+"F0.wireOp",EDGE,"E1723"),sQuery(id+"F0.wireOp",EDGE,"E1724"),sQuery(id+"F0.wireOp",EDGE,"E1725"),sQuery(id+"F0.wireOp",EDGE,"E1726"),sQuery(id+"F0.wireOp",EDGE,"E1727"),sQuery(id+"F0.wireOp",EDGE,"E1728"),sQuery(id+"F0.wireOp",EDGE,"E1729"),sQuery(id+"F0.wireOp",EDGE,"E1730"),sQuery(id+"F0.wireOp",EDGE,"E1731"),sQuery(id+"F0.wireOp",EDGE,"E1732"),sQuery(id+"F0.wireOp",EDGE,"E1733"),sQuery(id+"F0.wireOp",EDGE,"E1734"),sQuery(id+"F0.wireOp",EDGE,"E1735"),sQuery(id+"F0.wireOp",EDGE,"E1736"),sQuery(id+"F0.wireOp",EDGE,"E1737"),sQuery(id+"F0.wireOp",EDGE,"E1738"),sQuery(id+"F0.wireOp",EDGE,"E1739"),sQuery(id+"F0.wireOp",EDGE,"E1740"),sQuery(id+"F0.wireOp",EDGE,"E1741"),sQuery(id+"F0.wireOp",EDGE,"E1742"),sQuery(id+"F0.wireOp",EDGE,"E1743"),sQuery(id+"F0.wireOp",EDGE,"E1744"),sQuery(id+"F0.wireOp",EDGE,"E1745"),sQuery(id+"F0.wireOp",EDGE,"E1746"),sQuery(id+"F0.wireOp",EDGE,"E1747"),sQuery(id+"F0.wireOp",EDGE,"E1748"),sQuery(id+"F0.wireOp",EDGE,"E1749"),sQuery(id+"F0.wireOp",EDGE,"E1750"),sQuery(id+"F0.wireOp",EDGE,"E1751"),sQuery(id+"F0.wireOp",EDGE,"E1752"),sQuery(id+"F0.wireOp",EDGE,"E1753"),sQuery(id+"F0.wireOp",EDGE,"E1754"),sQuery(id+"F0.wireOp",EDGE,"E1755"),sQuery(id+"F0.wireOp",EDGE,"E1756"),sQuery(id+"F0.wireOp",EDGE,"E1757"),sQuery(id+"F0.wireOp",EDGE,"E1758"),sQuery(id+"F0.wireOp",EDGE,"E1759"),sQuery(id+"F0.wireOp",EDGE,"E1760"),sQuery(id+"F0.wireOp",EDGE,"E1761"),sQuery(id+"F0.wireOp",EDGE,"E1762"),sQuery(id+"F0.wireOp",EDGE,"E1763"),sQuery(id+"F0.wireOp",EDGE,"E1764"),sQuery(id+"F0.wireOp",EDGE,"E1765"),sQuery(id+"F0.wireOp",EDGE,"E1766"),sQuery(id+"F0.wireOp",EDGE,"E1767"),sQuery(id+"F0.wireOp",EDGE,"E1768"),sQuery(id+"F0.wireOp",EDGE,"E1769"),sQuery(id+"F0.wireOp",EDGE,"E1770"),sQuery(id+"F0.wireOp",EDGE,"E1771"),sQuery(id+"F0.wireOp",EDGE,"E1772"),sQuery(id+"F0.wireOp",EDGE,"E1773"),sQuery(id+"F0.wireOp",EDGE,"E1774"),sQuery(id+"F0.wireOp",EDGE,"E1775"),sQuery(id+"F0.wireOp",EDGE,"E1776"),sQuery(id+"F0.wireOp",EDGE,"E1777"),sQuery(id+"F0.wireOp",EDGE,"E1778"),sQuery(id+"F0.wireOp",EDGE,"E1779"),sQuery(id+"F0.wireOp",EDGE,"E1780"),sQuery(id+"F0.wireOp",EDGE,"E1781"),sQuery(id+"F0.wireOp",EDGE,"E1782"),sQuery(id+"F0.wireOp",EDGE,"E1783"),sQuery(id+"F0.wireOp",EDGE,"E1784"),sQuery(id+"F0.wireOp",EDGE,"E1785"),sQuery(id+"F0.wireOp",EDGE,"E1786"),sQuery(id+"F0.wireOp",EDGE,"E1787"),sQuery(id+"F0.wireOp",EDGE,"E1788"),sQuery(id+"F0.wireOp",EDGE,"E1789"),sQuery(id+"F0.wireOp",EDGE,"E1790"),sQuery(id+"F0.wireOp",EDGE,"E1791"),sQuery(id+"F0.wireOp",EDGE,"E1792"),sQuery(id+"F0.wireOp",EDGE,"E1793"),sQuery(id+"F0.wireOp",EDGE,"E1794"),sQuery(id+"F0.wireOp",EDGE,"E1795"),sQuery(id+"F0.wireOp",EDGE,"E1796"),sQuery(id+"F0.wireOp",EDGE,"E1797"),sQuery(id+"F0.wireOp",EDGE,"E1798"),sQuery(id+"F0.wireOp",EDGE,"E1799"),sQuery(id+"F0.wireOp",EDGE,"E1800"),sQuery(id+"F0.wireOp",EDGE,"E1801"),sQuery(id+"F0.wireOp",EDGE,"E1802"),sQuery(id+"F0.wireOp",EDGE,"E1803"),sQuery(id+"F0.wireOp",EDGE,"E1804"),sQuery(id+"F0.wireOp",EDGE,"E1805"),sQuery(id+"F0.wireOp",EDGE,"E1806"),sQuery(id+"F0.wireOp",EDGE,"E1807"),sQuery(id+"F0.wireOp",EDGE,"E1808"),sQuery(id+"F0.wireOp",EDGE,"E1809"),sQuery(id+"F0.wireOp",EDGE,"E1810"),sQuery(id+"F0.wireOp",EDGE,"E1811"),sQuery(id+"F0.wireOp",EDGE,"E1812"),sQuery(id+"F0.wireOp",EDGE,"E1813"),sQuery(id+"F0.wireOp",EDGE,"E1814"),sQuery(id+"F0.wireOp",EDGE,"E1815"),sQuery(id+"F0.wireOp",EDGE,"E1816"),sQuery(id+"F0.wireOp",EDGE,"E1817"),sQuery(id+"F0.wireOp",EDGE,"E1818"),sQuery(id+"F0.wireOp",EDGE,"E1819"),sQuery(id+"F0.wireOp",EDGE,"E1820"),sQuery(id+"F0.wireOp",EDGE,"E1821"),sQuery(id+"F0.wireOp",EDGE,"E1822"),sQuery(id+"F0.wireOp",EDGE,"E1823"),sQuery(id+"F0.wireOp",EDGE,"E1824"),sQuery(id+"F0.wireOp",EDGE,"E1825"),sQuery(id+"F0.wireOp",EDGE,"E1826"),sQuery(id+"F0.wireOp",EDGE,"E1827"),sQuery(id+"F0.wireOp",EDGE,"E1828"),sQuery(id+"F0.wireOp",EDGE,"E1829"),sQuery(id+"F0.wireOp",EDGE,"E1830"),sQuery(id+"F0.wireOp",EDGE,"E1831"),sQuery(id+"F0.wireOp",EDGE,"E1832"),sQuery(id+"F0.wireOp",EDGE,"E1833"),sQuery(id+"F0.wireOp",EDGE,"E1834"),sQuery(id+"F0.wireOp",EDGE,"E1835"),sQuery(id+"F0.wireOp",EDGE,"E1836"),sQuery(id+"F0.wireOp",EDGE,"E1837"),sQuery(id+"F0.wireOp",EDGE,"E1838"),sQuery(id+"F0.wireOp",EDGE,"E1839"),sQuery(id+"F0.wireOp",EDGE,"E1840"),sQuery(id+"F0.wireOp",EDGE,"E1841"),sQuery(id+"F0.wireOp",EDGE,"E1842"),sQuery(id+"F0.wireOp",EDGE,"E1843"),sQuery(id+"F0.wireOp",EDGE,"E1844"),sQuery(id+"F0.wireOp",EDGE,"E1845"),sQuery(id+"F0.wireOp",EDGE,"E1846"),sQuery(id+"F0.wireOp",EDGE,"E1847"),sQuery(id+"F0.wireOp",EDGE,"E1848"),sQuery(id+"F0.wireOp",EDGE,"E1849"),sQuery(id+"F0.wireOp",EDGE,"E1850"),sQuery(id+"F0.wireOp",EDGE,"E1851"),sQuery(id+"F0.wireOp",EDGE,"E1852"),sQuery(id+"F0.wireOp",EDGE,"E1853"),sQuery(id+"F0.wireOp",EDGE,"E1854"),sQuery(id+"F0.wireOp",EDGE,"E1855"),sQuery(id+"F0.wireOp",EDGE,"E1856"),sQuery(id+"F0.wireOp",EDGE,"E1857"),sQuery(id+"F0.wireOp",EDGE,"E1858"),sQuery(id+"F0.wireOp",EDGE,"E1859"),sQuery(id+"F0.wireOp",EDGE,"E1860"),sQuery(id+"F0.wireOp",EDGE,"E1861"),sQuery(id+"F0.wireOp",EDGE,"E1862"),sQuery(id+"F0.wireOp",EDGE,"E1863"),sQuery(id+"F0.wireOp",EDGE,"E1864"),sQuery(id+"F0.wireOp",EDGE,"E1865"),sQuery(id+"F0.wireOp",EDGE,"E1866"),sQuery(id+"F0.wireOp",EDGE,"E1867"),sQuery(id+"F0.wireOp",EDGE,"E1868"),sQuery(id+"F0.wireOp",EDGE,"E1869"),sQuery(id+"F0.wireOp",EDGE,"E1870"),sQuery(id+"F0.wireOp",EDGE,"E1871"),sQuery(id+"F0.wireOp",EDGE,"E1872"),sQuery(id+"F0.wireOp",EDGE,"E1873"),sQuery(id+"F0.wireOp",EDGE,"E1874"),sQuery(id+"F0.wireOp",EDGE,"E1875"),sQuery(id+"F0.wireOp",EDGE,"E1876"),sQuery(id+"F0.wireOp",EDGE,"E1877"),sQuery(id+"F0.wireOp",EDGE,"E1878"),sQuery(id+"F0.wireOp",EDGE,"E1879"),sQuery(id+"F0.wireOp",EDGE,"E1880"),sQuery(id+"F0.wireOp",EDGE,"E1881"),sQuery(id+"F0.wireOp",EDGE,"E1882"),sQuery(id+"F0.wireOp",EDGE,"E1883"),sQuery(id+"F0.wireOp",EDGE,"E1884"),sQuery(id+"F0.wireOp",EDGE,"E1885"),sQuery(id+"F0.wireOp",EDGE,"E1886"),sQuery(id+"F0.wireOp",EDGE,"E1887"),sQuery(id+"F0.wireOp",EDGE,"E1888"),sQuery(id+"F0.wireOp",EDGE,"E1889"),sQuery(id+"F0.wireOp",EDGE,"E1890"),sQuery(id+"F0.wireOp",EDGE,"E1891"),sQuery(id+"F0.wireOp",EDGE,"E1892"),sQuery(id+"F0.wireOp",EDGE,"E1893"),sQuery(id+"F0.wireOp",EDGE,"E1894"),sQuery(id+"F0.wireOp",EDGE,"E1895"),sQuery(id+"F0.wireOp",EDGE,"E1896"),sQuery(id+"F0.wireOp",EDGE,"E1897"),sQuery(id+"F0.wireOp",EDGE,"E1898"),sQuery(id+"F0.wireOp",EDGE,"E1899"),sQuery(id+"F0.wireOp",EDGE,"E1900"),sQuery(id+"F0.wireOp",EDGE,"E1901"),sQuery(id+"F0.wireOp",EDGE,"E1902"),sQuery(id+"F0.wireOp",EDGE,"E1903"),sQuery(id+"F0.wireOp",EDGE,"E1904"),sQuery(id+"F0.wireOp",EDGE,"E1905"),sQuery(id+"F0.wireOp",EDGE,"E1906"),sQuery(id+"F0.wireOp",EDGE,"E1907"),sQuery(id+"F0.wireOp",EDGE,"E1908"),sQuery(id+"F0.wireOp",EDGE,"E1909"),sQuery(id+"F0.wireOp",EDGE,"E1910"),sQuery(id+"F0.wireOp",EDGE,"E1911"),sQuery(id+"F0.wireOp",EDGE,"E1912"),sQuery(id+"F0.wireOp",EDGE,"E1913"),sQuery(id+"F0.wireOp",EDGE,"E1914"),sQuery(id+"F0.wireOp",EDGE,"E1915"),sQuery(id+"F0.wireOp",EDGE,"E1916"),sQuery(id+"F0.wireOp",EDGE,"E1917"),sQuery(id+"F0.wireOp",EDGE,"E1918"),sQuery(id+"F0.wireOp",EDGE,"E1919"),sQuery(id+"F0.wireOp",EDGE,"E1920"),sQuery(id+"F0.wireOp",EDGE,"E1921"),sQuery(id+"F0.wireOp",EDGE,"E1922"),sQuery(id+"F0.wireOp",EDGE,"E1923"),sQuery(id+"F0.wireOp",EDGE,"E1924"),sQuery(id+"F0.wireOp",EDGE,"E1925"),sQuery(id+"F0.wireOp",EDGE,"E1926"),sQuery(id+"F0.wireOp",EDGE,"E1927"),sQuery(id+"F0.wireOp",EDGE,"E1928"),sQuery(id+"F0.wireOp",EDGE,"E1929"),sQuery(id+"F0.wireOp",EDGE,"E1930"),sQuery(id+"F0.wireOp",EDGE,"E1931"),sQuery(id+"F0.wireOp",EDGE,"E1932"),sQuery(id+"F0.wireOp",EDGE,"E1933"),sQuery(id+"F0.wireOp",EDGE,"E1934"),sQuery(id+"F0.wireOp",EDGE,"E1935"),sQuery(id+"F0.wireOp",EDGE,"E1936"),sQuery(id+"F0.wireOp",EDGE,"E1937"),sQuery(id+"F0.wireOp",EDGE,"E1938"),sQuery(id+"F0.wireOp",EDGE,"E1939"),sQuery(id+"F0.wireOp",EDGE,"E1940"),sQuery(id+"F0.wireOp",EDGE,"E1941"),sQuery(id+"F0.wireOp",EDGE,"E1942"),sQuery(id+"F0.wireOp",EDGE,"E1943"),sQuery(id+"F0.wireOp",EDGE,"E1944"),sQuery(id+"F0.wireOp",EDGE,"E1945"),sQuery(id+"F0.wireOp",EDGE,"E1946"),sQuery(id+"F0.wireOp",EDGE,"E1947"),sQuery(id+"F0.wireOp",EDGE,"E1948"),sQuery(id+"F0.wireOp",EDGE,"E1949"),sQuery(id+"F0.wireOp",EDGE,"E1950"),sQuery(id+"F0.wireOp",EDGE,"E1951"),sQuery(id+"F0.wireOp",EDGE,"E1952"),sQuery(id+"F0.wireOp",EDGE,"E1953"),sQuery(id+"F0.wireOp",EDGE,"E1954"),sQuery(id+"F0.wireOp",EDGE,"E1955"),sQuery(id+"F0.wireOp",EDGE,"E1956"),sQuery(id+"F0.wireOp",EDGE,"E1957"),sQuery(id+"F0.wireOp",EDGE,"E1958"),sQuery(id+"F0.wireOp",EDGE,"E1959"),sQuery(id+"F0.wireOp",EDGE,"E1960"),sQuery(id+"F0.wireOp",EDGE,"E1961"),sQuery(id+"F0.wireOp",EDGE,"E1962"),sQuery(id+"F0.wireOp",EDGE,"E1963"),sQuery(id+"F0.wireOp",EDGE,"E1964"),sQuery(id+"F0.wireOp",EDGE,"E1965"),sQuery(id+"F0.wireOp",EDGE,"E1966"),sQuery(id+"F0.wireOp",EDGE,"E1967"),sQuery(id+"F0.wireOp",EDGE,"E1968"),sQuery(id+"F0.wireOp",EDGE,"E1969"),sQuery(id+"F0.wireOp",EDGE,"E1970"),sQuery(id+"F0.wireOp",EDGE,"E1971"),sQuery(id+"F0.wireOp",EDGE,"E1972"),sQuery(id+"F0.wireOp",EDGE,"E1973"),sQuery(id+"F0.wireOp",EDGE,"E1974"),sQuery(id+"F0.wireOp",EDGE,"E1975"),sQuery(id+"F0.wireOp",EDGE,"E1976"),sQuery(id+"F0.wireOp",EDGE,"E1977"),sQuery(id+"F0.wireOp",EDGE,"E1978"),sQuery(id+"F0.wireOp",EDGE,"E1979"),sQuery(id+"F0.wireOp",EDGE,"E1980"),sQuery(id+"F0.wireOp",EDGE,"E1981"),sQuery(id+"F0.wireOp",EDGE,"E1982"),sQuery(id+"F0.wireOp",EDGE,"E1983"),sQuery(id+"F0.wireOp",EDGE,"E1984"),sQuery(id+"F0.wireOp",EDGE,"E1985"),sQuery(id+"F0.wireOp",EDGE,"E1986"),sQuery(id+"F0.wireOp",EDGE,"E1987"),sQuery(id+"F0.wireOp",EDGE,"E1988"),sQuery(id+"F0.wireOp",EDGE,"E1989"),sQuery(id+"F0.wireOp",EDGE,"E1990"),sQuery(id+"F0.wireOp",EDGE,"E1991"),sQuery(id+"F0.wireOp",EDGE,"E1992"),sQuery(id+"F0.wireOp",EDGE,"E1993"),sQuery(id+"F0.wireOp",EDGE,"E1994"),sQuery(id+"F0.wireOp",EDGE,"E1995"),sQuery(id+"F0.wireOp",EDGE,"E1996"),sQuery(id+"F0.wireOp",EDGE,"E1997"),sQuery(id+"F0.wireOp",EDGE,"E1998"),sQuery(id+"F0.wireOp",EDGE,"E1999"),sQuery(id+"F0.wireOp",EDGE,"E2000"),sQuery(id+"F0.wireOp",EDGE,"E2001"),sQuery(id+"F0.wireOp",EDGE,"E2002"),sQuery(id+"F0.wireOp",EDGE,"E2003"),sQuery(id+"F0.wireOp",EDGE,"E2004"),sQuery(id+"F0.wireOp",EDGE,"E2005"),sQuery(id+"F0.wireOp",EDGE,"E2006"),sQuery(id+"F0.wireOp",EDGE,"E2007"),sQuery(id+"F0.wireOp",EDGE,"E2008"),sQuery(id+"F0.wireOp",EDGE,"E2009"),sQuery(id+"F0.wireOp",EDGE,"E2010"),sQuery(id+"F0.wireOp",EDGE,"E2011"),sQuery(id+"F0.wireOp",EDGE,"E2012"),sQuery(id+"F0.wireOp",EDGE,"E2013"),sQuery(id+"F0.wireOp",EDGE,"E2014"),sQuery(id+"F0.wireOp",EDGE,"E2015"),sQuery(id+"F0.wireOp",EDGE,"E2016"),sQuery(id+"F0.wireOp",EDGE,"E2017"),sQuery(id+"F0.wireOp",EDGE,"E2018"),sQuery(id+"F0.wireOp",EDGE,"E2019"),sQuery(id+"F0.wireOp",EDGE,"E2020"),sQuery(id+"F0.wireOp",EDGE,"E2021"),sQuery(id+"F0.wireOp",EDGE,"E2022"),sQuery(id+"F0.wireOp",EDGE,"E2023"),sQuery(id+"F0.wireOp",EDGE,"E2024"),sQuery(id+"F0.wireOp",EDGE,"E2025"),sQuery(id+"F0.wireOp",EDGE,"E2026"),sQuery(id+"F0.wireOp",EDGE,"E2027"),sQuery(id+"F0.wireOp",EDGE,"E2028"),sQuery(id+"F0.wireOp",EDGE,"E2029"),sQuery(id+"F0.wireOp",EDGE,"E2030"),sQuery(id+"F0.wireOp",EDGE,"E2031"),sQuery(id+"F0.wireOp",EDGE,"E2032"),sQuery(id+"F0.wireOp",EDGE,"E2033"),sQuery(id+"F0.wireOp",EDGE,"E2034"),sQuery(id+"F0.wireOp",EDGE,"E2035"),sQuery(id+"F0.wireOp",EDGE,"E2036"),sQuery(id+"F0.wireOp",EDGE,"E2037"),sQuery(id+"F0.wireOp",EDGE,"E2038"),sQuery(id+"F0.wireOp",EDGE,"E2039"),sQuery(id+"F0.wireOp",EDGE,"E2040"),sQuery(id+"F0.wireOp",EDGE,"E2041"),sQuery(id+"F0.wireOp",EDGE,"E2042"),sQuery(id+"F0.wireOp",EDGE,"E2043"),sQuery(id+"F0.wireOp",EDGE,"E2044"),sQuery(id+"F0.wireOp",EDGE,"E2045"),sQuery(id+"F0.wireOp",EDGE,"E2046"),sQuery(id+"F0.wireOp",EDGE,"E2047"),sQuery(id+"F0.wireOp",EDGE,"E2048"),sQuery(id+"F0.wireOp",EDGE,"E2049"),sQuery(id+"F0.wireOp",EDGE,"E2050"),sQuery(id+"F0.wireOp",EDGE,"E2051"),sQuery(id+"F0.wireOp",EDGE,"E2052"),sQuery(id+"F0.wireOp",EDGE,"E2053"),sQuery(id+"F0.wireOp",EDGE,"E2054"),sQuery(id+"F0.wireOp",EDGE,"E2055"),sQuery(id+"F0.wireOp",EDGE,"E2056"),sQuery(id+"F0.wireOp",EDGE,"E2057"),sQuery(id+"F0.wireOp",EDGE,"E2058"),sQuery(id+"F0.wireOp",EDGE,"E2059"),sQuery(id+"F0.wireOp",EDGE,"E2060"),sQuery(id+"F0.wireOp",EDGE,"E2061"),sQuery(id+"F0.wireOp",EDGE,"E2062"),sQuery(id+"F0.wireOp",EDGE,"E2063"),sQuery(id+"F0.wireOp",EDGE,"E2064"),sQuery(id+"F0.wireOp",EDGE,"E2065"),sQuery(id+"F0.wireOp",EDGE,"E2066"),sQuery(id+"F0.wireOp",EDGE,"E2067"),sQuery(id+"F0.wireOp",EDGE,"E2068"),sQuery(id+"F0.wireOp",EDGE,"E2069"),sQuery(id+"F0.wireOp",EDGE,"E2070"),sQuery(id+"F0.wireOp",EDGE,"E2071"),sQuery(id+"F0.wireOp",EDGE,"E2072"),sQuery(id+"F0.wireOp",EDGE,"E2073"),sQuery(id+"F0.wireOp",EDGE,"E2074"),sQuery(id+"F0.wireOp",EDGE,"E2075"),sQuery(id+"F0.wireOp",EDGE,"E2076"),sQuery(id+"F0.wireOp",EDGE,"E2077"),sQuery(id+"F0.wireOp",EDGE,"E2078"),sQuery(id+"F0.wireOp",EDGE,"E2079"),sQuery(id+"F0.wireOp",EDGE,"E2080"),sQuery(id+"F0.wireOp",EDGE,"E2081"),sQuery(id+"F0.wireOp",EDGE,"E2082"),sQuery(id+"F0.wireOp",EDGE,"E2083"),sQuery(id+"F0.wireOp",EDGE,"E2084"),sQuery(id+"F0.wireOp",EDGE,"E2085"),sQuery(id+"F0.wireOp",EDGE,"E2086"),sQuery(id+"F0.wireOp",EDGE,"E2087"),sQuery(id+"F0.wireOp",EDGE,"E2090"),sQuery(id+"F0.wireOp",EDGE,"E2091"),sQuery(id+"F0.wireOp",EDGE,"E2092"),sQuery(id+"F0.wireOp",EDGE,"E2093"),sQuery(id+"F0.wireOp",EDGE,"E2094"),sQuery(id+"F0.wireOp",EDGE,"E2095"),sQuery(id+"F0.wireOp",EDGE,"E2096"),sQuery(id+"F0.wireOp",EDGE,"E2097"),sQuery(id+"F0.wireOp",EDGE,"E2098"),sQuery(id+"F0.wireOp",EDGE,"E2099"),sQuery(id+"F0.wireOp",EDGE,"E2100"),sQuery(id+"F0.wireOp",EDGE,"E2101"),sQuery(id+"F0.wireOp",EDGE,"E2102"),sQuery(id+"F0.wireOp",EDGE,"E2103"),sQuery(id+"F0.wireOp",EDGE,"E2104"),sQuery(id+"F0.wireOp",EDGE,"E2105"),sQuery(id+"F0.wireOp",EDGE,"E2106"),sQuery(id+"F0.wireOp",EDGE,"E2107"),sQuery(id+"F0.wireOp",EDGE,"E2108"),sQuery(id+"F0.wireOp",EDGE,"E2109"),sQuery(id+"F0.wireOp",EDGE,"E2110"),sQuery(id+"F0.wireOp",EDGE,"E2111"),sQuery(id+"F0.wireOp",EDGE,"E2112"),sQuery(id+"F0.wireOp",EDGE,"E2113"),sQuery(id+"F0.wireOp",EDGE,"E2118"),sQuery(id+"F0.wireOp",EDGE,"E2120"),sQuery(id+"F0.wireOp",EDGE,"E2124"),sQuery(id+"F0.wireOp",EDGE,"E2127"),sQuery(id+"F0.wireOp",EDGE,"E2128"),sQuery(id+"F0.wireOp",EDGE,"E2129"),sQuery(id+"F0.wireOp",EDGE,"E2130"),sQuery(id+"F0.wireOp",EDGE,"E2131"),sQuery(id+"F0.wireOp",EDGE,"E2132"),sQuery(id+"F0.wireOp",EDGE,"E2133"),sQuery(id+"F0.wireOp",EDGE,"E2134"),sQuery(id+"F0.wireOp",EDGE,"E2163"),sQuery(id+"F0.wireOp",EDGE,"E2164"),sQuery(id+"F0.wireOp",EDGE,"E2165"),sQuery(id+"F0.wireOp",EDGE,"E2166"),sQuery(id+"F0.wireOp",EDGE,"E2167"),sQuery(id+"F0.wireOp",EDGE,"E2168"),sQuery(id+"F0.wireOp",EDGE,"E2169"),sQuery(id+"F0.wireOp",EDGE,"E2170"),sQuery(id+"F0.wireOp",EDGE,"E2171"),sQuery(id+"F0.wireOp",EDGE,"E2172"),sQuery(id+"F0.wireOp",EDGE,"E2176"),sQuery(id+"F0.wireOp",EDGE,"E2177"),sQuery(id+"F0.wireOp",EDGE,"E2178"),sQuery(id+"F0.wireOp",EDGE,"E2179"),sQuery(id+"F0.wireOp",EDGE,"E2180"),sQuery(id+"F0.wireOp",EDGE,"E2181"),sQuery(id+"F0.wireOp",EDGE,"E2182"),sQuery(id+"F0.wireOp",EDGE,"E2183"),sQuery(id+"F0.wireOp",EDGE,"E2184"),sQuery(id+"F0.wireOp",EDGE,"E2185"),sQuery(id+"F0.wireOp",EDGE,"E2211"),sQuery(id+"F0.wireOp",EDGE,"E2212"),sQuery(id+"F0.wireOp",EDGE,"E2213"),sQuery(id+"F0.wireOp",EDGE,"E2214"),sQuery(id+"F0.wireOp",EDGE,"E2215"),sQuery(id+"F0.wireOp",EDGE,"E2216"),sQuery(id+"F0.wireOp",EDGE,"E2217"),sQuery(id+"F0.wireOp",EDGE,"E2219"),sQuery(id+"F0.wireOp",EDGE,"E2282"),sQuery(id+"F0.wireOp",EDGE,"E2283"),sQuery(id+"F0.wireOp",EDGE,"E2284"),sQuery(id+"F0.wireOp",EDGE,"E2285"),sQuery(id+"F0.wireOp",EDGE,"E2286"),sQuery(id+"F0.wireOp",EDGE,"E2287"),sQuery(id+"F0.wireOp",EDGE,"E2288"),sQuery(id+"F0.wireOp",EDGE,"E2289"),sQuery(id+"F0.wireOp",EDGE,"E2290"),sQuery(id+"F0.wireOp",EDGE,"E2291"),sQuery(id+"F0.wireOp",EDGE,"E2292"),sQuery(id+"F0.wireOp",EDGE,"E2293"),sQuery(id+"F0.wireOp",EDGE,"E2294"),sQuery(id+"F0.wireOp",EDGE,"E2295"),sQuery(id+"F0.wireOp",EDGE,"E2296"),sQuery(id+"F0.wireOp",EDGE,"E2297"),sQuery(id+"F0.wireOp",EDGE,"E2298"),sQuery(id+"F0.wireOp",EDGE,"E2300"),sQuery(id+"F0.wireOp",EDGE,"E2301"),sQuery(id+"F0.wireOp",EDGE,"E2302"),sQuery(id+"F0.wireOp",EDGE,"E2303"),sQuery(id+"F0.wireOp",EDGE,"E2305"),sQuery(id+"F0.wireOp",EDGE,"E2306"),sQuery(id+"F0.wireOp",EDGE,"E2307"),sQuery(id+"F0.wireOp",EDGE,"E2308")])],"isStart":false});
            var sketch = newSketch(context, id + "F4", { "sketchPlane" : qUnion([Q0])});
            skLineSegment(sketch, "E2339.bottom", {"start": v(73.12, 18.06) * mm, "end": v(84.26, 18.06) * mm});
            skLineSegment(sketch, "E2339.top", {"start": v(73.12, -8.42) * mm, "end": v(84.26, -8.42) * mm});
            skLineSegment(sketch, "E2339.left", {"start": v(73.12, 18.06) * mm, "end": v(73.12, -8.42) * mm});
            skLineSegment(sketch, "E2339.right", {"start": v(84.26, 18.06) * mm, "end": v(84.26, -8.42) * mm});
            skLineSegment(sketch, "E2340.bottom", {"start": v(67.5, -28.74) * mm, "end": v(75.96, -28.74) * mm});
            skLineSegment(sketch, "E2340.top", {"start": v(67.5, -36.17) * mm, "end": v(75.96, -36.17) * mm});
            skLineSegment(sketch, "E2340.left", {"start": v(67.5, -28.74) * mm, "end": v(67.5, -36.17) * mm});
            skLineSegment(sketch, "E2340.right", {"start": v(75.96, -28.74) * mm, "end": v(75.96, -36.17) * mm});
            skLineSegment(sketch, "E2341.bottom", {"start": v(78.65, 24.3) * mm, "end": v(74.07, 24.3) * mm});
            skLineSegment(sketch, "E2341.top", {"start": v(78.65, 30.55) * mm, "end": v(74.07, 30.55) * mm});
            skLineSegment(sketch, "E2341.left", {"start": v(78.65, 24.3) * mm, "end": v(78.65, 30.55) * mm});
            skLineSegment(sketch, "E2341.right", {"start": v(74.07, 24.3) * mm, "end": v(74.07, 30.55) * mm});
            skCircle(sketch, "E2342", {"center": v(95.33, 8.73) * mm, "radius": 3.42 * mm});
            skLineSegment(sketch, "E2343.bottom", {"start": v(61.35, -37.9) * mm, "end": v(72.84, -37.9) * mm});
            skLineSegment(sketch, "E2343.top", {"start": v(61.35, -50.73) * mm, "end": v(72.84, -50.73) * mm});
            skLineSegment(sketch, "E2343.left", {"start": v(61.35, -37.9) * mm, "end": v(61.35, -50.73) * mm});
            skLineSegment(sketch, "E2343.right", {"start": v(72.84, -37.9) * mm, "end": v(72.84, -50.73) * mm});
            skLineSegment(sketch, "E2344.bottom", {"start": v(69.4, 42.09) * mm, "end": v(77.61, 42.09) * mm});
            skLineSegment(sketch, "E2344.top", {"start": v(69.4, 32.24) * mm, "end": v(77.61, 32.24) * mm});
            skLineSegment(sketch, "E2344.left", {"start": v(69.4, 42.09) * mm, "end": v(69.4, 32.24) * mm});
            skLineSegment(sketch, "E2344.right", {"start": v(77.61, 42.09) * mm, "end": v(77.61, 32.24) * mm});
            skSolve(sketch);
        }
        {
            var Q0;
            Q0 = qSketchRegion(id + "F4", true);
            extrude(context, id + "F5", {"entities" : qUnion([Q0]), "operationType" : NewBodyOperationType.ADD, "oppositeDirection" : true, "depth" : 7 * mm});
        }
    });
